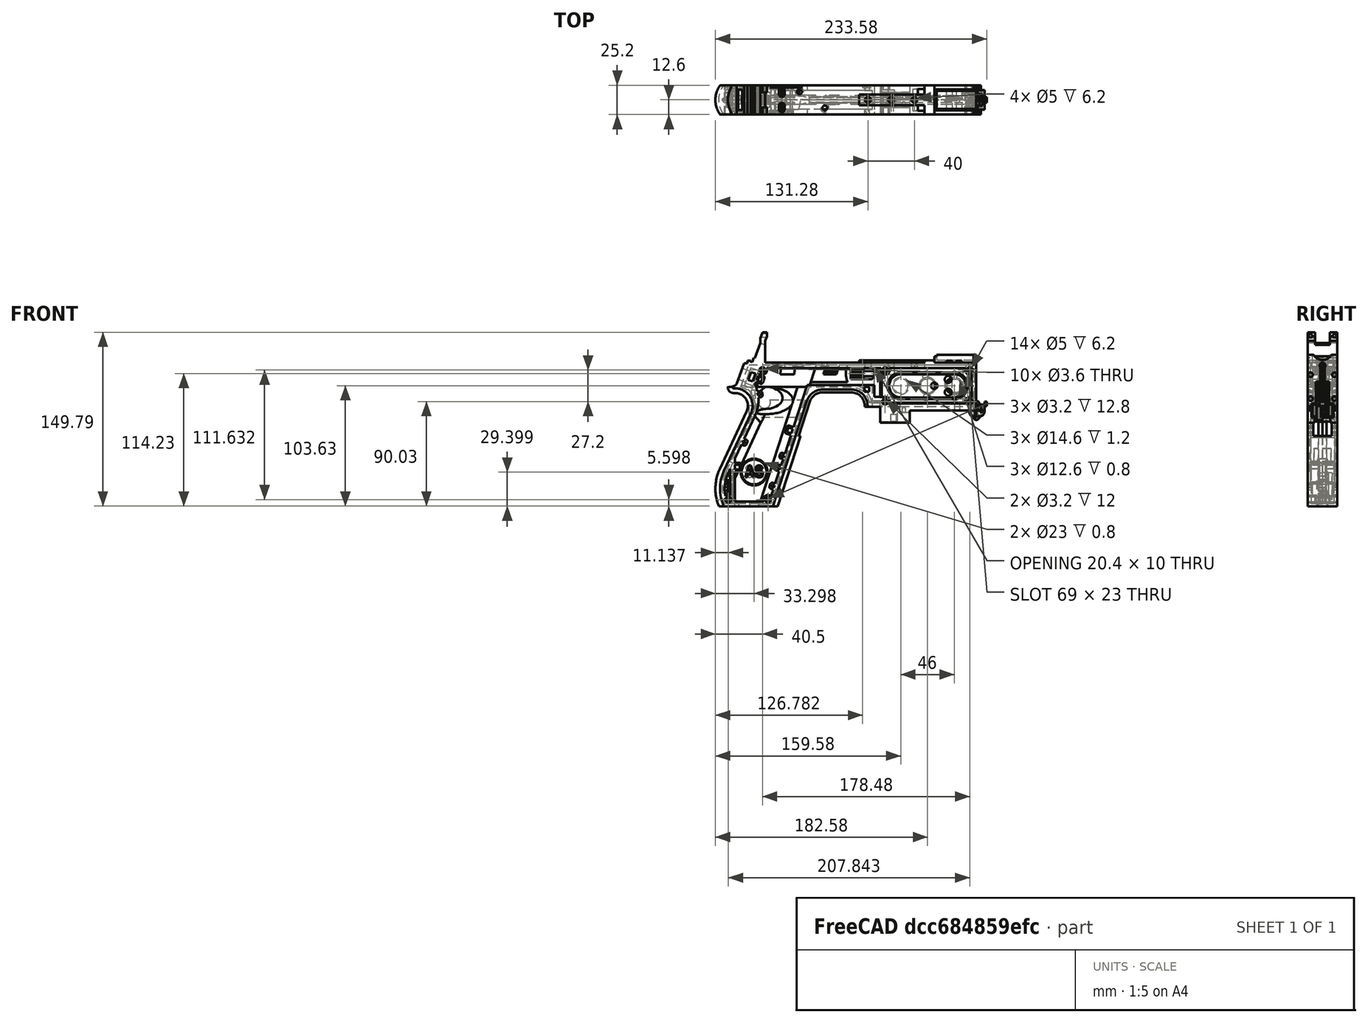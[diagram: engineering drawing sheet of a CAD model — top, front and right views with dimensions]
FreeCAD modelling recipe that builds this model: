
FCSTD DOCUMENT  (FreeCAD 1.0R39319 (Git))
Label: PICON-OF_ver_53
License: All rights reserved
LicenseURL: https://en.wikipedia.org/wiki/All_rights_reserved
objects: Sketcher::SketchObject×124, Part::Extrusion×63, Part::Cut×48, PartDesign::Pad×29, PartDesign::Pocket×21, PartDesign::Chamfer×15, PartDesign::Body×10, PartDesign::Fillet×6, Part::MultiFuse×5, Part::Part2DObjectPython×4, PartDesign::SubtractivePipe×4, PartDesign::SubtractiveLoft×4, PartDesign::Plane×3, PartDesign::SubShapeBinder×2, Part::Sweep×1, PartDesign::ShapeBinder×1, Mesh::Feature×1, PartDesign::Point×1, PartDesign::Groove×1
note: 626 computed .brp shape members not serialized (recipe doc carries the construction recipe); baked Part::Feature solids carry a one-line shape summary decoded from their .brp

FEATURE [Sketcher::SketchObject] Sketch  label="corpo principale"
  ArcFitTolerance = 1e-06
  AttacherType = Attacher::AttachEngine3D
  AttachmentSupport = -> [XZ_Plane]
  FullyConstrained = true
  MakeInternals = false
  MapMode = 5
  Placement = pos=(0,0,0) rot=(1,0,0;1.5708rad)
  sketch-geometry (65):
    g0: LineSegment StartX=0 StartY=0 StartZ=0 EndX=-57.2 EndY=0 EndZ=0
    g1: LineSegment StartX=-57.2 StartY=0 StartZ=0 EndX=-57.2 EndY=-10.4 EndZ=0
    g2: LineSegment StartX=-57.2 StartY=-10.4 StartZ=0 EndX=-82.8 EndY=-10.4 EndZ=0
    g3: LineSegment StartX=-82.8 StartY=-10.4 StartZ=0 EndX=-82.8 EndY=3.2 EndZ=0
    g4: LineSegment StartX=-82.8 StartY=3.2 StartZ=0 EndX=-93.6 EndY=3.2 EndZ=0
    g5: LineSegment StartX=-93.6 StartY=3.2 StartZ=0 EndX=-93.6 EndY=4 EndZ=0
    g6: LineSegment StartX=-107.6 StartY=18 StartZ=0 EndX=-132.428 EndY=18 EndZ=0
    g7: LineSegment StartX=-145.743 StartY=8.32624 StartZ=0 EndX=-175.232 EndY=-82.4316 EndZ=0
    g8: LineSegment StartX=-175.232 StartY=-82.4316 StartZ=0 EndX=-217.232 EndY=-82.4316 EndZ=0
    g9: LineSegment StartX=-217.232 StartY=-52.1862 StartZ=0 EndX=-193.988 EndY=-2.33927 EndZ=0
    g10: LineSegment StartX=-206.196 StartY=23.0857 StartZ=0 EndX=-199.861 EndY=40.4914 EndZ=0
    g11: LineSegment StartX=-199.861 StartY=40.4914 StartZ=0 EndX=-197.061 EndY=40.4914 EndZ=0
    g12: LineSegment StartX=-197.061 StartY=40.4914 StartZ=0 EndX=-197.061 EndY=42.8914 EndZ=0
    g13: LineSegment StartX=-197.061 StartY=42.8914 StartZ=0 EndX=-194.261 EndY=42.8914 EndZ=0
    g14: LineSegment StartX=-194.261 StartY=42.8914 StartZ=0 EndX=-194.535 EndY=42.1397 EndZ=0
    g15: LineSegment StartX=-194.535 StartY=42.1397 StartZ=0 EndX=-193.031 EndY=41.5924 EndZ=0
    g16: LineSegment StartX=-193.031 StartY=41.5924 StartZ=0 EndX=-191.663 EndY=45.3512 EndZ=0
    g17: LineSegment StartX=-191.663 StartY=45.3512 StartZ=0 EndX=-190.536 EndY=44.9408 EndZ=0
    g18: LineSegment StartX=-190.536 StartY=44.9408 StartZ=0 EndX=-185.747 EndY=58.0965 EndZ=0
    g19: LineSegment StartX=-185.747 StartY=58.0965 StartZ=0 EndX=-185.747 EndY=62.0965 EndZ=0
    g20: LineSegment StartX=-185.747 StartY=62.0965 StartZ=0 EndX=-183.832 EndY=67.3588 EndZ=0
    g21: LineSegment StartX=-183.832 StartY=67.3588 StartZ=0 EndX=-180.232 EndY=67.3588 EndZ=0
    g22: LineSegment StartX=-180.232 StartY=67.3588 StartZ=0 EndX=-180.232 EndY=63.7588 EndZ=0
    g23: LineSegment StartX=-180.232 StartY=63.7588 StartZ=0 EndX=-181.6 EndY=60 EndZ=0
    g24: LineSegment StartX=-181.6 StartY=60 StartZ=0 EndX=-181.6 EndY=41.2 EndZ=0
    g25: LineSegment StartX=-181.6 StartY=41.2 StartZ=0 EndX=-100.8 EndY=41.2 EndZ=0
    g26: LineSegment StartX=-36 StartY=43.2 StartZ=0 EndX=-36 EndY=41.2 EndZ=0
    g27: LineSegment StartX=0 StartY=48 StartZ=0 EndX=0 EndY=0 EndZ=0
    g28: LineSegment StartX=-209.901 StartY=19.85 StartZ=0 EndX=-209.901 EndY=20.1 EndZ=0
    g29: LineSegment StartX=-208.001 StartY=22 StartZ=0 EndX=-207.747 EndY=22 EndZ=0
    g30: LineSegment StartX=-207.583 StartY=19 StartZ=0 EndX=-209.051 EndY=19 EndZ=0
    g31: ArcOfCircle CenterX=-208.001 CenterY=20.1 CenterZ=0 NormalX=0 NormalY=0 NormalZ=1 AngleXU=0 Radius=1.9 StartAngle=1.5708 EndAngle=3.14159
    g32: GeomPoint [constr] X=-209.901 Y=22 Z=0
    g33: ArcOfCircle CenterX=-209.051 CenterY=19.85 CenterZ=0 NormalX=0 NormalY=0 NormalZ=1 AngleXU=0 Radius=0.85 StartAngle=3.14159 EndAngle=4.71239
    g34: GeomPoint [constr] X=-209.901 Y=19 Z=0
    g35: ArcOfCircle CenterX=-207.747 CenterY=23.65 CenterZ=0 NormalX=0 NormalY=0 NormalZ=1 AngleXU=0 Radius=1.65 StartAngle=4.71239 EndAngle=5.93412
    g36: GeomPoint [constr] X=-206.591 Y=22 Z=0
    g37: LineSegment StartX=-4 StartY=6 StartZ=0 EndX=-4 EndY=36.4 EndZ=0
    g38: LineSegment StartX=-4 StartY=36.4 StartZ=0 EndX=-185.2 EndY=36.4 EndZ=0
    g39: LineSegment StartX=-185.2 StartY=36.4 StartZ=0 EndX=-190.441 EndY=22 EndZ=0
    g40: LineSegment StartX=-214.575 StartY=-78.4316 StartZ=0 EndX=-178.142 EndY=-78.4316 EndZ=0
    g41: LineSegment StartX=-178.142 StartY=-78.4316 StartZ=0 EndX=-145.51 EndY=22 EndZ=0
    g42: LineSegment StartX=-145.51 StartY=22 StartZ=0 EndX=-87.91 EndY=22 EndZ=0
    g43: LineSegment StartX=-87.91 StartY=22 StartZ=0 EndX=-87.91 EndY=11.6 EndZ=0
    g44: LineSegment StartX=-87.91 StartY=11.6 StartZ=0 EndX=-80.11 EndY=11.6 EndZ=0
    g45: LineSegment StartX=-80.11 StartY=11.6 StartZ=0 EndX=-80.11 EndY=6 EndZ=0
    g46: LineSegment StartX=-80.11 StartY=6 StartZ=0 EndX=-4 EndY=6 EndZ=0
    g47: LineSegment StartX=-190.363 StartY=-4.02975 StartZ=0 EndX=-213.607 EndY=-53.8767 EndZ=0
    g48: ArcOfCircle CenterX=-132.428 CenterY=4 CenterZ=0 NormalX=0 NormalY=0 NormalZ=1 AngleXU=0 Radius=14 StartAngle=1.5708 EndAngle=2.82743
    g49: GeomPoint [constr] X=-142.6 Y=18 Z=0
    g50: ArcOfCircle CenterX=-107.6 CenterY=4 CenterZ=0 NormalX=0 NormalY=0 NormalZ=1 AngleXU=0 Radius=14 StartAngle=0 EndAngle=1.5708
    g51: GeomPoint [constr] X=-93.6 Y=18 Z=0
    g52: ArcOfCircle CenterX=-184.801 CenterY=-67.3089 CenterZ=0 NormalX=0 NormalY=0 NormalZ=1 AngleXU=0 Radius=35.7833 StartAngle=2.70526 EndAngle=3.57792
    g53: ArcOfCircle CenterX=-207.583 CenterY=4 CenterZ=0 NormalX=0 NormalY=0 NormalZ=1 AngleXU=0 Radius=15 StartAngle=5.84685 EndAngle=7.85398
    g54: LineSegment [constr] StartX=-213.607 StartY=-53.8767 StartZ=0 EndX=-217.232 EndY=-52.1862 EndZ=0
    g55: ArcOfCircle CenterX=-184.801 CenterY=-67.3089 CenterZ=0 NormalX=0 NormalY=0 NormalZ=1 AngleXU=0 Radius=31.7833 StartAngle=2.70526 EndAngle=3.49911
    g56: ArcOfCircle CenterX=-218.095 CenterY=8.90192 CenterZ=0 NormalX=0 NormalY=0 NormalZ=1 AngleXU=0 Radius=30.5989 StartAngle=5.84685 EndAngle=6.72553
    g57: LineSegment StartX=-44.6 StartY=43.2 StartZ=0 EndX=-36 EndY=43.2 EndZ=0
    g58: LineSegment StartX=-100.8 StartY=41.2 StartZ=0 EndX=-44.6 EndY=41.2 EndZ=0
    g59: LineSegment StartX=-44.6 StartY=41.2 StartZ=0 EndX=-44.6 EndY=43.2 EndZ=0
    g60: LineSegment StartX=-2.4 StartY=48 StartZ=0 EndX=0 EndY=48 EndZ=0
    g61: LineSegment StartX=-36 StartY=41.2 StartZ=0 EndX=-2.4 EndY=41.2 EndZ=0
    g62: LineSegment StartX=-2.4 StartY=41.2 StartZ=0 EndX=-2.4 EndY=48 EndZ=0
    g63: LineSegment [constr] StartX=-181.6 StartY=36.4 StartZ=0 EndX=-152.209 EndY=36.4 EndZ=0
    g64: LineSegment [constr] StartX=-181.6 StartY=36.4 StartZ=0 EndX=-130.41 EndY=36.4 EndZ=0
  constraints (183):
    c: Coincident(g-1,g0)
    c: PointOnObject(g0,g-1)
    c: Coincident(g0,g1)
    c: Vertical(g1)
    c: Coincident(g1,g2)
    c: Horizontal(g2)
    c: Coincident(g2,g3)
    c: Vertical(g3)
    c: Coincident(g3,g4)
    c: Coincident(g4,g5)
    c: Vertical(g5)
    c: Horizontal(g6)
    c: Coincident(g7,g8)
    c: Horizontal(g8)
    c: Coincident(g10,g11)
    c: Horizontal(g11)
    c: Coincident(g11,g12)
    c: Vertical(g12)
    c: Coincident(g12,g13)
    c: Horizontal(g13)
    c: Coincident(g13,g14)
    c: Coincident(g14,g15)
    c: Coincident(g15,g16)
    c: Coincident(g16,g17)
    c: Coincident(g17,g18)
    c: Coincident(g18,g19)
    c: Vertical(g19)
    c: Coincident(g19,g20)
    c: Coincident(g20,g21)
    c: Horizontal(g21)
    c: Coincident(g21,g22)
    c: Vertical(g22)
    c: Coincident(g22,g23)
    c: Coincident(g23,g24)
    c: Vertical(g24)
    c: Coincident(g24,g25)
    c: Horizontal(g25)
    c: Coincident(g57,g26)
    c: Vertical(g26)
    c: Coincident(g26,g61)
    c: PointOnObject(g60,g-2)
    c: Coincident(g60,g27)
    c: Coincident(g27,g0)
    c: DistanceY(g27,g27) = 48
    c: DistanceY(g1,g1) = 10.4
    c: DistanceX(g0,g0) = 57.2
    c: DistanceX(g2,g2) = 25.6
    c: Horizontal(g4)
    c: DistanceY(g3,g3) = 13.6
    c: DistanceX(g4,g4) = 10.8
    c: DistanceY(g5,g51) = 14.8
    c: DistanceX(g49,g51) = 49
    c: Distance(g7,g49) = 105.6
    c: DistanceX(g61,g60) = 36
    c: DistanceX(g25,g25) = 80.8
    c: DistanceY(g24,g24) = 18.8
    c: DistanceY(g22,g22) = 3.6
    c: Distance(g23) = 4
    c: Angle(g-1,g23) = 1.22173
    c: DistanceX(g21,g21) = 3.6
    c: Distance(g20) = 5.6
    c: Angle(g-1,g20) = 1.22173
    c: DistanceY(g19,g19) = 4
    c: Distance(g18) = 14
    c: Angle(g-1,g18) = 1.22173
    c: Distance(g17) = 1.2
    c: Distance(g16) = 4
    c: Angle(g16) = 1.22173
    c: Perpendicular(g18,g17)
    c: Distance(g15) = 1.6
    c: Perpendicular(g16,g15)
    c: Distance(g14) = 0.8
    c: DistanceX(g13,g13) = 2.8
    c: Perpendicular(g15,g14)
    c: DistanceY(g12,g12) = 2.4
    c: DistanceX(g11,g11) = 2.8
    c: Distance(g9) = 55
    c: Angle(g9,g-1) = 2.00713
    c: Horizontal(g29)
    c: Vertical(g28)
    c: Horizontal(g30)
    c: PointOnObject(g32,g29)
    c: PointOnObject(g32,g28)
    c: Tangent(g29,g31) = 1.5708
    c: Tangent(g28,g31) = 1.5708
    c: PointOnObject(g34,g28)
    c: PointOnObject(g34,g30)
    c: Tangent(g28,g33) = 1.5708
    c: Tangent(g30,g33) = 1.5708
    c: PointOnObject(g36,g29)
    c: PointOnObject(g36,g10)
    c: Tangent(g29,g35) = -1.5708
    c: Tangent(g10,g35) = -1.5708
    c: Angle(g-1,g10) = 1.22173
    c: Radius(g35) = 1.65
    c: Vertical(g37)
    c: Coincident(g37,g38)
    c: Horizontal(g38)
    c: Coincident(g38,g39)
    c: Horizontal(g40)
    c: Coincident(g40,g41)
    c: Coincident(g41,g42)
    c: Horizontal(g42)
    c: Coincident(g42,g43)
    c: Vertical(g43)
    c: Coincident(g43,g44)
    c: Horizontal(g44)
    c: Coincident(g44,g45)
    c: Vertical(g45)
    c: Coincident(g45,g46)
    c: Coincident(g46,g37)
    c: Horizontal(g46)
    c: DistanceY(g0,g37) = 6
    c: DistanceX(g37,g0) = 4
    c: DistanceY(g37,g25) = 4.8
    c: DistanceX(g38,g38) = 181.2
    c: DistanceX(g42,g42) = 57.6
    c: DistanceY(g49,g41) = 4
    c: DistanceX(g41,g49) = 2.91
    c: DistanceY(g43,g43) = 10.4
    c: DistanceX(g44,g44) = 7.8
    c: DistanceY(g7,g40) = 4
    c: Distance(g47) = 55
    c: Angle(g-1,g39) = 1.22173
    c: PointOnObject(g49,g7)
    c: PointOnObject(g49,g6)
    c: Tangent(g7,g48) = -1.5708
    c: Tangent(g6,g48) = -1.5708
    c: PointOnObject(g51,g5)
    c: PointOnObject(g51,g6)
    c: Tangent(g5,g50) = -1.5708
    c: Tangent(g6,g50) = -1.5708
    c: Radius(g50) = 14
    c: Radius(g48) = 14
    c: DistanceX(g8,g8) = 42
    c: Angle(g7,g-1) = 1.88496
    c: Parallel(g41,g7)
    c: Parallel(g47,g9)
    c: Coincident(g52,g8)
    c: Tangent(g52,g9) = 1.5708
    c: DistanceX(g9,g8) = 0
    c: Tangent(g53,g9) = -1.5708
    c: Tangent(g53,g30) = -1.5708
    c: Diameter(g53) = 30
    c: DistanceY(g53,g0) = -4
    c: Coincident(g54,g47)
    c: Distance(g54) = 4
    c: Coincident(g54,g9)
    c: Coincident(g55,g40)
    c: Tangent(g55,g47) = -1.5708
    c: Coincident(g52,g55)
    c: Coincident(g56,g39)
    c: Tangent(g56,g47) = 1.5708
    c: Horizontal(g57)
    c: DistanceX(g57,g57) = 8.6
    c: Coincident(g58,g25)
    c: Horizontal(g58)
    c: Coincident(g59,g58)
    c: Vertical(g59)
    c: DistanceY(g58,g57) = 2
    c: DistanceX(g58,g58) = 56.2
    c: Coincident(g59,g57)
    c: DistanceY(g41,g36) = 0
    c: DistanceY(g36,g39) = 0
    c: DistanceY(g28,g28) = 0.25
    c: DistanceX(g30,g36) = 2.46
    c: DistanceX(g28,g29) = 1.9
    c: Coincident(g62,g60)
    c: Horizontal(g60)
    c: DistanceX(g62,g27) = 2.4
    c: Coincident(g61,g62)
    c: DistanceY(g26,g26) = 2
    c: Vertical(g62)
    c: DistanceY(g61,g60) = 6.8
    c: Horizontal(g61)
    c: Distance(g63) = 29.391
    c: PointOnObject(g63,g38)
    c: PointOnObject(g63,g38)
    c: Distance(g64) = 51.19
    c: PointOnObject(g64,g38)
    c: PointOnObject(g64,g38)
    c: DistanceX(g24,g63) = 0
    c: DistanceX(g24,g64) = 0
FEATURE [Part::Extrusion] Extrude  label="Extrude corpo principale"
  Base = -> Sketch
  Dir = (0,-1,2e-16)
  DirMode = 2
  FaceMakerClass = Part::FaceMakerBullseye
  FaceMakerMode = 3
  LengthFwd = 25.2
  LengthRev = 12.6
  Solid = true
  Symmetric = true
FEATURE [Sketcher::SketchObject] Sketch002  label="scavo grilletto"
  ArcFitTolerance = 1e-06
  AttachmentSupport = -> [XZ_Plane]
  ExternalGeometry = -> [Sketch]
  FullyConstrained = true
  MakeInternals = false
  MapMode = 5
  Placement = pos=(0,0,0) rot=(1,0,0;1.5708rad)
  sketch-geometry (4):
    g0: LineSegment StartX=-89.51 StartY=22 StartZ=0 EndX=-152.71 EndY=22 EndZ=0
    g1: LineSegment StartX=-152.71 StartY=22 StartZ=0 EndX=-167.006 EndY=-22 EndZ=0
    g2: LineSegment StartX=-167.006 StartY=-22 StartZ=0 EndX=-89.51 EndY=-22 EndZ=0
    g3: LineSegment StartX=-89.51 StartY=-22 StartZ=0 EndX=-89.51 EndY=22 EndZ=0
  constraints (12):
    c: Horizontal(g0)
    c: Coincident(g0,g1)
    c: Coincident(g1,g2)
    c: Horizontal(g2)
    c: Coincident(g2,g3)
    c: Coincident(g3,g0)
    c: Vertical(g3)
    c: Angle(g1,g0) = 1.88496
    c: DistanceY(g3,g3) = 44
    c: DistanceX(g0,g0) = 63.2
    c: DistanceX(g0,g-3) = 1.6
    c: DistanceY(g-3,g0) = 0
FEATURE [Sketcher::SketchObject] Sketch004  label="traiettoria arrotondamento impugnatura anteriore"
  ArcFitTolerance = 1e-06
  AttachmentSupport = -> [XZ_Plane]
  ExternalGeometry = -> [Sketch]
  FullyConstrained = true
  MakeInternals = false
  MapMode = 5
  Placement = pos=(0,0,0) rot=(1,0,0;1.5708rad)
  sketch-geometry (13):
    g0: LineSegment StartX=-175.232 StartY=-82.4316 StartZ=0 EndX=-145.743 EndY=8.32624 EndZ=0
    g1: LineSegment StartX=-93.6 StartY=3.2 StartZ=0 EndX=-93.6 EndY=4 EndZ=0
    g2: LineSegment StartX=-132.428 StartY=18 StartZ=0 EndX=-107.6 EndY=18 EndZ=0
    g3: ArcOfCircle CenterX=-132.428 CenterY=4 CenterZ=0 NormalX=0 NormalY=0 NormalZ=1 AngleXU=0 Radius=14 StartAngle=1.5708 EndAngle=2.82743
    g4: ArcOfCircle CenterX=-107.6 CenterY=4 CenterZ=0 NormalX=0 NormalY=0 NormalZ=1 AngleXU=0 Radius=14 StartAngle=0 EndAngle=1.5708
    g5: LineSegment StartX=-175.232 StartY=-82.4316 StartZ=0 EndX=-217.232 EndY=-82.4316 EndZ=0
    g6: LineSegment StartX=-217.232 StartY=-52.1862 StartZ=0 EndX=-193.988 EndY=-2.33927 EndZ=0
    g7: LineSegment StartX=-209.051 StartY=19 StartZ=0 EndX=-207.583 EndY=19 EndZ=0
    g8: LineSegment StartX=-209.901 StartY=20.1 StartZ=0 EndX=-209.901 EndY=19.85 EndZ=0
    g9: ArcOfCircle CenterX=-184.801 CenterY=-67.3089 CenterZ=0 NormalX=0 NormalY=0 NormalZ=1 AngleXU=0 Radius=35.7833 StartAngle=2.70526 EndAngle=3.57792
    g10: ArcOfCircle CenterX=-207.583 CenterY=4 CenterZ=0 NormalX=0 NormalY=0 NormalZ=1 AngleXU=0 Radius=15 StartAngle=5.84685 EndAngle=7.85398
    g11: ArcOfCircle CenterX=-209.051 CenterY=19.85 CenterZ=0 NormalX=0 NormalY=0 NormalZ=1 AngleXU=0 Radius=0.85 StartAngle=3.14159 EndAngle=4.71239
    g12: ArcOfCircle CenterX=-208.001 CenterY=20.1 CenterZ=0 NormalX=0 NormalY=0 NormalZ=1 AngleXU=0 Radius=1.9 StartAngle=1.5708 EndAngle=3.14159
  constraints (26):
    c: Coincident(g0,g-3)
    c: Coincident(g0,g-6)
    c: Coincident(g1,g-8)
    c: Coincident(g1,g-7)
    c: Coincident(g2,g-5)
    c: Coincident(g2,g-4)
    c: Coincident(g3,g2)
    c: Tangent(g3,g0) = 1.5708
    c: Coincident(g4,g1)
    c: Tangent(g4,g2) = 1.5708
    c: Coincident(g5,g0)
    c: Coincident(g5,g-9)
    c: Coincident(g6,g-12)
    c: Coincident(g6,g-11)
    c: Coincident(g7,g-15)
    c: Coincident(g7,g-14)
    c: Coincident(g8,g-16)
    c: Coincident(g8,g-17)
    c: Tangent(g9,g6) = 1.5708
    c: Coincident(g9,g5)
    c: Coincident(g10,g7)
    c: Tangent(g10,g6) = -1.5708
    c: Tangent(g11,g7) = -1.5708
    c: Coincident(g11,g8)
    c: Tangent(g12,g8) = -1.5708
    c: Coincident(g12,g-17)
FEATURE [PartDesign::Plane] DatumPlane  label="Piano per disegno arrotondamento impugnatura"
  AttachmentSupport = -> [Sketch]
  Length = 73.6581
  MapMode = 7
  Placement = pos=(-145.743,1.8e-15,8.32624) rot=(0.154555,0.154555,0.97582;1.59527rad)
  ResizeMode = 0
  Width = 303.511
FEATURE [Sketcher::SketchObject] Sketch005  label="forma arrotondamento impugnatura anteriore"
  ArcFitTolerance = 1e-06
  AttachmentSupport = -> [DatumPlane]
  FullyConstrained = true
  MakeInternals = false
  MapMode = 5
  Placement = pos=(-145.743,1.8e-15,8.32624) rot=(0.154555,0.154555,0.97582;1.59527rad)
  sketch-geometry (5):
    g0: GeomPoint [constr] X=0 Y=-4 Z=0
    g1: GeomPoint [constr] X=-12.6 Y=7.1e-15 Z=0
    g2: GeomPoint [constr] X=12.6 Y=4.97e-14 Z=0
    g3: LineSegment StartX=-12.6 StartY=7.1e-15 StartZ=0 EndX=12.6 EndY=4.97e-14 EndZ=0
    g4: ArcOfCircle CenterX=-3.88e-14 CenterY=17.845 CenterZ=0 NormalX=0 NormalY=0 NormalZ=1 AngleXU=0 Radius=21.845 StartAngle=4.09759 EndAngle=5.32718
  constraints (11):
    c: DistanceY(g0,g-1) = 4
    c: DistanceX(g-1,g0) = 0
    c: DistanceX(g1,g-1) = 12.6
    c: DistanceX(g-1,g2) = 12.6
    c: DistanceY(g-1,g2) = 0
    c: DistanceY(g-1,g1) = 0
    c: Coincident(g3,g1)
    c: Coincident(g3,g2)
    c: Coincident(g4,g1)
    c: Coincident(g4,g2)
    c: PointOnObject(g0,g4)
FEATURE [Part::Sweep] Sweep  label="Sweep impugnatura"
  Frenet = true
  Sections = -> [Sketch005]
  Solid = true
  Spine = -> Sketch [Edge32,Edge33,Edge34,Edge35,Edge36,Edge37,Edge38,Edge39,Edge40,Edge41,Edge42,Edge43,Edge44]
  Transition = 1
FEATURE [Sketcher::SketchObject] Sketch008  label="buchi e pulizie varie"
  ArcFitTolerance = 1e-06
  AttachmentSupport = -> [XZ_Plane]
  ExternalGeometry = -> [Sketch]
  FullyConstrained = true
  MakeInternals = false
  MapMode = 5
  Placement = pos=(0,0,0) rot=(1,0,0;1.5708rad)
  sketch-geometry (26):
    g0: LineSegment StartX=-96.278 StartY=20.155 StartZ=0 EndX=-92.278 EndY=20.155 EndZ=0
    g1: LineSegment StartX=-92.278 StartY=20.155 StartZ=0 EndX=-92.278 EndY=16.155 EndZ=0
    g2: LineSegment StartX=-92.278 StartY=16.155 StartZ=0 EndX=-96.278 EndY=16.155 EndZ=0
    g3: LineSegment StartX=-96.278 StartY=16.155 StartZ=0 EndX=-96.278 EndY=20.155 EndZ=0
    g4: LineSegment StartX=-222.232 StartY=-82.4316 StartZ=0 EndX=-170.232 EndY=-82.4316 EndZ=0
    g5: LineSegment StartX=-170.232 StartY=-82.4316 StartZ=0 EndX=-170.232 EndY=-86.4316 EndZ=0
    g6: LineSegment StartX=-170.232 StartY=-86.4316 StartZ=0 EndX=-222.232 EndY=-86.4316 EndZ=0
    g7: LineSegment StartX=-222.232 StartY=-86.4316 StartZ=0 EndX=-222.232 EndY=-82.4316 EndZ=0
    g8: LineSegment StartX=-213.901 StartY=20.1 StartZ=0 EndX=-213.901 EndY=26 EndZ=0
    g9: LineSegment StartX=-213.901 StartY=26 StartZ=0 EndX=-206.196 EndY=26 EndZ=0
    g10: LineSegment StartX=-17.4 StartY=42.8 StartZ=0 EndX=-12.4 EndY=42.8 EndZ=0
    g11: LineSegment StartX=-12.4 StartY=42.8 StartZ=0 EndX=-12.4 EndY=41.2 EndZ=0
    g12: LineSegment StartX=-12.4 StartY=41.2 StartZ=0 EndX=-17.4 EndY=41.2 EndZ=0
    g13: LineSegment StartX=-17.4 StartY=41.2 StartZ=0 EndX=-17.4 EndY=42.8 EndZ=0
    g14: LineSegment StartX=-25.9 StartY=42.8 StartZ=0 EndX=-20.9 EndY=42.8 EndZ=0
    g15: LineSegment StartX=-20.9 StartY=42.8 StartZ=0 EndX=-20.9 EndY=41.2 EndZ=0
    g16: LineSegment StartX=-20.9 StartY=41.2 StartZ=0 EndX=-25.9 EndY=41.2 EndZ=0
    g17: LineSegment StartX=-25.9 StartY=41.2 StartZ=0 EndX=-25.9 EndY=42.8 EndZ=0
    g18: GeomPoint [constr] X=-206.196 Y=23.0857 Z=0
    g19: GeomPoint [constr] X=-213.901 Y=20.1 Z=0
    g20: BSplineCurve PolesCount=4 KnotsCount=2 Degree=3 IsPeriodic=0
    g21-g24: Circle [constr] x4 (B-spline internal-alignment scaffolding for g20; pole/knot coordinates omitted)
    g25: LineSegment StartX=-206.196 StartY=26 StartZ=0 EndX=-206.196 EndY=23.0857 EndZ=0
  constraints (73):
    c: Horizontal(g0)
    c: Coincident(g1,g0)
    c: Vertical(g1)
    c: Coincident(g2,g1)
    c: Horizontal(g2)
    c: Coincident(g3,g2)
    c: Coincident(g3,g0)
    c: Vertical(g3)
    c: DistanceX(g0,g-4) = 4.368
    c: DistanceY(g0,g-4) = 1.845
    c: DistanceY(g1,g1) = 4
    c: DistanceX(g2,g2) = 4
    c: Horizontal(g4)
    c: Coincident(g5,g4)
    c: Vertical(g5)
    c: Coincident(g6,g5)
    c: Horizontal(g6)
    c: Coincident(g7,g6)
    c: Coincident(g7,g4)
    c: Vertical(g7)
    c: DistanceY(g7,g7) = 4
    c: DistanceX(g4,g-5) = 5
    c: DistanceX(g-5,g4) = 5
    c: DistanceY(g4,g-5) = 0
    c: Coincident(g9,g8)
    c: Parallel(g9,g-6)
    c: DistanceX(g8,g-8) = 4
    c: Horizontal(g10)
    c: Coincident(g11,g10)
    c: Vertical(g11)
    c: Coincident(g12,g11)
    c: Horizontal(g12)
    c: Coincident(g13,g12)
    c: Coincident(g13,g10)
    c: Vertical(g13)
    c: Horizontal(g14)
    c: Coincident(g15,g14)
    c: Vertical(g15)
    c: Coincident(g16,g15)
    c: Horizontal(g16)
    c: Coincident(g17,g16)
    c: Coincident(g17,g14)
    c: Vertical(g17)
    c: DistanceY(g11,g10) = 1.6
    c: DistanceX(g10,g10) = 5
    c: DistanceY(g15,g14) = 1.6
    c: DistanceX(g14,g14) = 5
    c: DistanceX(g15,g12) = 3.5
    c: DistanceX(g11,g-9) = 10
    c: DistanceY(g-9,g11) = 0
    c: DistanceY(g-9,g15) = 0
    c: Perpendicular(g8,g9)
    c: DistanceY(g-7,g9) = 4
    c: DistanceY(g8,g-8) = 0
    c: InternalAlignment(g18,g20)
    c: InternalAlignment(g19,g20)
    c: InternalAlignment(g21,g20)
    c: Weight(g21) = 1
    c: InternalAlignment(g22,g20)
    c: Equal(g22,g21)
    c: InternalAlignment(g23,g20)
    c: Equal(g23,g21)
    c: InternalAlignment(g24,g20)
    c: Equal(g24,g21)
    c: Coincident(g18,g-12)
    c: Coincident(g19,g8)
    c: Coincident(g25,g9)
    c: Coincident(g25,g20)
    c: Vertical(g25)
    c: DistanceY(g20,g23) = 0
    c: DistanceY(g22,g18) = 2.26
    c: DistanceX(g22,g18) = 0.93
    c: DistanceX(g20,g23) = 2.9
FEATURE [Part::Extrusion] Extrude004  label="Extrude Buchi e pulizie varie"
  Base = -> Sketch008
  Dir = (0,-1,2e-16)
  DirMode = 2
  FaceMakerClass = Part::FaceMakerBullseye
  FaceMakerMode = 3
  LengthFwd = 25.2
  LengthRev = 0
  Solid = true
  Symmetric = true
FEATURE [Sketcher::SketchObject] Sketch009  label="rinforzi"
  ArcFitTolerance = 1e-06
  AttachmentSupport = -> [XZ_Plane]
  ExternalGeometry = -> [Sketch]
  FullyConstrained = true
  MakeInternals = false
  MapMode = 5
  Placement = pos=(0,0,0) rot=(1,0,0;1.5708rad)
  sketch-geometry (9):
    g0: LineSegment StartX=-87.91 StartY=22 StartZ=0 EndX=-87.91 EndY=36.4 EndZ=0
    g1: LineSegment StartX=-87.91 StartY=36.4 StartZ=0 EndX=-97.91 EndY=36.4 EndZ=0
    g2: LineSegment StartX=-97.91 StartY=36.4 StartZ=0 EndX=-97.91 EndY=22 EndZ=0
    g3: LineSegment StartX=-97.91 StartY=22 StartZ=0 EndX=-87.91 EndY=22 EndZ=0
    g4: LineSegment StartX=-149.713 StartY=9.06563 StartZ=0 EndX=-154.586 EndY=-5.93437 EndZ=0
    g5: LineSegment StartX=-154.586 StartY=-5.93437 StartZ=0 EndX=-191.863 EndY=-5.93437 EndZ=0
    g6: LineSegment StartX=-191.863 StartY=-5.93437 StartZ=0 EndX=-191.863 EndY=9.06563 EndZ=0
    g7: LineSegment StartX=-191.863 StartY=9.06563 StartZ=0 EndX=-149.713 EndY=9.06563 EndZ=0
    g8: LineSegment [constr] StartX=-145.51 StartY=22 StartZ=0 EndX=-149.713 EndY=9.06563 EndZ=0
  constraints (25):
    c: Vertical(g0)
    c: Coincident(g1,g0)
    c: Horizontal(g1)
    c: Coincident(g2,g1)
    c: Vertical(g2)
    c: Coincident(g3,g2)
    c: Coincident(g3,g0)
    c: Horizontal(g3)
    c: Coincident(g0,g-4)
    c: DistanceX(g3,g3) = 10
    c: DistanceY(g0,g-3) = 0
    c: Coincident(g5,g4)
    c: Horizontal(g5)
    c: Coincident(g6,g5)
    c: Vertical(g6)
    c: Coincident(g7,g6)
    c: Coincident(g7,g4)
    c: Horizontal(g7)
    c: Distance(g8) = 13.6
    c: Parallel(g-6,g8)
    c: Coincident(g-6,g8)
    c: Parallel(g4,g-6)
    c: DistanceY(g4,g4) = 15
    c: Coincident(g4,g8)
    c: DistanceX(g-5,g5) = -1.5
FEATURE [Part::Extrusion] Extrude001  label="Extrude scavo grilletto"
  Base = -> Sketch002
  Dir = (0,-1,2e-16)
  DirMode = 2
  FaceMakerClass = Part::FaceMakerBullseye
  FaceMakerMode = 3
  LengthFwd = 16
  LengthRev = 0
  Solid = true
  Symmetric = true
FEATURE [Part::Extrusion] Extrude005  label="Extrude Rinforzi"
  Base = -> Sketch009
  Dir = (0,-1,2e-16)
  DirMode = 2
  FaceMakerClass = Part::FaceMakerBullseye
  FaceMakerMode = 3
  LengthFwd = 2
  LengthRev = 0
  Placement = pos=(0,12.6,0) rot=(0,0,1;0rad)
  Solid = true
  Symmetric = false
FEATURE [PartDesign::ShapeBinder] CopyCut
  TraceSupport = false
FEATURE [PartDesign::Plane] DatumPlane001
  AttachmentSupport = -> [CopyCut]
  Length = 283.944
  MapMode = 5
  Placement = pos=(0,12.6,0) rot=(0,0.707107,0.707107;3.14159rad)
  ResizeMode = 0
  Width = 188.15
FEATURE [Sketcher::SketchObject] Sketch010  label="buco neopixel"
  ArcFitTolerance = 1e-06
  AttachmentSupport = -> [XZ_Plane]
  ExternalGeometry = -> [Sketch]
  FullyConstrained = true
  MakeInternals = false
  MapMode = 5
  Placement = pos=(0,0,0) rot=(1,0,0;1.5708rad)
  sketch-geometry (5):
    g0: LineSegment [constr] StartX=-199.861 StartY=40.4914 StartZ=0 EndX=-201.368 EndY=36.3521 EndZ=0
    g1: LineSegment StartX=-201.368 StartY=36.3521 StartZ=0 EndX=-204.932 EndY=26.5605 EndZ=0
    g2: LineSegment StartX=-201.368 StartY=36.3521 StartZ=0 EndX=-180.2 EndY=28.6477 EndZ=0
    g3: LineSegment StartX=-180.2 StartY=28.6477 StartZ=0 EndX=-183.764 EndY=18.8561 EndZ=0
    g4: LineSegment StartX=-183.764 StartY=18.8561 StartZ=0 EndX=-204.932 EndY=26.5605 EndZ=0
  constraints (14):
    c: Parallel(g0,g-3)
    c: Distance(g0) = 4.405
    c: Coincident(g0,g-3)
    c: Coincident(g2,g1)
    c: Coincident(g3,g2)
    c: Coincident(g4,g3)
    c: Coincident(g4,g1)
    c: Parallel(g1,g-3)
    c: Distance(g1) = 10.42
    c: Coincident(g1,g0)
    c: Parallel(g2,g4)
    c: Perpendicular(g1,g2)
    c: DistanceX(g-4,g2) = 5
    c: Parallel(g3,g1)
FEATURE [Part::Extrusion] Extrude006  label="Extrude buco neopixel"
  Base = -> Sketch010
  Dir = (0,-1,2e-16)
  DirMode = 2
  FaceMakerClass = Part::FaceMakerBullseye
  FaceMakerMode = 3
  LengthFwd = 17.2
  LengthRev = 0
  Solid = true
  Symmetric = true
FEATURE [Sketcher::SketchObject] Sketch011  label="fermo grilletto"
  ArcFitTolerance = 1e-06
  AttachmentSupport = -> [XZ_Plane]
  ExternalGeometry = -> [Sketch]
  FullyConstrained = true
  MakeInternals = false
  MapMode = 5
  Placement = pos=(0,0,0) rot=(1,0,0;1.5708rad)
  sketch-geometry (18):
    g0: LineSegment [constr] StartX=-145.51 StartY=22 StartZ=0 EndX=-157.347 EndY=-14.4293 EndZ=0
    g1: LineSegment [constr] StartX=-157.347 StartY=-14.4293 StartZ=0 EndX=-157.841 EndY=-15.951 EndZ=0
    g2: LineSegment StartX=-161.151 StartY=-13.1932 StartZ=0 EndX=-155.825 EndY=-14.9237 EndZ=0
    g3: LineSegment StartX=-163.167 StartY=-14.2205 StartZ=0 EndX=-164.403 EndY=-18.0247 EndZ=0
    g4: LineSegment StartX=-163.376 StartY=-20.0408 StartZ=0 EndX=-158.05 EndY=-21.7713 EndZ=0
    g5: LineSegment StartX=-158.05 StartY=-21.7713 StartZ=0 EndX=-155.825 EndY=-14.9237 EndZ=0
    g6: LineSegment StartX=-161.645 StartY=-14.7149 StartZ=0 EndX=-157.841 EndY=-15.951 EndZ=0
    g7: LineSegment StartX=-157.841 StartY=-15.951 StartZ=0 EndX=-159.077 EndY=-19.7552 EndZ=0
    g8: LineSegment StartX=-159.077 StartY=-19.7552 StartZ=0 EndX=-162.881 EndY=-18.5191 EndZ=0
    g9: LineSegment StartX=-162.881 StartY=-18.5191 StartZ=0 EndX=-161.645 EndY=-14.7149 EndZ=0
    g10: LineSegment [constr] StartX=-161.645 StartY=-14.7149 StartZ=0 EndX=-161.151 EndY=-13.1932 EndZ=0
    g11: LineSegment [constr] StartX=-159.077 StartY=-19.7552 StartZ=0 EndX=-157.555 EndY=-20.2496 EndZ=0
    g12: LineSegment [constr] StartX=-159.077 StartY=-19.7552 StartZ=0 EndX=-159.572 EndY=-21.2769 EndZ=0
    g13: LineSegment [constr] StartX=-161.645 StartY=-14.7149 StartZ=0 EndX=-163.167 EndY=-14.2205 EndZ=0
    g14: ArcOfCircle CenterX=-161.645 CenterY=-14.7149 CenterZ=0 NormalX=0 NormalY=0 NormalZ=1 AngleXU=0 Radius=1.6 StartAngle=1.25664 EndAngle=2.82743
    g15: GeomPoint [constr] X=-162.673 Y=-12.6988 Z=0
    g16: ArcOfCircle CenterX=-162.881 CenterY=-18.5191 CenterZ=0 NormalX=0 NormalY=0 NormalZ=1 AngleXU=0 Radius=1.6 StartAngle=2.82743 EndAngle=4.39823
    g17: GeomPoint [constr] X=-164.897 Y=-19.5464 Z=0
  constraints (48):
    c: Parallel(g0,g-3)
    c: Distance(g0) = 38.304
    c: Coincident(g0,g-3)
    c: Parallel(g1,g-3)
    c: Distance(g1) = 1.6
    c: Coincident(g1,g0)
    c: Coincident(g5,g4)
    c: Coincident(g5,g2)
    c: Coincident(g7,g6)
    c: Coincident(g8,g7)
    c: Coincident(g9,g8)
    c: Coincident(g9,g6)
    c: Parallel(g7,g-3)
    c: Parallel(g9,g7)
    c: Perpendicular(g6,g7)
    c: Parallel(g6,g8)
    c: Distance(g6) = 4
    c: Distance(g9) = 4
    c: Parallel(g5,g7)
    c: Parallel(g9,g3)
    c: Parallel(g2,g6)
    c: Parallel(g4,g8)
    c: Parallel(g13,g6)
    c: Parallel(g10,g9)
    c: Parallel(g11,g8)
    c: Parallel(g12,g7)
    c: Distance(g10) = 1.6
    c: Distance(g13) = 1.6
    c: Distance(g12) = 1.6
    c: Distance(g11) = 1.6
    c: Coincident(g10,g6)
    c: Coincident(g13,g6)
    c: Coincident(g12,g7)
    c: Coincident(g11,g7)
    c: Distance(g10,g15) = 1.6
    c: Distance(g15,g13) = 1.6
    c: Distance(g4,g12) = 1.6
    c: Distance(g4,g11) = 1.6
    c: PointOnObject(g15,g2)
    c: Tangent(g3,g14) = -1.5708
    c: Tangent(g2,g14) = 1.5708
    c: PointOnObject(g17,g4)
    c: PointOnObject(g17,g3)
    c: Tangent(g4,g16) = -1.5708
    c: Tangent(g3,g16) = -1.5708
    c: Equal(g16,g14)
    c: Coincident(g16,g8)
    c: Coincident(g6,g1)
FEATURE [Part::Extrusion] Extrude007  label="Extrude fermo grilletto"
  Base = -> Sketch011
  Dir = (0,-1,2e-16)
  DirMode = 2
  FaceMakerClass = Part::FaceMakerBullseye
  FaceMakerMode = 3
  LengthFwd = 25.2
  LengthRev = 0
  Solid = true
  Symmetric = true
FEATURE [Sketcher::SketchObject] Sketch012  label="buco oled"
  ArcFitTolerance = 1e-06
  AttachmentSupport = -> [XZ_Plane]
  ExternalGeometry = -> [Sketch]
  FullyConstrained = true
  MakeInternals = false
  MapMode = 5
  Placement = pos=(0,0,0) rot=(1,0,0;1.5708rad)
  sketch-geometry (4):
    g0: LineSegment StartX=-185.747 StartY=58.0965 StartZ=0 EndX=-180.232 EndY=56.0891 EndZ=0
    g1: LineSegment StartX=-185.747 StartY=58.0965 StartZ=0 EndX=-185.747 EndY=67.3588 EndZ=0
    g2: LineSegment StartX=-185.747 StartY=67.3588 StartZ=0 EndX=-180.232 EndY=67.3588 EndZ=0
    g3: LineSegment StartX=-180.232 StartY=67.3588 StartZ=0 EndX=-180.232 EndY=56.0891 EndZ=0
  constraints (10):
    c: Coincident(g1,g0)
    c: Coincident(g2,g1)
    c: Coincident(g3,g2)
    c: Coincident(g3,g0)
    c: Parallel(g1,g-5)
    c: Perpendicular(g-3,g0)
    c: Parallel(g2,g-6)
    c: Parallel(g3,g-4)
    c: Coincident(g0,g-5)
    c: Coincident(g2,g-6)
FEATURE [Part::Extrusion] Extrude008  label="Extrude buco oled"
  Base = -> Sketch012
  Dir = (0,-1,2e-16)
  DirMode = 2
  FaceMakerClass = Part::FaceMakerBullseye
  FaceMakerMode = 3
  LengthFwd = 12.8
  LengthRev = 0
  Solid = true
  Symmetric = true
FEATURE [Sketcher::SketchObject] Sketch013  label="buco pompa"
  ArcFitTolerance = 1e-06
  AttachmentSupport = -> [XZ_Plane]
  ExternalGeometry = -> [Sketch]
  FullyConstrained = true
  MakeInternals = false
  MapMode = 5
  Placement = pos=(0,0,0) rot=(1,0,0;1.5708rad)
  sketch-geometry (8):
    g0: LineSegment StartX=-82.8 StartY=-10.4 StartZ=0 EndX=-82.8 EndY=-9.6 EndZ=0
    g1: LineSegment StartX=-82.8 StartY=-9.6 StartZ=0 EndX=-67.9 EndY=-9.6 EndZ=0
    g2: LineSegment StartX=-67.9 StartY=-9.6 StartZ=0 EndX=-67.9 EndY=6 EndZ=0
    g3: LineSegment StartX=-67.9 StartY=6 StartZ=0 EndX=-65.9 EndY=6 EndZ=0
    g4: LineSegment StartX=-65.9 StartY=6 StartZ=0 EndX=-65.9 EndY=-1.7 EndZ=0
    g5: LineSegment StartX=-65.9 StartY=-1.7 StartZ=0 EndX=-57.2 EndY=-1.7 EndZ=0
    g6: LineSegment StartX=-57.2 StartY=-1.7 StartZ=0 EndX=-57.2 EndY=-10.4 EndZ=0
    g7: LineSegment StartX=-57.2 StartY=-10.4 StartZ=0 EndX=-82.8 EndY=-10.4 EndZ=0
  constraints (22):
    c: Vertical(g0)
    c: Coincident(g1,g0)
    c: Horizontal(g1)
    c: Coincident(g2,g1)
    c: Vertical(g2)
    c: Coincident(g3,g2)
    c: Horizontal(g3)
    c: Coincident(g4,g3)
    c: Vertical(g4)
    c: Coincident(g5,g4)
    c: Horizontal(g5)
    c: Coincident(g6,g5)
    c: Vertical(g6)
    c: Coincident(g7,g6)
    c: Coincident(g7,g0)
    c: DistanceY(g0,g0) = 0.8
    c: DistanceY(g6,g6) = 8.7
    c: DistanceX(g1,g1) = 14.9
    c: DistanceX(g3,g3) = 2
    c: Coincident(g0,g-4)
    c: DistanceY(g2,g-6) = 0
    c: Coincident(g6,g-5)
FEATURE [Part::Extrusion] Extrude009  label="Extrude buco pompa"
  Base = -> Sketch013
  Dir = (0,-1,2e-16)
  DirMode = 2
  FaceMakerClass = Part::FaceMakerBullseye
  FaceMakerMode = 3
  LengthFwd = 13.2
  LengthRev = 0
  Solid = true
  Symmetric = true
FEATURE [Sketcher::SketchObject] Sketch014  label="buco frontale"
  ArcFitTolerance = 1e-06
  AttachmentSupport = -> [XZ_Plane]
  ExternalGeometry = -> [Sketch]
  FullyConstrained = true
  MakeInternals = false
  MapMode = 5
  Placement = pos=(0,0,0) rot=(1,0,0;1.5708rad)
  sketch-geometry (10):
    g0: LineSegment StartX=0 StartY=0 StartZ=0 EndX=0 EndY=24.671 EndZ=0
    g1: LineSegment StartX=0 StartY=24.671 StartZ=0 EndX=-4 EndY=24.671 EndZ=0
    g2: LineSegment StartX=-4 StartY=24.671 StartZ=0 EndX=-4 EndY=16 EndZ=0
    g3: LineSegment StartX=-4 StartY=16 StartZ=0 EndX=-2.4 EndY=16 EndZ=0
    g4: LineSegment StartX=-2.4 StartY=16 StartZ=0 EndX=-2.4 EndY=10 EndZ=0
    g5: LineSegment StartX=-2.4 StartY=10 StartZ=0 EndX=-12 EndY=10 EndZ=0
    g6: LineSegment StartX=-12 StartY=10 StartZ=0 EndX=-12 EndY=6 EndZ=0
    g7: LineSegment StartX=-12 StartY=6 StartZ=0 EndX=-2.4 EndY=6 EndZ=0
    g8: LineSegment StartX=-2.4 StartY=6 StartZ=0 EndX=-2.4 EndY=0 EndZ=0
    g9: LineSegment StartX=-2.4 StartY=0 StartZ=0 EndX=0 EndY=0 EndZ=0
  constraints (29):
    c: Vertical(g0)
    c: Coincident(g1,g0)
    c: Horizontal(g1)
    c: Coincident(g2,g1)
    c: Vertical(g2)
    c: Coincident(g3,g2)
    c: Horizontal(g3)
    c: Coincident(g4,g3)
    c: Vertical(g4)
    c: Coincident(g5,g4)
    c: Horizontal(g5)
    c: Coincident(g6,g5)
    c: Vertical(g6)
    c: Coincident(g7,g6)
    c: Coincident(g8,g7)
    c: Vertical(g8)
    c: Coincident(g9,g8)
    c: Coincident(g9,g0)
    c: Horizontal(g9)
    c: DistanceY(g0,g0) = 24.671
    c: Horizontal(g7)
    c: DistanceY(g6,g6) = 4
    c: DistanceY(g4,g4) = 6
    c: DistanceX(g9,g9) = 2.4
    c: Coincident(g0,g-1)
    c: DistanceY(g-3,g7) = 0
    c: DistanceX(g8,g4) = 0
    c: DistanceX(g-3,g1) = 0
    c: DistanceX(g6,g-3) = 8
FEATURE [Part::Extrusion] Extrude010  label="Extrude buco frontale"
  Base = -> Sketch014
  Dir = (0,-1,2e-16)
  DirMode = 2
  FaceMakerClass = Part::FaceMakerBullseye
  FaceMakerMode = 3
  LengthFwd = 11.2
  LengthRev = 0
  Solid = true
  Symmetric = true
FEATURE [Sketcher::SketchObject] Sketch015  label="guida rail"
  ArcFitTolerance = 1e-06
  AttachmentSupport = -> [XZ_Plane]
  ExternalGeometry = -> [Sketch]
  FullyConstrained = true
  MakeInternals = false
  MapMode = 5
  Placement = pos=(0,0,0) rot=(1,0,0;1.5708rad)
  sketch-geometry (4):
    g0: LineSegment StartX=-100.8 StartY=43.2 StartZ=0 EndX=-44.6 EndY=43.2 EndZ=0
    g1: LineSegment StartX=-44.6 StartY=43.2 StartZ=0 EndX=-44.6 EndY=41.2 EndZ=0
    g2: LineSegment StartX=-44.6 StartY=41.2 StartZ=0 EndX=-100.8 EndY=41.2 EndZ=0
    g3: LineSegment StartX=-100.8 StartY=41.2 StartZ=0 EndX=-100.8 EndY=43.2 EndZ=0
  constraints (9):
    c: Horizontal(g0)
    c: Coincident(g1,g0)
    c: Coincident(g2,g1)
    c: Coincident(g3,g2)
    c: Coincident(g3,g0)
    c: Vertical(g3)
    c: Coincident(g2,g-3)
    c: Coincident(g1,g-3)
    c: Coincident(g0,g-4)
FEATURE [Part::Extrusion] Extrude011  label="Extrude guida rail"
  Base = -> Sketch015
  Dir = (0,-1,2e-16)
  DirMode = 2
  FaceMakerClass = Part::FaceMakerBullseye
  FaceMakerMode = 3
  LengthFwd = 9
  LengthRev = 0
  Solid = true
  Symmetric = true
FEATURE [Sketcher::SketchObject] Sketch016  label="guide per coperture laterali"
  ArcFitTolerance = 1e-06
  AttachmentSupport = -> [XZ_Plane]
  ExternalGeometry = -> [Sketch]
  FullyConstrained = true
  MakeInternals = false
  MapMode = 5
  Placement = pos=(0,0,0) rot=(1,0,0;1.5708rad)
  sketch-geometry (14):
    g0: Circle CenterX=-5.6 CenterY=7.6 CenterZ=0 NormalX=0 NormalY=0 NormalZ=1 AngleXU=0 Radius=1.6
    g1: Circle CenterX=-5.6 CenterY=7.6 CenterZ=0 NormalX=0 NormalY=0 NormalZ=1 AngleXU=0 Radius=4
    g2: Circle CenterX=-5.6 CenterY=34.8 CenterZ=0 NormalX=0 NormalY=0 NormalZ=1 AngleXU=0 Radius=1.6
    g3: Circle CenterX=-5.6 CenterY=34.8 CenterZ=0 NormalX=0 NormalY=0 NormalZ=1 AngleXU=0 Radius=4
    g4: Circle CenterX=-184.08 CenterY=34.8 CenterZ=0 NormalX=0 NormalY=0 NormalZ=1 AngleXU=0 Radius=1.6
    g5: Circle CenterX=-184.08 CenterY=34.8 CenterZ=0 NormalX=0 NormalY=0 NormalZ=1 AngleXU=0 Radius=4
    g6: Circle CenterX=-179.305 CenterY=-76.8316 CenterZ=0 NormalX=0 NormalY=0 NormalZ=1 AngleXU=0 Radius=1.6
    g7: Circle CenterX=-179.305 CenterY=-76.8316 CenterZ=0 NormalX=0 NormalY=0 NormalZ=1 AngleXU=0 Radius=4
    g8: Circle CenterX=-213.443 CenterY=-76.8316 CenterZ=0 NormalX=0 NormalY=0 NormalZ=1 AngleXU=0 Radius=1.6
    g9: Circle CenterX=-213.443 CenterY=-76.8316 CenterZ=0 NormalX=0 NormalY=0 NormalZ=1 AngleXU=0 Radius=4
    g10: Circle CenterX=-78.51 CenterY=7.6 CenterZ=0 NormalX=0 NormalY=0 NormalZ=1 AngleXU=0 Radius=1.6
    g11: Circle CenterX=-78.51 CenterY=7.6 CenterZ=0 NormalX=0 NormalY=0 NormalZ=1 AngleXU=0 Radius=4
    g12: Circle CenterX=-78.51 CenterY=34.8 CenterZ=0 NormalX=0 NormalY=0 NormalZ=1 AngleXU=0 Radius=1.6
    g13: Circle CenterX=-78.51 CenterY=34.8 CenterZ=0 NormalX=0 NormalY=0 NormalZ=1 AngleXU=0 Radius=4
  constraints (35):
    c: Diameter(g0) = 3.2
    c: Diameter(g1) = 8
    c: Coincident(g0,g1)
    c: Diameter(g2) = 3.2
    c: Diameter(g3) = 8
    c: Coincident(g3,g2)
    c: Tangent(g2,g-7)
    c: Diameter(g4) = 3.2
    c: Diameter(g5) = 8
    c: Coincident(g5,g4)
    c: Tangent(g4,g-7)
    c: Tangent(g4,g-8)
    c: Diameter(g6) = 3.2
    c: Diameter(g7) = 8
    c: Coincident(g7,g6)
    c: Tangent(g6,g-9)
    c: Tangent(g6,g-10)
    c: Diameter(g8) = 3.2
    c: Diameter(g9) = 8
    c: Coincident(g9,g8)
    c: Tangent(g8,g-10)
    c: Tangent(g8,g-11)
    c: Diameter(g10) = 3.2
    c: Diameter(g11) = 8
    c: Diameter(g12) = 3.2
    c: Diameter(g13) = 8
    c: Coincident(g12,g13)
    c: Coincident(g10,g11)
    c: Tangent(g12,g-7)
    c: DistanceX(g12,g10) = 0
    c: Tangent(g2,g-6)
    c: Tangent(g0,g-6)
    c: Tangent(g0,g-3)
    c: Tangent(g10,g-3)
    c: Tangent(g10,g-4)
FEATURE [Part::Extrusion] Extrude012  label="extrude guide per coperture laterali"
  Base = -> Sketch016
  Dir = (0,-1,2e-16)
  DirMode = 2
  FaceMakerClass = Part::FaceMakerBullseye
  FaceMakerMode = 3
  LengthFwd = 25.2
  LengthRev = 0
  Solid = true
  Symmetric = true
FEATURE [Sketcher::SketchObject] Sketch017  label="supporto CAM"
  ArcFitTolerance = 1e-06
  AttachmentSupport = -> [XZ_Plane]
  ExternalGeometry = -> [Sketch]
  FullyConstrained = true
  MakeInternals = false
  MapMode = 5
  Placement = pos=(0,0,0) rot=(1,0,0;1.5708rad)
  sketch-geometry (6):
    g0: LineSegment StartX=-2.4 StartY=48 StartZ=0 EndX=-2.4 EndY=41.2 EndZ=0
    g1: LineSegment StartX=-2.4 StartY=48 StartZ=0 EndX=-34 EndY=48 EndZ=0
    g2: LineSegment StartX=-34 StartY=48 StartZ=0 EndX=-34 EndY=46.72 EndZ=0
    g3: LineSegment StartX=-34 StartY=46.72 StartZ=0 EndX=-36 EndY=46.72 EndZ=0
    g4: LineSegment StartX=-36 StartY=46.72 StartZ=0 EndX=-36 EndY=41.2 EndZ=0
    g5: LineSegment StartX=-36 StartY=41.2 StartZ=0 EndX=-2.4 EndY=41.2 EndZ=0
  constraints (15):
    c: Coincident(g1,g0)
    c: Horizontal(g1)
    c: Coincident(g2,g1)
    c: Vertical(g2)
    c: Coincident(g3,g2)
    c: Horizontal(g3)
    c: Coincident(g4,g3)
    c: Coincident(g5,g4)
    c: DistanceX(g1,g0) = 31.6
    c: Coincident(g5,g0)
    c: Vertical(g4)
    c: DistanceY(g2,g1) = 1.28
    c: Coincident(g0,g-3)
    c: Coincident(g0,g-3)
    c: Coincident(g4,g-4)
FEATURE [Part::Extrusion] Extrude013  label="Extrude supporto CAM"
  Base = -> Sketch017
  Dir = (0,-1,2e-16)
  DirMode = 2
  FaceMakerClass = Part::FaceMakerBullseye
  FaceMakerMode = 3
  LengthFwd = 17.8
  LengthRev = 0
  Solid = true
  Symmetric = true
FEATURE [Sketcher::SketchObject] Sketch018  label="Scavo CAM"
  ArcFitTolerance = 1e-06
  AttachmentSupport = -> [YZ_Plane]
  ExternalGeometry = -> [Sketch]
  FullyConstrained = true
  MakeInternals = false
  MapMode = 5
  Placement = pos=(0,0,0) rot=(0.57735,0.57735,0.57735;2.0944rad)
  sketch-geometry (4):
    g0: LineSegment StartX=-7.73 StartY=48 StartZ=0 EndX=7.73 EndY=48 EndZ=0
    g1: LineSegment [constr] StartX=1.07e-14 StartY=48 StartZ=0 EndX=0 EndY=43.5155 EndZ=0
    g2: ArcOfCircle CenterX=9e-15 CenterY=52.42 CenterZ=0 NormalX=0 NormalY=0 NormalZ=1 AngleXU=0 Radius=8.90445 StartAngle=3.66102 EndAngle=5.76376
    g3: Circle [constr] CenterX=9e-15 CenterY=52.42 CenterZ=0 NormalX=0 NormalY=0 NormalZ=1 AngleXU=0 Radius=8.9
  constraints (13):
    c: Horizontal(g0)
    c: DistanceY(g-3,g0) = 0
    c: DistanceX(g0,g0) = 15.46
    c: DistanceX(g0,g-3) = 7.73
    c: DistanceX(g-3) = 0
    c: Coincident(g1,g-3)
    c: PointOnObject(g1,g-2)
    c: Coincident(g2,g0)
    c: Coincident(g2,g0)
    c: PointOnObject(g1,g2)
    c: Diameter(g3) = 17.8
    c: DistanceY(g1,g3) = 4.42
    c: Coincident(g2,g3)
FEATURE [Part::Extrusion] Extrude014  label="Extrude Scavo CAM"
  Base = -> Sketch018
  Dir = (1,0,0)
  DirMode = 2
  FaceMakerClass = Part::FaceMakerBullseye
  FaceMakerMode = 3
  LengthFwd = -34
  LengthRev = 0
  Solid = true
  Symmetric = false
FEATURE [Sketcher::SketchObject] Sketch019  label="scavo rumble"
  ArcFitTolerance = 1e-06
  AttachmentSupport = -> [XZ_Plane]
  ExternalGeometry = -> [Sketch]
  FullyConstrained = true
  MakeInternals = false
  MapMode = 5
  Placement = pos=(0,0,0) rot=(1,0,0;1.5708rad)
  sketch-geometry (6):
    g0: LineSegment StartX=-163.771 StartY=-21.9058 StartZ=0 EndX=-158.636 EndY=-23.5745 EndZ=0
    g1: LineSegment StartX=-158.636 StartY=-23.5745 StartZ=0 EndX=-165.743 EndY=-45.4488 EndZ=0
    g2: LineSegment StartX=-165.743 StartY=-45.4488 StartZ=0 EndX=-170.879 EndY=-43.7801 EndZ=0
    g3: LineSegment StartX=-170.879 StartY=-43.7801 StartZ=0 EndX=-163.771 EndY=-21.9058 EndZ=0
    g4: LineSegment [constr] StartX=-145.51 StartY=22 StartZ=0 EndX=-160.157 EndY=-23.0801 EndZ=0
    g5: LineSegment [constr] StartX=-158.636 StartY=-23.5745 StartZ=0 EndX=-160.157 EndY=-23.0801 EndZ=0
  constraints (17):
    c: Coincident(g1,g0)
    c: Coincident(g2,g1)
    c: Coincident(g3,g2)
    c: Coincident(g3,g0)
    c: Parallel(g3,g-3)
    c: Parallel(g3,g1)
    c: Perpendicular(g3,g0)
    c: Perpendicular(g2,g3)
    c: Distance(g2,g0) = 23
    c: Parallel(g4,g-3)
    c: Distance(g4) = 47.4
    c: Coincident(g4,g-3)
    c: Parallel(g5,g0)
    c: Distance(g5) = 1.6
    c: Coincident(g5,g0)
    c: Distance(g5,g0) = 3.8
    c: Coincident(g5,g4)
FEATURE [Part::Extrusion] Extrude015  label="scavo rumble001"
  Base = -> Sketch019
  Dir = (0,-1,2e-16)
  DirMode = 2
  FaceMakerClass = Part::FaceMakerBullseye
  FaceMakerMode = 3
  LengthFwd = 21
  LengthRev = 0
  Solid = true
  Symmetric = true
FEATURE [Sketcher::SketchObject] Sketch020  label="fermo rumble"
  ArcFitTolerance = 1e-06
  AttachmentSupport = -> [XZ_Plane]
  ExternalGeometry = -> [Sketch019,Sketch]
  FullyConstrained = true
  MakeInternals = false
  MapMode = 5
  Placement = pos=(0,0,0) rot=(1,0,0;1.5708rad)
  sketch-geometry (16):
    g0: LineSegment [constr] StartX=-165.905 StartY=-40.7697 StartZ=0 EndX=-167.265 EndY=-44.9544 EndZ=0
    g1: LineSegment [constr] StartX=-167.265 StartY=-44.9544 StartZ=0 EndX=-165.743 EndY=-45.4488 EndZ=0
    g2: LineSegment StartX=-167.318 StartY=-37.9976 StartZ=0 EndX=-165.225 EndY=-38.6774 EndZ=0
    g3: LineSegment StartX=-165.225 StartY=-38.6774 StartZ=0 EndX=-165.905 EndY=-40.7697 EndZ=0
    g4: LineSegment StartX=-165.905 StartY=-40.7697 StartZ=0 EndX=-167.997 EndY=-40.0899 EndZ=0
    g5: LineSegment StartX=-167.997 StartY=-40.0899 StartZ=0 EndX=-167.318 EndY=-37.9976 EndZ=0
    g6: LineSegment StartX=-166.823 StartY=-36.4759 StartZ=0 EndX=-163.399 EndY=-37.5883 EndZ=0
    g7: LineSegment StartX=-163.399 StartY=-37.5883 StartZ=0 EndX=-165.006 EndY=-42.5338 EndZ=0
    g8: LineSegment StartX=-165.006 StartY=-42.5338 StartZ=0 EndX=-168.43 EndY=-41.4214 EndZ=0
    g9: LineSegment StartX=-169.457 StartY=-39.4053 StartZ=0 EndX=-168.839 EndY=-37.5031 EndZ=0
    g10: LineSegment [constr] StartX=-168.839 StartY=-37.5031 StartZ=0 EndX=-168.345 EndY=-35.9815 EndZ=0
    g11: LineSegment [constr] StartX=-168.345 StartY=-35.9815 StartZ=0 EndX=-166.823 EndY=-36.4759 EndZ=0
    g12: ArcOfCircle CenterX=-167.936 CenterY=-39.8997 CenterZ=0 NormalX=0 NormalY=0 NormalZ=1 AngleXU=0 Radius=1.6 StartAngle=2.82743 EndAngle=4.39823
    g13: GeomPoint [constr] X=-169.952 Y=-40.9269 Z=0
    g14: ArcOfCircle CenterX=-167.318 CenterY=-37.9976 CenterZ=0 NormalX=0 NormalY=0 NormalZ=1 AngleXU=0 Radius=1.6 StartAngle=1.25664 EndAngle=2.82743
    g15: GeomPoint [constr] X=-168.345 Y=-35.9815 Z=0
  constraints (42):
    c: Parallel(g0,g-4)
    c: Distance(g0) = 4.4
    c: Coincident(g1,g0)
    c: Perpendicular(g0,g1)
    c: Distance(g1) = 1.6
    c: Coincident(g1,g-5)
    c: Coincident(g3,g2)
    c: Coincident(g4,g3)
    c: Coincident(g5,g4)
    c: Coincident(g5,g2)
    c: Parallel(g3,g-4)
    c: Parallel(g3,g5)
    c: Perpendicular(g2,g3)
    c: Parallel(g4,g2)
    c: Distance(g2) = 2.2
    c: Distance(g3) = 2.2
    c: Coincident(g7,g6)
    c: Coincident(g8,g7)
    c: Parallel(g7,g-4)
    c: Parallel(g7,g9)
    c: Perpendicular(g6,g7)
    c: Parallel(g6,g8)
    c: Distance(g6,g15) = 5.2
    c: Distance(g7) = 5.2
    c: Coincident(g11,g10)
    c: Parallel(g10,g9)
    c: Parallel(g11,g6)
    c: Distance(g10) = 1.6
    c: Distance(g11) = 1.6
    c: Coincident(g10,g15)
    c: Distance(g11,g2) = 1.6
    c: Distance(g2,g10) = 1.6
    c: PointOnObject(g13,g8)
    c: PointOnObject(g13,g9)
    c: Tangent(g8,g12) = 1.5708
    c: Tangent(g9,g12) = 1.5708
    c: PointOnObject(g15,g9)
    c: Tangent(g6,g14) = 1.5708
    c: Tangent(g9,g14) = 1.5708
    c: Equal(g12,g14)
    c: Coincident(g6,g11)
    c: Coincident(g3,g0)
FEATURE [Part::Extrusion] Extrude016  label="Extrude fermo rumble"
  Base = -> Sketch020
  Dir = (0,-1,2e-16)
  DirMode = 2
  FaceMakerClass = Part::FaceMakerBullseye
  FaceMakerMode = 3
  LengthFwd = 25.2
  LengthRev = 0
  Solid = true
  Symmetric = true
FEATURE [Sketcher::SketchObject] Sketch021  label="perno fermo rumble001"
  ArcFitTolerance = 1e-06
  AttachmentSupport = -> [XZ_Plane001]
  FullyConstrained = true
  MakeInternals = false
  MapMode = 5
  Placement = pos=(0,0,0) rot=(1,0,0;1.5708rad)
  sketch-geometry (16):
    g0: LineSegment StartX=0 StartY=0.45 StartZ=0 EndX=0 EndY=1.55 EndZ=0
    g1: LineSegment StartX=0.45 StartY=2 StartZ=0 EndX=1.55 EndY=2 EndZ=0
    g2: LineSegment StartX=2 StartY=1.55 StartZ=0 EndX=2 EndY=0.45 EndZ=0
    g3: LineSegment StartX=1.55 StartY=0 StartZ=0 EndX=0.45 EndY=0 EndZ=0
    g4: ArcOfCircle [constr] CenterX=0.45 CenterY=1.55 CenterZ=0 NormalX=0 NormalY=0 NormalZ=1 AngleXU=0 Radius=0.45 StartAngle=1.5708 EndAngle=3.14159
    g5: GeomPoint [constr] X=0 Y=2 Z=0
    g6: LineSegment StartX=0.45 StartY=2 StartZ=0 EndX=0 EndY=1.55 EndZ=0
    g7: ArcOfCircle [constr] CenterX=1.55 CenterY=1.55 CenterZ=0 NormalX=0 NormalY=0 NormalZ=1 AngleXU=0 Radius=0.45 StartAngle=0 EndAngle=1.5708
    g8: GeomPoint [constr] X=2 Y=2 Z=0
    g9: LineSegment StartX=2 StartY=1.55 StartZ=0 EndX=1.55 EndY=2 EndZ=0
    g10: ArcOfCircle [constr] CenterX=1.55 CenterY=0.45 CenterZ=0 NormalX=0 NormalY=0 NormalZ=1 AngleXU=0 Radius=0.45 StartAngle=4.71239 EndAngle=6.28319
    g11: GeomPoint [constr] X=2 Y=0 Z=0
    g12: LineSegment StartX=1.55 StartY=0 StartZ=0 EndX=2 EndY=0.45 EndZ=0
    g13: ArcOfCircle [constr] CenterX=0.45 CenterY=0.45 CenterZ=0 NormalX=0 NormalY=0 NormalZ=1 AngleXU=0 Radius=0.45 StartAngle=3.14159 EndAngle=4.71239
    g14: GeomPoint [constr] X=0 Y=0 Z=0
    g15: LineSegment StartX=0 StartY=0.45 StartZ=0 EndX=0.45 EndY=0 EndZ=0
  constraints (35):
    c: Coincident(g14,g-1)
    c: PointOnObject(g5,g-2)
    c: Horizontal(g1)
    c: Vertical(g2)
    c: Horizontal(g3)
    c: DistanceX(g5,g8) = 2
    c: DistanceY(g11,g8) = 2
    c: PointOnObject(g5,g0)
    c: PointOnObject(g5,g1)
    c: Tangent(g0,g4) = 1.5708
    c: Tangent(g1,g4) = 1.5708
    c: Coincident(g6,g0)
    c: Coincident(g6,g1)
    c: PointOnObject(g8,g2)
    c: PointOnObject(g8,g1)
    c: Tangent(g2,g7) = 1.5708
    c: Tangent(g1,g7) = 1.5708
    c: Coincident(g9,g2)
    c: Coincident(g9,g1)
    c: PointOnObject(g11,g2)
    c: PointOnObject(g11,g3)
    c: Tangent(g2,g10) = 1.5708
    c: Tangent(g3,g10) = 1.5708
    c: Coincident(g12,g2)
    c: Coincident(g12,g3)
    c: PointOnObject(g14,g0)
    c: PointOnObject(g14,g3)
    c: Tangent(g0,g13) = 1.5708
    c: Tangent(g3,g13) = 1.5708
    c: Coincident(g15,g0)
    c: Coincident(g15,g3)
    c: Equal(g6,g9)
    c: Equal(g9,g12)
    c: Equal(g12,g15)
    c: DistanceX(g14,g3) = 0.45
FEATURE [Sketcher::SketchObject] Sketch022  label="fori per M3x5(OD)x6(L)"
  ArcFitTolerance = 1e-06
  AttachmentSupport = -> [XZ_Plane]
  ExternalGeometry = -> [Sketch016]
  FullyConstrained = true
  MakeInternals = false
  MapMode = 5
  Placement = pos=(0,0,0) rot=(1,0,0;1.5708rad)
  sketch-geometry (7):
    g0: Circle CenterX=-5.6 CenterY=34.8 CenterZ=0 NormalX=0 NormalY=0 NormalZ=1 AngleXU=0 Radius=2.5
    g1: Circle CenterX=-5.6 CenterY=7.6 CenterZ=0 NormalX=0 NormalY=0 NormalZ=1 AngleXU=0 Radius=2.5
    g2: Circle CenterX=-78.51 CenterY=34.8 CenterZ=0 NormalX=0 NormalY=0 NormalZ=1 AngleXU=0 Radius=2.5
    g3: Circle CenterX=-78.51 CenterY=7.6 CenterZ=0 NormalX=0 NormalY=0 NormalZ=1 AngleXU=0 Radius=2.5
    g4: Circle CenterX=-184.08 CenterY=34.8 CenterZ=0 NormalX=0 NormalY=0 NormalZ=1 AngleXU=0 Radius=2.5
    g5: Circle CenterX=-179.305 CenterY=-76.8316 CenterZ=0 NormalX=0 NormalY=0 NormalZ=1 AngleXU=0 Radius=2.5
    g6: Circle CenterX=-213.443 CenterY=-76.8316 CenterZ=0 NormalX=0 NormalY=0 NormalZ=1 AngleXU=0 Radius=2.5
  constraints (14):
    c: Diameter(g0) = 5
    c: Diameter(g1) = 5
    c: Diameter(g2) = 5
    c: Diameter(g3) = 5
    c: Diameter(g4) = 5
    c: Diameter(g5) = 5
    c: Diameter(g6) = 5
    c: Coincident(g0,g-8)
    c: Coincident(g1,g-9)
    c: Coincident(g2,g-6)
    c: Coincident(g3,g-7)
    c: Coincident(g4,g-5)
    c: Coincident(g5,g-4)
    c: Coincident(g6,g-3)
FEATURE [Part::Extrusion] Extrude018  label="Extrude fori M3x5x6 - dx"
  Base = -> Sketch022
  Dir = (0,-1,2e-16)
  DirMode = 2
  FaceMakerClass = Part::FaceMakerBullseye
  FaceMakerMode = 3
  LengthFwd = 6.2
  LengthRev = 0
  Placement = pos=(0,-9.5,0) rot=(0,0,1;0rad)
  Solid = true
  Symmetric = true
FEATURE [Part::Extrusion] Extrude019  label="Extrude fori M3x5x6 - sx"
  Base = -> Sketch022
  Dir = (0,-1,2e-16)
  DirMode = 2
  FaceMakerClass = Part::FaceMakerBullseye
  FaceMakerMode = 3
  LengthFwd = 6.2
  LengthRev = 0
  Placement = pos=(0,9.5,0) rot=(0,0,1;0rad)
  Solid = true
  Symmetric = true
FEATURE [Sketcher::SketchObject] Sketch023  label="foro anteriore M3x5x6"
  ArcFitTolerance = 1e-06
  AttachmentSupport = -> [YZ_Plane]
  FullyConstrained = true
  MakeInternals = false
  MapMode = 5
  Placement = pos=(0,0,0) rot=(0.57735,0.57735,0.57735;2.0944rad)
  sketch-geometry (2):
    g0: LineSegment [constr] StartX=0 StartY=0 StartZ=0 EndX=0 EndY=38.6 EndZ=0
    g1: Circle CenterX=0 CenterY=38.6 CenterZ=0 NormalX=0 NormalY=0 NormalZ=1 AngleXU=0 Radius=2.5
  constraints (5):
    c: Coincident(g0,g-1)
    c: PointOnObject(g0,g-2)
    c: DistanceY(g0,g0) = 38.6
    c: Diameter(g1) = 5
    c: Coincident(g1,g0)
FEATURE [Part::Extrusion] Extrude020  label="Extrude foro anteriore M3x5x6"
  Base = -> Sketch023
  Dir = (1,0,0)
  DirMode = 2
  FaceMakerClass = Part::FaceMakerBullseye
  FaceMakerMode = 3
  LengthFwd = -6.2
  LengthRev = 0
  Solid = true
  Symmetric = false
FEATURE [Sketcher::SketchObject] Sketch024  label="fori per viti frontale"
  ArcFitTolerance = 1e-06
  AttachmentSupport = -> [YZ_Plane]
  FullyConstrained = true
  MakeInternals = false
  MapMode = 5
  Placement = pos=(0,0,0) rot=(0.57735,0.57735,0.57735;2.0944rad)
  sketch-geometry (9):
    g0: LineSegment [constr] StartX=-10.3 StartY=30.721 StartZ=0 EndX=10.3 EndY=30.721 EndZ=0
    g1: LineSegment [constr] StartX=10.3 StartY=30.721 StartZ=0 EndX=10.3 EndY=10.121 EndZ=0
    g2: LineSegment [constr] StartX=10.3 StartY=10.121 StartZ=0 EndX=-10.3 EndY=10.121 EndZ=0
    g3: LineSegment [constr] StartX=-10.3 StartY=10.121 StartZ=0 EndX=-10.3 EndY=30.721 EndZ=0
    g4: LineSegment [constr] StartX=0 StartY=0 StartZ=0 EndX=0 EndY=10.121 EndZ=0
    g5: Circle CenterX=-10.3 CenterY=30.721 CenterZ=0 NormalX=0 NormalY=0 NormalZ=1 AngleXU=0 Radius=2
    g6: Circle CenterX=10.3 CenterY=30.721 CenterZ=0 NormalX=0 NormalY=0 NormalZ=1 AngleXU=0 Radius=2
    g7: Circle CenterX=-10.3 CenterY=10.121 CenterZ=0 NormalX=0 NormalY=0 NormalZ=1 AngleXU=0 Radius=2
    g8: Circle CenterX=10.3 CenterY=10.121 CenterZ=0 NormalX=0 NormalY=0 NormalZ=1 AngleXU=0 Radius=2
  constraints (22):
    c: Horizontal(g0)
    c: Coincident(g1,g0)
    c: Vertical(g1)
    c: Coincident(g2,g1)
    c: Horizontal(g2)
    c: Coincident(g3,g2)
    c: Coincident(g3,g0)
    c: Vertical(g3)
    c: DistanceX(g0,g0) = 20.6
    c: DistanceY(g3,g3) = 20.6
    c: Coincident(g4,g-1)
    c: PointOnObject(g4,g-2)
    c: DistanceY(g4,g4) = 10.121
    c: Symmetric(g2,g2,g4)
    c: Diameter(g5) = 4
    c: Diameter(g6) = 4
    c: Diameter(g7) = 4
    c: Diameter(g8) = 4
    c: Coincident(g5,g0)
    c: Coincident(g6,g0)
    c: Coincident(g7,g2)
    c: Coincident(g8,g1)
FEATURE [Part::Extrusion] Extrude021  label="Extrude fori per viti frontale"
  Base = -> Sketch024
  Dir = (1,0,0)
  DirMode = 2
  FaceMakerClass = Part::FaceMakerBullseye
  FaceMakerMode = 3
  LengthFwd = -2.4
  LengthRev = 0
  Solid = true
  Symmetric = false
FEATURE [Sketcher::SketchObject] Sketch025  label="foro per filo CAM"
  ArcFitTolerance = 1e-06
  AttachmentSupport = -> [XZ_Plane]
  ExternalGeometry = -> [Sketch]
  FullyConstrained = true
  MakeInternals = false
  MapMode = 5
  Placement = pos=(0,0,0) rot=(1,0,0;1.5708rad)
  sketch-geometry (4):
    g0: LineSegment StartX=-44.6 StartY=41.2 StartZ=0 EndX=-44.6 EndY=36.4 EndZ=0
    g1: LineSegment StartX=-44.6 StartY=36.4 StartZ=0 EndX=-54.6 EndY=36.4 EndZ=0
    g2: LineSegment StartX=-54.6 StartY=36.4 StartZ=0 EndX=-50.4 EndY=41.2 EndZ=0
    g3: LineSegment StartX=-50.4 StartY=41.2 StartZ=0 EndX=-44.6 EndY=41.2 EndZ=0
  constraints (11):
    c: Vertical(g0)
    c: Coincident(g1,g0)
    c: Horizontal(g1)
    c: Coincident(g2,g1)
    c: Coincident(g3,g2)
    c: Coincident(g3,g0)
    c: Horizontal(g3)
    c: Coincident(g0,g-3)
    c: DistanceY(g0,g-4) = 0
    c: DistanceX(g3,g3) = 5.8
    c: DistanceX(g1,g1) = 10
FEATURE [Part::Extrusion] Extrude022  label="Extrude foro per filo CAM dx"
  Base = -> Sketch025
  Dir = (0,-1,2e-16)
  DirMode = 2
  FaceMakerClass = Part::FaceMakerBullseye
  FaceMakerMode = 3
  LengthFwd = 4.9
  LengthRev = 0
  Placement = pos=(0,6.95,0) rot=(0,0,1;0rad)
  Solid = true
  Symmetric = true
FEATURE [Part::Extrusion] Extrude023  label="Extrude foro per filo CAM sx"
  Base = -> Sketch025
  Dir = (0,-1,2e-16)
  DirMode = 2
  FaceMakerClass = Part::FaceMakerBullseye
  FaceMakerMode = 3
  LengthFwd = 4.9
  LengthRev = 0
  Placement = pos=(0,-6.95,0) rot=(0,0,1;0rad)
  Solid = true
  Symmetric = true
FEATURE [Sketcher::SketchObject] Sketch026  label="foro sotto anteriore M3x5x6"
  ArcFitTolerance = 1e-06
  AttachmentSupport = -> [XY_Plane]
  FullyConstrained = true
  MakeInternals = false
  MapMode = 5
  sketch-geometry (2):
    g0: LineSegment [constr] StartX=0 StartY=0 StartZ=0 EndX=-16.5 EndY=0 EndZ=0
    g1: Circle CenterX=-16.5 CenterY=0 CenterZ=0 NormalX=0 NormalY=0 NormalZ=1 AngleXU=0 Radius=2.5
  constraints (5):
    c: Distance(g0) = 16.5
    c: Coincident(g0,g-1)
    c: PointOnObject(g0,g-1)
    c: Diameter(g1) = 5
    c: Coincident(g0,g1)
FEATURE [Sketcher::SketchObject] Sketch027  label="foro sotto posteriore M3x5x6"
  ArcFitTolerance = 1e-06
  AttachmentSupport = -> [XY_Plane]
  ExternalGeometry = -> [Sketch]
  FullyConstrained = true
  MakeInternals = false
  MapMode = 5
  sketch-geometry (2):
    g0: LineSegment [constr] StartX=-82.8 StartY=2e-16 StartZ=0 EndX=-71.3 EndY=2e-16 EndZ=0
    g1: Circle CenterX=-71.3 CenterY=2e-16 CenterZ=0 NormalX=0 NormalY=0 NormalZ=1 AngleXU=0 Radius=2.5
  constraints (5):
    c: Distance(g0) = 11.5
    c: Coincident(g0,g-3)
    c: PointOnObject(g0,g-3)
    c: Diameter(g1) = 5
    c: Coincident(g1,g0)
FEATURE [Sketcher::SketchObject] Sketch029  label="fori sotto impugnatura"
  ArcFitTolerance = 1e-06
  AttachmentSupport = -> [XY_Plane]
  ExternalGeometry = -> [Sketch]
  FullyConstrained = true
  MakeInternals = false
  MapMode = 5
  sketch-geometry (15):
    g0: LineSegment [constr] StartX=-175.232 StartY=-1.83e-14 StartZ=0 EndX=-191.232 EndY=0 EndZ=0
    g1: Circle CenterX=-191.232 CenterY=0 CenterZ=0 NormalX=0 NormalY=0 NormalZ=1 AngleXU=0 Radius=3.95
    g2: LineSegment [constr] StartX=-175.232 StartY=-1.83e-14 StartZ=0 EndX=-204.275 EndY=0 EndZ=0
    g3: LineSegment StartX=-204.275 StartY=3.525 StartZ=0 EndX=-204.275 EndY=-3.525 EndZ=0
    g4: LineSegment StartX=-205.4 StartY=-4.65 StartZ=0 EndX=-206.65 EndY=-4.65 EndZ=0
    g5: LineSegment StartX=-207.775 StartY=-3.525 StartZ=0 EndX=-207.775 EndY=3.525 EndZ=0
    g6: LineSegment StartX=-206.65 StartY=4.65 StartZ=0 EndX=-205.4 EndY=4.65 EndZ=0
    g7: ArcOfCircle CenterX=-206.65 CenterY=3.525 CenterZ=0 NormalX=0 NormalY=0 NormalZ=1 AngleXU=0 Radius=1.125 StartAngle=1.5708 EndAngle=3.14159
    g8: GeomPoint [constr] X=-207.775 Y=4.65 Z=0
    g9: ArcOfCircle CenterX=-205.4 CenterY=3.525 CenterZ=0 NormalX=0 NormalY=0 NormalZ=1 AngleXU=0 Radius=1.125 StartAngle=0 EndAngle=1.5708
    g10: GeomPoint [constr] X=-204.275 Y=4.65 Z=0
    g11: ArcOfCircle CenterX=-205.4 CenterY=-3.525 CenterZ=0 NormalX=0 NormalY=0 NormalZ=1 AngleXU=0 Radius=1.125 StartAngle=4.71239 EndAngle=6.28319
    g12: GeomPoint [constr] X=-204.275 Y=-4.65 Z=0
    g13: ArcOfCircle CenterX=-206.65 CenterY=-3.525 CenterZ=0 NormalX=0 NormalY=0 NormalZ=1 AngleXU=0 Radius=1.125 StartAngle=3.14159 EndAngle=4.71239
    g14: GeomPoint [constr] X=-207.775 Y=-4.65 Z=0
  constraints (35):
    c: Distance(g0) = 16
    c: Coincident(g0,g-3)
    c: PointOnObject(g0,g-1)
    c: Diameter(g1) = 7.9
    c: Coincident(g1,g0)
    c: Coincident(g2,g0)
    c: PointOnObject(g2,g-1)
    c: Vertical(g3)
    c: Horizontal(g4)
    c: Vertical(g5)
    c: Horizontal(g6)
    c: DistanceY(g12,g10) = 9.3
    c: DistanceX(g8,g10) = 3.5
    c: Symmetric(g10,g12,g2)
    c: PointOnObject(g8,g5)
    c: PointOnObject(g8,g6)
    c: Tangent(g5,g7) = 1.5708
    c: Tangent(g6,g7) = 1.5708
    c: PointOnObject(g10,g3)
    c: PointOnObject(g10,g6)
    c: Tangent(g3,g9) = 1.5708
    c: Tangent(g6,g9) = 1.5708
    c: PointOnObject(g12,g3)
    c: PointOnObject(g12,g4)
    c: Tangent(g3,g11) = 1.5708
    c: Tangent(g4,g11) = 1.5708
    c: PointOnObject(g14,g4)
    c: PointOnObject(g14,g5)
    c: Tangent(g4,g13) = 1.5708
    c: Tangent(g5,g13) = 1.5708
    c: Equal(g7,g9)
    c: Equal(g9,g11)
    c: Equal(g11,g13)
    c: DistanceX(g6,g6) = 1.25
    c: DistanceX(g-5,g5) = 6.8
FEATURE [Sketcher::SketchObject] Sketch030  label="fori superiori per solenoide e oled"
  ArcFitTolerance = 1e-06
  AttachmentSupport = -> [XY_Plane]
  ExternalGeometry = -> [Sketch]
  FullyConstrained = true
  MakeInternals = false
  MapMode = 5
  sketch-geometry (33):
    g0: LineSegment [constr] StartX=-181.6 StartY=1.12e-14 StartZ=0 EndX=-169.91 EndY=0 EndZ=0
    g1: LineSegment [constr] StartX=-169.91 StartY=0 StartZ=0 EndX=-169.91 EndY=-2.6 EndZ=0
    g2: LineSegment [constr] StartX=-169.91 StartY=0 StartZ=0 EndX=-169.91 EndY=2.6 EndZ=0
    g3: LineSegment StartX=-169.91 StartY=4.975 StartZ=0 EndX=-169.91 EndY=8.225 EndZ=0
    g4: LineSegment StartX=-167.535 StartY=10.6 StartZ=0 EndX=-167.285 EndY=10.6 EndZ=0
    g5: LineSegment StartX=-164.91 StartY=8.225 StartZ=0 EndX=-164.91 EndY=4.975 EndZ=0
    g6: LineSegment StartX=-167.285 StartY=2.6 StartZ=0 EndX=-167.535 EndY=2.6 EndZ=0
    g7: LineSegment StartX=-169.91 StartY=-4.975 StartZ=0 EndX=-169.91 EndY=-8.225 EndZ=0
    g8: LineSegment StartX=-167.535 StartY=-10.6 StartZ=0 EndX=-167.285 EndY=-10.6 EndZ=0
    g9: LineSegment StartX=-164.91 StartY=-8.225 StartZ=0 EndX=-164.91 EndY=-4.975 EndZ=0
    g10: LineSegment StartX=-167.285 StartY=-2.6 StartZ=0 EndX=-167.535 EndY=-2.6 EndZ=0
    g11: ArcOfCircle CenterX=-167.535 CenterY=8.225 CenterZ=0 NormalX=0 NormalY=0 NormalZ=1 AngleXU=0 Radius=2.375 StartAngle=1.5708 EndAngle=3.14159
    g12: GeomPoint [constr] X=-169.91 Y=10.6 Z=0
    g13: ArcOfCircle CenterX=-167.285 CenterY=8.225 CenterZ=0 NormalX=0 NormalY=0 NormalZ=1 AngleXU=0 Radius=2.375 StartAngle=0 EndAngle=1.5708
    g14: GeomPoint [constr] X=-164.91 Y=10.6 Z=0
    g15: ArcOfCircle CenterX=-167.285 CenterY=4.975 CenterZ=0 NormalX=0 NormalY=0 NormalZ=1 AngleXU=0 Radius=2.375 StartAngle=4.71239 EndAngle=6.28319
    g16: GeomPoint [constr] X=-164.91 Y=2.6 Z=0
    g17: ArcOfCircle CenterX=-167.535 CenterY=4.975 CenterZ=0 NormalX=0 NormalY=0 NormalZ=1 AngleXU=0 Radius=2.375 StartAngle=3.14159 EndAngle=4.71239
    g18: GeomPoint [constr] X=-169.91 Y=2.6 Z=0
    g19: ArcOfCircle CenterX=-167.535 CenterY=-4.975 CenterZ=0 NormalX=0 NormalY=0 NormalZ=1 AngleXU=0 Radius=2.375 StartAngle=1.5708 EndAngle=3.14159
    g20: GeomPoint [constr] X=-169.91 Y=-2.6 Z=0
    g21: ArcOfCircle CenterX=-167.285 CenterY=-4.975 CenterZ=0 NormalX=0 NormalY=0 NormalZ=1 AngleXU=0 Radius=2.375 StartAngle=0 EndAngle=1.5708
    g22: GeomPoint [constr] X=-164.91 Y=-2.6 Z=0
    g23: ArcOfCircle CenterX=-167.285 CenterY=-8.225 CenterZ=0 NormalX=0 NormalY=0 NormalZ=1 AngleXU=0 Radius=2.375 StartAngle=4.71239 EndAngle=6.28319
    g24: GeomPoint [constr] X=-164.91 Y=-10.6 Z=0
    g25: ArcOfCircle CenterX=-167.535 CenterY=-8.225 CenterZ=0 NormalX=0 NormalY=0 NormalZ=1 AngleXU=0 Radius=2.375 StartAngle=3.14159 EndAngle=4.71239
    g26: GeomPoint [constr] X=-169.91 Y=-10.6 Z=0
    g27: LineSegment [constr] StartX=-181.6 StartY=1.12e-14 StartZ=0 EndX=-152.209 EndY=0 EndZ=0
    g28: LineSegment [constr] StartX=-181.6 StartY=1.12e-14 StartZ=0 EndX=-130.41 EndY=0 EndZ=0
    g29: LineSegment [constr] StartX=-152.209 StartY=0 StartZ=0 EndX=-152.209 EndY=6.95 EndZ=0
    g30: LineSegment [constr] StartX=-130.41 StartY=0 StartZ=0 EndX=-130.41 EndY=-6.95 EndZ=0
    g31: Circle CenterX=-152.209 CenterY=6.95 CenterZ=0 NormalX=0 NormalY=0 NormalZ=1 AngleXU=0 Radius=2.1
    g32: Circle CenterX=-130.41 CenterY=-6.95 CenterZ=0 NormalX=0 NormalY=0 NormalZ=1 AngleXU=0 Radius=2.1
  constraints (79):
    c: Distance(g0) = 11.69
    c: PointOnObject(g0,g-1)
    c: Coincident(g-4,g0)
    c: Distance(g1) = 2.6
    c: Coincident(g1,g0)
    c: Vertical(g1)
    c: Distance(g2) = 2.6
    c: Coincident(g2,g0)
    c: Vertical(g2)
    c: Distance(g18,g12) = 8
    c: Coincident(g18,g2)
    c: Vertical(g3)
    c: Distance(g14,g12) = 5
    c: Horizontal(g4)
    c: Distance(g16,g14) = 8
    c: Vertical(g5)
    c: Distance(g26,g20) = 8
    c: Coincident(g20,g1)
    c: Vertical(g7)
    c: Distance(g26,g24) = 5
    c: Horizontal(g8)
    c: Distance(g24,g22) = 8
    c: Vertical(g9)
    c: PointOnObject(g12,g3)
    c: PointOnObject(g12,g4)
    c: Tangent(g3,g11) = 1.5708
    c: Tangent(g4,g11) = 1.5708
    c: PointOnObject(g14,g5)
    c: PointOnObject(g14,g4)
    c: Tangent(g5,g13) = 1.5708
    c: Tangent(g4,g13) = 1.5708
    c: PointOnObject(g16,g5)
    c: PointOnObject(g16,g6)
    c: Tangent(g5,g15) = 1.5708
    c: Tangent(g6,g15) = 1.5708
    c: PointOnObject(g18,g3)
    c: PointOnObject(g18,g6)
    c: Tangent(g3,g17) = 1.5708
    c: Tangent(g6,g17) = 1.5708
    c: Equal(g11,g13)
    c: Equal(g13,g15)
    c: Equal(g15,g17)
    c: DistanceX(g4,g4) = 0.25
    c: PointOnObject(g20,g7)
    c: PointOnObject(g20,g10)
    c: Tangent(g7,g19) = -1.5708
    c: Tangent(g10,g19) = -1.5708
    c: PointOnObject(g22,g9)
    c: PointOnObject(g22,g10)
    c: Tangent(g9,g21) = -1.5708
    c: Tangent(g10,g21) = -1.5708
    c: PointOnObject(g24,g9)
    c: PointOnObject(g24,g8)
    c: Tangent(g9,g23) = -1.5708
    c: Tangent(g8,g23) = -1.5708
    c: PointOnObject(g26,g8)
    c: PointOnObject(g26,g7)
    c: Tangent(g8,g25) = -1.5708
    c: Tangent(g7,g25) = -1.5708
    c: Equal(g19,g21)
    c: Equal(g21,g23)
    c: Equal(g23,g25)
    c: DistanceX(g10,g10) = 0.25
    c: Distance(g27) = 29.391
    c: Coincident(g27,g0)
    c: PointOnObject(g27,g-1)
    c: Distance(g28) = 51.19
    c: Coincident(g28,g0)
    c: PointOnObject(g28,g-1)
    c: Distance(g29) = 6.95
    c: Coincident(g29,g27)
    c: Vertical(g29)
    c: Distance(g30) = 6.95
    c: Coincident(g30,g28)
    c: Vertical(g30)
    c: Diameter(g31) = 4.2
    c: Diameter(g32) = 4.2
    c: Coincident(g32,g30)
    c: Coincident(g31,g29)
FEATURE [Sketcher::SketchObject] Sketch031  label="fori inferiori switch pompa"
  ArcFitTolerance = 1e-06
  AttachmentSupport = -> [XY_Plane]
  ExternalGeometry = -> [Sketch]
  FullyConstrained = true
  MakeInternals = false
  MapMode = 5
  sketch-geometry (4):
    g0: LineSegment [constr] StartX=-57.2 StartY=1.9e-15 StartZ=0 EndX=-62.45 EndY=1.9e-15 EndZ=0
    g1: LineSegment [constr] StartX=-62.45 StartY=3.25 StartZ=0 EndX=-62.45 EndY=-3.25 EndZ=0
    g2: Circle CenterX=-62.45 CenterY=3.25 CenterZ=0 NormalX=0 NormalY=0 NormalZ=1 AngleXU=0 Radius=1.6
    g3: Circle CenterX=-62.45 CenterY=-3.25 CenterZ=0 NormalX=0 NormalY=0 NormalZ=1 AngleXU=0 Radius=1.6
  constraints (10):
    c: Distance(g0) = 5.25
    c: Coincident(g0,g-3)
    c: PointOnObject(g0,g-3)
    c: Vertical(g1)
    c: DistanceY(g1,g1) = 6.5
    c: Symmetric(g1,g1,g0)
    c: Diameter(g2) = 3.2
    c: Diameter(g3) = 3.2
    c: Coincident(g2,g1)
    c: Coincident(g3,g1)
FEATURE [Sketcher::SketchObject] Sketch032  label="spazio per PILA 18650"
  ArcFitTolerance = 1e-06
  AttachmentSupport = -> [XY_Plane]
  ExternalGeometry = -> [Sketch]
  FullyConstrained = true
  MakeInternals = false
  MapMode = 5
  sketch-geometry (2):
    g0: LineSegment [constr] StartX=-178.142 StartY=-1.74e-14 StartZ=0 EndX=-191.142 EndY=-1.83e-14 EndZ=0
    g1: Circle CenterX=-191.142 CenterY=-1.83e-14 CenterZ=0 NormalX=0 NormalY=0 NormalZ=1 AngleXU=0 Radius=10.5
  constraints (5):
    c: Distance(g0) = 13
    c: Coincident(g0,g-3)
    c: PointOnObject(g0,g-4)
    c: Diameter(g1) = 21
    c: Coincident(g1,g0)
FEATURE [Part::Extrusion] Extrude030  label="Extrude spazio per PILA 18650"
  Base = -> Sketch032
  Dir = (0,0,1)
  DirLink = -> Sketch [Edge45]
  DirMode = 2
  FaceMakerClass = Part::FaceMakerBullseye
  FaceMakerMode = 3
  LengthFwd = 76
  LengthRev = 0
  Placement = pos=(6,0,-72) rot=(0,0,1;0rad)
  Solid = true
  Symmetric = false
FEATURE [Sketcher::SketchObject] Sketch033  label="fermo per scheda micro"
  ArcFitTolerance = 1e-06
  AttachmentSupport = -> [XZ_Plane]
  ExternalGeometry = -> [Sketch]
  FullyConstrained = true
  MakeInternals = false
  MapMode = 5
  Placement = pos=(0,0,0) rot=(1,0,0;1.5708rad)
  sketch-geometry (12):
    g0: LineSegment StartX=-11.6 StartY=6 StartZ=0 EndX=-4 EndY=6 EndZ=0
    g1: LineSegment StartX=-4 StartY=6 StartZ=0 EndX=-4 EndY=36.4 EndZ=0
    g2: LineSegment StartX=-4 StartY=36.4 StartZ=0 EndX=-11.6 EndY=36.4 EndZ=0
    g3: LineSegment StartX=-11.6 StartY=36.4 StartZ=0 EndX=-11.6 EndY=6 EndZ=0
    g4: LineSegment StartX=-80.11 StartY=11.6 StartZ=0 EndX=-70.51 EndY=11.6 EndZ=0
    g5: LineSegment StartX=-70.51 StartY=11.6 StartZ=0 EndX=-70.51 EndY=6 EndZ=0
    g6: LineSegment StartX=-70.51 StartY=6 StartZ=0 EndX=-80.11 EndY=6 EndZ=0
    g7: LineSegment StartX=-80.11 StartY=6 StartZ=0 EndX=-80.11 EndY=11.6 EndZ=0
    g8: LineSegment StartX=-78.51 StartY=36.4 StartZ=0 EndX=-70.51 EndY=36.4 EndZ=0
    g9: LineSegment StartX=-70.51 StartY=36.4 StartZ=0 EndX=-70.51 EndY=30.8 EndZ=0
    g10: LineSegment StartX=-70.51 StartY=30.8 StartZ=0 EndX=-78.51 EndY=30.8 EndZ=0
    g11: LineSegment StartX=-78.51 StartY=30.8 StartZ=0 EndX=-78.51 EndY=36.4 EndZ=0
  constraints (33):
    c: Horizontal(g0)
    c: Coincident(g1,g0)
    c: Coincident(g2,g1)
    c: Horizontal(g2)
    c: Coincident(g3,g2)
    c: Coincident(g3,g0)
    c: Vertical(g3)
    c: DistanceX(g2,g2) = 7.6
    c: Coincident(g1,g-3)
    c: Coincident(g0,g-3)
    c: Horizontal(g4)
    c: Coincident(g5,g4)
    c: Vertical(g5)
    c: Coincident(g6,g5)
    c: Horizontal(g6)
    c: Coincident(g7,g6)
    c: Coincident(g7,g4)
    c: Vertical(g7)
    c: DistanceY(g5,g5) = 5.6
    c: DistanceX(g4,g4) = 9.6
    c: Coincident(g9,g8)
    c: Vertical(g9)
    c: Coincident(g10,g9)
    c: Horizontal(g10)
    c: Coincident(g11,g10)
    c: Coincident(g11,g8)
    c: Vertical(g11)
    c: DistanceY(g9,g9) = 5.6
    c: DistanceX(g10,g10) = 8
    c: Coincident(g4,g-4)
    c: DistanceX(g4,g10) = 1.6
    c: Horizontal(g8)
    c: DistanceY(g8,g1) = 0
FEATURE [Sketcher::SketchObject] Sketch034  label="buchi guida rail"
  ArcFitTolerance = 1e-06
  AttachmentSupport = -> [XY_Plane]
  ExternalGeometry = -> [Sketch]
  FullyConstrained = true
  MakeInternals = false
  MapMode = 5
  sketch-geometry (6):
    g0: LineSegment [constr] StartX=-100.8 StartY=9.1e-15 StartZ=0 EndX=-93.3 EndY=0 EndZ=0
    g1: LineSegment [constr] StartX=-93.3 StartY=0 StartZ=0 EndX=-73.3 EndY=0 EndZ=0
    g2: LineSegment [constr] StartX=-73.3 StartY=0 StartZ=0 EndX=-53.3 EndY=0 EndZ=0
    g3: Circle CenterX=-93.3 CenterY=0 CenterZ=0 NormalX=0 NormalY=0 NormalZ=1 AngleXU=0 Radius=2.5
    g4: Circle CenterX=-73.3 CenterY=0 CenterZ=0 NormalX=0 NormalY=0 NormalZ=1 AngleXU=0 Radius=2.5
    g5: Circle CenterX=-53.3 CenterY=0 CenterZ=0 NormalX=0 NormalY=0 NormalZ=1 AngleXU=0 Radius=2.5
  constraints (15):
    c: Distance(g0) = 7.5
    c: Coincident(g0,g-3)
    c: PointOnObject(g0,g-1)
    c: Distance(g1) = 20
    c: Coincident(g1,g0)
    c: PointOnObject(g1,g-1)
    c: Distance(g2) = 20
    c: Coincident(g2,g1)
    c: PointOnObject(g2,g-1)
    c: Diameter(g3) = 5
    c: Diameter(g4) = 5
    c: Diameter(g5) = 5
    c: Coincident(g3,g0)
    c: Coincident(g4,g1)
    c: Coincident(g5,g2)
FEATURE [Part::Extrusion] Extrude032  label="Extrude buchi guida rail"
  Base = -> Sketch034
  Dir = (0,0,1)
  DirMode = 2
  FaceMakerClass = Part::FaceMakerBullseye
  FaceMakerMode = 3
  LengthFwd = -6.2
  LengthRev = 0
  Placement = pos=(0,0,43.2) rot=(0,0,1;0rad)
  Solid = true
  Symmetric = false
FEATURE [Part::Extrusion] Extrude033  label="Extrude fori superiori per solenoide e oled001"
  Base = -> Sketch030
  Dir = (0,0,1)
  DirMode = 2
  FaceMakerClass = Part::FaceMakerBullseye
  FaceMakerMode = 3
  LengthFwd = -4.8
  LengthRev = 0
  Placement = pos=(0,0,41.2) rot=(0,0,1;0rad)
  Solid = true
  Symmetric = false
FEATURE [Part::Extrusion] Extrude034  label="Extrude fori sotto impugnatura001"
  Base = -> Sketch029
  Dir = (0,0,1)
  DirMode = 2
  FaceMakerClass = Part::FaceMakerBullseye
  FaceMakerMode = 3
  LengthFwd = 5
  LengthRev = 0
  Placement = pos=(0,0,-83) rot=(0,0,1;0rad)
  Solid = true
  Symmetric = false
FEATURE [Part::Extrusion] Extrude035  label="Extrude fori inferiori switch pompa001"
  Base = -> Sketch031
  Dir = (0,0,1)
  DirMode = 2
  FaceMakerClass = Part::FaceMakerBullseye
  FaceMakerMode = 3
  LengthFwd = 4
  LengthRev = 0
  Placement = pos=(0,0,-1.7) rot=(0,0,1;0rad)
  Solid = true
  Symmetric = false
FEATURE [Part::Extrusion] Extrude036  label="Extrude foro sotto posteriore M3x5x007"
  Base = -> Sketch027
  Dir = (0,0,1)
  DirMode = 2
  FaceMakerClass = Part::FaceMakerBullseye
  FaceMakerMode = 3
  LengthFwd = 6.2
  LengthRev = 0
  Placement = pos=(0,0,-9.6) rot=(0,0,1;0rad)
  Solid = true
  Symmetric = false
FEATURE [Part::Extrusion] Extrude037  label="Extrude foro sotto anteriore M3x5x007"
  Base = -> Sketch026
  Dir = (0,0,1)
  DirMode = 2
  FaceMakerClass = Part::FaceMakerBullseye
  FaceMakerMode = 3
  LengthFwd = 6.2
  LengthRev = 0
  Solid = true
  Symmetric = false
FEATURE [Sketcher::SketchObject] Sketch035  label="foro per fissaggio micro"
  ArcFitTolerance = 1e-06
  AttachmentSupport = -> [XZ_Plane]
  ExternalGeometry = -> [Sketch,Sketch033]
  FullyConstrained = true
  MakeInternals = false
  MapMode = 5
  Placement = pos=(0,0,0) rot=(1,0,0;1.5708rad)
  sketch-geometry (3):
    g0: Circle CenterX=-7.8 CenterY=21.2 CenterZ=0 NormalX=0 NormalY=0 NormalZ=1 AngleXU=0 Radius=1.6
    g1: GeomPoint [constr] X=-4 Y=21.2 Z=0
    g2: LineSegment [constr] StartX=-4 StartY=21.2 StartZ=0 EndX=-11.6 EndY=21.2 EndZ=0
  constraints (6):
    c: Diameter(g0) = 3.2
    c: Symmetric(g-3,g-3,g1)
    c: Coincident(g2,g1)
    c: Horizontal(g2)
    c: DistanceX(g-4,g2) = 0
    c: Symmetric(g2,g1,g0)
FEATURE [Part::Extrusion] Extrude038  label="Extrude foro per fissaggio micro"
  Base = -> Sketch035
  Dir = (0,-1,2e-16)
  DirMode = 2
  FaceMakerClass = Part::FaceMakerBullseye
  FaceMakerMode = 3
  LengthFwd = 3
  LengthRev = 0
  Placement = pos=(0,8.6,0) rot=(0,0,1;0rad)
  Solid = true
  Symmetric = false
FEATURE [Sketcher::SketchObject] Sketch036  label="supporto per alimentatore"
  ArcFitTolerance = 1e-06
  AttachmentSupport = -> [XZ_Plane]
  ExternalGeometry = -> [Sketch,Sketch016,Sketch022]
  FullyConstrained = true
  MakeInternals = false
  MapMode = 5
  Placement = pos=(0,0,0) rot=(1,0,0;1.5708rad)
  sketch-geometry (5):
    g0: LineSegment StartX=-211.843 StartY=-50.0944 StartZ=0 EndX=-211.843 EndY=-80.4316 EndZ=0
    g1: LineSegment StartX=-211.843 StartY=-50.0944 StartZ=0 EndX=-207.775 EndY=-41.3701 EndZ=0
    g2: LineSegment [constr] StartX=-209.443 StartY=-50.0944 StartZ=0 EndX=-209.443 EndY=-80.4316 EndZ=0
    g3: LineSegment StartX=-207.775 StartY=-41.3701 StartZ=0 EndX=-207.775 EndY=-80.4316 EndZ=0
    g4: LineSegment StartX=-211.843 StartY=-80.4316 StartZ=0 EndX=-207.775 EndY=-80.4316 EndZ=0
  constraints (15):
    c: Vertical(g0)
    c: Coincident(g1,g0)
    c: Vertical(g2)
    c: Tangent(g2,g-5)
    c: Coincident(g3,g1)
    c: Vertical(g3)
    c: DistanceY(g-3,g3) = -2
    c: Tangent(g1,g-8)
    c: DistanceY(g-3,g0) = -2
    c: Coincident(g4,g0)
    c: Coincident(g4,g3)
    c: Tangent(g0,g-6)
    c: DistanceY(g-3,g2) = -2
    c: DistanceY(g2,g0) = 0
    c: DistanceX(g-3,g3) = 6.8
FEATURE [Part::Extrusion] Extrude039  label="Extrude039 supporto alimentatore"
  Base = -> Sketch036
  Dir = (0,-1,2e-16)
  DirMode = 2
  FaceMakerClass = Part::FaceMakerBullseye
  FaceMakerMode = 3
  LengthFwd = 25.2
  LengthRev = 0
  Solid = true
  Symmetric = true
FEATURE [Sketcher::SketchObject] Sketch037  label="scavo per alimentatore"
  ArcFitTolerance = 1e-06
  AttachmentSupport = -> [XZ_Plane]
  ExternalGeometry = -> [Sketch036]
  FullyConstrained = true
  MakeInternals = false
  MapMode = 5
  Placement = pos=(0,0,0) rot=(1,0,0;1.5708rad)
  sketch-geometry (4):
    g0: LineSegment StartX=-209.575 StartY=-50.4316 StartZ=0 EndX=-209.575 EndY=-80.4316 EndZ=0
    g1: LineSegment StartX=-209.575 StartY=-50.4316 StartZ=0 EndX=-207.775 EndY=-50.4316 EndZ=0
    g2: LineSegment StartX=-207.775 StartY=-50.4316 StartZ=0 EndX=-207.775 EndY=-80.4316 EndZ=0
    g3: LineSegment StartX=-207.775 StartY=-80.4316 StartZ=0 EndX=-209.575 EndY=-80.4316 EndZ=0
  constraints (11):
    c: Vertical(g0)
    c: Coincident(g1,g0)
    c: Horizontal(g1)
    c: Coincident(g2,g1)
    c: Vertical(g2)
    c: Coincident(g3,g2)
    c: Coincident(g3,g0)
    c: Horizontal(g3)
    c: DistanceX(g1,g1) = 1.8
    c: Coincident(g2,g-3)
    c: DistanceY(g2,g2) = 30
FEATURE [Part::Extrusion] Extrude040  label="Extrude040 scavo alimentatore"
  Base = -> Sketch037
  Dir = (0,-1,2e-16)
  DirMode = 2
  FaceMakerClass = Part::FaceMakerBullseye
  FaceMakerMode = 3
  LengthFwd = 19.5
  LengthRev = 0
  Solid = true
  Symmetric = true
FEATURE [Part::Extrusion] Extrude031  label="Extrude fermo per scheda micro"
  Base = -> Sketch033
  Dir = (0,-1,2e-16)
  DirMode = 2
  FaceMakerClass = Part::FaceMakerBullseye
  FaceMakerMode = 3
  LengthFwd = 3
  LengthRev = 0
  Placement = pos=(0,8.6,0) rot=(0,0,1;0rad)
  Solid = true
  Symmetric = false
FEATURE [Sketcher::SketchObject] Sketch038  label="scavo driver solenoide"
  ArcFitTolerance = 1e-06
  AttachmentSupport = -> [XZ_Plane]
  ExternalGeometry = -> [Sketch,Sketch036]
  FullyConstrained = true
  MakeInternals = false
  MapMode = 5
  Placement = pos=(0,0,0) rot=(1,0,0;1.5708rad)
  sketch-geometry (7):
    g0: LineSegment StartX=-192.222 StartY=-8.0175 StartZ=0 EndX=-194.941 EndY=-6.74965 EndZ=0
    g1: LineSegment StartX=-194.941 StartY=-6.74965 StartZ=0 EndX=-212.269 EndY=-43.9083 EndZ=0
    g2: LineSegment StartX=-192.222 StartY=-8.0175 StartZ=0 EndX=-188.779 EndY=-9.62345 EndZ=0
    g3: LineSegment StartX=-188.779 StartY=-9.62345 StartZ=0 EndX=-205.357 EndY=-45.1761 EndZ=0
    g4: LineSegment StartX=-205.357 StartY=-45.1761 StartZ=0 EndX=-209.55 EndY=-45.1761 EndZ=0
    g5: LineSegment [constr] StartX=-212.269 StartY=-43.9083 StartZ=0 EndX=-209.55 EndY=-45.1761 EndZ=0
    g6: LineSegment StartX=-212.269 StartY=-43.9083 StartZ=0 EndX=-209.55 EndY=-45.1761 EndZ=0
  constraints (20):
    c: Coincident(g1,g0)
    c: Coincident(g3,g2)
    c: Coincident(g4,g3)
    c: Distance(g2) = 3.8
    c: Distance(g1) = 41
    c: Coincident(g5,g1)
    c: Distance(g5) = 3
    c: Perpendicular(g5,g-3)
    c: Parallel(g1,g-3)
    c: Perpendicular(g1,g0)
    c: Distance(g0) = 3
    c: Coincident(g6,g1)
    c: Parallel(g3,g-3)
    c: Perpendicular(g2,g3)
    c: Coincident(g2,g0)
    c: Perpendicular(g-4,g4)
    c: PointOnObject(g5,g-3)
    c: Distance(g-3,g5) = 9.6
    c: Coincident(g4,g5)
    c: Coincident(g6,g4)
FEATURE [Part::Extrusion] Extrude041  label="Extrude scavo driver solenoide"
  Base = -> Sketch038
  Dir = (0,-1,2e-16)
  DirMode = 2
  FaceMakerClass = Part::FaceMakerBullseye
  FaceMakerMode = 3
  LengthFwd = 20.6
  LengthRev = 0
  Solid = true
  Symmetric = true
FEATURE [Sketcher::SketchObject] Sketch039  label="scavo per cavo usb per micro"
  ArcFitTolerance = 1e-06
  AttachmentSupport = -> [XZ_Plane]
  ExternalGeometry = -> [Sketch,Sketch016]
  FullyConstrained = true
  MakeInternals = false
  MapMode = 5
  Placement = pos=(0,0,0) rot=(1,0,0;1.5708rad)
  sketch-geometry (4):
    g0: LineSegment StartX=-82.51 StartY=36.4 StartZ=0 EndX=-74.51 EndY=36.4 EndZ=0
    g1: LineSegment StartX=-74.51 StartY=36.4 StartZ=0 EndX=-74.51 EndY=30.8 EndZ=0
    g2: LineSegment StartX=-74.51 StartY=30.8 StartZ=0 EndX=-82.51 EndY=30.8 EndZ=0
    g3: LineSegment StartX=-82.51 StartY=30.8 StartZ=0 EndX=-82.51 EndY=36.4 EndZ=0
  constraints (11):
    c: Coincident(g1,g0)
    c: Vertical(g1)
    c: Coincident(g2,g1)
    c: Horizontal(g2)
    c: Coincident(g3,g2)
    c: Coincident(g3,g0)
    c: Vertical(g3)
    c: Tangent(g0,g-3)
    c: Tangent(g2,g-4)
    c: Tangent(g3,g-4)
    c: Tangent(g1,g-4)
FEATURE [Part::Extrusion] Extrude042  label="Extrude scavo per cavo usb per micro"
  Base = -> Sketch039
  Dir = (0,-1,2e-16)
  DirMode = 2
  FaceMakerClass = Part::FaceMakerBullseye
  FaceMakerMode = 3
  LengthFwd = 11.2
  LengthRev = 0
  Solid = true
  Symmetric = true
FEATURE [Sketcher::SketchObject] Sketch040  label="scavo saldature alimentatore connettore 5v"
  ArcFitTolerance = 1e-06
  AttachmentSupport = -> [XZ_Plane]
  ExternalGeometry = -> [Sketch037]
  FullyConstrained = true
  MakeInternals = false
  MapMode = 5
  Placement = pos=(0,0,0) rot=(1,0,0;1.5708rad)
  sketch-geometry (4):
    g0: LineSegment StartX=-211.175 StartY=-52.4316 StartZ=0 EndX=-211.175 EndY=-56.4316 EndZ=0
    g1: LineSegment StartX=-211.175 StartY=-52.4316 StartZ=0 EndX=-209.575 EndY=-52.4316 EndZ=0
    g2: LineSegment StartX=-209.575 StartY=-52.4316 StartZ=0 EndX=-209.575 EndY=-56.4316 EndZ=0
    g3: LineSegment StartX=-209.575 StartY=-56.4316 StartZ=0 EndX=-211.175 EndY=-56.4316 EndZ=0
  constraints (11):
    c: Vertical(g0)
    c: Coincident(g1,g0)
    c: Horizontal(g1)
    c: Coincident(g2,g1)
    c: Coincident(g3,g2)
    c: Coincident(g3,g0)
    c: Horizontal(g3)
    c: DistanceX(g1,g1) = 1.6
    c: DistanceY(g2,g2) = 4
    c: Tangent(g2,g-3)
    c: DistanceY(g1,g-3) = 2
FEATURE [Part::Extrusion] Extrude043  label="Extrude scavo saldature alimentatore connettore 5v"
  Base = -> Sketch040
  Dir = (0,-1,2e-16)
  DirMode = 2
  FaceMakerClass = Part::FaceMakerBullseye
  FaceMakerMode = 3
  LengthFwd = 8
  LengthRev = 0
  Solid = true
  Symmetric = true
FEATURE [Sketcher::SketchObject] Sketch041  label="scavo saldature alimentatore connettore 5v verticali"
  ArcFitTolerance = 1e-06
  AttachmentSupport = -> [XZ_Plane]
  ExternalGeometry = -> [Sketch037]
  FullyConstrained = true
  MakeInternals = false
  MapMode = 5
  Placement = pos=(0,0,0) rot=(1,0,0;1.5708rad)
  sketch-geometry (4):
    g0: LineSegment StartX=-211.175 StartY=-53.6316 StartZ=0 EndX=-209.575 EndY=-53.6316 EndZ=0
    g1: LineSegment StartX=-209.575 StartY=-53.6316 StartZ=0 EndX=-209.575 EndY=-76.6316 EndZ=0
    g2: LineSegment StartX=-209.575 StartY=-76.6316 StartZ=0 EndX=-211.175 EndY=-76.6316 EndZ=0
    g3: LineSegment StartX=-211.175 StartY=-76.6316 StartZ=0 EndX=-211.175 EndY=-53.6316 EndZ=0
  constraints (11):
    c: Horizontal(g0)
    c: Coincident(g1,g0)
    c: Coincident(g2,g1)
    c: Horizontal(g2)
    c: Coincident(g3,g2)
    c: Coincident(g3,g0)
    c: Vertical(g3)
    c: DistanceY(g3,g3) = 23
    c: DistanceX(g0,g0) = 1.6
    c: Tangent(g1,g-3)
    c: DistanceY(g0,g-3) = 3.2
FEATURE [Part::Extrusion] Extrude044  label="Extrude scavo saldature alimentatore connettore 5v verticali"
  Base = -> Sketch041
  Dir = (0,-1,2e-16)
  DirMode = 2
  FaceMakerClass = Part::FaceMakerBullseye
  FaceMakerMode = 3
  LengthFwd = 3.2
  LengthRev = 0
  Placement = pos=(0,8.3,0) rot=(0,0,1;0rad)
  Solid = true
  Symmetric = false
FEATURE [Sketcher::SketchObject] Sketch042  label="fermi per driver solenoide e alimentatore"
  ArcFitTolerance = 1e-06
  AttachmentSupport = -> [XZ_Plane]
  ExternalGeometry = -> [Sketch036,Sketch037,Sketch,Sketch038]
  FullyConstrained = true
  MakeInternals = false
  MapMode = 5
  Placement = pos=(0,0,0) rot=(1,0,0;1.5708rad)
  sketch-geometry (27):
    g0: LineSegment StartX=-200.506 StartY=-25.7811 StartZ=0 EndX=-201.436 EndY=-27.775 EndZ=0
    g1: LineSegment StartX=-201.436 StartY=-27.775 StartZ=0 EndX=-199.442 EndY=-28.7048 EndZ=0
    g2: LineSegment StartX=-199.442 StartY=-28.7048 StartZ=0 EndX=-198.512 EndY=-26.7109 EndZ=0
    g3: LineSegment StartX=-198.512 StartY=-26.7109 StartZ=0 EndX=-200.506 EndY=-25.7811 EndZ=0
    g4: LineSegment StartX=-201.28 StartY=-23.6549 StartZ=0 EndX=-203.562 EndY=-28.5489 EndZ=0
    g5: LineSegment StartX=-203.562 StartY=-28.5489 StartZ=0 EndX=-200.118 EndY=-30.1549 EndZ=0
    g6: LineSegment StartX=-197.992 StartY=-29.381 StartZ=0 EndX=-197.062 EndY=-27.3871 EndZ=0
    g7: LineSegment StartX=-197.836 StartY=-25.2608 StartZ=0 EndX=-201.28 EndY=-23.6549 EndZ=0
    g8: LineSegment [constr] StartX=-198.668 StartY=-30.8311 StartZ=0 EndX=-197.992 EndY=-29.381 EndZ=0
    g9: LineSegment [constr] StartX=-198.668 StartY=-30.8311 StartZ=0 EndX=-200.118 EndY=-30.1549 EndZ=0
    g10: ArcOfCircle CenterX=-198.512 CenterY=-26.7109 CenterZ=0 NormalX=0 NormalY=0 NormalZ=1 AngleXU=0 Radius=1.6 StartAngle=5.84685 EndAngle=7.41765
    g11: GeomPoint [constr] X=-196.386 Y=-25.937 Z=0
    g12: ArcOfCircle CenterX=-199.442 CenterY=-28.7048 CenterZ=0 NormalX=0 NormalY=0 NormalZ=1 AngleXU=0 Radius=1.6 StartAngle=4.27606 EndAngle=5.84685
    g13: GeomPoint [constr] X=-198.668 Y=-30.8311 Z=0
    g14: LineSegment StartX=-207.775 StartY=-46.8316 StartZ=0 EndX=-207.775 EndY=-50.8316 EndZ=0
    g15: LineSegment StartX=-207.775 StartY=-46.8316 StartZ=0 EndX=-203.775 EndY=-46.8316 EndZ=0
    g16: LineSegment StartX=-203.775 StartY=-46.8316 StartZ=0 EndX=-203.775 EndY=-50.8316 EndZ=0
    g17: LineSegment StartX=-207.775 StartY=-50.8316 StartZ=0 EndX=-203.775 EndY=-50.8316 EndZ=0
    g18: LineSegment StartX=-209.375 StartY=-52.4316 StartZ=0 EndX=-203.775 EndY=-52.4316 EndZ=0
    g19: LineSegment StartX=-202.175 StartY=-50.8316 StartZ=0 EndX=-202.175 EndY=-46.8316 EndZ=0
    g20: LineSegment StartX=-203.775 StartY=-45.2316 StartZ=0 EndX=-209.375 EndY=-45.2316 EndZ=0
    g21: LineSegment StartX=-209.375 StartY=-45.2316 StartZ=0 EndX=-209.375 EndY=-52.4316 EndZ=0
    g22: ArcOfCircle CenterX=-203.775 CenterY=-46.8316 CenterZ=0 NormalX=0 NormalY=0 NormalZ=1 AngleXU=0 Radius=1.6 StartAngle=1.8e-15 EndAngle=1.5708
    g23: GeomPoint [constr] X=-202.175 Y=-45.2316 Z=0
    g24: ArcOfCircle CenterX=-203.775 CenterY=-50.8316 CenterZ=0 NormalX=0 NormalY=0 NormalZ=1 AngleXU=0 Radius=1.6 StartAngle=4.71239 EndAngle=6.28319
    g25: GeomPoint [constr] X=-202.175 Y=-52.4316 Z=0
    g26: LineSegment [constr] StartX=-207.775 StartY=-50.4316 StartZ=0 EndX=-207.775 EndY=-50.8316 EndZ=0
  constraints (69):
    c: Coincident(g1,g0)
    c: Coincident(g2,g1)
    c: Coincident(g3,g2)
    c: Coincident(g3,g0)
    c: Parallel(g0,g2)
    c: Perpendicular(g3,g0)
    c: Perpendicular(g1,g0)
    c: Coincident(g5,g4)
    c: Coincident(g7,g4)
    c: Distance(g3) = 2.2
    c: Distance(g2) = 2.2
    c: Parallel(g6,g2)
    c: Parallel(g6,g4)
    c: Perpendicular(g5,g6)
    c: Perpendicular(g7,g6)
    c: Distance(g13,g11) = 5.4
    c: Distance(g5,g13) = 5.4
    c: Coincident(g9,g8)
    c: Distance(g8) = 1.6
    c: Distance(g9) = 1.6
    c: Perpendicular(g9,g8)
    c: Parallel(g8,g6)
    c: Coincident(g8,g13)
    c: Distance(g8,g1) = 1.6
    c: Distance(g9,g1) = 1.6
    c: Tangent(g0,g-5)
    c: Distance(g0,g-6) = 19.2
    c: PointOnObject(g11,g7)
    c: PointOnObject(g11,g6)
    c: Tangent(g7,g10) = -1.5708
    c: Tangent(g6,g10) = -1.5708
    c: PointOnObject(g13,g5)
    c: Tangent(g5,g12) = -1.5708
    c: Tangent(g6,g12) = -1.5708
    c: Equal(g10,g12)
    c: Coincident(g10,g2)
    c: Vertical(g14)
    c: Coincident(g15,g14)
    c: Horizontal(g15)
    c: Coincident(g16,g15)
    c: Vertical(g16)
    c: Coincident(g17,g14)
    c: Coincident(g17,g16)
    c: Horizontal(g17)
    c: Distance(g16) = 4
    c: Distance(g15) = 4
    c: Horizontal(g18)
    c: Vertical(g19)
    c: Horizontal(g20)
    c: Coincident(g21,g20)
    c: Coincident(g21,g18)
    c: Vertical(g21)
    c: Distance(g20,g23) = 7.2
    c: Distance(g25,g23) = 7.2
    c: DistanceY(g18,g14) = 1.6
    c: DistanceX(g18,g14) = 1.6
    c: PointOnObject(g23,g20)
    c: PointOnObject(g23,g19)
    c: Tangent(g20,g22) = -1.5708
    c: Tangent(g19,g22) = -1.5708
    c: PointOnObject(g25,g19)
    c: Tangent(g18,g24) = -1.5708
    c: Tangent(g19,g24) = -1.5708
    c: Equal(g22,g24)
    c: Coincident(g22,g15)
    c: Vertical(g26)
    c: Distance(g26) = 0.4
    c: Coincident(g26,g-4)
    c: Coincident(g14,g26)
FEATURE [Part::Extrusion] Extrude045  label="Extrude fermi per driver solenoide e alimentatore"
  Base = -> Sketch042
  Dir = (0,-1,2e-16)
  DirMode = 2
  FaceMakerClass = Part::FaceMakerBullseye
  FaceMakerMode = 3
  LengthFwd = 25.2
  LengthRev = 0
  Solid = true
  Symmetric = true
FEATURE [Sketcher::SketchObject] Sketch043  label="scavo pulizia fermo alimentatore"
  ArcFitTolerance = 1e-06
  AttachmentSupport = -> [XZ_Plane]
  ExternalGeometry = -> [Sketch042,Sketch036,Sketch037]
  FullyConstrained = true
  MakeInternals = false
  MapMode = 5
  Placement = pos=(0,0,0) rot=(1,0,0;1.5708rad)
  sketch-geometry (6):
    g0: LineSegment StartX=-209.375 StartY=-52.4316 StartZ=0 EndX=-209.375 EndY=-50.4316 EndZ=0
    g1: LineSegment StartX=-209.375 StartY=-50.4316 StartZ=0 EndX=-207.775 EndY=-50.4316 EndZ=0
    g2: LineSegment StartX=-207.775 StartY=-50.4316 StartZ=0 EndX=-207.775 EndY=-45.2316 EndZ=0
    g3: LineSegment StartX=-207.775 StartY=-45.2316 StartZ=0 EndX=-202.175 EndY=-45.2316 EndZ=0
    g4: LineSegment StartX=-202.175 StartY=-45.2316 StartZ=0 EndX=-202.175 EndY=-52.4316 EndZ=0
    g5: LineSegment StartX=-202.175 StartY=-52.4316 StartZ=0 EndX=-209.375 EndY=-52.4316 EndZ=0
  constraints (13):
    c: Vertical(g0)
    c: Coincident(g1,g0)
    c: Coincident(g2,g1)
    c: Coincident(g3,g2)
    c: Coincident(g4,g3)
    c: Coincident(g5,g4)
    c: Coincident(g5,g0)
    c: Horizontal(g5)
    c: Coincident(g0,g-6)
    c: Tangent(g1,g-8)
    c: Tangent(g2,g-4)
    c: Tangent(g3,g-7)
    c: Tangent(g4,g-3)
FEATURE [Part::Extrusion] Extrude046  label="Extrude scavo pulizia fermo alimentatore"
  Base = -> Sketch043
  Dir = (0,-1,2e-16)
  DirMode = 2
  FaceMakerClass = Part::FaceMakerBullseye
  FaceMakerMode = 3
  LengthFwd = 19.5
  LengthRev = 0
  Solid = true
  Symmetric = true
FEATURE [Sketcher::SketchObject] Sketch044  label="buchini per fissaggio oled"
  ArcFitTolerance = 1e-06
  AttachmentSupport = -> [YZ_Plane]
  ExternalGeometry = -> [Sketch]
  FullyConstrained = true
  MakeInternals = false
  MapMode = 5
  Placement = pos=(0,0,0) rot=(0.57735,0.57735,0.57735;2.0944rad)
  sketch-geometry (5):
    g0: LineSegment [constr] StartX=1.5e-14 StartY=67.3588 StartZ=0 EndX=0 EndY=64.3588 EndZ=0
    g1: LineSegment [constr] StartX=0 StartY=64.3588 StartZ=0 EndX=10.4 EndY=64.3588 EndZ=0
    g2: LineSegment [constr] StartX=0 StartY=64.3588 StartZ=0 EndX=-10.4 EndY=64.3588 EndZ=0
    g3: Circle CenterX=10.4 CenterY=64.3588 CenterZ=0 NormalX=0 NormalY=0 NormalZ=1 AngleXU=0 Radius=1.5
    g4: Circle CenterX=-10.4 CenterY=64.3588 CenterZ=0 NormalX=0 NormalY=0 NormalZ=1 AngleXU=0 Radius=1.5
  constraints (13):
    c: Distance(g0) = 3
    c: PointOnObject(g0,g-2)
    c: Coincident(g1,g0)
    c: Horizontal(g1)
    c: Coincident(g2,g0)
    c: Horizontal(g2)
    c: DistanceX(g1,g1) = 10.4
    c: Coincident(g3,g1)
    c: Diameter(g4) = 3
    c: Coincident(g4,g2)
    c: Coincident(g0,g-7)
    c: Equal(g1,g2)
    c: Equal(g4,g3)
FEATURE [Part::Extrusion] Extrude047  label="Extrude buchini per fissaggio oled"
  Base = -> Sketch044
  Dir = (1,0,0)
  DirMode = 2
  FaceMakerClass = Part::FaceMakerBullseye
  FaceMakerMode = 3
  LengthFwd = 10
  LengthRev = 0
  Placement = pos=(-186,0,0) rot=(0,0,1;0rad)
  Solid = true
  Symmetric = false
FEATURE [Sketcher::SketchObject] Sketch046  label="scavo 5x5 neopixel"
  ArcFitTolerance = 1e-06
  AttachmentSupport = -> [YZ_Plane002]
  FullyConstrained = true
  MakeInternals = false
  MapMode = 5
  Placement = pos=(0,0,0) rot=(0.57735,0.57735,0.57735;2.0944rad)
  sketch-geometry (4):
    g0: LineSegment StartX=-2.7 StartY=2.7 StartZ=0 EndX=2.7 EndY=2.7 EndZ=0
    g1: LineSegment StartX=2.7 StartY=2.7 StartZ=0 EndX=2.7 EndY=-2.7 EndZ=0
    g2: LineSegment StartX=2.7 StartY=-2.7 StartZ=0 EndX=-2.7 EndY=-2.7 EndZ=0
    g3: LineSegment StartX=-2.7 StartY=-2.7 StartZ=0 EndX=-2.7 EndY=2.7 EndZ=0
  constraints (11):
    c: Horizontal(g0)
    c: Coincident(g1,g0)
    c: Vertical(g1)
    c: Coincident(g2,g1)
    c: Horizontal(g2)
    c: Coincident(g3,g2)
    c: Coincident(g3,g0)
    c: Vertical(g3)
    c: DistanceX(g0,g0) = 5.4
    c: DistanceY(g1,g1) = 5.4
    c: Symmetric(g0,g1,g-1)
FEATURE [Sketcher::SketchObject] Sketch047  label="scavo 10x10 neopixel corpo"
  ArcFitTolerance = 1e-06
  AttachmentOffset = pos=(0,0,1) rot=(0,0,1;0rad)
  AttachmentSupport = -> [YZ_Plane002]
  FullyConstrained = true
  MakeInternals = false
  MapMode = 5
  Placement = pos=(1,0,0) rot=(0.57735,0.57735,0.57735;2.0944rad)
  sketch-geometry (4):
    g0: LineSegment StartX=-5 StartY=5.1 StartZ=0 EndX=5 EndY=5.1 EndZ=0
    g1: LineSegment StartX=5 StartY=5.1 StartZ=0 EndX=5 EndY=-5.1 EndZ=0
    g2: LineSegment StartX=5 StartY=-5.1 StartZ=0 EndX=-5 EndY=-5.1 EndZ=0
    g3: LineSegment StartX=-5 StartY=-5.1 StartZ=0 EndX=-5 EndY=5.1 EndZ=0
  constraints (11):
    c: Horizontal(g0)
    c: Coincident(g1,g0)
    c: Vertical(g1)
    c: Coincident(g2,g1)
    c: Horizontal(g2)
    c: Coincident(g3,g2)
    c: Coincident(g3,g0)
    c: Vertical(g3)
    c: DistanceX(g0,g0) = 10
    c: DistanceY(g1,g1) = 10.2
    c: Symmetric(g0,g2,g-1)
FEATURE [Sketcher::SketchObject] Sketch048  label="buco per perno blocco neopixel"
  ArcFitTolerance = 1e-06
  AttachmentSupport = -> [XZ_Plane002]
  FullyConstrained = true
  MakeInternals = false
  MapMode = 5
  Placement = pos=(0,0,0) rot=(1,0,0;1.5708rad)
  sketch-geometry (4):
    g0: LineSegment StartX=3 StartY=1.2 StartZ=0 EndX=3 EndY=-1.2 EndZ=0
    g1: LineSegment StartX=3 StartY=-1.2 StartZ=0 EndX=5.4 EndY=-1.2 EndZ=0
    g2: LineSegment StartX=5.4 StartY=-1.2 StartZ=0 EndX=5.4 EndY=1.2 EndZ=0
    g3: LineSegment StartX=5.4 StartY=1.2 StartZ=0 EndX=3 EndY=1.2 EndZ=0
  constraints (11):
    c: Coincident(g1,g0)
    c: Horizontal(g1)
    c: Coincident(g2,g1)
    c: Vertical(g2)
    c: Coincident(g3,g2)
    c: Coincident(g3,g0)
    c: Horizontal(g3)
    c: DistanceX(g1,g1) = 2.4
    c: DistanceY(g2,g2) = 2.4
    c: Symmetric(g0,g0,g-1)
    c: DistanceX(g-1,g0) = 3
FEATURE [Sketcher::SketchObject] Sketch045  label="blocco principale per neopixel"
  ArcFitTolerance = 1e-06
  AttachmentSupport = -> [XZ_Plane002]
  ExternalGeometry = -> [Sketch048]
  FullyConstrained = true
  MakeInternals = false
  MapMode = 5
  Placement = pos=(0,0,0) rot=(1,0,0;1.5708rad)
  sketch-geometry (6):
    g0: LineSegment StartX=0 StartY=5.1 StartZ=0 EndX=0 EndY=-5.1 EndZ=0
    g1: LineSegment StartX=0 StartY=-5.1 StartZ=0 EndX=3 EndY=-5.1 EndZ=0
    g2: LineSegment StartX=7 StartY=-1.1 StartZ=0 EndX=7 EndY=5.1 EndZ=0
    g3: LineSegment StartX=7 StartY=5.1 StartZ=0 EndX=0 EndY=5.1 EndZ=0
    g4: ArcOfCircle CenterX=3 CenterY=-1.1 CenterZ=0 NormalX=0 NormalY=0 NormalZ=1 AngleXU=0 Radius=4 StartAngle=4.71239 EndAngle=6.28319
    g5: GeomPoint [constr] X=7 Y=-5.1 Z=0
  constraints (15):
    c: Vertical(g0)
    c: Coincident(g1,g0)
    c: Horizontal(g1)
    c: Vertical(g2)
    c: Coincident(g3,g2)
    c: Coincident(g3,g0)
    c: Horizontal(g3)
    c: DistanceY(g0,g0) = 10.2
    c: Symmetric(g0,g0,g-1)
    c: DistanceX(g3,g3) = 7
    c: PointOnObject(g5,g2)
    c: PointOnObject(g5,g1)
    c: Tangent(g2,g4) = -1.5708
    c: Tangent(g1,g4) = -1.5708
    c: DistanceX(g-3,g1) = 0
FEATURE [Sketcher::SketchObject] Sketch049  label="rinforzi esterni per corpo neopoixel"
  ArcFitTolerance = 1e-06
  AttachmentSupport = -> [XZ_Plane002]
  ExternalGeometry = -> [Sketch045]
  FullyConstrained = true
  MakeInternals = false
  MapMode = 5
  Placement = pos=(0,0,0) rot=(1,0,0;1.5708rad)
  sketch-geometry (8):
    g0: LineSegment StartX=1 StartY=-4.1 StartZ=0 EndX=2 EndY=-4.1 EndZ=0
    g1: LineSegment StartX=2 StartY=-4.1 StartZ=0 EndX=2 EndY=-5.1 EndZ=0
    g2: LineSegment StartX=2 StartY=-5.1 StartZ=0 EndX=1 EndY=-5.1 EndZ=0
    g3: LineSegment StartX=1 StartY=-5.1 StartZ=0 EndX=1 EndY=-4.1 EndZ=0
    g4: LineSegment StartX=1 StartY=5.1 StartZ=0 EndX=2 EndY=5.1 EndZ=0
    g5: LineSegment StartX=2 StartY=5.1 StartZ=0 EndX=2 EndY=4.1 EndZ=0
    g6: LineSegment StartX=2 StartY=4.1 StartZ=0 EndX=1 EndY=4.1 EndZ=0
    g7: LineSegment StartX=1 StartY=4.1 StartZ=0 EndX=1 EndY=5.1 EndZ=0
  constraints (24):
    c: Horizontal(g0)
    c: Coincident(g1,g0)
    c: Vertical(g1)
    c: Coincident(g2,g1)
    c: Horizontal(g2)
    c: Coincident(g3,g2)
    c: Coincident(g3,g0)
    c: Vertical(g3)
    c: Horizontal(g4)
    c: Coincident(g5,g4)
    c: Vertical(g5)
    c: Coincident(g6,g5)
    c: Horizontal(g6)
    c: Coincident(g7,g6)
    c: Coincident(g7,g4)
    c: Vertical(g7)
    c: DistanceX(g4,g4) = 1
    c: DistanceY(g5,g5) = 1
    c: DistanceX(g0,g0) = 1
    c: DistanceY(g1,g1) = 1
    c: DistanceX(g-3,g4) = 1
    c: DistanceY(g-3,g4) = 0
    c: DistanceX(g-4,g2) = 1
    c: DistanceY(g2,g-4) = 0
FEATURE [Sketcher::SketchObject] Sketch052  label="scavo saldature driver solenoide"
  ArcFitTolerance = 1e-06
  AttachmentSupport = -> [XZ_Plane]
  ExternalGeometry = -> [Sketch038]
  FullyConstrained = true
  MakeInternals = false
  MapMode = 5
  Placement = pos=(0,0,0) rot=(1,0,0;1.5708rad)
  sketch-geometry (4):
    g0: LineSegment StartX=-195.304 StartY=-6.5806 StartZ=0 EndX=-196.994 EndY=-10.2058 EndZ=0
    g1: LineSegment StartX=-196.994 StartY=-10.2058 StartZ=0 EndX=-196.632 EndY=-10.3749 EndZ=0
    g2: LineSegment StartX=-196.632 StartY=-10.3749 StartZ=0 EndX=-194.941 EndY=-6.74965 EndZ=0
    g3: LineSegment StartX=-194.941 StartY=-6.74965 StartZ=0 EndX=-195.304 EndY=-6.5806 EndZ=0
  constraints (11):
    c: Coincident(g1,g0)
    c: Coincident(g2,g1)
    c: Coincident(g3,g2)
    c: Coincident(g3,g0)
    c: Parallel(g2,g0)
    c: Perpendicular(g2,g3)
    c: Perpendicular(g1,g2,g1) = 1.5708
    c: Parallel(g2,g-3)
    c: Distance(g2) = 4
    c: Distance(g3) = 0.4
    c: Coincident(g2,g-3)
FEATURE [Part::Extrusion] Extrude055  label="Extrude scavo saldature driver solenoide"
  Base = -> Sketch052
  Dir = (0,-1,2e-16)
  DirMode = 2
  FaceMakerClass = Part::FaceMakerBullseye
  FaceMakerMode = 3
  LengthFwd = 6
  LengthRev = 0
  Solid = true
  Symmetric = true
FEATURE [Sketcher::SketchObject] Sketch053  label="scavo saldature rumble"
  ArcFitTolerance = 1e-06
  AttachmentSupport = -> [XZ_Plane]
  ExternalGeometry = -> [Sketch019]
  FullyConstrained = true
  MakeInternals = false
  MapMode = 5
  Placement = pos=(0,0,0) rot=(1,0,0;1.5708rad)
  sketch-geometry (4):
    g0: LineSegment StartX=-164.507 StartY=-41.6446 StartZ=0 EndX=-165.743 EndY=-45.4488 EndZ=0
    g1: LineSegment StartX=-165.743 StartY=-45.4488 StartZ=0 EndX=-164.602 EndY=-45.8196 EndZ=0
    g2: LineSegment StartX=-164.602 StartY=-45.8196 StartZ=0 EndX=-163.366 EndY=-42.0154 EndZ=0
    g3: LineSegment StartX=-163.366 StartY=-42.0154 StartZ=0 EndX=-164.507 EndY=-41.6446 EndZ=0
  constraints (11):
    c: Coincident(g1,g0)
    c: Coincident(g2,g1)
    c: Coincident(g3,g2)
    c: Coincident(g3,g0)
    c: Parallel(g0,g2)
    c: Perpendicular(g3,g0)
    c: Perpendicular(g1,g0)
    c: Parallel(g0,g-3)
    c: Distance(g0) = 4
    c: Distance(g1) = 1.2
    c: Coincident(g0,g-3)
FEATURE [Part::Extrusion] Extrude056  label="Extrude scavo saldature rumble"
  Base = -> Sketch053
  Dir = (0,-1,2e-16)
  DirMode = 2
  FaceMakerClass = Part::FaceMakerBullseye
  FaceMakerMode = 3
  LengthFwd = 8.4
  LengthRev = 0
  Solid = true
  Symmetric = true
FEATURE [Sketcher::SketchObject] Sketch054  label="scavo saldature alimentatore connettore USB"
  ArcFitTolerance = 1e-06
  AttachmentSupport = -> [XZ_Plane]
  ExternalGeometry = -> [Sketch037]
  FullyConstrained = true
  MakeInternals = false
  MapMode = 5
  Placement = pos=(0,0,0) rot=(1,0,0;1.5708rad)
  sketch-geometry (4):
    g0: LineSegment StartX=-209.575 StartY=-80.4316 StartZ=0 EndX=-210.375 EndY=-80.4316 EndZ=0
    g1: LineSegment StartX=-210.375 StartY=-80.4316 StartZ=0 EndX=-210.375 EndY=-72.4316 EndZ=0
    g2: LineSegment StartX=-210.375 StartY=-72.4316 StartZ=0 EndX=-209.575 EndY=-72.4316 EndZ=0
    g3: LineSegment StartX=-209.575 StartY=-72.4316 StartZ=0 EndX=-209.575 EndY=-80.4316 EndZ=0
  constraints (11):
    c: Horizontal(g0)
    c: Coincident(g1,g0)
    c: Vertical(g1)
    c: Coincident(g2,g1)
    c: Horizontal(g2)
    c: Coincident(g3,g2)
    c: Coincident(g3,g0)
    c: Vertical(g3)
    c: DistanceX(g0,g0) = 0.8
    c: DistanceY(g3,g3) = 8
    c: Coincident(g0,g-4)
FEATURE [Part::Extrusion] Extrude057  label="Extrude scavo saldature alimentatore connettore USB"
  Base = -> Sketch054
  Dir = (0,-1,2e-16)
  DirMode = 2
  FaceMakerClass = Part::FaceMakerBullseye
  FaceMakerMode = 3
  LengthFwd = 11
  LengthRev = 0
  Solid = true
  Symmetric = true
FEATURE [Sketcher::SketchObject] Sketch055  label="buco interno per micro switch"
  ArcFitTolerance = 1e-06
  AttachmentSupport = -> [XZ_Plane]
  ExternalGeometry = -> [Sketch]
  FullyConstrained = true
  MakeInternals = false
  MapMode = 5
  Placement = pos=(0,0,0) rot=(1,0,0;1.5708rad)
  sketch-geometry (11):
    g0: LineSegment [constr] StartX=-194.483 StartY=34.2854 StartZ=0 EndX=-196.022 EndY=30.0568 EndZ=0
    g1: LineSegment [constr] StartX=-196.022 StartY=30.0568 StartZ=0 EndX=-197.561 EndY=25.8282 EndZ=0
    g2: LineSegment [constr] StartX=-196.022 StartY=30.0568 StartZ=0 EndX=-194.143 EndY=29.3727 EndZ=0
    g3: LineSegment [constr] StartX=-196.022 StartY=30.0568 StartZ=0 EndX=-197.902 EndY=30.7408 EndZ=0
    g4: LineSegment StartX=-196.362 StartY=34.9694 StartZ=0 EndX=-192.604 EndY=33.6014 EndZ=0
    g5: LineSegment StartX=-199.441 StartY=26.5122 StartZ=0 EndX=-195.682 EndY=25.1441 EndZ=0
    g6: LineSegment StartX=-192.604 StartY=33.6014 StartZ=0 EndX=-195.682 EndY=25.1441 EndZ=0
    g7: LineSegment StartX=-196.362 StartY=34.9694 StartZ=0 EndX=-199.441 EndY=26.5122 EndZ=0
    g8: GeomPoint [constr] X=-187.821 Y=29.2 Z=0
    g9: LineSegment [constr] StartX=-188.505 StartY=27.3206 StartZ=0 EndX=-196.022 EndY=30.0568 EndZ=0
    g10: LineSegment [constr] StartX=-187.821 StartY=29.2 StartZ=0 EndX=-188.505 EndY=27.3206 EndZ=0
  constraints (27):
    c: Coincident(g2,g0)
    c: Parallel(g0,g-3)
    c: Tangent(g1,g0) = -1.5708
    c: Perpendicular(g0,g2)
    c: Tangent(g2,g3)
    c: Distance(g0,g1) = 9
    c: Equal(g0,g1)
    c: Distance(g3,g2) = 4
    c: Equal(g2,g3)
    c: Parallel(g3,g4)
    c: Symmetric(g4,g4,g0)
    c: Parallel(g6,g1)
    c: Parallel(g7,g1)
    c: Symmetric(g6,g6,g2)
    c: Symmetric(g5,g5,g1)
    c: Symmetric(g7,g7,g3)
    c: Coincident(g7,g4)
    c: Coincident(g6,g4)
    c: Coincident(g5,g6)
    c: Symmetric(g-3,g-3,g8)
    c: Perpendicular(g-3,g9)
    c: Distance(g9) = 8
    c: Coincident(g3,g9)
    c: Coincident(g10,g8)
    c: Parallel(g10,g-3)
    c: Distance(g10) = 2
    c: Coincident(g10,g9)
FEATURE [Sketcher::SketchObject] Sketch056  label="buco esterno per micro switch"
  ArcFitTolerance = 1e-06
  AttachmentSupport = -> [XZ_Plane]
  ExternalGeometry = -> [Sketch055]
  FullyConstrained = true
  MakeInternals = false
  MapMode = 5
  Placement = pos=(0,0,0) rot=(1,0,0;1.5708rad)
  sketch-geometry (17):
    g0: GeomPoint [constr] X=-194.143 Y=29.3727 Z=0
    g1: GeomPoint [constr] X=-194.483 Y=34.2854 Z=0
    g2: GeomPoint [constr] X=-197.902 Y=30.7408 Z=0
    g3: GeomPoint [constr] X=-197.561 Y=25.8282 Z=0
    g4: GeomPoint [constr] X=-196.022 Y=30.0568 Z=0
    g5: LineSegment [constr] StartX=-194.483 StartY=34.2854 StartZ=0 EndX=-196.022 EndY=30.0568 EndZ=0
    g6: LineSegment [constr] StartX=-196.022 StartY=30.0568 StartZ=0 EndX=-197.561 EndY=25.8282 EndZ=0
    g7: LineSegment [constr] StartX=-197.902 StartY=30.7408 StartZ=0 EndX=-196.022 EndY=30.0568 EndZ=0
    g8: LineSegment [constr] StartX=-196.022 StartY=30.0568 StartZ=0 EndX=-194.143 EndY=29.3727 EndZ=0
    g9: LineSegment [constr] StartX=-195.338 StartY=31.9362 StartZ=0 EndX=-196.022 EndY=30.0568 EndZ=0
    g10: LineSegment [constr] StartX=-196.022 StartY=30.0568 StartZ=0 EndX=-196.706 EndY=28.1774 EndZ=0
    g11: LineSegment [constr] StartX=-196.022 StartY=30.0568 StartZ=0 EndX=-196.821 EndY=30.3475 EndZ=0
    g12: LineSegment [constr] StartX=-196.022 StartY=30.0568 StartZ=0 EndX=-195.223 EndY=29.7661 EndZ=0
    g13: LineSegment StartX=-194.539 StartY=31.6454 StartZ=0 EndX=-195.907 EndY=27.8867 EndZ=0
    g14: LineSegment StartX=-196.137 StartY=32.2269 StartZ=0 EndX=-197.505 EndY=28.4681 EndZ=0
    g15: LineSegment StartX=-196.137 StartY=32.2269 StartZ=0 EndX=-194.539 EndY=31.6454 EndZ=0
    g16: LineSegment StartX=-197.505 StartY=28.4681 StartZ=0 EndX=-195.907 EndY=27.8867 EndZ=0
  constraints (34):
    c: Symmetric(g-5,g-5,g1)
    c: Symmetric(g-5,g-6,g0)
    c: Symmetric(g-6,g-6,g3)
    c: Symmetric(g-5,g-6,g2)
    c: Coincident(g5,g1)
    c: Coincident(g5,g4)
    c: Coincident(g6,g4)
    c: Coincident(g6,g3)
    c: Equal(g5,g6)
    c: Coincident(g7,g2)
    c: Coincident(g7,g4)
    c: Coincident(g8,g4)
    c: Coincident(g8,g0)
    c: Equal(g7,g8)
    c: Coincident(g11,g9)
    c: Coincident(g12,g9)
    c: Tangent(g10,g9) = -1.5708
    c: Perpendicular(g11,g9)
    c: Parallel(g9,g-4)
    c: Equal(g9,g10)
    c: Parallel(g12,g11)
    c: Equal(g11,g12)
    c: Distance(g11,g12) = 1.7
    c: Distance(g9,g10) = 4
    c: Symmetric(g13,g13,g12)
    c: Parallel(g13,g9)
    c: Symmetric(g14,g14,g11)
    c: Symmetric(g15,g15,g9)
    c: Parallel(g15,g11)
    c: Symmetric(g16,g16,g10)
    c: Coincident(g16,g14)
    c: Coincident(g15,g14)
    c: Coincident(g13,g15)
    c: Coincident(g9,g4)
FEATURE [Sketcher::SketchObject] Sketch057  label="buco interno per SWITCH"
  ArcFitTolerance = 1e-06
  AttachmentSupport = -> [XZ_Plane]
  ExternalGeometry = -> [Sketch]
  FullyConstrained = true
  MakeInternals = false
  MapMode = 5
  Placement = pos=(0,0,0) rot=(1,0,0;1.5708rad)
  sketch-geometry (10):
    g0: GeomPoint [constr] X=-187.821 Y=29.2 Z=0
    g1: LineSegment [constr] StartX=-188.505 StartY=27.3206 StartZ=0 EndX=-193.203 EndY=29.0307 EndZ=0
    g2: LineSegment [constr] StartX=-190.809 StartY=35.6086 StartZ=0 EndX=-195.597 EndY=22.4529 EndZ=0
    g3: GeomPoint [constr] X=-193.203 Y=29.0307 Z=0
    g4: LineSegment [constr] StartX=-196.492 StartY=30.2278 StartZ=0 EndX=-189.914 EndY=27.8336 EndZ=0
    g5: LineSegment StartX=-194.098 StartY=36.8056 StartZ=0 EndX=-187.52 EndY=34.4115 EndZ=0
    g6: LineSegment StartX=-194.098 StartY=36.8056 StartZ=0 EndX=-198.886 EndY=23.6499 EndZ=0
    g7: LineSegment StartX=-187.52 StartY=34.4115 StartZ=0 EndX=-192.308 EndY=21.2558 EndZ=0
    g8: LineSegment StartX=-198.886 StartY=23.6499 StartZ=0 EndX=-192.308 EndY=21.2558 EndZ=0
    g9: LineSegment [constr] StartX=-187.821 StartY=29.2 StartZ=0 EndX=-188.505 EndY=27.3206 EndZ=0
  constraints (23):
    c: Symmetric(g-3,g-3,g0)
    c: Perpendicular(g1,g-3)
    c: Parallel(g2,g-3)
    c: Symmetric(g2,g2,g3)
    c: Perpendicular(g2,g4)
    c: Symmetric(g4,g4,g3)
    c: Distance(g2) = 14
    c: Distance(g4) = 7
    c: Distance(g1) = 5
    c: Parallel(g5,g4)
    c: Parallel(g7,g2)
    c: Symmetric(g5,g5,g2)
    c: Symmetric(g6,g6,g4)
    c: Symmetric(g7,g7,g4)
    c: Symmetric(g8,g8,g2)
    c: Coincident(g6,g5)
    c: Coincident(g7,g5)
    c: Coincident(g8,g7)
    c: Coincident(g3,g1)
    c: Coincident(g9,g0)
    c: Parallel(g9,g-3)
    c: Distance(g9) = 2
    c: Coincident(g1,g9)
FEATURE [Sketcher::SketchObject] Sketch058  label="buco esterno per SWITCH"
  ArcFitTolerance = 1e-06
  AttachmentSupport = -> [XZ_Plane]
  ExternalGeometry = -> [Sketch057]
  FullyConstrained = true
  MakeInternals = false
  MapMode = 5
  Placement = pos=(0,0,0) rot=(1,0,0;1.5708rad)
  sketch-geometry (12):
    g0: GeomPoint [constr] X=-190.809 Y=35.6086 Z=0
    g1: GeomPoint [constr] X=-196.492 Y=30.2278 Z=0
    g2: GeomPoint [constr] X=-189.914 Y=27.8336 Z=0
    g3: GeomPoint [constr] X=-195.597 Y=22.4529 Z=0
    g4: GeomPoint [constr] X=-193.203 Y=29.0307 Z=0
    g5: LineSegment [constr] StartX=-192.006 StartY=32.3196 StartZ=0 EndX=-194.4 EndY=25.7418 EndZ=0
    g6: GeomPoint [constr] X=-193.203 Y=29.0307 Z=0
    g7: LineSegment [constr] StartX=-195.082 StartY=29.7148 StartZ=0 EndX=-191.324 EndY=28.3467 EndZ=0
    g8: LineSegment StartX=-193.885 StartY=33.0037 StartZ=0 EndX=-190.127 EndY=31.6356 EndZ=0
    g9: LineSegment StartX=-190.127 StartY=31.6356 StartZ=0 EndX=-192.521 EndY=25.0578 EndZ=0
    g10: LineSegment StartX=-196.28 StartY=26.4258 StartZ=0 EndX=-192.521 EndY=25.0578 EndZ=0
    g11: LineSegment StartX=-193.885 StartY=33.0037 StartZ=0 EndX=-196.28 EndY=26.4258 EndZ=0
  constraints (21):
    c: Symmetric(g-6,g-6,g3)
    c: Symmetric(g-4,g-6,g2)
    c: Symmetric(g-5,g-4,g0)
    c: Symmetric(g-5,g-6,g1)
    c: Symmetric(g1,g2,g4)
    c: Parallel(g5,g-4)
    c: Symmetric(g5,g5,g6)
    c: Perpendicular(g7,g5)
    c: Symmetric(g7,g7,g6)
    c: Distance(g5) = 7
    c: Distance(g7) = 4
    c: Parallel(g8,g7)
    c: Parallel(g11,g5)
    c: Symmetric(g8,g8,g5)
    c: Symmetric(g9,g9,g7)
    c: Symmetric(g10,g10,g5)
    c: Symmetric(g11,g11,g7)
    c: Coincident(g11,g8)
    c: Coincident(g9,g8)
    c: Coincident(g9,g10)
    c: Coincident(g6,g4)
FEATURE [Part::Extrusion] Extrude060  label="Extrude buco interno per SWITCH destro"
  Base = -> Sketch057
  Dir = (0,-1,2e-16)
  DirMode = 2
  FaceMakerClass = Part::FaceMakerBullseye
  FaceMakerMode = 3
  LengthFwd = 13.2
  LengthRev = 0
  Placement = pos=(0,2.6,0) rot=(0,0,1;0rad)
  Solid = true
  Symmetric = false
FEATURE [Part::Extrusion] Extrude061  label="Extrude buco esterno per SWITCH destro"
  Base = -> Sketch058
  Dir = (0,-1,2e-16)
  DirMode = 2
  FaceMakerClass = Part::FaceMakerBullseye
  FaceMakerMode = 3
  LengthFwd = 2
  LengthRev = 0
  Placement = pos=(0,-10.6,0) rot=(0,0,1;0rad)
  Solid = true
  Symmetric = false
FEATURE [Sketcher::SketchObject] Sketch059  label="buco per spazio introduzione SWITCH"
  ArcFitTolerance = 1e-06
  AttachmentSupport = -> [XZ_Plane]
  ExternalGeometry = -> [Sketch057,Sketch010]
  FullyConstrained = true
  MakeInternals = false
  MapMode = 5
  Placement = pos=(0,0,0) rot=(1,0,0;1.5708rad)
  sketch-geometry (8):
    g0: LineSegment [constr] StartX=-201.368 StartY=36.3521 StartZ=0 EndX=-195.094 EndY=34.0687 EndZ=0
    g1: LineSegment [constr] StartX=-194.098 StartY=36.8056 StartZ=0 EndX=-195.094 EndY=34.0687 EndZ=0
    g2: LineSegment StartX=-198.658 StartY=24.2771 StartZ=0 EndX=-199.654 EndY=21.5401 EndZ=0
    g3: LineSegment StartX=-199.654 StartY=21.5401 StartZ=0 EndX=-181.196 EndY=14.822 EndZ=0
    g4: LineSegment StartX=-181.196 StartY=14.822 StartZ=0 EndX=-180.2 EndY=17.559 EndZ=0
    g5: LineSegment StartX=-180.2 StartY=17.559 StartZ=0 EndX=-198.658 EndY=24.2771 EndZ=0
    g6: LineSegment [constr] StartX=-204.932 StartY=26.5605 StartZ=0 EndX=-198.658 EndY=24.2771 EndZ=0
    g7: LineSegment [constr] StartX=-198.658 StartY=24.2771 StartZ=0 EndX=-199.654 EndY=21.5401 EndZ=0
  constraints (20):
    c: Parallel(g1,g-3)
    c: Parallel(g0,g-4)
    c: Coincident(g0,g-4)
    c: Coincident(g1,g-3)
    c: Coincident(g0,g1)
    c: Coincident(g3,g2)
    c: Coincident(g4,g3)
    c: Coincident(g5,g4)
    c: Coincident(g5,g2)
    c: Parallel(g5,g-5)
    c: Parallel(g3,g-5)
    c: Parallel(g4,g-6)
    c: DistanceX(g-6,g4) = 0
    c: Coincident(g6,g-5)
    c: Equal(g6,g0)
    c: Coincident(g7,g6)
    c: Equal(g7,g1)
    c: Tangent(g7,g-3)
    c: Coincident(g2,g6)
    c: Coincident(g2,g7)
FEATURE [Part::Extrusion] Extrude062  label="Extrude buco per spazio introduzione SWITCH"
  Base = -> Sketch059
  Dir = (0,-1,2e-16)
  DirMode = 2
  FaceMakerClass = Part::FaceMakerBullseye
  FaceMakerMode = 3
  LengthFwd = 13.2
  LengthRev = 0
  Solid = true
  Symmetric = true
FEATURE [Part::Extrusion] Extrude063  label="Extrude buco interno per SWITCH sinistro"
  Base = -> Sketch057
  Dir = (0,-1,2e-16)
  DirMode = 2
  FaceMakerClass = Part::FaceMakerBullseye
  FaceMakerMode = 3
  LengthFwd = 13.2
  LengthRev = 0
  Placement = pos=(0,10.6,0) rot=(0,0,1;0rad)
  Solid = true
  Symmetric = false
FEATURE [Part::Extrusion] Extrude064  label="Extrude buco esterno per SWITCH sinistro"
  Base = -> Sketch058
  Dir = (0,-1,2e-16)
  DirMode = 2
  FaceMakerClass = Part::FaceMakerBullseye
  FaceMakerMode = 3
  LengthFwd = 2
  LengthRev = 0
  Placement = pos=(0,12.6,0) rot=(0,0,1;0rad)
  Solid = true
  Symmetric = false
FEATURE [Sketcher::SketchObject] Sketch061  label="struttura esterna blocco switch"
  ArcFitTolerance = 1e-06
  AttachmentSupport = -> [XZ_Plane003]
  FullyConstrained = true
  MakeInternals = false
  MapMode = 5
  Placement = pos=(0,0,0) rot=(1,0,0;1.5708rad)
  sketch-geometry (5):
    g0: LineSegment StartX=-1 StartY=-5.1 StartZ=0 EndX=1 EndY=-5.1 EndZ=0
    g1: LineSegment StartX=1 StartY=-5.1 StartZ=0 EndX=1 EndY=5.1 EndZ=0
    g2: LineSegment StartX=1 StartY=5.1 StartZ=0 EndX=-1 EndY=5.1 EndZ=0
    g3: LineSegment StartX=-1 StartY=5.1 StartZ=0 EndX=-1 EndY=-5.1 EndZ=0
    g4: GeomPoint [constr] X=0 Y=0 Z=0
  constraints (12):
    c: Coincident(g0,g1)
    c: Coincident(g1,g2)
    c: Coincident(g2,g3)
    c: Coincident(g3,g0)
    c: Horizontal(g0)
    c: Horizontal(g2)
    c: Vertical(g1)
    c: Vertical(g3)
    c: Symmetric(g2,g0,g4)
    c: Distance(g1,g3) = 2
    c: Distance(g0,g2) = 10.2
    c: Coincident(g4,g-1)
FEATURE [Sketcher::SketchObject] Sketch062  label="struttura interna blocco switch"
  ArcFitTolerance = 1e-06
  AttachmentSupport = -> [XZ_Plane003]
  ExternalGeometry = -> [Sketch061]
  FullyConstrained = true
  MakeInternals = false
  MapMode = 5
  Placement = pos=(0,0,0) rot=(1,0,0;1.5708rad)
  sketch-geometry (5):
    g0: LineSegment StartX=-1 StartY=3.1 StartZ=0 EndX=-1 EndY=-3.1 EndZ=0
    g1: LineSegment StartX=-1 StartY=-3.1 StartZ=0 EndX=1 EndY=-3.1 EndZ=0
    g2: LineSegment StartX=1 StartY=-3.1 StartZ=0 EndX=1 EndY=3.1 EndZ=0
    g3: LineSegment StartX=1 StartY=3.1 StartZ=0 EndX=-1 EndY=3.1 EndZ=0
    g4: GeomPoint [constr] X=0 Y=0 Z=0
  constraints (12):
    c: Coincident(g0,g1)
    c: Coincident(g1,g2)
    c: Coincident(g2,g3)
    c: Coincident(g3,g0)
    c: Vertical(g0)
    c: Vertical(g2)
    c: Horizontal(g1)
    c: Horizontal(g3)
    c: Symmetric(g2,g0,g4)
    c: Coincident(g4,g-1)
    c: Distance(g0) = 6.2
    c: Equal(g3,g-3)
FEATURE [Sketcher::SketchObject] Sketch063  label="blocchi tra switch"
  ArcFitTolerance = 1e-06
  AttachmentSupport = -> [XZ_Plane003]
  ExternalGeometry = -> [Sketch061,Sketch062]
  FullyConstrained = true
  MakeInternals = false
  MapMode = 5
  Placement = pos=(0,0,0) rot=(1,0,0;1.5708rad)
  sketch-geometry (8):
    g0: LineSegment StartX=-3 StartY=5.1 StartZ=0 EndX=-1 EndY=5.1 EndZ=0
    g1: LineSegment StartX=-1 StartY=5.1 StartZ=0 EndX=-1 EndY=3.1 EndZ=0
    g2: LineSegment StartX=-1 StartY=3.1 StartZ=0 EndX=-3 EndY=3.1 EndZ=0
    g3: LineSegment StartX=-3 StartY=3.1 StartZ=0 EndX=-3 EndY=5.1 EndZ=0
    g4: LineSegment StartX=-3 StartY=-3.1 StartZ=0 EndX=-1 EndY=-3.1 EndZ=0
    g5: LineSegment StartX=-1 StartY=-3.1 StartZ=0 EndX=-1 EndY=-5.1 EndZ=0
    g6: LineSegment StartX=-1 StartY=-5.1 StartZ=0 EndX=-3 EndY=-5.1 EndZ=0
    g7: LineSegment StartX=-3 StartY=-5.1 StartZ=0 EndX=-3 EndY=-3.1 EndZ=0
  constraints (20):
    c: Horizontal(g0)
    c: Coincident(g1,g0)
    c: Coincident(g2,g1)
    c: Horizontal(g2)
    c: Coincident(g3,g2)
    c: Coincident(g3,g0)
    c: Vertical(g3)
    c: Horizontal(g4)
    c: Coincident(g5,g4)
    c: Coincident(g6,g5)
    c: Horizontal(g6)
    c: Coincident(g7,g6)
    c: Coincident(g7,g4)
    c: Vertical(g7)
    c: Coincident(g0,g-4)
    c: Coincident(g1,g-5)
    c: Coincident(g4,g-6)
    c: Coincident(g5,g-7)
    c: Distance(g0) = 2
    c: Distance(g4) = 2
FEATURE [Sketcher::SketchObject] Sketch066  label="piano per rampino"
  ArcFitTolerance = 1e-06
  AttachmentSupport = -> [XZ_Plane002]
  ExternalGeometry = -> [Sketch045]
  FullyConstrained = true
  MakeInternals = false
  MapMode = 5
  Placement = pos=(0,0,0) rot=(1,0,0;1.5708rad)
  sketch-geometry (4):
    g0: LineSegment StartX=5.4 StartY=5.1 StartZ=0 EndX=5.4 EndY=3.9 EndZ=0
    g1: LineSegment StartX=5.4 StartY=3.9 StartZ=0 EndX=7 EndY=3.9 EndZ=0
    g2: LineSegment StartX=7 StartY=3.9 StartZ=0 EndX=7 EndY=5.1 EndZ=0
    g3: LineSegment StartX=7 StartY=5.1 StartZ=0 EndX=5.4 EndY=5.1 EndZ=0
  constraints (11):
    c: Coincident(g0,g1)
    c: Coincident(g1,g2)
    c: Coincident(g2,g3)
    c: Coincident(g3,g0)
    c: Vertical(g0)
    c: Vertical(g2)
    c: Horizontal(g1)
    c: Horizontal(g3)
    c: Distance(g0,g2) = 1.6
    c: Distance(g1,g3) = 1.2
    c: Coincident(g2,g-3)
FEATURE [Sketcher::SketchObject] Sketch064  label="rampini_per_serraggio_struttura"
  ArcFitTolerance = 1e-06
  AttachmentSupport = -> [XZ_Plane002]
  ExternalGeometry = -> [Sketch066,Sketch045]
  FullyConstrained = true
  MakeInternals = false
  MapMode = 5
  Placement = pos=(0,0,0) rot=(1,0,0;1.5708rad)
  sketch-geometry (7):
    g0: LineSegment StartX=7 StartY=5.1 StartZ=0 EndX=7 EndY=3.9 EndZ=0
    g1: LineSegment StartX=7 StartY=3.9 StartZ=0 EndX=9 EndY=3.9 EndZ=0
    g2: LineSegment StartX=7 StartY=5.1 StartZ=0 EndX=7 EndY=5.1 EndZ=0
    g3: LineSegment StartX=7 StartY=5.1 StartZ=0 EndX=7 EndY=7.5 EndZ=0
    g4: LineSegment StartX=9 StartY=5.1 StartZ=0 EndX=9 EndY=3.9 EndZ=0
    g5: LineSegment StartX=7 StartY=7.5 StartZ=0 EndX=9 EndY=7.5 EndZ=0
    g6: LineSegment StartX=9 StartY=7.5 StartZ=0 EndX=9 EndY=5.1 EndZ=0
  constraints (20):
    c: Vertical(g0)
    c: Coincident(g1,g0)
    c: Horizontal(g1)
    c: Coincident(g2,g0)
    c: Horizontal(g2)
    c: Coincident(g3,g2)
    c: Vertical(g3)
    c: Coincident(g5,g3)
    c: Coincident(g4,g6)
    c: Coincident(g4,g1)
    c: Vertical(g4)
    c: Coincident(g0,g-3)
    c: DistanceY(g-4,g3) = 2.4
    c: DistanceX(g1,g1) = 2
    c: DistanceY(g2,g6) = 0
    c: DistanceX(g2,g2) = 0
    c: DistanceY(g0,g0) = 1.2
    c: Coincident(g5,g6)
    c: Horizontal(g5)
    c: Vertical(g6)
FEATURE [Sketcher::SketchObject] Sketch067  label="perno per blocco switch"
  ArcFitTolerance = 1e-06
  AttachmentSupport = -> [XZ_Plane]
  ExternalGeometry = -> [Sketch,Sketch010]
  FullyConstrained = true
  MakeInternals = false
  MapMode = 5
  Placement = pos=(0,0,0) rot=(1,0,0;1.5708rad)
  sketch-geometry (14):
    g0: LineSegment StartX=-191.073 StartY=24.9429 StartZ=0 EndX=-185.81 EndY=23.0276 EndZ=0
    g1: LineSegment StartX=-183.76 StartY=23.9839 StartZ=0 EndX=-182.392 EndY=27.7427 EndZ=0
    g2: LineSegment StartX=-183.348 StartY=29.7934 StartZ=0 EndX=-188.61 EndY=31.7087 EndZ=0
    g3: LineSegment StartX=-188.61 StartY=31.7087 StartZ=0 EndX=-191.073 EndY=24.9429 EndZ=0
    g4: GeomPoint [constr] X=-186.459 Y=27.0946 Z=0
    g5: LineSegment StartX=-189.022 StartY=25.8992 StartZ=0 EndX=-185.263 EndY=24.5311 EndZ=0
    g6: LineSegment StartX=-185.263 StartY=24.5311 StartZ=0 EndX=-183.895 EndY=28.2899 EndZ=0
    g7: LineSegment StartX=-183.895 StartY=28.2899 StartZ=0 EndX=-187.654 EndY=29.658 EndZ=0
    g8: LineSegment StartX=-187.654 StartY=29.658 StartZ=0 EndX=-189.022 EndY=25.8992 EndZ=0
    g9: GeomPoint [constr] X=-186.459 Y=27.0946 Z=0
    g10: ArcOfCircle CenterX=-185.263 CenterY=24.5311 CenterZ=0 NormalX=0 NormalY=0 NormalZ=1 AngleXU=0 Radius=1.6 StartAngle=4.36332 EndAngle=5.93412
    g11: GeomPoint [constr] X=-184.307 Y=22.4804 Z=0
    g12: ArcOfCircle CenterX=-183.895 CenterY=28.2899 CenterZ=0 NormalX=0 NormalY=0 NormalZ=1 AngleXU=0 Radius=1.6 StartAngle=5.93412 EndAngle=7.50492
    g13: GeomPoint [constr] X=-181.844 Y=29.2462 Z=0
  constraints (30):
    c: Coincident(g2,g3)
    c: Coincident(g3,g0)
    c: Symmetric(g13,g0,g4)
    c: Distance(g11,g3) = 7.2
    c: Distance(g0,g2) = 7.2
    c: Parallel(g3,g1)
    c: Parallel(g2,g0)
    c: Perpendicular(g2,g3)
    c: Coincident(g5,g6)
    c: Coincident(g6,g7)
    c: Coincident(g7,g8)
    c: Coincident(g8,g5)
    c: Symmetric(g7,g5,g9)
    c: Distance(g6,g8) = 4
    c: Distance(g5,g7) = 4
    c: Coincident(g9,g4)
    c: Parallel(g8,g6)
    c: Parallel(g7,g5)
    c: Perpendicular(g7,g8)
    c: Tangent(g8,g-3)
    c: Tangent(g2,g-4)
    c: PointOnObject(g11,g1)
    c: PointOnObject(g11,g0)
    c: Tangent(g1,g10) = -1.5708
    c: Tangent(g0,g10) = -1.5708
    c: PointOnObject(g13,g1)
    c: Tangent(g1,g12) = -1.5708
    c: Tangent(g2,g12) = -1.5708
    c: Equal(g10,g12)
    c: Coincident(g10,g5)
FEATURE [Part::Extrusion] Extrude072  label="Extrude perno per blocco switch"
  Base = -> Sketch067
  Dir = (0,-1,2e-16)
  DirMode = 2
  FaceMakerClass = Part::FaceMakerBullseye
  FaceMakerMode = 3
  LengthFwd = 25.2
  LengthRev = 0
  Solid = true
  Symmetric = true
FEATURE [Part::MultiFuse] Fusion
  Refine = true
  Shapes = -> [Extrude,Sweep,Extrude007,Extrude011,Extrude005,Extrude012,Extrude013,Extrude016,Extrude031,Extrude039,Extrude045,Extrude072]
FEATURE [Part::Cut] Cut
  Base = -> Fusion
  Refine = true
  Tool = -> Extrude001
FEATURE [Part::Cut] Cut001
  Base = -> Cut
  Refine = true
  Tool = -> Extrude004
FEATURE [Part::Cut] Cut002
  Base = -> Cut001
  Refine = true
  Tool = -> Extrude006
FEATURE [Part::Cut] Cut003
  Base = -> Cut002
  Refine = true
  Tool = -> Extrude008
FEATURE [Part::Cut] Cut004
  Base = -> Cut003
  Refine = true
  Tool = -> Extrude009
FEATURE [Part::Cut] Cut005
  Base = -> Cut004
  Refine = true
  Tool = -> Extrude010
FEATURE [Part::Cut] Cut006
  Base = -> Cut005
  Refine = true
  Tool = -> Extrude014
FEATURE [Part::Cut] Cut007
  Base = -> Cut006
  Refine = true
  Tool = -> Extrude015
FEATURE [Part::Cut] Cut008
  Base = -> Cut007
  Refine = true
  Tool = -> Extrude018
FEATURE [Part::Cut] Cut009
  Base = -> Cut008
  Refine = true
  Tool = -> Extrude019
FEATURE [Part::Cut] Cut010
  Base = -> Cut009
  Refine = true
  Tool = -> Extrude020
FEATURE [Part::Cut] Cut011
  Base = -> Cut010
  Refine = true
  Tool = -> Extrude021
FEATURE [Part::Cut] Cut012
  Base = -> Cut011
  Refine = true
  Tool = -> Extrude022
FEATURE [Part::Cut] Cut013
  Base = -> Cut012
  Refine = true
  Tool = -> Extrude023
FEATURE [Part::Cut] Cut014
  Base = -> Cut013
  Refine = true
  Tool = -> Extrude032
FEATURE [Part::Cut] Cut015
  Base = -> Cut014
  Refine = true
  Tool = -> Extrude033
FEATURE [Part::Cut] Cut016
  Base = -> Cut015
  Refine = true
  Tool = -> Extrude034
FEATURE [Part::Cut] Cut017
  Base = -> Cut016
  Refine = true
  Tool = -> Extrude035
FEATURE [Part::Cut] Cut018
  Base = -> Cut017
  Refine = true
  Tool = -> Extrude036
FEATURE [Part::Cut] Cut019
  Base = -> Cut018
  Refine = true
  Tool = -> Extrude037
FEATURE [Part::Cut] Cut020
  Base = -> Cut019
  Refine = true
  Tool = -> Extrude030
FEATURE [Part::Cut] Cut022
  Base = -> Cut020
  Refine = true
  Tool = -> Extrude038
FEATURE [Part::Cut] Cut023
  Base = -> Cut022
  Refine = true
  Tool = -> Extrude041
FEATURE [Part::Cut] Cut024
  Base = -> Cut023
  Refine = true
  Tool = -> Extrude040
FEATURE [Part::Cut] Cut025
  Base = -> Cut024
  Refine = true
  Tool = -> Extrude042
FEATURE [Part::Cut] Cut026
  Base = -> Cut025
  Refine = true
  Tool = -> Extrude043
FEATURE [Part::Cut] Cut027
  Base = -> Cut026
  Refine = true
  Tool = -> Extrude044
FEATURE [Part::Cut] Cut028
  Base = -> Cut027
  Refine = true
  Tool = -> Extrude046
FEATURE [Part::Cut] Cut029
  Base = -> Cut028
  Refine = true
  Tool = -> Extrude047
FEATURE [Part::Cut] Cut033
  Base = -> Cut029
  Refine = true
  Tool = -> Extrude055
FEATURE [Part::Cut] Cut034
  Base = -> Cut033
  Refine = true
  Tool = -> Extrude056
FEATURE [Part::Cut] Cut035
  Base = -> Cut034
  Refine = true
  Tool = -> Extrude057
FEATURE [Part::Cut] Cut037
  Base = -> Cut035
  Refine = true
  Tool = -> Extrude060
FEATURE [Part::Cut] Cut038
  Base = -> Cut037
  Refine = true
  Tool = -> Extrude061
FEATURE [Part::Cut] Cut039
  Base = -> Cut038
  Refine = true
  Tool = -> Extrude063
FEATURE [Part::Cut] Cut040
  Base = -> Cut039
  Refine = true
  Tool = -> Extrude064
FEATURE [Part::Cut] Cut041
  Base = -> Cut040
  Refine = true
  Tool = -> Extrude062
FEATURE [Sketcher::SketchObject] Sketch068  label="base con smusso sopra neopixel"
  ArcFitTolerance = 1e-06
  AttachmentSupport = -> [YZ_Plane002]
  FullyConstrained = true
  MakeInternals = false
  MapMode = 5
  Placement = pos=(0,0,0) rot=(0.57735,0.57735,0.57735;2.0944rad)
  sketch-geometry (5):
    g0: LineSegment StartX=-9.5 StartY=-6.1 StartZ=0 EndX=9.5 EndY=-6.1 EndZ=0
    g1: LineSegment StartX=9.5 StartY=-6.1 StartZ=0 EndX=9.5 EndY=6.1 EndZ=0
    g2: LineSegment StartX=9.5 StartY=6.1 StartZ=0 EndX=-9.5 EndY=6.1 EndZ=0
    g3: LineSegment StartX=-9.5 StartY=6.1 StartZ=0 EndX=-9.5 EndY=-6.1 EndZ=0
    g4: GeomPoint [constr] X=0 Y=0 Z=0
  constraints (12):
    c: Coincident(g0,g1)
    c: Coincident(g1,g2)
    c: Coincident(g2,g3)
    c: Coincident(g3,g0)
    c: Horizontal(g0)
    c: Horizontal(g2)
    c: Vertical(g1)
    c: Vertical(g3)
    c: Symmetric(g2,g0,g4)
    c: Distance(g1,g3) = 19
    c: Distance(g0,g2) = 12.2
    c: Coincident(g4,g-1)
FEATURE [Sketcher::SketchObject] Sketch069  label="cilindro minore"
  ArcFitTolerance = 1e-06
  AttachmentSupport = -> [XZ_Plane004]
  FullyConstrained = true
  MakeInternals = false
  MapMode = 5
  Placement = pos=(0,0,0) rot=(1,0,0;1.5708rad)
  sketch-geometry (1):
    g0: Circle CenterX=0 CenterY=0 CenterZ=0 NormalX=0 NormalY=0 NormalZ=1 AngleXU=0 Radius=5.8
  constraints (2):
    c: Diameter(g0) = 11.6
    c: Coincident(g0,g-1)
FEATURE [Sketcher::SketchObject] Sketch070  label="cilindro maggiore"
  ArcFitTolerance = 1e-06
  AttachmentSupport = -> [XZ_Plane004]
  ExternalGeometry = -> [Sketch069]
  FullyConstrained = true
  MakeInternals = false
  MapMode = 5
  Placement = pos=(0,0,0) rot=(1,0,0;1.5708rad)
  sketch-geometry (1):
    g0: Circle CenterX=0 CenterY=0 CenterZ=0 NormalX=0 NormalY=0 NormalZ=1 AngleXU=0 Radius=6.5
  constraints (2):
    c: Coincident(g0,g-1)
    c: Diameter(g0) = 13
FEATURE [Sketcher::SketchObject] Sketch071  label="buco interno"
  ArcFitTolerance = 1e-06
  AttachmentSupport = -> [XZ_Plane004]
  ExternalGeometry = -> [Sketch069]
  FullyConstrained = true
  MakeInternals = false
  MapMode = 5
  Placement = pos=(0,0,0) rot=(1,0,0;1.5708rad)
  sketch-geometry (1):
    g0: Circle CenterX=0 CenterY=0 CenterZ=0 NormalX=0 NormalY=0 NormalZ=1 AngleXU=0 Radius=5
  constraints (2):
    c: Coincident(g0,g-1)
    c: Diameter(g0) = 10
FEATURE [PartDesign::Pad] Pad
  Direction = (0,-1,2e-16)
  Length = 1.2
  Length2 = 10
  Placement = pos=(0,0,0) rot=(1,0,0;1.5708rad)
  Profile = -> Sketch070
  ReferenceAxis = -> Sketch070 [N_Axis]
  Refine = true
  Suppressed = false
  Type = 0
FEATURE [PartDesign::Pad] Pad001
  BaseFeature = -> Pad
  Direction = (0,-1,2e-16)
  Length = 5.6
  Length2 = 10
  Placement = pos=(0,0,0) rot=(1,0,0;1.5708rad)
  Profile = -> Sketch069
  ReferenceAxis = -> Sketch069 [N_Axis]
  Refine = true
  Suppressed = false
  Type = 0
FEATURE [PartDesign::Pocket] Pocket
  BaseFeature = -> Pad001
  Direction = (0,1,-2e-16)
  Length = 7
  Length2 = 5
  Midplane = true
  Placement = pos=(0,0,0) rot=(1,0,0;1.5708rad)
  Profile = -> Sketch071
  ReferenceAxis = -> Sketch071 [N_Axis]
  Refine = true
  Suppressed = false
  Type = 0
FEATURE [PartDesign::Fillet] Fillet
  Base = -> Pocket [Face7]
  BaseFeature = -> Pocket
  Placement = pos=(0,0,0) rot=(1,0,0;1.5708rad)
  Radius = 1
  Refine = true
  SupportTransform = false
  Suppressed = false
  UseAllEdges = false
FEATURE [PartDesign::Body] Body004  label="pulsanti lato sinistro"
  AllowCompound = false
  Group = -> [Sketch069,Sketch070,Sketch071,Pad,Pad001,Pocket,Fillet]
  Origin = -> Origin004
  Tip = -> Fillet
FEATURE [Sketcher::SketchObject] Sketch072  label="buco per saldature e diodo driver solenoide"
  ArcFitTolerance = 1e-06
  AttachmentSupport = -> [XZ_Plane]
  ExternalGeometry = -> [Sketch038]
  FullyConstrained = true
  MakeInternals = false
  MapMode = 5
  Placement = pos=(0,0,0) rot=(1,0,0;1.5708rad)
  sketch-geometry (4):
    g0: LineSegment StartX=-212.269 StartY=-43.9083 StartZ=0 EndX=-207.197 EndY=-33.0326 EndZ=0
    g1: LineSegment StartX=-207.197 StartY=-33.0326 StartZ=0 EndX=-207.56 EndY=-32.8635 EndZ=0
    g2: LineSegment StartX=-207.56 StartY=-32.8635 StartZ=0 EndX=-212.631 EndY=-43.7392 EndZ=0
    g3: LineSegment StartX=-212.631 StartY=-43.7392 StartZ=0 EndX=-212.269 EndY=-43.9083 EndZ=0
  constraints (11):
    c: Coincident(g1,g0)
    c: Coincident(g2,g1)
    c: Coincident(g3,g2)
    c: Coincident(g3,g0)
    c: Parallel(g-3,g0)
    c: Parallel(g0,g2)
    c: Perpendicular(g0,g3)
    c: Perpendicular(g1,g0)
    c: Distance(g3) = 0.4
    c: Distance(g2) = 12
    c: Coincident(g0,g-3)
FEATURE [Part::Extrusion] Extrude074  label="Extrude buco per saldature e diodo driver solenoide"
  Base = -> Sketch072
  Dir = (0,-1,2e-16)
  DirMode = 2
  FaceMakerClass = Part::FaceMakerBullseye
  FaceMakerMode = 3
  LengthFwd = 14.6
  LengthRev = 0
  Solid = true
  Symmetric = true
FEATURE [Part::Cut] Cut042
  Base = -> Cut041
  Refine = true
  Tool = -> Extrude074
FEATURE [Sketcher::SketchObject] Sketch073  label="fori slargati blocco solenoide"
  ArcFitTolerance = 1e-06
  AttachmentSupport = -> [XY_Plane]
  ExternalGeometry = -> [Sketch030]
  FullyConstrained = true
  MakeInternals = false
  MapMode = 5
  sketch-geometry (2):
    g0: Circle CenterX=-152.209 CenterY=6.95 CenterZ=0 NormalX=0 NormalY=0 NormalZ=1 AngleXU=0 Radius=3.7
    g1: Circle CenterX=-130.41 CenterY=-6.95 CenterZ=0 NormalX=0 NormalY=0 NormalZ=1 AngleXU=0 Radius=3.7
  constraints (4):
    c: Diameter(g0) = 7.4
    c: Coincident(g0,g-3)
    c: Diameter(g1) = 7.4
    c: Coincident(g1,g-4)
FEATURE [Part::Extrusion] Extrude075  label="Extrude fori slargati blocco solenoide"
  Base = -> Sketch073
  Dir = (0,0,1)
  DirMode = 2
  FaceMakerClass = Part::FaceMakerBullseye
  FaceMakerMode = 3
  LengthFwd = 1.5
  LengthRev = 0
  Placement = pos=(0,0,36.4) rot=(0,0,1;0rad)
  Solid = true
  Symmetric = false
FEATURE [Part::Cut] Cut043
  Base = -> Cut042
  Refine = true
  Tool = -> Extrude075
FEATURE [Sketcher::SketchObject] Sketch074  label="lato sx pistola"
  ArcFitTolerance = 1e-06
  AttachmentSupport = -> [XZ_Plane]
  ExternalGeometry = -> [Sketch016,Sketch,Sketch058]
  FullyConstrained = true
  MakeInternals = false
  MapMode = 5
  Placement = pos=(0,0,0) rot=(1,0,0;1.5708rad)
  sketch-geometry (37):
    g0: LineSegment StartX=-82.8 StartY=3.2 StartZ=0 EndX=0 EndY=3.2 EndZ=0
    g1: LineSegment StartX=-82.8 StartY=3.2 StartZ=0 EndX=-82.8 EndY=6.2 EndZ=0
    g2: LineSegment [constr] StartX=-107.6 StartY=18 StartZ=0 EndX=-107.6 EndY=20 EndZ=0
    g3: LineSegment [constr] StartX=-132.428 StartY=18 StartZ=0 EndX=-132.428 EndY=20 EndZ=0
    g4: LineSegment StartX=-132.428 StartY=20 StartZ=0 EndX=-107.6 EndY=20 EndZ=0
    g5: ArcOfCircle CenterX=-107.6 CenterY=4 CenterZ=0 NormalX=0 NormalY=0 NormalZ=1 AngleXU=0 Radius=16 StartAngle=0.137937 EndAngle=1.5708
    g6: LineSegment StartX=-82.8 StartY=6.2 StartZ=0 EndX=-91.752 EndY=6.2 EndZ=0
    g7: LineSegment [constr] StartX=-145.743 StartY=8.32624 StartZ=0 EndX=-147.645 EndY=8.94427 EndZ=0
    g8: ArcOfCircle CenterX=-132.428 CenterY=4 CenterZ=0 NormalX=0 NormalY=0 NormalZ=1 AngleXU=0 Radius=16 StartAngle=1.5708 EndAngle=2.82743
    g9: LineSegment StartX=-215.932 StartY=-80.4316 StartZ=0 EndX=-176.685 EndY=-80.4316 EndZ=0
    g10: LineSegment StartX=-147.645 StartY=8.94427 StartZ=0 EndX=-176.685 EndY=-80.4316 EndZ=0
    g11: LineSegment [constr] StartX=-193.988 StartY=-2.33927 StartZ=0 EndX=-192.176 EndY=-3.18451 EndZ=0
    g12: LineSegment [constr] StartX=-217.232 StartY=-52.1862 StartZ=0 EndX=-215.42 EndY=-53.0314 EndZ=0
    g13: LineSegment StartX=-192.176 StartY=-3.18451 StartZ=0 EndX=-215.42 EndY=-53.0314 EndZ=0
    g14: ArcOfCircle CenterX=-184.801 CenterY=-67.3089 CenterZ=0 NormalX=0 NormalY=0 NormalZ=1 AngleXU=0 Radius=33.7833 StartAngle=2.70526 EndAngle=3.54053
    g15: ArcOfCircle CenterX=-207.583 CenterY=4 CenterZ=0 NormalX=0 NormalY=0 NormalZ=1 AngleXU=0 Radius=17 StartAngle=5.84685 EndAngle=7.56663
    g16: LineSegment StartX=-202.765 StartY=20.303 StartZ=0 EndX=-195.887 EndY=39.2 EndZ=0
    g17: LineSegment [constr] StartX=-193.885 StartY=33.0037 StartZ=0 EndX=-197.644 EndY=34.3718 EndZ=0
    g18: LineSegment StartX=-195.887 StartY=39.2 StartZ=0 EndX=0 EndY=39.2 EndZ=0
    g19: LineSegment StartX=0 StartY=3.2 StartZ=0 EndX=0 EndY=39.2 EndZ=0
    g20: LineSegment StartX=-189.939 StartY=31.5672 StartZ=0 EndX=-192.333 EndY=24.9893 EndZ=0
    g21: LineSegment StartX=-196.467 StartY=26.4942 StartZ=0 EndX=-194.073 EndY=33.0721 EndZ=0
    g22: Circle CenterX=-213.443 CenterY=-76.8316 CenterZ=0 NormalX=0 NormalY=0 NormalZ=1 AngleXU=0 Radius=1.8
    g23: Circle CenterX=-179.305 CenterY=-76.8316 CenterZ=0 NormalX=0 NormalY=0 NormalZ=1 AngleXU=0 Radius=1.8
    g24: Circle CenterX=-184.08 CenterY=34.8 CenterZ=0 NormalX=0 NormalY=0 NormalZ=1 AngleXU=0 Radius=1.8
    g25: Circle CenterX=-78.51 CenterY=34.8 CenterZ=0 NormalX=0 NormalY=0 NormalZ=1 AngleXU=0 Radius=1.8
    g26: Circle CenterX=-78.51 CenterY=7.6 CenterZ=0 NormalX=0 NormalY=0 NormalZ=1 AngleXU=0 Radius=1.8
    g27: Circle CenterX=-5.6 CenterY=34.8 CenterZ=0 NormalX=0 NormalY=0 NormalZ=1 AngleXU=0 Radius=1.8
    g28: Circle CenterX=-5.6 CenterY=7.6 CenterZ=0 NormalX=0 NormalY=0 NormalZ=1 AngleXU=0 Radius=1.8
    g29: LineSegment StartX=-190.127 StartY=31.6356 StartZ=0 EndX=-189.939 EndY=31.5672 EndZ=0
    g30: LineSegment StartX=-194.073 StartY=33.0721 StartZ=0 EndX=-193.885 EndY=33.0037 EndZ=0
    g31: LineSegment StartX=-193.885 StartY=33.0037 StartZ=0 EndX=-190.127 EndY=31.6356 EndZ=0
    g32: LineSegment StartX=-196.467 StartY=26.4942 StartZ=0 EndX=-192.333 EndY=24.9893 EndZ=0
    g33: Circle CenterX=-19 CenterY=21.2 CenterZ=0 NormalX=0 NormalY=0 NormalZ=1 AngleXU=0 Radius=6.3
    g34: Circle CenterX=-42 CenterY=21.2 CenterZ=0 NormalX=0 NormalY=0 NormalZ=1 AngleXU=0 Radius=6.3
    g35: Circle CenterX=-65 CenterY=21.2 CenterZ=0 NormalX=0 NormalY=0 NormalZ=1 AngleXU=0 Radius=6.3
    g36: LineSegment [constr] StartX=-4 StartY=21.2 StartZ=0 EndX=-65 EndY=21.2 EndZ=0
  constraints (96):
    c: Coincident(g0,g-41)
    c: Horizontal(g0)
    c: PointOnObject(g0,g-39)
    c: Coincident(g1,g0)
    c: Vertical(g1)
    c: DistanceY(g1,g1) = 3
    c: Coincident(g2,g-17)
    c: Vertical(g2)
    c: Coincident(g3,g-16)
    c: Vertical(g3)
    c: DistanceY(g2,g2) = 2
    c: DistanceY(g3,g3) = 2
    c: Coincident(g4,g3)
    c: Coincident(g4,g2)
    c: Coincident(g5,g-17)
    c: Coincident(g5,g2)
    c: Coincident(g6,g1)
    c: Horizontal(g6)
    c: Coincident(g6,g5)
    c: Coincident(g7,g-15)
    c: Coincident(g8,g7)
    c: Coincident(g8,g3)
    c: Coincident(g8,g-15)
    c: Horizontal(g9)
    c: DistanceY(g-13,g9) = 2
    c: Coincident(g10,g7)
    c: Parallel(g10,g-14)
    c: Coincident(g9,g10)
    c: Distance(g11) = 2
    c: Coincident(g11,g-11)
    c: Perpendicular(g-11,g11)
    c: Distance(g12) = 2
    c: Coincident(g12,g-12)
    c: Perpendicular(g-11,g12)
    c: Coincident(g13,g11)
    c: Coincident(g13,g12)
    c: Coincident(g14,g-32)
    c: Coincident(g14,g12)
    c: Coincident(g14,g9)
    c: Coincident(g15,g-10)
    c: Coincident(g15,g11)
    c: Parallel(g16,g-22)
    c: Distance(g17) = 4
    c: PointOnObject(g17,g16)
    c: Coincident(g15,g16)
    c: Horizontal(g18)
    c: Coincident(g18,g16)
    c: Coincident(g19,g0)
    c: PointOnObject(g19,g-39)
    c: DistanceY(g19,g-36) = 2
    c: Coincident(g18,g19)
    c: Diameter(g22) = 3.6
    c: Coincident(g22,g-9)
    c: Diameter(g23) = 3.6
    c: Coincident(g23,g-8)
    c: Diameter(g24) = 3.6
    c: Diameter(g25) = 3.6
    c: Diameter(g26) = 3.6
    c: Diameter(g27) = 3.6
    c: Diameter(g28) = 3.6
    c: Coincident(g27,g-4)
    c: Coincident(g28,g-3)
    c: Coincident(g25,g-6)
    c: Coincident(g26,g-5)
    c: Coincident(g24,g-7)
    c: Parallel(g20,g-21)
    c: Equal(g20,g-21)
    c: Parallel(g21,g-19)
    c: Equal(g21,g-19)
    c: Distance(g29) = 0.2
    c: Distance(g30) = 0.2
    c: Parallel(g29,g-20)
    c: Parallel(g31,g-20)
    c: Equal(g31,g-20)
    c: Coincident(g30,g31)
    c: Coincident(g31,g29)
    c: Coincident(g29,g-21)
    c: Parallel(g30,g31)
    c: Coincident(g17,g30)
    c: Coincident(g20,g29)
    c: Coincident(g21,g30)
    c: Perpendicular(g16,g17)
    c: Coincident(g32,g21)
    c: Coincident(g32,g20)
    c: Perpendicular(g10,g7)
    c: Diameter(g33) = 12.6
    c: Diameter(g34) = 12.6
    c: Diameter(g35) = 12.6
    c: Horizontal(g36)
    c: PointOnObject(g33,g36)
    c: PointOnObject(g34,g36)
    c: DistanceX(g34,g33) = 23
    c: DistanceX(g35,g34) = 23
    c: DistanceX(g33,g36) = 15
    c: Symmetric(g-24,g-24,g36)
    c: Coincident(g36,g35)
FEATURE [Sketcher::SketchObject] Sketch075  label="lato dx pistola"
  ArcFitTolerance = 1e-06
  AttachmentSupport = -> [XZ_Plane]
  ExternalGeometry = -> [Sketch016,Sketch,Sketch058,Sketch074]
  FullyConstrained = true
  MakeInternals = false
  MapMode = 5
  Placement = pos=(0,0,0) rot=(1,0,0;1.5708rad)
  sketch-geometry (61):
    g0: LineSegment StartX=-82.8 StartY=3.2 StartZ=0 EndX=0 EndY=3.2 EndZ=0
    g1: LineSegment StartX=-82.8 StartY=3.2 StartZ=0 EndX=-82.8 EndY=6.2 EndZ=0
    g2: LineSegment [constr] StartX=-107.6 StartY=18 StartZ=0 EndX=-107.6 EndY=20 EndZ=0
    g3: LineSegment [constr] StartX=-132.428 StartY=18 StartZ=0 EndX=-132.428 EndY=20 EndZ=0
    g4: LineSegment StartX=-132.428 StartY=20 StartZ=0 EndX=-107.6 EndY=20 EndZ=0
    g5: ArcOfCircle CenterX=-107.6 CenterY=4 CenterZ=0 NormalX=0 NormalY=0 NormalZ=1 AngleXU=0 Radius=16 StartAngle=0.137937 EndAngle=1.5708
    g6: LineSegment StartX=-82.8 StartY=6.2 StartZ=0 EndX=-91.752 EndY=6.2 EndZ=0
    g7: LineSegment [constr] StartX=-145.743 StartY=8.32624 StartZ=0 EndX=-147.645 EndY=8.94427 EndZ=0
    g8: ArcOfCircle CenterX=-132.428 CenterY=4 CenterZ=0 NormalX=0 NormalY=0 NormalZ=1 AngleXU=0 Radius=16 StartAngle=1.5708 EndAngle=2.82743
    g9: LineSegment StartX=-215.932 StartY=-80.4316 StartZ=0 EndX=-176.685 EndY=-80.4316 EndZ=0
    g10: LineSegment StartX=-147.645 StartY=8.94427 StartZ=0 EndX=-176.685 EndY=-80.4316 EndZ=0
    g11: LineSegment [constr] StartX=-193.988 StartY=-2.33927 StartZ=0 EndX=-192.176 EndY=-3.18451 EndZ=0
    g12: LineSegment [constr] StartX=-217.232 StartY=-52.1862 StartZ=0 EndX=-215.42 EndY=-53.0314 EndZ=0
    g13: LineSegment StartX=-192.176 StartY=-3.18451 StartZ=0 EndX=-215.42 EndY=-53.0314 EndZ=0
    g14: ArcOfCircle CenterX=-184.801 CenterY=-67.3089 CenterZ=0 NormalX=0 NormalY=0 NormalZ=1 AngleXU=0 Radius=33.7833 StartAngle=2.70526 EndAngle=3.54053
    g15: ArcOfCircle CenterX=-207.583 CenterY=4 CenterZ=0 NormalX=0 NormalY=0 NormalZ=1 AngleXU=0 Radius=17 StartAngle=5.84685 EndAngle=7.56663
    g16: LineSegment StartX=-202.765 StartY=20.303 StartZ=0 EndX=-195.887 EndY=39.2 EndZ=0
    g17: LineSegment [constr] StartX=-193.885 StartY=33.0037 StartZ=0 EndX=-197.644 EndY=34.3718 EndZ=0
    g18: LineSegment StartX=-195.887 StartY=39.2 StartZ=0 EndX=0 EndY=39.2 EndZ=0
    g19: LineSegment StartX=0 StartY=3.2 StartZ=0 EndX=0 EndY=39.2 EndZ=0
    g20: LineSegment StartX=-189.939 StartY=31.5672 StartZ=0 EndX=-192.333 EndY=24.9893 EndZ=0
    g21: LineSegment StartX=-196.467 StartY=26.4942 StartZ=0 EndX=-194.073 EndY=33.0721 EndZ=0
    g22: Circle CenterX=-213.443 CenterY=-76.8316 CenterZ=0 NormalX=0 NormalY=0 NormalZ=1 AngleXU=0 Radius=1.8
    g23: Circle CenterX=-179.305 CenterY=-76.8316 CenterZ=0 NormalX=0 NormalY=0 NormalZ=1 AngleXU=0 Radius=1.8
    g24: Circle CenterX=-184.08 CenterY=34.8 CenterZ=0 NormalX=0 NormalY=0 NormalZ=1 AngleXU=0 Radius=1.8
    g25: Circle CenterX=-78.51 CenterY=34.8 CenterZ=0 NormalX=0 NormalY=0 NormalZ=1 AngleXU=0 Radius=1.8
    g26: Circle CenterX=-78.51 CenterY=7.6 CenterZ=0 NormalX=0 NormalY=0 NormalZ=1 AngleXU=0 Radius=1.8
    g27: Circle CenterX=-5.6 CenterY=34.8 CenterZ=0 NormalX=0 NormalY=0 NormalZ=1 AngleXU=0 Radius=1.8
    g28: Circle CenterX=-5.6 CenterY=7.6 CenterZ=0 NormalX=0 NormalY=0 NormalZ=1 AngleXU=0 Radius=1.8
    g29: LineSegment StartX=-190.127 StartY=31.6356 StartZ=0 EndX=-189.939 EndY=31.5672 EndZ=0
    g30: LineSegment StartX=-194.073 StartY=33.0721 StartZ=0 EndX=-193.885 EndY=33.0037 EndZ=0
    g31: LineSegment StartX=-193.885 StartY=33.0037 StartZ=0 EndX=-190.127 EndY=31.6356 EndZ=0
    g32: LineSegment StartX=-196.467 StartY=26.4942 StartZ=0 EndX=-192.333 EndY=24.9893 EndZ=0
    g33: LineSegment [constr] StartX=-4 StartY=21.2 StartZ=0 EndX=-87.91 EndY=21.2 EndZ=0
    g34: GeomPoint [constr] X=-4 Y=21.2 Z=0
    g35: LineSegment [constr] StartX=-15.2 StartY=33.7 StartZ=0 EndX=-15.2 EndY=8.7 EndZ=0
    g36: LineSegment [constr] StartX=-15.2 StartY=33.7 StartZ=0 EndX=-56.2 EndY=33.7 EndZ=0
    g37: LineSegment [constr] StartX=-15.2 StartY=8.7 StartZ=0 EndX=-56.2 EndY=8.7 EndZ=0
    g38: LineSegment [constr] StartX=-56.2 StartY=33.7 StartZ=0 EndX=-56.2 EndY=8.7 EndZ=0
    g39: Circle CenterX=-18.6 CenterY=30.3 CenterZ=0 NormalX=0 NormalY=0 NormalZ=1 AngleXU=0 Radius=3.4
    g40: Circle CenterX=-18.6 CenterY=12.1 CenterZ=0 NormalX=0 NormalY=0 NormalZ=1 AngleXU=0 Radius=3.4
    g41: Circle CenterX=-43.2 CenterY=30.3 CenterZ=0 NormalX=0 NormalY=0 NormalZ=1 AngleXU=0 Radius=3.4
    g42: Circle CenterX=-43.2 CenterY=12.1 CenterZ=0 NormalX=0 NormalY=0 NormalZ=1 AngleXU=0 Radius=3.4
    g43: LineSegment [constr] StartX=-4 StartY=21.2 StartZ=0 EndX=-15.2 EndY=21.2 EndZ=0
    g44: LineSegment [constr] StartX=-15.2 StartY=21.2 StartZ=0 EndX=-36.2 EndY=21.2 EndZ=0
    g45: LineSegment [constr] StartX=-41.5 StartY=16.2 StartZ=0 EndX=-30.9 EndY=16.2 EndZ=0
    g46: LineSegment [constr] StartX=-30.9 StartY=16.2 StartZ=0 EndX=-30.9 EndY=26.2 EndZ=0
    g47: LineSegment [constr] StartX=-30.9 StartY=26.2 StartZ=0 EndX=-41.5 EndY=26.2 EndZ=0
    g48: LineSegment [constr] StartX=-41.5 StartY=26.2 StartZ=0 EndX=-41.5 EndY=16.2 EndZ=0
    g49: GeomPoint [constr] X=-36.2 Y=21.2 Z=0
    g50: Circle CenterX=-36.2 CenterY=21.2 CenterZ=0 NormalX=0 NormalY=0 NormalZ=1 AngleXU=0 Radius=2.8
    g51: LineSegment [constr] StartX=-24.2 StartY=26.7 StartZ=0 EndX=-24.2 EndY=15.7 EndZ=0
    g52: Circle CenterX=-24.2 CenterY=26.7 CenterZ=0 NormalX=0 NormalY=0 NormalZ=1 AngleXU=0 Radius=3
    g53: Circle CenterX=-24.2 CenterY=15.7 CenterZ=0 NormalX=0 NormalY=0 NormalZ=1 AngleXU=0 Radius=3
    g54: GeomPoint X=-18.6 Y=30.3 Z=0
    g55: GeomPoint X=-18.6 Y=12.1 Z=0
    g56: GeomPoint X=-43.2 Y=12.1 Z=0
    g57: GeomPoint X=-43.2 Y=30.3 Z=0
    g58: Circle CenterX=-65 CenterY=21.2 CenterZ=0 NormalX=0 NormalY=0 NormalZ=1 AngleXU=0 Radius=1.5
    g59: Circle CenterX=-42 CenterY=21.2 CenterZ=0 NormalX=0 NormalY=0 NormalZ=1 AngleXU=0 Radius=1.5
    g60: Circle CenterX=-19 CenterY=21.2 CenterZ=0 NormalX=0 NormalY=0 NormalZ=1 AngleXU=0 Radius=1.5
  constraints (149):
    c: Coincident(g0,g-41)
    c: Horizontal(g0)
    c: PointOnObject(g0,g-39)
    c: Coincident(g1,g0)
    c: Vertical(g1)
    c: DistanceY(g1,g1) = 3
    c: Coincident(g2,g-17)
    c: Vertical(g2)
    c: Coincident(g3,g-16)
    c: Vertical(g3)
    c: DistanceY(g2,g2) = 2
    c: DistanceY(g3,g3) = 2
    c: Coincident(g4,g3)
    c: Coincident(g4,g2)
    c: Coincident(g5,g-17)
    c: Coincident(g5,g2)
    c: Coincident(g6,g1)
    c: Horizontal(g6)
    c: Coincident(g6,g5)
    c: Coincident(g7,g-15)
    c: Coincident(g8,g7)
    c: Coincident(g8,g3)
    c: Coincident(g8,g-15)
    c: Horizontal(g9)
    c: DistanceY(g-13,g9) = 2
    c: Coincident(g10,g7)
    c: Parallel(g10,g-14)
    c: Coincident(g9,g10)
    c: Distance(g11) = 2
    c: Coincident(g11,g-11)
    c: Perpendicular(g-11,g11)
    c: Distance(g12) = 2
    c: Coincident(g12,g-12)
    c: Perpendicular(g-11,g12)
    c: Coincident(g13,g11)
    c: Coincident(g13,g12)
    c: Coincident(g14,g-32)
    c: Coincident(g14,g12)
    c: Coincident(g14,g9)
    c: Coincident(g15,g-10)
    c: Coincident(g15,g11)
    c: Parallel(g16,g-22)
    c: Distance(g17) = 4
    c: PointOnObject(g17,g16)
    c: Coincident(g15,g16)
    c: Horizontal(g18)
    c: Coincident(g18,g16)
    c: Coincident(g19,g0)
    c: PointOnObject(g19,g-39)
    c: DistanceY(g19,g-36) = 2
    c: Coincident(g18,g19)
    c: Diameter(g22) = 3.6
    c: Coincident(g22,g-9)
    c: Diameter(g23) = 3.6
    c: Coincident(g23,g-8)
    c: Diameter(g24) = 3.6
    c: Diameter(g25) = 3.6
    c: Diameter(g26) = 3.6
    c: Diameter(g27) = 3.6
    c: Diameter(g28) = 3.6
    c: Coincident(g27,g-4)
    c: Coincident(g28,g-3)
    c: Coincident(g25,g-6)
    c: Coincident(g26,g-5)
    c: Coincident(g24,g-7)
    c: Parallel(g20,g-21)
    c: Equal(g20,g-21)
    c: Parallel(g21,g-19)
    c: Equal(g21,g-19)
    c: Distance(g29) = 0.2
    c: Distance(g30) = 0.2
    c: Parallel(g29,g-20)
    c: Parallel(g31,g-20)
    c: Equal(g31,g-20)
    c: Coincident(g30,g31)
    c: Coincident(g31,g29)
    c: Coincident(g29,g-21)
    c: Parallel(g30,g31)
    c: Coincident(g17,g30)
    c: Coincident(g20,g29)
    c: Coincident(g21,g30)
    c: Perpendicular(g16,g17)
    c: Coincident(g32,g21)
    c: Coincident(g32,g20)
    c: Perpendicular(g10,g7)
    c: Horizontal(g33)
    c: Symmetric(g-24,g-24,g33)
    c: PointOnObject(g33,g-28)
    c: Symmetric(g-24,g-24,g34)
    c: DistanceY(g35,g35) = 25
    c: Symmetric(g35,g35,g33)
    c: Distance(g36) = 41
    c: Coincident(g36,g35)
    c: Horizontal(g36)
    c: Coincident(g37,g35)
    c: Horizontal(g37)
    c: Coincident(g38,g36)
    c: Vertical(g38)
    c: Coincident(g37,g38)
    c: Diameter(g39) = 6.8
    c: Diameter(g40) = 6.8
    c: Tangent(g39,g36)
    c: Tangent(g40,g37)
    c: Tangent(g39,g35)
    c: Tangent(g40,g35)
    c: Diameter(g41) = 6.8
    c: Diameter(g42) = 6.8
    c: Tangent(g41,g36)
    c: Tangent(g42,g37)
    c: DistanceX(g41,g39) = 24.6
    c: DistanceX(g42,g40) = 24.6
    c: Distance(g43) = 11.2
    c: Coincident(g43,g33)
    c: PointOnObject(g43,g33)
    c: PointOnObject(g43,g35)
    c: Distance(g44) = 21
    c: Coincident(g44,g43)
    c: PointOnObject(g44,g33)
    c: Coincident(g45,g46)
    c: Coincident(g46,g47)
    c: Coincident(g47,g48)
    c: Coincident(g48,g45)
    c: Horizontal(g45)
    c: Horizontal(g47)
    c: Vertical(g46)
    c: Vertical(g48)
    c: Symmetric(g47,g45,g49)
    c: Distance(g46,g48) = 10.6
    c: Distance(g45,g47) = 10
    c: Coincident(g49,g44)
    c: Diameter(g50) = 5.6
    c: Coincident(g50,g44)
    c: Distance(g51) = 11
    c: Symmetric(g51,g51,g33)
    c: DistanceX(g51,g43) = 9
    c: Diameter(g52) = 6
    c: Coincident(g52,g51)
    c: Diameter(g53) = 6
    c: Coincident(g53,g51)
    c: Coincident(g40,g55)
    c: Coincident(g39,g54)
    c: Coincident(g41,g57)
    c: Coincident(g42,g56)
    c: Diameter(g58) = 3
    c: Diameter(g59) = 3
    c: Diameter(g60) = 3
    c: Coincident(g58,g-44)
    c: Coincident(g59,g-46)
    c: Coincident(g60,g-45)
FEATURE [Sketcher::SketchObject] Sketch078
  ArcFitTolerance = 1e-06
  AttachmentSupport = -> [XZ_Plane005]
  FullyConstrained = true
  MakeInternals = false
  MapMode = 5
  Placement = pos=(0,0,0) rot=(1,0,0;1.5708rad)
  sketch-geometry (5):
    g0: LineSegment [constr] StartX=0 StartY=5.5 StartZ=0 EndX=0 EndY=-5.5 EndZ=0
    g1: ArcOfCircle CenterX=0 CenterY=5.5 CenterZ=0 NormalX=0 NormalY=0 NormalZ=1 AngleXU=0 Radius=2.7 StartAngle=0 EndAngle=3.14159
    g2: ArcOfCircle CenterX=0 CenterY=-5.5 CenterZ=0 NormalX=0 NormalY=0 NormalZ=1 AngleXU=0 Radius=2.7 StartAngle=3.1416 EndAngle=6.28318
    g3: LineSegment StartX=-2.7 StartY=5.5 StartZ=0 EndX=-2.7 EndY=-5.50001 EndZ=0
    g4: LineSegment StartX=2.7 StartY=5.5 StartZ=0 EndX=2.7 EndY=-5.50001 EndZ=0
  constraints (13):
    c: Distance(g0) = 11
    c: Vertical(g0)
    c: Symmetric(g0,g0,g-1)
    c: Radius(g1) = 2.7
    c: Coincident(g1,g0)
    c: Radius(g2) = 2.7
    c: Coincident(g2,g0)
    c: Vertical(g3)
    c: Vertical(g4)
    c: Coincident(g2,g4)
    c: Coincident(g2,g3)
    c: Tangent(g3,g1) = -1.5708
    c: Tangent(g4,g1) = 1.5708
FEATURE [PartDesign::Pad] Pad002
  Direction = (0,-1,2e-16)
  Length = 0.8
  Length2 = 10
  Placement = pos=(0,0,0) rot=(1,0,0;1.5708rad)
  Profile = -> Sketch078
  ReferenceAxis = -> Sketch078 [N_Axis]
  Refine = true
  Suppressed = false
  Type = 0
FEATURE [Sketcher::SketchObject] Sketch079
  ArcFitTolerance = 1e-06
  AttachmentSupport = -> [XZ_Plane005]
  ExternalGeometry = -> [Sketch078]
  FullyConstrained = true
  MakeInternals = false
  MapMode = 5
  Placement = pos=(0,0,0) rot=(1,0,0;1.5708rad)
  sketch-geometry (2):
    g0: Circle CenterX=-1e-16 CenterY=5.5 CenterZ=0 NormalX=0 NormalY=0 NormalZ=1 AngleXU=0 Radius=2.7
    g1: Circle CenterX=0 CenterY=-5.5 CenterZ=0 NormalX=0 NormalY=0 NormalZ=1 AngleXU=0 Radius=2.7
  constraints (4):
    c: Coincident(g0,g-3)
    c: PointOnObject(g-3,g0)
    c: Coincident(g1,g-4)
    c: Equal(g1,g-4)
FEATURE [PartDesign::Pad] Pad003
  BaseFeature = -> Pad002
  Direction = (0,-1,2e-16)
  Length = 5
  Length2 = 10
  Placement = pos=(0,0,0) rot=(1,0,0;1.5708rad)
  Profile = -> Sketch079
  ReferenceAxis = -> Sketch079 [N_Axis]
  Refine = true
  Suppressed = false
  Type = 0
FEATURE [PartDesign::Fillet] Fillet001
  Base = -> Pad003 [Edge16,Edge14]
  BaseFeature = -> Pad003
  Placement = pos=(0,0,0) rot=(1,0,0;1.5708rad)
  Radius = 0.4
  Refine = true
  SupportTransform = false
  Suppressed = false
  UseAllEdges = false
FEATURE [PartDesign::Body] Body005  label="pulsanti lato destro"
  AllowCompound = false
  Group = -> [Sketch078,Pad002,Sketch079,Pad003,Fillet001]
  Origin = -> Origin005
  Tip = -> Fillet001
FEATURE [PartDesign::SubShapeBinder] Binder
  BindCopyOnChange = 0
  BindMode = 0
  ClaimChildren = false
  Context = -> Body006 [Binder.]
  Fuse = false
  MakeFace = true
  OffsetFill = false
  OffsetIntersection = false
  OffsetJoinType = 0
  OffsetOpenResult = false
  PartialLoad = false
  Refine = true
  Relative = true
  Support = -> [Body[Sketch074.]]
  _Version = 2
FEATURE [PartDesign::SubShapeBinder] Binder001
  BindCopyOnChange = 0
  BindMode = 0
  ClaimChildren = false
  Context = -> Body007 [Binder001.]
  Fuse = false
  MakeFace = true
  OffsetFill = false
  OffsetIntersection = false
  OffsetJoinType = 0
  OffsetOpenResult = false
  PartialLoad = false
  Refine = true
  Relative = true
  Support = -> [Body[Sketch075.]]
  _Version = 2
FEATURE [Mesh::Feature] logo_per_PCB_definitivo_positivo
  Placement = pos=(-191,17,-66) rot=(0,1,1;0rad)
FEATURE [Sketcher::SketchObject] Sketch114  label="Sketch114 - base lato DX"
  ArcFitTolerance = 1e-06
  AttachmentSupport = -> [Binder001]
  ExternalGeometry = -> [Binder001]
  FullyConstrained = true
  MakeInternals = false
  MapMode = 5
  Placement = pos=(0,1e-15,0) rot=(0,0.707107,0.707107;3.14159rad)
  sketch-geometry (30):
    g0: Circle CenterX=5.6 CenterY=34.8 CenterZ=0 NormalX=0 NormalY=0 NormalZ=1 AngleXU=0 Radius=1.8
    g1: Circle CenterX=5.6 CenterY=7.6 CenterZ=0 NormalX=0 NormalY=0 NormalZ=1 AngleXU=0 Radius=1.8
    g2: Circle CenterX=24.2 CenterY=26.7 CenterZ=0 NormalX=0 NormalY=0 NormalZ=1 AngleXU=0 Radius=3
    g3: Circle CenterX=24.2 CenterY=15.7 CenterZ=0 NormalX=0 NormalY=0 NormalZ=1 AngleXU=0 Radius=3
    g4: Circle CenterX=36.2 CenterY=21.2 CenterZ=0 NormalX=0 NormalY=0 NormalZ=1 AngleXU=0 Radius=2.8
    g5: Circle CenterX=78.51 CenterY=34.8 CenterZ=0 NormalX=0 NormalY=0 NormalZ=1 AngleXU=0 Radius=1.8
    g6: Circle CenterX=78.51 CenterY=7.6 CenterZ=0 NormalX=0 NormalY=0 NormalZ=1 AngleXU=0 Radius=1.8
    g7: Circle CenterX=184.08 CenterY=34.8 CenterZ=0 NormalX=0 NormalY=0 NormalZ=1 AngleXU=0 Radius=1.8
    g8: Circle CenterX=213.443 CenterY=-76.8316 CenterZ=0 NormalX=0 NormalY=0 NormalZ=1 AngleXU=0 Radius=1.8
    g9: Circle CenterX=179.305 CenterY=-76.8316 CenterZ=0 NormalX=0 NormalY=0 NormalZ=1 AngleXU=0 Radius=1.8
    g10: ArcOfCircle [constr] CenterX=132.428 CenterY=4 CenterZ=0 NormalX=0 NormalY=0 NormalZ=1 AngleXU=0 Radius=16 StartAngle=0.314159 EndAngle=1.5708
    g11: ArcOfCircle CenterX=107.6 CenterY=4 CenterZ=0 NormalX=0 NormalY=0 NormalZ=1 AngleXU=0 Radius=16 StartAngle=1.5708 EndAngle=3.00366
    g12: ArcOfCircle CenterX=207.583 CenterY=4 CenterZ=0 NormalX=0 NormalY=0 NormalZ=1 AngleXU=0 Radius=17 StartAngle=1.85815 EndAngle=3.57792
    g13: ArcOfCircle CenterX=184.801 CenterY=-67.3089 CenterZ=0 NormalX=0 NormalY=0 NormalZ=1 AngleXU=0 Radius=33.7833 StartAngle=5.88425 EndAngle=6.71952
    g14: LineSegment StartX=0 StartY=39.2 StartZ=0 EndX=0 EndY=3.2 EndZ=0
    g15: LineSegment StartX=0 StartY=3.2 StartZ=0 EndX=82.8 EndY=3.2 EndZ=0
    g16: LineSegment StartX=82.8 StartY=3.2 StartZ=0 EndX=82.8 EndY=6.2 EndZ=0
    g17: LineSegment StartX=82.8 StartY=6.2 StartZ=0 EndX=91.752 EndY=6.2 EndZ=0
    g18: LineSegment StartX=107.6 StartY=20 StartZ=0 EndX=132.428 EndY=20 EndZ=0
    g19: LineSegment StartX=147.645 StartY=8.94427 StartZ=0 EndX=176.685 EndY=-80.4316 EndZ=0
    g20: LineSegment StartX=176.685 StartY=-80.4316 StartZ=0 EndX=215.932 EndY=-80.4316 EndZ=0
    g21: LineSegment StartX=215.42 StartY=-53.0314 StartZ=0 EndX=192.176 EndY=-3.18451 EndZ=0
    g22: LineSegment StartX=202.765 StartY=20.303 StartZ=0 EndX=195.887 EndY=39.2 EndZ=0
    g23: LineSegment StartX=195.887 StartY=39.2 StartZ=0 EndX=0 EndY=39.2 EndZ=0
    g24: LineSegment StartX=196.467 StartY=26.4942 StartZ=0 EndX=194.073 EndY=33.0721 EndZ=0
    g25: LineSegment StartX=194.073 StartY=33.0721 StartZ=0 EndX=189.939 EndY=31.5672 EndZ=0
    g26: LineSegment StartX=189.939 StartY=31.5672 StartZ=0 EndX=192.333 EndY=24.9893 EndZ=0
    g27: LineSegment StartX=192.333 StartY=24.9893 StartZ=0 EndX=196.467 EndY=26.4942 EndZ=0
    g28: LineSegment StartX=132.428 StartY=20 StartZ=0 EndX=144.053 EndY=20 EndZ=0
    g29: LineSegment StartX=144.053 StartY=20 StartZ=0 EndX=147.645 EndY=8.94427 EndZ=0
  constraints (65):
    c: Equal(g0,g-25)
    c: Equal(g2,g-29)
    c: Equal(g3,g-30)
    c: Equal(g4,g-28)
    c: Equal(g1,g-26)
    c: Coincident(g0,g-25)
    c: Coincident(g1,g-26)
    c: Coincident(g2,g-29)
    c: Coincident(g3,g-30)
    c: Coincident(g4,g-28)
    c: Equal(g5,g-23)
    c: Equal(g6,g-24)
    c: Coincident(g5,g-23)
    c: Coincident(g6,g-24)
    c: Equal(g7,g-20)
    c: Coincident(g7,g-20)
    c: Equal(g9,g-22)
    c: Coincident(g9,g-22)
    c: Equal(g8,g-21)
    c: Coincident(g8,g-21)
    c: Equal(g13,g-12)
    c: Equal(g12,g-14)
    c: Equal(g10,g-9)
    c: Equal(g11,g-7)
    c: Coincident(g14,g-27)
    c: Coincident(g14,g-27)
    c: Coincident(g15,g14)
    c: Coincident(g15,g-5)
    c: Coincident(g16,g15)
    c: Coincident(g16,g-6)
    c: Coincident(g17,g16)
    c: Coincident(g17,g-7)
    c: Coincident(g11,g17)
    c: Coincident(g11,g-8)
    c: Coincident(g18,g11)
    c: Coincident(g18,g-9)
    c: Coincident(g10,g18)
    c: Coincident(g10,g-10)
    c: Coincident(g19,g10)
    c: Coincident(g19,g-11)
    c: Coincident(g20,g19)
    c: Coincident(g20,g-12)
    c: Coincident(g13,g20)
    c: Coincident(g13,g-13)
    c: Coincident(g21,g13)
    c: Coincident(g21,g-14)
    c: Coincident(g12,g21)
    c: Coincident(g12,g-15)
    c: Coincident(g22,g12)
    c: Coincident(g22,g-15)
    c: Coincident(g23,g22)
    c: Coincident(g23,g14)
    c: Coincident(g24,g-18)
    c: Coincident(g24,g-16)
    c: Coincident(g25,g24)
    c: Coincident(g25,g-19)
    c: Coincident(g26,g25)
    c: Coincident(g26,g-19)
    c: Coincident(g27,g26)
    c: Coincident(g27,g24)
    c: Coincident(g29,g10)
    c: Coincident(g28,g10)
    c: Coincident(g29,g28)
    c: Parallel(g28,g18)
    c: Parallel(g29,g19)
FEATURE [PartDesign::Pad] Pad011
  Direction = (0,1,-2e-16)
  Length = 2
  Length2 = 10
  Profile = -> Sketch114
  ReferenceAxis = -> Sketch114 [N_Axis]
  Refine = true
  Reversed = true
  Suppressed = false
  Type = 0
FEATURE [Sketcher::SketchObject] Sketch115
  ArcFitTolerance = 1e-06
  AttachmentSupport = -> [Pad011]
  ExternalGeometry = -> [Binder001]
  FullyConstrained = true
  MakeInternals = false
  MapMode = 5
  Placement = pos=(0,1.7e-15,0) rot=(0,0.707107,0.707107;3.14159rad)
  sketch-geometry (4):
    g0: ArcOfCircle CenterX=24.2 CenterY=26.7 CenterZ=0 NormalX=0 NormalY=0 NormalZ=1 AngleXU=0 Radius=3 StartAngle=4.48384e-08 EndAngle=3.14159
    g1: ArcOfCircle CenterX=24.2 CenterY=15.7 CenterZ=0 NormalX=0 NormalY=0 NormalZ=1 AngleXU=0 Radius=3 StartAngle=3.14159 EndAngle=6.28318
    g2: LineSegment StartX=21.2 StartY=26.7 StartZ=0 EndX=21.2 EndY=15.7 EndZ=0
    g3: LineSegment StartX=27.2 StartY=26.7 StartZ=0 EndX=27.2 EndY=15.7 EndZ=0
  constraints (12):
    c: Equal(g1,g-4)
    c: Equal(g0,g-3)
    c: Coincident(g0,g-3)
    c: Coincident(g1,g-4)
    c: Vertical(g2)
    c: Vertical(g3)
    c: Tangent(g3,g-3)
    c: Tangent(g2,g-3)
    c: Coincident(g0,g2)
    c: Coincident(g0,g3)
    c: Coincident(g1,g2)
    c: Coincident(g3,g1)
FEATURE [Sketcher::SketchObject] Sketch117  label="Sketch117 - fori per inserto M3 x 3 x 4.5"
  ArcFitTolerance = 1e-06
  AttachmentSupport = -> [Pad011]
  ExternalGeometry = -> [Binder001]
  FullyConstrained = true
  MakeInternals = false
  MapMode = 5
  Placement = pos=(0,1.7e-15,0) rot=(0,0.707107,0.707107;3.14159rad)
  sketch-geometry (4):
    g0: Circle CenterX=43.2 CenterY=30.3 CenterZ=0 NormalX=0 NormalY=0 NormalZ=1 AngleXU=0 Radius=2.25
    g1: Circle CenterX=43.2 CenterY=12.1 CenterZ=0 NormalX=0 NormalY=0 NormalZ=1 AngleXU=0 Radius=2.25
    g2: Circle CenterX=18.6 CenterY=30.3 CenterZ=0 NormalX=0 NormalY=0 NormalZ=1 AngleXU=0 Radius=2.25
    g3: Circle CenterX=18.6 CenterY=12.1 CenterZ=0 NormalX=0 NormalY=0 NormalZ=1 AngleXU=0 Radius=2.25
  constraints (8):
    c: Diameter(g0) = 4.5
    c: Diameter(g1) = 4.5
    c: Diameter(g2) = 4.5
    c: Diameter(g3) = 4.5
    c: Coincident(g2,g-3)
    c: Coincident(g3,g-6)
    c: Coincident(g0,g-4)
    c: Coincident(g1,g-5)
FEATURE [Sketcher::SketchObject] Sketch118
  ArcFitTolerance = 1e-06
  AttachmentSupport = -> [Pad011]
  ExternalGeometry = -> [Binder001]
  FullyConstrained = true
  MakeInternals = false
  MapMode = 5
  Placement = pos=(0,-2,0) rot=(1,0,0;1.5708rad)
  sketch-geometry (12):
    g0: Circle CenterX=-78.51 CenterY=34.8 CenterZ=0 NormalX=0 NormalY=0 NormalZ=1 AngleXU=0 Radius=1.8
    g1: Circle CenterX=-78.51 CenterY=7.6 CenterZ=0 NormalX=0 NormalY=0 NormalZ=1 AngleXU=0 Radius=1.8
    g2: Circle CenterX=-5.6 CenterY=34.8 CenterZ=0 NormalX=0 NormalY=0 NormalZ=1 AngleXU=0 Radius=1.8
    g3: Circle CenterX=-5.6 CenterY=7.6 CenterZ=0 NormalX=0 NormalY=0 NormalZ=1 AngleXU=0 Radius=1.8
    g4: LineSegment StartX=0 StartY=39.2 StartZ=0 EndX=0 EndY=3.2 EndZ=0
    g5: LineSegment StartX=0 StartY=3.2 StartZ=0 EndX=-82.8 EndY=3.2 EndZ=0
    g6: LineSegment StartX=-82.8 StartY=3.2 StartZ=0 EndX=-82.8 EndY=39.2 EndZ=0
    g7: LineSegment StartX=-82.8 StartY=39.2 StartZ=0 EndX=0 EndY=39.2 EndZ=0
    g8: ArcOfCircle CenterX=-65 CenterY=21.2 CenterZ=0 NormalX=0 NormalY=0 NormalZ=1 AngleXU=0 Radius=10 StartAngle=1.5708 EndAngle=4.71239
    g9: ArcOfCircle CenterX=-19 CenterY=21.2 CenterZ=0 NormalX=0 NormalY=0 NormalZ=1 AngleXU=0 Radius=10 StartAngle=4.71239 EndAngle=7.85398
    g10: LineSegment StartX=-65 StartY=31.2 StartZ=0 EndX=-19 EndY=31.2 EndZ=0
    g11: LineSegment StartX=-65 StartY=11.2 StartZ=0 EndX=-19 EndY=11.2 EndZ=0
  constraints (25):
    c: Equal(g2,g-5)
    c: Equal(g3,g-7)
    c: Equal(g1,g-6)
    c: Equal(g0,g-4)
    c: Coincident(g0,g-4)
    c: Coincident(g1,g-6)
    c: Coincident(g3,g-7)
    c: Coincident(g2,g-5)
    c: Coincident(g4,g-8)
    c: Coincident(g4,g-9)
    c: Coincident(g5,g4)
    c: Coincident(g5,g-10)
    c: Coincident(g6,g5)
    c: PointOnObject(g6,g-3)
    c: Vertical(g6)
    c: Coincident(g7,g6)
    c: Coincident(g7,g4)
    c: Tangent(g8,g10) = 1.5708
    c: Tangent(g8,g11) = -1.5708
    c: Tangent(g9,g10) = 1.5708
    c: Tangent(g9,g11) = -1.5708
    c: Equal(g8,g9)
    c: Radius(g8) = 10
    c: Coincident(g8,g-11)
    c: Coincident(g9,g-12)
FEATURE [Sketcher::SketchObject] Sketch120
  ArcFitTolerance = 1e-06
  AttachmentSupport = -> [Pad011]
  ExternalGeometry = -> [Binder001]
  FullyConstrained = true
  MakeInternals = false
  MapMode = 5
  Placement = pos=(0,-2,0) rot=(1,0,0;1.5708rad)
  sketch-geometry (4):
    g0: LineSegment StartX=-137.815 StartY=39.2 StartZ=0 EndX=-142.655 EndY=24.303 EndZ=0
    g1: LineSegment StartX=-137.815 StartY=39.2 StartZ=0 EndX=-110.815 EndY=39.2 EndZ=0
    g2: LineSegment StartX=-142.655 StartY=24.303 StartZ=0 EndX=-110.815 EndY=24.303 EndZ=0
    g3: ArcOfCircle CenterX=-92.2534 CenterY=31.7515 CenterZ=0 NormalX=0 NormalY=0 NormalZ=1 AngleXU=0 Radius=20 StartAngle=2.75997 EndAngle=3.52321
  constraints (12):
    c: PointOnObject(g0,g-3)
    c: Coincident(g1,g0)
    c: PointOnObject(g1,g-3)
    c: Coincident(g2,g0)
    c: Horizontal(g2)
    c: Tangent(g0,g-4)
    c: Vertical(g2,g1)
    c: DistanceX(g1,g1) = 27
    c: DistanceY(g-6,g0) = 4
    c: Radius(g3) = 20
    c: Coincident(g3,g1)
    c: Coincident(g3,g2)
FEATURE [Sketcher::SketchObject] Sketch121
  ArcFitTolerance = 1e-06
  AttachmentSupport = -> [Pad011]
  ExternalGeometry = -> [Binder001]
  FullyConstrained = true
  MakeInternals = false
  MapMode = 5
  Placement = pos=(0,-2,0) rot=(1,0,0;1.5708rad)
  sketch-geometry (15):
    g0: LineSegment StartX=-137.815 StartY=39.2 StartZ=0 EndX=-143.955 EndY=20.303 EndZ=0
    g1: LineSegment StartX=-143.955 StartY=20.303 StartZ=0 EndX=-190.141 EndY=20.303 EndZ=0
    g2: LineSegment StartX=-190.141 StartY=20.303 StartZ=0 EndX=-186.139 EndY=31.3 EndZ=0
    g3: LineSegment StartX=-178.754 StartY=39.2 StartZ=0 EndX=-180.791 EndY=33.6029 EndZ=0
    g4: ArcOfCircle CenterX=-184.08 CenterY=34.8 CenterZ=0 NormalX=0 NormalY=0 NormalZ=1 AngleXU=0 Radius=3.5 StartAngle=4.71239 EndAngle=5.93412
    g5: LineSegment StartX=-184.08 StartY=31.3 StartZ=0 EndX=-186.139 EndY=31.3 EndZ=0
    g6: LineSegment StartX=-137.815 StartY=39.2 StartZ=0 EndX=-156.815 EndY=39.2 EndZ=0
    g7: LineSegment StartX=-168.815 StartY=39.2 StartZ=0 EndX=-178.754 EndY=39.2 EndZ=0
    g8: LineSegment StartX=-157.815 StartY=39.2 StartZ=0 EndX=-167.815 EndY=39.2 EndZ=0
    g9: LineSegment StartX=-168.815 StartY=31.2 StartZ=0 EndX=-156.815 EndY=31.2 EndZ=0
    g10: LineSegment StartX=-167.436 StartY=36.2 StartZ=0 EndX=-157.436 EndY=36.2 EndZ=0
    g11: ArcOfCircle CenterX=-176.411 CenterY=35.2 CenterZ=0 NormalX=0 NormalY=0 NormalZ=1 AngleXU=0 Radius=20 StartAngle=6.08183 EndAngle=6.48454
    g12: ArcOfCircle CenterX=-188.411 CenterY=35.2 CenterZ=0 NormalX=0 NormalY=0 NormalZ=1 AngleXU=0 Radius=20 StartAngle=6.08183 EndAngle=6.48454
    g13: ArcOfCircle CenterX=-177.411 CenterY=35.2 CenterZ=0 NormalX=0 NormalY=0 NormalZ=1 AngleXU=0 Radius=20 StartAngle=0.0500209 EndAngle=0.201358
    g14: ArcOfCircle CenterX=-187.411 CenterY=35.2 CenterZ=0 NormalX=0 NormalY=0 NormalZ=1 AngleXU=0 Radius=20 StartAngle=0.0500209 EndAngle=0.201358
  constraints (46):
    c: PointOnObject(g0,g-3)
    c: Tangent(g0,g-5)
    c: Coincident(g1,g0)
    c: Horizontal(g1)
    c: Coincident(g2,g1)
    c: PointOnObject(g3,g-3)
    c: Parallel(g3,g-6)
    c: Parallel(g2,g-6)
    c: Radius(g4) = 3.5
    c: Coincident(g4,g-7)
    c: Tangent(g3,g4) = 1.5708
    c: Horizontal(g5)
    c: Tangent(g5,g4) = 1.5708
    c: DistanceX(g-8,g5) = 3.8
    c: Coincident(g2,g5)
    c: Coincident(g6,g0)
    c: PointOnObject(g6,g-3)
    c: DistanceX(g6,g6) = 19
    c: PointOnObject(g7,g-3)
    c: DistanceX(g7,g6) = 12
    c: Coincident(g7,g3)
    c: PointOnObject(g8,g-3)
    c: PointOnObject(g8,g-3)
    c: DistanceX(g8,g8) = 10
    c: DistanceX(g8,g6) = 1
    c: Horizontal(g9)
    c: Vertical(g7,g9)
    c: Vertical(g6,g9)
    c: DistanceY(g9,g7) = 8
    c: Horizontal(g10)
    c: Equal(g8,g10)
    c: DistanceY(g10,g8) = 3
    c: Radius(g11) = 20
    c: Coincident(g11,g6)
    c: Coincident(g11,g9)
    c: Radius(g12) = 20
    c: Coincident(g12,g7)
    c: Coincident(g12,g9)
    c: Equal(g13,g11)
    c: Coincident(g13,g8)
    c: Coincident(g13,g10)
    c: Horizontal(g13,g11)
    c: Equal(g14,g12)
    c: Coincident(g14,g8)
    c: Coincident(g14,g10)
    c: Horizontal(g1,g-6)
FEATURE [Sketcher::SketchObject] Sketch122
  ArcFitTolerance = 1e-06
  AttachmentSupport = -> [Pad011]
  ExternalGeometry = -> [Binder001]
  FullyConstrained = true
  MakeInternals = false
  MapMode = 5
  Placement = pos=(0,-2,0) rot=(1,0,0;1.5708rad)
  sketch-geometry (8):
    g0: ArcOfCircle CenterX=-184.801 CenterY=-67.3089 CenterZ=0 NormalX=0 NormalY=0 NormalZ=1 AngleXU=0 Radius=33.7833 StartAngle=2.70526 EndAngle=3.54053
    g1: LineSegment StartX=-176.685 StartY=-80.4316 StartZ=0 EndX=-215.932 EndY=-80.4316 EndZ=0
    g2: LineSegment StartX=-215.42 StartY=-53.0314 StartZ=0 EndX=-192.176 EndY=-3.18454 EndZ=0
    g3: ArcOfCircle CenterX=-207.583 CenterY=4 CenterZ=0 NormalX=0 NormalY=0 NormalZ=1 AngleXU=0 Radius=17 StartAngle=5.84685 EndAngle=7.56663
    g4: Circle CenterX=-213.443 CenterY=-76.8316 CenterZ=0 NormalX=0 NormalY=0 NormalZ=1 AngleXU=0 Radius=3
    g5: Circle CenterX=-179.305 CenterY=-76.8316 CenterZ=0 NormalX=0 NormalY=0 NormalZ=1 AngleXU=0 Radius=3
    g6: LineSegment StartX=-143.955 StartY=20.303 StartZ=0 EndX=-176.685 EndY=-80.4316 EndZ=0
    g7: LineSegment StartX=-202.765 StartY=20.303 StartZ=0 EndX=-143.955 EndY=20.303 EndZ=0
  constraints (18):
    c: Coincident(g0,g-7)
    c: Coincident(g0,g-8)
    c: Coincident(g1,g0)
    c: Tangent(g2,g-5)
    c: Coincident(g3,g-6)
    c: Coincident(g2,g3)
    c: Coincident(g0,g2)
    c: Diameter(g4) = 6
    c: Diameter(g5) = 6
    c: Coincident(g4,g-9)
    c: Coincident(g5,g-10)
    c: Horizontal(g1)
    c: Coincident(g6,g1)
    c: Tangent(g6,g-4)
    c: Coincident(g3,g-6)
    c: Coincident(g7,g3)
    c: Horizontal(g7)
    c: Coincident(g7,g6)
FEATURE [Sketcher::SketchObject] Sketch123
  ArcFitTolerance = 1e-06
  AttachmentSupport = -> [Pad011]
  ExternalGeometry = -> [Binder001]
  FullyConstrained = true
  MakeInternals = false
  MapMode = 5
  Placement = pos=(0,-2,0) rot=(1,0,0;1.5708rad)
  sketch-geometry (4):
    g0: LineSegment StartX=-108 StartY=36.8 StartZ=0 EndX=-90 EndY=36.8 EndZ=0
    g1: LineSegment StartX=-108 StartY=36.8 StartZ=0 EndX=-108 EndY=26.8 EndZ=0
    g2: LineSegment StartX=-108 StartY=26.8 StartZ=0 EndX=-90 EndY=26.8 EndZ=0
    g3: ArcOfCircle CenterX=-94 CenterY=31.8 CenterZ=0 NormalX=0 NormalY=0 NormalZ=1 AngleXU=0 Radius=6.40312 StartAngle=5.38713 EndAngle=7.17924
  constraints (13):
    c: Horizontal(g0)
    c: Coincident(g1,g0)
    c: Vertical(g1)
    c: Coincident(g2,g1)
    c: Horizontal(g2)
    c: DistanceX(g0,g0) = 18
    c: DistanceY(g1,g1) = 10
    c: Equal(g0,g2)
    c: DistanceX(g0,g-3) = 90
    c: DistanceY(g0,g-3) = 2.4
    c: Coincident(g3,g0)
    c: Coincident(g3,g2)
    c: DistanceX(g3,g0) = 4
FEATURE [PartDesign::Chamfer] Chamfer014
  Angle = 45
  Base = -> Pad011 [Edge80,Edge4,Edge7]
  BaseFeature = -> Pad011
  ChamferType = 0
  FlipDirection = false
  Refine = true
  Size = 1.9
  Size2 = 1
  SupportTransform = false
  Suppressed = false
  UseAllEdges = false
FEATURE [PartDesign::Pocket] Pocket006
  BaseFeature = -> Chamfer014
  Direction = (0,-1,2e-16)
  Length = 1.2
  Length2 = 5
  Profile = -> Sketch115
  ReferenceAxis = -> Sketch115 [N_Axis]
  Refine = true
  Suppressed = false
  Type = 0
FEATURE [Sketcher::SketchObject] Sketch116  label="Sketch116 - pieno per inserto M3 x 3 x 4,5"
  ArcFitTolerance = 1e-06
  AttachmentSupport = -> [Pocket006]
  ExternalGeometry = -> [Binder001]
  FullyConstrained = true
  MakeInternals = false
  MapMode = 5
  Placement = pos=(0,1.7e-15,0) rot=(0,0.707107,0.707107;3.14159rad)
  sketch-geometry (4):
    g0: Circle CenterX=43.2 CenterY=30.3 CenterZ=0 NormalX=0 NormalY=0 NormalZ=1 AngleXU=0 Radius=3.4
    g1: Circle CenterX=43.2 CenterY=12.1 CenterZ=0 NormalX=0 NormalY=0 NormalZ=1 AngleXU=0 Radius=3.4
    g2: Circle CenterX=18.6 CenterY=30.3 CenterZ=0 NormalX=0 NormalY=0 NormalZ=1 AngleXU=0 Radius=3.4
    g3: Circle CenterX=18.6 CenterY=12.1 CenterZ=0 NormalX=0 NormalY=0 NormalZ=1 AngleXU=0 Radius=3.4
  constraints (8):
    c: Diameter(g0) = 6.8
    c: Diameter(g1) = 6.8
    c: Diameter(g2) = 6.8
    c: Diameter(g3) = 6.8
    c: Coincident(g2,g-3)
    c: Coincident(g0,g-4)
    c: Coincident(g3,g-6)
    c: Coincident(g1,g-5)
FEATURE [PartDesign::Pad] Pad012
  BaseFeature = -> Pocket006
  Direction = (0,1,-2e-16)
  Length = 2.4
  Length2 = 10
  Profile = -> Sketch116
  ReferenceAxis = -> Sketch116 [N_Axis]
  Refine = true
  Suppressed = false
  Type = 0
FEATURE [PartDesign::Pocket] Pocket007
  BaseFeature = -> Pad012
  Direction = (0,-1,2e-16)
  Length = 0.6
  Length2 = 2.4
  Profile = -> Sketch117
  ReferenceAxis = -> Sketch117 [N_Axis]
  Refine = true
  Suppressed = false
  Type = 4
FEATURE [PartDesign::Pad] Pad013
  BaseFeature = -> Pocket007
  Direction = (0,-1,2e-16)
  Length = 1.6
  Length2 = 10
  Profile = -> Sketch118
  ReferenceAxis = -> Sketch118 [N_Axis]
  Refine = true
  Suppressed = false
  Type = 0
FEATURE [Sketcher::SketchObject] Sketch119
  ArcFitTolerance = 1e-06
  AttachmentSupport = -> [Pad013]
  ExternalGeometry = -> [Binder001]
  FullyConstrained = true
  MakeInternals = false
  MapMode = 5
  Placement = pos=(0,-3.6,0) rot=(1,0,0;1.5708rad)
  sketch-geometry (21):
    g0: LineSegment [constr] StartX=-82.8 StartY=3.2 StartZ=0 EndX=-82.8 EndY=39.2 EndZ=0
    g1: ArcOfCircle CenterX=-78.51 CenterY=34.8 CenterZ=0 NormalX=0 NormalY=0 NormalZ=1 AngleXU=0 Radius=3.5 StartAngle=4.71239 EndAngle=6.28319
    g2: ArcOfCircle CenterX=-78.51 CenterY=7.6 CenterZ=0 NormalX=0 NormalY=0 NormalZ=1 AngleXU=0 Radius=3.5 StartAngle=0 EndAngle=1.5708
    g3: ArcOfCircle CenterX=-5.6 CenterY=34.8 CenterZ=0 NormalX=0 NormalY=0 NormalZ=1 AngleXU=0 Radius=3.5 StartAngle=3.14159 EndAngle=4.71239
    g4: ArcOfCircle CenterX=-5.6 CenterY=7.6 CenterZ=0 NormalX=0 NormalY=0 NormalZ=1 AngleXU=0 Radius=3.5 StartAngle=1.5708 EndAngle=3.14159
    g5: LineSegment StartX=0 StartY=39.2 StartZ=0 EndX=0 EndY=31.3 EndZ=0
    g6: LineSegment StartX=0 StartY=39.2 StartZ=0 EndX=-9.1 EndY=39.2 EndZ=0
    g7: LineSegment StartX=0 StartY=3.2 StartZ=0 EndX=0 EndY=11.1 EndZ=0
    g8: LineSegment StartX=0 StartY=3.2 StartZ=0 EndX=-9.1 EndY=3.2 EndZ=0
    g9: LineSegment StartX=-82.8 StartY=3.2 StartZ=0 EndX=-75.01 EndY=3.2 EndZ=0
    g10: LineSegment StartX=-82.8 StartY=3.2 StartZ=0 EndX=-82.8 EndY=11.1 EndZ=0
    g11: LineSegment StartX=-82.8 StartY=39.2 StartZ=0 EndX=-82.8 EndY=31.3 EndZ=0
    g12: LineSegment StartX=-82.8 StartY=39.2 StartZ=0 EndX=-75.01 EndY=39.2 EndZ=0
    g13: LineSegment StartX=-82.8 StartY=31.3 StartZ=0 EndX=-78.51 EndY=31.3 EndZ=0
    g14: LineSegment StartX=-75.01 StartY=39.2 StartZ=0 EndX=-75.01 EndY=34.8 EndZ=0
    g15: LineSegment StartX=-82.8 StartY=11.1 StartZ=0 EndX=-78.51 EndY=11.1 EndZ=0
    g16: LineSegment StartX=-75.01 StartY=3.2 StartZ=0 EndX=-75.01 EndY=7.6 EndZ=0
    g17: LineSegment StartX=-9.1 StartY=39.2 StartZ=0 EndX=-9.1 EndY=34.8 EndZ=0
    g18: LineSegment StartX=0 StartY=31.3 StartZ=0 EndX=-5.6 EndY=31.3 EndZ=0
    g19: LineSegment StartX=0 StartY=11.1 StartZ=0 EndX=-5.6 EndY=11.1 EndZ=0
    g20: LineSegment StartX=-9.1 StartY=3.2 StartZ=0 EndX=-9.1 EndY=7.6 EndZ=0
  constraints (51):
    c: Coincident(g0,g-10)
    c: PointOnObject(g0,g-8)
    c: Vertical(g0)
    c: Coincident(g1,g-3)
    c: Coincident(g2,g-4)
    c: Coincident(g3,g-5)
    c: Coincident(g4,g-6)
    c: Radius(g4) = 3.5
    c: Radius(g3) = 3.5
    c: Radius(g1) = 3.5
    c: Radius(g2) = 3.5
    c: Coincident(g5,g-9)
    c: PointOnObject(g5,g-9)
    c: Coincident(g6,g5)
    c: PointOnObject(g6,g-8)
    c: Coincident(g7,g-9)
    c: PointOnObject(g7,g-9)
    c: Coincident(g8,g7)
    c: PointOnObject(g8,g-7)
    c: Coincident(g9,g0)
    c: PointOnObject(g9,g-7)
    c: Coincident(g10,g0)
    c: PointOnObject(g10,g0)
    c: Coincident(g11,g0)
    c: PointOnObject(g11,g0)
    c: Coincident(g12,g0)
    c: PointOnObject(g12,g-8)
    c: Coincident(g13,g11)
    c: Horizontal(g13)
    c: Coincident(g14,g12)
    c: Vertical(g14)
    c: Coincident(g15,g10)
    c: Horizontal(g15)
    c: Coincident(g16,g9)
    c: Vertical(g16)
    c: Coincident(g17,g6)
    c: Vertical(g17)
    c: Coincident(g18,g5)
    c: Horizontal(g18)
    c: Coincident(g19,g7)
    c: Horizontal(g19)
    c: Coincident(g20,g8)
    c: Vertical(g20)
    c: Tangent(g20,g4) = 1.5708
    c: Tangent(g4,g19) = -1.5708
    c: Tangent(g18,g3) = 1.5708
    c: Tangent(g3,g17) = -1.5708
    c: Tangent(g13,g1) = -1.5708
    c: Tangent(g1,g14) = 1.5708
    c: Tangent(g16,g2) = -1.5708
    c: Tangent(g2,g15) = 1.5708
FEATURE [PartDesign::Pocket] Pocket008
  BaseFeature = -> Pad013
  Direction = (0,1,-2e-16)
  Length = 1.6
  Length2 = 5
  Profile = -> Sketch119
  ReferenceAxis = -> Sketch119 [N_Axis]
  Refine = true
  Suppressed = false
  Type = 0
FEATURE [PartDesign::Pad] Pad017
  BaseFeature = -> Pocket008
  Direction = (0,-1,2e-16)
  Length = 1.6
  Length2 = 10
  Profile = -> Sketch123
  ReferenceAxis = -> Sketch123 [N_Axis]
  Refine = true
  Suppressed = false
  Type = 0
FEATURE [Sketcher::SketchObject] Sketch125
  ArcFitTolerance = 1e-06
  AttachmentSupport = -> [Pad017]
  ExternalGeometry = -> [Pad017]
  FullyConstrained = true
  MakeInternals = false
  MapMode = 5
  Placement = pos=(0,-3.6,8e-16) rot=(1,0,0;1.5708rad)
  sketch-geometry (20):
    g0: LineSegment StartX=-108 StartY=35.8 StartZ=0 EndX=-108 EndY=35 EndZ=0
    g1: LineSegment StartX=-108 StartY=35 StartZ=0 EndX=-97 EndY=35 EndZ=0
    g2: LineSegment StartX=-97 StartY=35 StartZ=0 EndX=-97 EndY=35.8 EndZ=0
    g3: LineSegment StartX=-97 StartY=35.8 StartZ=0 EndX=-108 EndY=35.8 EndZ=0
    g4: LineSegment StartX=-108 StartY=28.6 StartZ=0 EndX=-108 EndY=27.8 EndZ=0
    g5: LineSegment StartX=-108 StartY=27.8 StartZ=0 EndX=-97 EndY=27.8 EndZ=0
    g6: LineSegment StartX=-97 StartY=27.8 StartZ=0 EndX=-97 EndY=28.6 EndZ=0
    g7: LineSegment StartX=-97 StartY=28.6 StartZ=0 EndX=-108 EndY=28.6 EndZ=0
    g8: LineSegment StartX=-108 StartY=30.4 StartZ=0 EndX=-108 EndY=29.6 EndZ=0
    g9: LineSegment StartX=-108 StartY=29.6 StartZ=0 EndX=-97 EndY=29.6 EndZ=0
    g10: LineSegment StartX=-97 StartY=29.6 StartZ=0 EndX=-97 EndY=30.4 EndZ=0
    g11: LineSegment StartX=-97 StartY=30.4 StartZ=0 EndX=-108 EndY=30.4 EndZ=0
    g12: LineSegment StartX=-108 StartY=32.2 StartZ=0 EndX=-108 EndY=31.4 EndZ=0
    g13: LineSegment StartX=-108 StartY=31.4 StartZ=0 EndX=-97 EndY=31.4 EndZ=0
    g14: LineSegment StartX=-97 StartY=31.4 StartZ=0 EndX=-97 EndY=32.2 EndZ=0
    g15: LineSegment StartX=-97 StartY=32.2 StartZ=0 EndX=-108 EndY=32.2 EndZ=0
    g16: LineSegment StartX=-108 StartY=34 StartZ=0 EndX=-108 EndY=33.2 EndZ=0
    g17: LineSegment StartX=-108 StartY=33.2 StartZ=0 EndX=-97 EndY=33.2 EndZ=0
    g18: LineSegment StartX=-97 StartY=33.2 StartZ=0 EndX=-97 EndY=34 EndZ=0
    g19: LineSegment StartX=-97 StartY=34 StartZ=0 EndX=-108 EndY=34 EndZ=0
  constraints (55):
    c: Coincident(g1,g0)
    c: Horizontal(g1)
    c: Coincident(g2,g1)
    c: Vertical(g2)
    c: Coincident(g3,g2)
    c: Horizontal(g3)
    c: Coincident(g3,g0)
    c: DistanceX(g1,g1) = 11
    c: DistanceY(g2,g2) = 0.8
    c: Coincident(g5,g4)
    c: Horizontal(g5)
    c: Coincident(g6,g5)
    c: Vertical(g6)
    c: Coincident(g7,g6)
    c: Horizontal(g7)
    c: Coincident(g7,g4)
    c: Coincident(g9,g8)
    c: Horizontal(g9)
    c: Coincident(g10,g9)
    c: Vertical(g10)
    c: Coincident(g11,g10)
    c: Horizontal(g11)
    c: Coincident(g11,g8)
    c: Coincident(g13,g12)
    c: Horizontal(g13)
    c: Coincident(g14,g13)
    c: Vertical(g14)
    c: Coincident(g15,g14)
    c: Horizontal(g15)
    c: Coincident(g15,g12)
    c: Coincident(g17,g16)
    c: Horizontal(g17)
    c: Coincident(g18,g17)
    c: Vertical(g18)
    c: Coincident(g19,g18)
    c: Horizontal(g19)
    c: Coincident(g19,g16)
    c: Equal(g3,g19)
    c: Equal(g3,g15)
    c: Equal(g3,g11)
    c: Equal(g3,g7)
    c: Equal(g2,g18)
    c: Equal(g2,g14)
    c: Equal(g2,g10)
    c: Equal(g2,g6)
    c: DistanceY(g-4,g4) = 1
    c: DistanceY(g4,g8) = 1
    c: DistanceY(g8,g12) = 1
    c: DistanceY(g12,g16) = 1
    c: DistanceY(g16,g0) = 1
    c: Tangent(g0,g-5)
    c: Tangent(g16,g-5)
    c: Tangent(g12,g-5)
    c: Tangent(g8,g-5)
    c: Tangent(g4,g-5)
FEATURE [PartDesign::Chamfer] Chamfer009
  Angle = 45
  Base = -> Pad017 [Edge151,Edge154]
  BaseFeature = -> Pad017
  ChamferType = 1
  FlipDirection = false
  Refine = true
  Size = 1.5
  Size2 = 2.8
  SupportTransform = false
  Suppressed = false
  UseAllEdges = false
FEATURE [PartDesign::Pocket] Pocket009
  BaseFeature = -> Chamfer009
  Direction = (0,1,-2e-16)
  Length = 1
  Length2 = 5
  Profile = -> Sketch125
  ReferenceAxis = -> Sketch125 [N_Axis]
  Refine = true
  Suppressed = false
  Type = 0
FEATURE [PartDesign::Pad] Pad014
  BaseFeature = -> Pocket009
  Direction = (0,-1,2e-16)
  Length = 0.8
  Length2 = 10
  Profile = -> Sketch120
  ReferenceAxis = -> Sketch120 [N_Axis]
  Refine = true
  Suppressed = false
  Type = 0
FEATURE [Sketcher::SketchObject] Sketch124
  ArcFitTolerance = 1e-06
  AttachmentSupport = -> [Pad014]
  ExternalGeometry = -> [Binder001]
  FullyConstrained = true
  MakeInternals = false
  MapMode = 5
  Placement = pos=(0,-2.8,6e-16) rot=(1,0,0;1.5708rad)
  sketch-geometry (4):
    g0: LineSegment StartX=-129 StartY=39.2 StartZ=0 EndX=-131.599 EndY=31.2 EndZ=0
    g1: LineSegment StartX=-118 StartY=39.2 StartZ=0 EndX=-120.599 EndY=31.2 EndZ=0
    g2: LineSegment StartX=-129 StartY=39.2 StartZ=0 EndX=-118 EndY=39.2 EndZ=0
    g3: LineSegment StartX=-120.599 StartY=31.2 StartZ=0 EndX=-131.599 EndY=31.2 EndZ=0
  constraints (12):
    c: PointOnObject(g0,g-3)
    c: PointOnObject(g1,g-3)
    c: Parallel(g-4,g0)
    c: Parallel(g-4,g1)
    c: Coincident(g2,g0)
    c: Coincident(g2,g1)
    c: DistanceX(g2,g2) = 11
    c: DistanceY(g1,g1) = 8
    c: Coincident(g3,g1)
    c: Horizontal(g3)
    c: Coincident(g3,g0)
    c: DistanceX(g1,g-3) = 118
FEATURE [PartDesign::Pad] Pad018
  BaseFeature = -> Pad014
  Direction = (0,-1,2e-16)
  Length = 1.2
  Length2 = 10
  Profile = -> Sketch124
  ReferenceAxis = -> Sketch124 [N_Axis]
  Refine = true
  Suppressed = false
  Type = 0
FEATURE [Sketcher::SketchObject] Sketch126
  ArcFitTolerance = 1e-06
  AttachmentSupport = -> [Pad018]
  ExternalGeometry = -> [Pad018]
  FullyConstrained = true
  MakeInternals = false
  MapMode = 5
  Placement = pos=(0,-4,0) rot=(1,0,0;1.5708rad)
  sketch-geometry (8):
    g0: LineSegment StartX=-129.877 StartY=36.5 StartZ=0 EndX=-130.137 EndY=35.7 EndZ=0
    g1: LineSegment StartX=-130.69 StartY=34 StartZ=0 EndX=-130.95 EndY=33.2 EndZ=0
    g2: LineSegment StartX=-129.877 StartY=36.5 StartZ=0 EndX=-118.877 EndY=36.5 EndZ=0
    g3: LineSegment StartX=-130.137 StartY=35.7 StartZ=0 EndX=-119.137 EndY=35.7 EndZ=0
    g4: LineSegment StartX=-130.69 StartY=34 StartZ=0 EndX=-119.69 EndY=34 EndZ=0
    g5: LineSegment StartX=-130.95 StartY=33.2 StartZ=0 EndX=-119.95 EndY=33.2 EndZ=0
    g6: LineSegment StartX=-118.877 StartY=36.5 StartZ=0 EndX=-119.137 EndY=35.7 EndZ=0
    g7: LineSegment StartX=-119.69 StartY=34 StartZ=0 EndX=-119.95 EndY=33.2 EndZ=0
  constraints (20):
    c: Coincident(g2,g0)
    c: Horizontal(g2)
    c: Coincident(g3,g0)
    c: Horizontal(g3)
    c: Coincident(g4,g1)
    c: Horizontal(g4)
    c: Coincident(g5,g1)
    c: Horizontal(g5)
    c: Coincident(g6,g2)
    c: Coincident(g6,g3)
    c: Coincident(g7,g4)
    c: Coincident(g7,g5)
    c: Tangent(g0,g-4)
    c: Tangent(g6,g-5)
    c: Tangent(g1,g-4)
    c: Tangent(g7,g-5)
    c: DistanceY(g3,g2) = 0.8
    c: DistanceY(g5,g4) = 0.8
    c: DistanceY(g-6,g1) = 2
    c: DistanceY(g-6,g0) = 4.5
FEATURE [PartDesign::Chamfer] Chamfer008
  Angle = 45
  Base = -> Pad018 [Edge257]
  BaseFeature = -> Pad018
  ChamferType = 1
  FlipDirection = false
  Refine = true
  Size = 1
  Size2 = 6
  SupportTransform = false
  Suppressed = false
  UseAllEdges = false
FEATURE [PartDesign::Pocket] Pocket010
  BaseFeature = -> Chamfer008
  Direction = (0,1,-2e-16)
  Length = 1
  Length2 = 5
  Profile = -> Sketch126
  ReferenceAxis = -> Sketch126 [N_Axis]
  Refine = true
  Suppressed = false
  Type = 0
FEATURE [PartDesign::Pad] Pad015
  BaseFeature = -> Pocket010
  Direction = (0,-1,2e-16)
  Length = 2
  Length2 = 10
  Profile = -> Sketch121
  ReferenceAxis = -> Sketch121 [N_Axis]
  Refine = true
  Suppressed = false
  Type = 0
FEATURE [PartDesign::Pad] Pad016
  BaseFeature = -> Pad015
  Direction = (0,-1,2e-16)
  Length = 1.6
  Length2 = 10
  Profile = -> Sketch122
  ReferenceAxis = -> Sketch122 [N_Axis]
  Refine = true
  Suppressed = false
  Type = 0
FEATURE [Sketcher::SketchObject] Sketch129
  ArcFitTolerance = 1e-06
  AttachmentSupport = -> [Pad016]
  ExternalGeometry = -> [Binder001]
  FullyConstrained = true
  MakeInternals = false
  MapMode = 5
  Placement = pos=(0,-3.6,0) rot=(1,0,0;1.5708rad)
  sketch-geometry (12):
    g0: LineSegment [constr] StartX=-192.176 StartY=-3.18451 StartZ=0 EndX=-181.223 EndY=20.303 EndZ=0
    g1: LineSegment [constr] StartX=-202.765 StartY=20.303 StartZ=0 EndX=-181.223 EndY=20.303 EndZ=0
    g2: LineSegment StartX=-202.765 StartY=20.303 StartZ=0 EndX=-181.223 EndY=20.303 EndZ=0
    g3: LineSegment StartX=-192.176 StartY=-3.18451 StartZ=0 EndX=-196.804 EndY=-13.1107 EndZ=0
    g4: ArcOfCircle CenterX=-207.583 CenterY=4 CenterZ=0 NormalX=0 NormalY=0 NormalZ=1 AngleXU=0 Radius=17 StartAngle=5.84685 EndAngle=7.56663
    g5: ArcOfEllipse CenterX=-181.223 CenterY=8.55923 CenterZ=0 NormalX=0 NormalY=0 NormalZ=1 MajorRadius=23.4779 MinorRadius=11.7437 AngleXU=2e-16 StartAngle=4.71239 EndAngle=7.85398
    g6: LineSegment [constr] StartX=-157.745 StartY=8.55923 StartZ=0 EndX=-204.701 EndY=8.55923 EndZ=0
    g7: LineSegment [constr] StartX=-181.223 StartY=20.303 StartZ=0 EndX=-181.223 EndY=-3.18451 EndZ=0
    g8: GeomPoint [constr] X=-160.894 Y=8.55923 Z=0
    g9: GeomPoint [constr] X=-201.553 Y=8.55923 Z=0
    g10: ArcOfCircle CenterX=-181.223 CenterY=-20.3763 CenterZ=0 NormalX=0 NormalY=0 NormalZ=1 AngleXU=0 Radius=17.1918 StartAngle=1.57079 EndAngle=2.70526
    g11: GeomPoint [constr] X=-181.223 Y=-3.18451 Z=0
  constraints (23):
    c: Coincident(g0,g-5)
    c: Coincident(g1,g-6)
    c: Horizontal(g1)
    c: Coincident(g1,g0)
    c: Parallel(g0,g-4)
    c: Coincident(g2,g1)
    c: Coincident(g2,g0)
    c: Coincident(g3,g0)
    c: Equal(g4,g-5)
    c: Coincident(g4,g1)
    c: Coincident(g4,g0)
    c: InternalAlignment(g6-g9 -> g5) x4
    c: Vertical(g5,g0)
    c: Horizontal(g6)
    c: Coincident(g5,g0)
    c: DistanceX(g6,g-3) = 10.1
    c: Tangent(g10,g3) = -1.5708
    c: PointOnObject(g11,g10)
    c: Tangent(g5,g10,g11) = 1.5708
    c: Coincident(g10,g5)
    c: Coincident(g11,g7)
    c: Parallel(g3,g-4)
    c: Horizontal(g5,g0)
FEATURE [Sketcher::SketchObject] Sketch130
  ArcFitTolerance = 1e-06
  AttachmentOffset = pos=(0,0,-1.6) rot=(0,0,1;0rad)
  AttachmentSupport = -> [Pad016]
  ExternalGeometry = -> [Binder001]
  FullyConstrained = true
  MakeInternals = false
  MapMode = 5
  Placement = pos=(0,-2,-4e-16) rot=(1,0,0;1.5708rad)
  sketch-geometry (12):
    g0: LineSegment [constr] StartX=-192.176 StartY=-3.18451 StartZ=0 EndX=-181.223 EndY=20.303 EndZ=0
    g1: LineSegment [constr] StartX=-202.765 StartY=20.303 StartZ=0 EndX=-181.223 EndY=20.303 EndZ=0
    g2: LineSegment StartX=-202.765 StartY=20.303 StartZ=0 EndX=-181.223 EndY=20.303 EndZ=0
    g3: LineSegment StartX=-192.176 StartY=-3.18451 StartZ=0 EndX=-193.827 EndY=-6.72678 EndZ=0
    g4: ArcOfCircle CenterX=-207.583 CenterY=4 CenterZ=0 NormalX=0 NormalY=0 NormalZ=1 AngleXU=0 Radius=17 StartAngle=5.84685 EndAngle=7.56663
    g5: ArcOfEllipse CenterX=-181.223 CenterY=10.803 CenterZ=0 NormalX=0 NormalY=0 NormalZ=1 MajorRadius=14.4779 MinorRadius=9.5 AngleXU=0 StartAngle=4.71239 EndAngle=7.85398
    g6: LineSegment [constr] StartX=-166.745 StartY=10.803 StartZ=0 EndX=-195.701 EndY=10.803 EndZ=0
    g7: LineSegment [constr] StartX=-181.223 StartY=20.303 StartZ=0 EndX=-181.223 EndY=1.30297 EndZ=0
    g8: GeomPoint [constr] X=-170.298 Y=10.803 Z=0
    g9: GeomPoint [constr] X=-192.148 Y=10.803 Z=0
    g10: ArcOfCircle CenterX=-181.223 CenterY=-12.6042 CenterZ=0 NormalX=0 NormalY=0 NormalZ=1 AngleXU=0 Radius=13.9072 StartAngle=1.5708 EndAngle=2.70526
    g11: GeomPoint [constr] X=-181.223 Y=1.30297 Z=0
  constraints (23):
    c: Coincident(g0,g-5)
    c: Coincident(g1,g-6)
    c: Horizontal(g1)
    c: Coincident(g1,g0)
    c: Parallel(g0,g-4)
    c: Coincident(g2,g1)
    c: Coincident(g2,g0)
    c: Coincident(g3,g0)
    c: Equal(g4,g-5)
    c: Coincident(g4,g1)
    c: Coincident(g4,g0)
    c: InternalAlignment(g6-g9 -> g5) x4
    c: Vertical(g5,g0)
    c: Horizontal(g6)
    c: Coincident(g5,g0)
    c: DistanceX(g6,g-3) = 19.1
    c: Tangent(g10,g3) = -1.5708
    c: PointOnObject(g11,g10)
    c: Tangent(g5,g10,g11) = 1.5708
    c: Coincident(g10,g5)
    c: Coincident(g11,g7)
    c: Parallel(g3,g-4)
    c: DistanceY(g5,g0) = 19
FEATURE [Part::Part2DObjectPython] Clone2D001  label="Sketch130 (2D)"  # Draft 2D object (typed FeaturePython)
  Fuse = false
  Objects = -> [Sketch130]
  Placement = pos=(0,-2,-4e-16) rot=(1,0,0;1.5708rad)
  Scale = (1,1,1)
FEATURE [Sketcher::SketchObject] Sketch131
  ArcFitTolerance = 1e-06
  AttachmentOffset = pos=(0,0,-3.5) rot=(0,0,1;0rad)
  AttachmentSupport = -> [Pad016]
  ExternalGeometry = -> [Binder001]
  FullyConstrained = true
  MakeInternals = false
  MapMode = 5
  Placement = pos=(0,-0.1,-8e-16) rot=(1,0,0;1.5708rad)
  sketch-geometry (1):
    g0: GeomPoint X=-197.47 Y=8.55923 Z=0
  constraints (1):
    c: Symmetric(g-6,g-4,g0)
FEATURE [Sketcher::SketchObject] Sketch132
  ArcFitTolerance = 1e-06
  AttachmentSupport = -> [Pad016]
  ExternalGeometry = -> [Binder001]
  FullyConstrained = true
  MakeInternals = false
  MapMode = 5
  Placement = pos=(0,-3.6,0) rot=(1,0,0;1.5708rad)
  sketch-geometry (3):
    g0: LineSegment [constr] StartX=-215.42 StartY=-53.0314 StartZ=0 EndX=-167.782 EndY=-53.0314 EndZ=0
    g1: Circle CenterX=-191.282 CenterY=-53.0314 CenterZ=0 NormalX=0 NormalY=0 NormalZ=1 AngleXU=0 Radius=11.5
    g2: Circle CenterX=-191.282 CenterY=-53.0314 CenterZ=0 NormalX=0 NormalY=0 NormalZ=1 AngleXU=0 Radius=10.7
  constraints (8):
    c: Coincident(g0,g-3)
    c: PointOnObject(g0,g-4)
    c: Horizontal(g0)
    c: Diameter(g1) = 23
    c: PointOnObject(g1,g0)
    c: DistanceX(g1,g0) = 23.5
    c: Diameter(g2) = 21.4
    c: Coincident(g2,g1)
FEATURE [Part::Part2DObjectPython] ShapeString  # Draft 2D object (typed FeaturePython)
  FontFile = <path>
  Fuse = false
  Justification = 6
  JustificationReference = 0
  KeepLeftMargin = false
  MakeFace = true
  ObliqueAngle = 0
  Placement = pos=(-199,-3.6,-57.5) rot=(1,0,0;1.5708rad)
  ScaleToSize = true
  Size = 10
  String = AS
  Tracking = 0
FEATURE [Sketcher::SketchObject] Sketch133
  ArcFitTolerance = 1e-06
  AttachmentSupport = -> [Binder]
  ExternalGeometry = -> [Binder]
  FullyConstrained = true
  MakeInternals = false
  MapMode = 5
  Placement = pos=(0,9e-16,0) rot=(0,0.707107,0.707107;3.14159rad)
  sketch-geometry (30):
    g0: LineSegment StartX=0 StartY=39.2 StartZ=0 EndX=0 EndY=3.2 EndZ=0
    g1: LineSegment StartX=0 StartY=3.2 StartZ=0 EndX=82.8 EndY=3.2 EndZ=0
    g2: LineSegment StartX=82.8 StartY=3.2 StartZ=0 EndX=82.8 EndY=6.2 EndZ=0
    g3: LineSegment StartX=82.8 StartY=6.2 StartZ=0 EndX=91.752 EndY=6.2 EndZ=0
    g4: LineSegment StartX=0 StartY=39.2 StartZ=0 EndX=195.887 EndY=39.2 EndZ=0
    g5: LineSegment StartX=195.887 StartY=39.2 StartZ=0 EndX=202.765 EndY=20.303 EndZ=0
    g6: LineSegment StartX=192.333 StartY=24.9893 StartZ=0 EndX=196.467 EndY=26.4942 EndZ=0
    g7: LineSegment StartX=196.467 StartY=26.4942 StartZ=0 EndX=194.073 EndY=33.0721 EndZ=0
    g8: LineSegment StartX=194.073 StartY=33.0721 StartZ=0 EndX=189.939 EndY=31.5672 EndZ=0
    g9: LineSegment StartX=189.939 StartY=31.5672 StartZ=0 EndX=192.333 EndY=24.9893 EndZ=0
    g10: ArcOfCircle CenterX=107.6 CenterY=4 CenterZ=0 NormalX=0 NormalY=0 NormalZ=1 AngleXU=0 Radius=16 StartAngle=1.5708 EndAngle=3.00366
    g11: LineSegment StartX=107.6 StartY=20 StartZ=0 EndX=132.428 EndY=20 EndZ=0
    g12: ArcOfCircle [constr] CenterX=132.428 CenterY=4 CenterZ=0 NormalX=0 NormalY=0 NormalZ=1 AngleXU=0 Radius=16 StartAngle=0.314159 EndAngle=1.5708
    g13: LineSegment StartX=147.645 StartY=8.94427 StartZ=0 EndX=176.685 EndY=-80.4316 EndZ=0
    g14: LineSegment StartX=176.685 StartY=-80.4316 StartZ=0 EndX=215.932 EndY=-80.4316 EndZ=0
    g15: ArcOfCircle CenterX=207.583 CenterY=4 CenterZ=0 NormalX=0 NormalY=0 NormalZ=1 AngleXU=0 Radius=17 StartAngle=1.85815 EndAngle=3.57792
    g16: ArcOfCircle CenterX=184.801 CenterY=-67.3089 CenterZ=0 NormalX=0 NormalY=0 NormalZ=1 AngleXU=0 Radius=33.7833 StartAngle=5.88425 EndAngle=6.71952
    g17: LineSegment StartX=192.176 StartY=-3.18451 StartZ=0 EndX=215.42 EndY=-53.0314 EndZ=0
    g18: Circle CenterX=5.6 CenterY=34.8 CenterZ=0 NormalX=0 NormalY=0 NormalZ=1 AngleXU=0 Radius=1.8
    g19: Circle CenterX=5.6 CenterY=7.6 CenterZ=0 NormalX=0 NormalY=0 NormalZ=1 AngleXU=0 Radius=1.8
    g20: Circle CenterX=78.51 CenterY=34.8 CenterZ=0 NormalX=0 NormalY=0 NormalZ=1 AngleXU=0 Radius=1.8
    g21: Circle CenterX=78.51 CenterY=7.6 CenterZ=0 NormalX=0 NormalY=0 NormalZ=1 AngleXU=0 Radius=1.8
    g22: Circle CenterX=184.08 CenterY=34.8 CenterZ=0 NormalX=0 NormalY=0 NormalZ=1 AngleXU=0 Radius=1.8
    g23: Circle CenterX=179.305 CenterY=-76.8316 CenterZ=0 NormalX=0 NormalY=0 NormalZ=1 AngleXU=0 Radius=1.8
    g24: Circle CenterX=213.443 CenterY=-76.8316 CenterZ=0 NormalX=0 NormalY=0 NormalZ=1 AngleXU=0 Radius=1.8
    g25: Circle CenterX=19 CenterY=21.2 CenterZ=0 NormalX=0 NormalY=0 NormalZ=1 AngleXU=0 Radius=6.3
    g26: Circle CenterX=42 CenterY=21.2 CenterZ=0 NormalX=0 NormalY=0 NormalZ=1 AngleXU=0 Radius=6.3
    g27: Circle CenterX=65 CenterY=21.2 CenterZ=0 NormalX=0 NormalY=0 NormalZ=1 AngleXU=0 Radius=6.3
    g28: LineSegment StartX=132.428 StartY=20 StartZ=0 EndX=144.053 EndY=20 EndZ=0
    g29: LineSegment StartX=147.645 StartY=8.94427 StartZ=0 EndX=144.053 EndY=20 EndZ=0
  constraints (65):
    c: Coincident(g0,g-4)
    c: Coincident(g0,g-5)
    c: Coincident(g1,g0)
    c: Coincident(g1,g-6)
    c: Coincident(g2,g1)
    c: Coincident(g2,g-7)
    c: Coincident(g3,g2)
    c: Coincident(g3,g-8)
    c: Coincident(g4,g0)
    c: Coincident(g4,g-16)
    c: Coincident(g5,g4)
    c: Coincident(g5,g-16)
    c: Coincident(g6,g-20)
    c: Coincident(g6,g-21)
    c: Coincident(g7,g6)
    c: Coincident(g7,g-23)
    c: Coincident(g8,g7)
    c: Coincident(g8,g-22)
    c: Coincident(g9,g8)
    c: Coincident(g9,g6)
    c: Equal(g10,g-8)
    c: Coincident(g10,g3)
    c: Coincident(g10,g-9)
    c: Coincident(g11,g10)
    c: Coincident(g11,g-10)
    c: Equal(g12,g-10)
    c: Coincident(g12,g11)
    c: Coincident(g12,g-11)
    c: Coincident(g13,g12)
    c: Coincident(g13,g-12)
    c: Coincident(g14,g13)
    c: Coincident(g14,g-13)
    c: Equal(g15,g-15)
    c: Coincident(g15,g5)
    c: Coincident(g15,g-15)
    c: Equal(g16,g-13)
    c: Coincident(g16,g14)
    c: Coincident(g16,g-14)
    c: Coincident(g17,g15)
    c: Coincident(g17,g16)
    c: Equal(g18,g-28)
    c: Equal(g19,g-29)
    c: Equal(g20,g-26)
    c: Equal(g21,g-27)
    c: Equal(g22,g-17)
    c: Equal(g24,g-25)
    c: Equal(g23,g-24)
    c: Coincident(g23,g-24)
    c: Coincident(g24,g-25)
    c: Coincident(g22,g-17)
    c: Coincident(g20,g-26)
    c: Coincident(g21,g-27)
    c: Coincident(g18,g-28)
    c: Coincident(g19,g-29)
    c: Equal(g25,g-30)
    c: Equal(g26,g-31)
    c: Equal(g27,g-32)
    c: Coincident(g25,g-30)
    c: Coincident(g26,g-31)
    c: Coincident(g27,g-32)
    c: Parallel(g28,g11)
    c: Parallel(g29,g13)
    c: Coincident(g28,g11)
    c: Coincident(g29,g12)
    c: Coincident(g29,g28)
FEATURE [PartDesign::Pad] Pad019
  Direction = (0,1,-2e-16)
  Length = 2
  Length2 = 10
  Profile = -> Sketch133
  ReferenceAxis = -> Sketch133 [N_Axis]
  Refine = true
  Suppressed = false
  Type = 0
FEATURE [Sketcher::SketchObject] Sketch091  label="Sketch091 - forma anteriore"
  ArcFitTolerance = 1e-06
  AttachmentSupport = -> [Pad019]
  ExternalGeometry = -> [Binder]
  FullyConstrained = true
  MakeInternals = false
  MapMode = 5
  Placement = pos=(0,2,0) rot=(0,0.707107,0.707107;3.14159rad)
  sketch-geometry (12):
    g0: Circle CenterX=5.6 CenterY=34.8 CenterZ=0 NormalX=0 NormalY=0 NormalZ=1 AngleXU=0 Radius=1.8
    g1: Circle CenterX=5.6 CenterY=7.6 CenterZ=0 NormalX=0 NormalY=0 NormalZ=1 AngleXU=0 Radius=1.8
    g2: Circle CenterX=78.51 CenterY=34.8 CenterZ=0 NormalX=0 NormalY=0 NormalZ=1 AngleXU=0 Radius=1.8
    g3: Circle CenterX=78.51 CenterY=7.6 CenterZ=0 NormalX=0 NormalY=0 NormalZ=1 AngleXU=0 Radius=1.8
    g4: LineSegment StartX=0 StartY=39.2 StartZ=0 EndX=0 EndY=3.2 EndZ=0
    g5: LineSegment StartX=0 StartY=3.2 StartZ=0 EndX=82.8 EndY=3.2 EndZ=0
    g6: LineSegment StartX=82.8 StartY=3.2 StartZ=0 EndX=82.8 EndY=39.2 EndZ=0
    g7: LineSegment StartX=82.8 StartY=39.2 StartZ=0 EndX=0 EndY=39.2 EndZ=0
    g8: ArcOfCircle CenterX=19 CenterY=21.2 CenterZ=0 NormalX=0 NormalY=0 NormalZ=1 AngleXU=0 Radius=10 StartAngle=1.5708 EndAngle=4.71239
    g9: ArcOfCircle CenterX=65 CenterY=21.2 CenterZ=0 NormalX=0 NormalY=0 NormalZ=1 AngleXU=0 Radius=10 StartAngle=4.71239 EndAngle=7.85398
    g10: LineSegment StartX=19 StartY=31.2 StartZ=0 EndX=65 EndY=31.2 EndZ=0
    g11: LineSegment StartX=19 StartY=11.2 StartZ=0 EndX=65 EndY=11.2 EndZ=0
  constraints (25):
    c: Equal(g2,g-7)
    c: Equal(g3,g-8)
    c: Equal(g1,g-13)
    c: Equal(g0,g-12)
    c: Coincident(g0,g-12)
    c: Coincident(g1,g-13)
    c: Coincident(g3,g-8)
    c: Coincident(g2,g-7)
    c: Coincident(g4,g-4)
    c: Coincident(g4,g-5)
    c: Coincident(g5,g4)
    c: Coincident(g5,g-6)
    c: Coincident(g6,g5)
    c: PointOnObject(g6,g-3)
    c: Vertical(g6)
    c: Coincident(g7,g6)
    c: Coincident(g7,g4)
    c: Tangent(g8,g10) = 1.5708
    c: Tangent(g8,g11) = -1.5708
    c: Tangent(g9,g10) = 1.5708
    c: Tangent(g9,g11) = -1.5708
    c: Equal(g8,g9)
    c: Radius(g8) = 10
    c: Coincident(g8,g-11)
    c: Coincident(g9,g-9)
FEATURE [Sketcher::SketchObject] Sketch093  label="Sketch093 - scavi interni pulsanti"
  ArcFitTolerance = 1e-06
  AttachmentSupport = -> [Pad019]
  ExternalGeometry = -> [Binder]
  FullyConstrained = true
  MakeInternals = false
  MapMode = 5
  Placement = pos=(0,1.8e-15,0) rot=(1,0,0;1.5708rad)
  sketch-geometry (3):
    g0: Circle CenterX=-65 CenterY=21.2 CenterZ=0 NormalX=0 NormalY=0 NormalZ=1 AngleXU=0 Radius=7.3
    g1: Circle CenterX=-42 CenterY=21.2 CenterZ=0 NormalX=0 NormalY=0 NormalZ=1 AngleXU=0 Radius=7.3
    g2: Circle CenterX=-19 CenterY=21.2 CenterZ=0 NormalX=0 NormalY=0 NormalZ=1 AngleXU=0 Radius=7.3
  constraints (6):
    c: Coincident(g0,g-3)
    c: Coincident(g1,g-4)
    c: Coincident(g2,g-5)
    c: Diameter(g0) = 14.6
    c: Diameter(g1) = 14.6
    c: Diameter(g2) = 14.6
FEATURE [Sketcher::SketchObject] Sketch094  label="Sketch094 - forma centrale"
  ArcFitTolerance = 1e-06
  AttachmentSupport = -> [Pad019]
  ExternalGeometry = -> [Binder]
  FullyConstrained = true
  MakeInternals = false
  MapMode = 5
  Placement = pos=(0,2,0) rot=(0,0.707107,0.707107;3.14159rad)
  sketch-geometry (4):
    g0: LineSegment StartX=137.815 StartY=39.2 StartZ=0 EndX=142.655 EndY=24.303 EndZ=0
    g1: LineSegment StartX=110.815 StartY=24.303 StartZ=0 EndX=142.655 EndY=24.303 EndZ=0
    g2: LineSegment StartX=137.815 StartY=39.2 StartZ=0 EndX=110.815 EndY=39.2 EndZ=0
    g3: ArcOfCircle CenterX=92.2534 CenterY=31.7515 CenterZ=0 NormalX=0 NormalY=0 NormalZ=1 AngleXU=0 Radius=20 StartAngle=5.90156 EndAngle=6.66481
  constraints (12):
    c: PointOnObject(g0,g-3)
    c: Tangent(g0,g-5)
    c: Horizontal(g1)
    c: Coincident(g1,g0)
    c: Coincident(g2,g0)
    c: PointOnObject(g2,g-3)
    c: DistanceX(g2,g2) = 27
    c: Vertical(g1,g2)
    c: Coincident(g3,g2)
    c: Radius(g3) = 20
    c: Coincident(g3,g1)
    c: DistanceY(g-6,g0) = 4
FEATURE [Sketcher::SketchObject] Sketch095  label="Sketch095 - forma posteriore"
  ArcFitTolerance = 1e-06
  AttachmentSupport = -> [Pad019]
  ExternalGeometry = -> [Binder]
  FullyConstrained = true
  MakeInternals = false
  MapMode = 5
  Placement = pos=(0,2,0) rot=(0,0.707107,0.707107;3.14159rad)
  sketch-geometry (15):
    g0: LineSegment StartX=137.815 StartY=39.2 StartZ=0 EndX=143.955 EndY=20.303 EndZ=0
    g1: LineSegment StartX=143.955 StartY=20.303 StartZ=0 EndX=190.141 EndY=20.303 EndZ=0
    g2: ArcOfCircle CenterX=184.08 CenterY=34.8 CenterZ=0 NormalX=0 NormalY=0 NormalZ=1 AngleXU=0 Radius=3.5 StartAngle=3.49066 EndAngle=4.71239
    g3: LineSegment StartX=180.791 StartY=33.6029 StartZ=0 EndX=178.754 EndY=39.2 EndZ=0
    g4: LineSegment StartX=184.08 StartY=31.3 StartZ=0 EndX=186.139 EndY=31.3 EndZ=0
    g5: LineSegment StartX=190.141 StartY=20.303 StartZ=0 EndX=186.139 EndY=31.3 EndZ=0
    g6: LineSegment StartX=137.815 StartY=39.2 StartZ=0 EndX=156.815 EndY=39.2 EndZ=0
    g7: LineSegment StartX=178.754 StartY=39.2 StartZ=0 EndX=168.815 EndY=39.2 EndZ=0
    g8: LineSegment StartX=156.815 StartY=31.2 StartZ=0 EndX=168.815 EndY=31.2 EndZ=0
    g9: ArcOfCircle CenterX=176.411 CenterY=35.2 CenterZ=0 NormalX=0 NormalY=0 NormalZ=1 AngleXU=0 Radius=20 StartAngle=2.94023 EndAngle=3.34295
    g10: ArcOfCircle CenterX=188.411 CenterY=35.2 CenterZ=0 NormalX=0 NormalY=0 NormalZ=1 AngleXU=0 Radius=20 StartAngle=2.94023 EndAngle=3.34295
    g11: LineSegment StartX=157.815 StartY=39.2 StartZ=0 EndX=167.815 EndY=39.2 EndZ=0
    g12: LineSegment StartX=157.436 StartY=36.2 StartZ=0 EndX=167.436 EndY=36.2 EndZ=0
    g13: ArcOfCircle CenterX=177.411 CenterY=35.2 CenterZ=0 NormalX=0 NormalY=0 NormalZ=1 AngleXU=0 Radius=20 StartAngle=2.94023 EndAngle=3.09157
    g14: ArcOfCircle CenterX=187.411 CenterY=35.2 CenterZ=0 NormalX=0 NormalY=0 NormalZ=1 AngleXU=0 Radius=20 StartAngle=2.94023 EndAngle=3.09157
  constraints (46):
    c: PointOnObject(g0,g-3)
    c: Tangent(g0,g-6)
    c: Coincident(g1,g0)
    c: Horizontal(g1)
    c: Radius(g2) = 3.5
    c: Coincident(g2,g-5)
    c: PointOnObject(g3,g-3)
    c: Parallel(g3,g-4)
    c: Tangent(g3,g2) = 1.5708
    c: Horizontal(g4)
    c: Tangent(g4,g2) = -1.5708
    c: Coincident(g5,g1)
    c: Parallel(g5,g-4)
    c: Coincident(g5,g4)
    c: DistanceX(g4,g-8) = 3.8
    c: Coincident(g6,g0)
    c: PointOnObject(g6,g-3)
    c: Coincident(g7,g3)
    c: PointOnObject(g7,g-3)
    c: Horizontal(g8)
    c: DistanceX(g6,g7) = 12
    c: Vertical(g8,g6)
    c: Vertical(g7,g8)
    c: DistanceY(g8,g6) = 8
    c: Coincident(g9,g8)
    c: Coincident(g9,g6)
    c: Coincident(g10,g7)
    c: Coincident(g10,g8)
    c: Radius(g9) = 20
    c: Radius(g10) = 20
    c: PointOnObject(g11,g-3)
    c: PointOnObject(g11,g-3)
    c: DistanceX(g11,g11) = 10
    c: DistanceX(g6,g11) = 1
    c: Horizontal(g12)
    c: Equal(g12,g11)
    c: DistanceY(g12,g11) = 3
    c: Coincident(g13,g11)
    c: Coincident(g13,g12)
    c: Radius(g13) = 20
    c: Coincident(g14,g11)
    c: Coincident(g14,g12)
    c: Radius(g14) = 20
    c: DistanceX(g0,g6) = 19
    c: Horizontal(g9,g13)
    c: Horizontal(g0,g-4)
FEATURE [Sketcher::SketchObject] Sketch096  label="Sketch096 - forma impugnatura"
  ArcFitTolerance = 1e-06
  AttachmentSupport = -> [Pad019]
  ExternalGeometry = -> [Binder]
  FullyConstrained = true
  MakeInternals = false
  MapMode = 5
  Placement = pos=(0,2,0) rot=(0,0.707107,0.707107;3.14159rad)
  sketch-geometry (8):
    g0: LineSegment StartX=176.685 StartY=-80.4316 StartZ=0 EndX=143.955 EndY=20.303 EndZ=0
    g1: LineSegment StartX=176.685 StartY=-80.4316 StartZ=0 EndX=215.932 EndY=-80.4316 EndZ=0
    g2: Circle CenterX=179.305 CenterY=-76.8316 CenterZ=0 NormalX=0 NormalY=0 NormalZ=1 AngleXU=0 Radius=3
    g3: Circle CenterX=213.443 CenterY=-76.8316 CenterZ=0 NormalX=0 NormalY=0 NormalZ=1 AngleXU=0 Radius=3
    g4: LineSegment StartX=143.955 StartY=20.303 StartZ=0 EndX=202.765 EndY=20.303 EndZ=0
    g5: LineSegment StartX=215.42 StartY=-53.0314 StartZ=0 EndX=192.176 EndY=-3.18451 EndZ=0
    g6: ArcOfCircle CenterX=184.801 CenterY=-67.3089 CenterZ=0 NormalX=0 NormalY=0 NormalZ=1 AngleXU=0 Radius=33.7833 StartAngle=5.88425 EndAngle=6.71952
    g7: ArcOfCircle CenterX=207.583 CenterY=4 CenterZ=0 NormalX=0 NormalY=0 NormalZ=1 AngleXU=0 Radius=17 StartAngle=1.85815 EndAngle=3.57792
  constraints (19):
    c: Coincident(g0,g-4)
    c: PointOnObject(g0,g-3)
    c: Horizontal(g0,g-7)
    c: Coincident(g1,g0)
    c: Coincident(g1,g-5)
    c: Diameter(g2) = 6
    c: Diameter(g3) = 6
    c: Coincident(g2,g-9)
    c: Coincident(g3,g-10)
    c: Coincident(g4,g0)
    c: Coincident(g5,g-6)
    c: Coincident(g6,g1)
    c: Coincident(g6,g5)
    c: Equal(g-5,g6)
    c: Coincident(g5,g-7)
    c: Coincident(g4,g-7)
    c: Tangent(g7,g-7)
    c: Coincident(g7,g4)
    c: Coincident(g7,g5)
FEATURE [Sketcher::SketchObject] Sketch097
  ArcFitTolerance = 1e-06
  AttachmentSupport = -> [Pad019]
  ExternalGeometry = -> [Binder]
  FullyConstrained = true
  MakeInternals = false
  MapMode = 5
  Placement = pos=(0,2,0) rot=(0,0.707107,0.707107;3.14159rad)
  sketch-geometry (4):
    g0: LineSegment StartX=90 StartY=36.8 StartZ=0 EndX=108 EndY=36.8 EndZ=0
    g1: LineSegment StartX=108 StartY=36.8 StartZ=0 EndX=108 EndY=26.8 EndZ=0
    g2: LineSegment StartX=108 StartY=26.8 StartZ=0 EndX=90 EndY=26.8 EndZ=0
    g3: ArcOfCircle CenterX=94 CenterY=31.8 CenterZ=0 NormalX=0 NormalY=0 NormalZ=1 AngleXU=0 Radius=6.40312 StartAngle=2.24554 EndAngle=4.03765
  constraints (13):
    c: Horizontal(g0)
    c: Coincident(g1,g0)
    c: Vertical(g1)
    c: DistanceX(g0,g0) = 18
    c: DistanceY(g1,g1) = 10
    c: Coincident(g2,g1)
    c: Horizontal(g2)
    c: Equal(g2,g0)
    c: DistanceY(g0,g-3) = 2.4
    c: Coincident(g3,g0)
    c: Coincident(g3,g2)
    c: DistanceX(g2,g3) = 4
    c: DistanceX(g-3,g0) = 90
FEATURE [PartDesign::Chamfer] Chamfer015
  Angle = 45
  Base = -> Pad019 [Edge19,Edge22,Edge79]
  BaseFeature = -> Pad019
  ChamferType = 0
  FlipDirection = false
  Refine = true
  Size = 1.9
  Size2 = 1
  SupportTransform = false
  Suppressed = false
  UseAllEdges = false
FEATURE [PartDesign::Pocket] Pocket002
  BaseFeature = -> Chamfer015
  Direction = (0,1,-2e-16)
  Length = 1.2
  Length2 = 5
  Profile = -> Sketch093
  ReferenceAxis = -> Sketch093 [N_Axis]
  Refine = true
  Suppressed = false
  Type = 0
FEATURE [PartDesign::Pad] Pad005
  BaseFeature = -> Pocket002
  Direction = (0,1,-2e-16)
  Length = 1.6
  Length2 = 10
  Profile = -> Sketch091
  ReferenceAxis = -> Sketch091 [N_Axis]
  Refine = true
  Suppressed = false
  Type = 0
FEATURE [Sketcher::SketchObject] Sketch092  label="Sketch092 - scavi per viti anteriori"
  ArcFitTolerance = 1e-06
  AttachmentSupport = -> [Pad005]
  ExternalGeometry = -> [Binder]
  FullyConstrained = true
  MakeInternals = false
  MapMode = 5
  Placement = pos=(0,3.6,0) rot=(0,0.707107,0.707107;3.14159rad)
  sketch-geometry (20):
    g0: ArcOfCircle CenterX=5.6 CenterY=7.6 CenterZ=0 NormalX=0 NormalY=0 NormalZ=1 AngleXU=0 Radius=3.5 StartAngle=0 EndAngle=1.5708
    g1: ArcOfCircle CenterX=5.6 CenterY=34.8 CenterZ=0 NormalX=0 NormalY=0 NormalZ=1 AngleXU=0 Radius=3.5 StartAngle=4.71239 EndAngle=6.28319
    g2: ArcOfCircle CenterX=78.51 CenterY=34.8 CenterZ=0 NormalX=0 NormalY=0 NormalZ=1 AngleXU=0 Radius=3.5 StartAngle=3.14159 EndAngle=4.71239
    g3: ArcOfCircle CenterX=78.51 CenterY=7.6 CenterZ=0 NormalX=0 NormalY=0 NormalZ=1 AngleXU=0 Radius=3.5 StartAngle=1.5708 EndAngle=3.14159
    g4: LineSegment StartX=0 StartY=3.2 StartZ=0 EndX=0 EndY=11.1 EndZ=0
    g5: LineSegment StartX=0 StartY=11.1 StartZ=0 EndX=5.6 EndY=11.1 EndZ=0
    g6: LineSegment StartX=0 StartY=3.2 StartZ=0 EndX=9.1 EndY=3.2 EndZ=0
    g7: LineSegment StartX=9.1 StartY=3.2 StartZ=0 EndX=9.1 EndY=7.6 EndZ=0
    g8: LineSegment StartX=0 StartY=39.2 StartZ=0 EndX=0 EndY=31.3 EndZ=0
    g9: LineSegment StartX=0 StartY=31.3 StartZ=0 EndX=5.6 EndY=31.3 EndZ=0
    g10: LineSegment StartX=0 StartY=39.2 StartZ=0 EndX=9.1 EndY=39.2 EndZ=0
    g11: LineSegment StartX=9.1 StartY=39.2 StartZ=0 EndX=9.1 EndY=34.8 EndZ=0
    g12: LineSegment StartX=82.8 StartY=39.2 StartZ=0 EndX=75.01 EndY=39.2 EndZ=0
    g13: LineSegment StartX=82.8 StartY=39.2 StartZ=0 EndX=82.8 EndY=31.3 EndZ=0
    g14: LineSegment StartX=82.8 StartY=31.3 StartZ=0 EndX=78.51 EndY=31.3 EndZ=0
    g15: LineSegment StartX=82.8 StartY=3.2 StartZ=0 EndX=75.01 EndY=3.2 EndZ=0
    g16: LineSegment StartX=75.01 StartY=3.2 StartZ=0 EndX=75.01 EndY=7.6 EndZ=0
    g17: LineSegment StartX=82.8 StartY=3.2 StartZ=0 EndX=82.8 EndY=11.1 EndZ=0
    g18: LineSegment StartX=82.8 StartY=11.1 StartZ=0 EndX=78.51 EndY=11.1 EndZ=0
    g19: LineSegment StartX=75.01 StartY=39.2 StartZ=0 EndX=75.01 EndY=34.8 EndZ=0
  constraints (48):
    c: Radius(g0) = 3.5
    c: Coincident(g0,g-10)
    c: Radius(g1) = 3.5
    c: Coincident(g1,g-9)
    c: Radius(g2) = 3.5
    c: Coincident(g2,g-8)
    c: Radius(g3) = 3.5
    c: Coincident(g3,g-7)
    c: Coincident(g4,g-5)
    c: PointOnObject(g4,g-4)
    c: Coincident(g5,g4)
    c: Horizontal(g5)
    c: Coincident(g6,g4)
    c: PointOnObject(g6,g-5)
    c: Coincident(g7,g6)
    c: Vertical(g7)
    c: Coincident(g8,g-4)
    c: PointOnObject(g8,g-4)
    c: Coincident(g9,g8)
    c: Horizontal(g9)
    c: Coincident(g10,g8)
    c: PointOnObject(g10,g-3)
    c: Coincident(g11,g10)
    c: Vertical(g11)
    c: PointOnObject(g12,g-3)
    c: PointOnObject(g12,g-3)
    c: Coincident(g13,g12)
    c: Vertical(g13)
    c: Coincident(g14,g13)
    c: Horizontal(g14)
    c: Coincident(g15,g-6)
    c: PointOnObject(g15,g-5)
    c: Coincident(g16,g15)
    c: Vertical(g16)
    c: Coincident(g17,g15)
    c: Coincident(g18,g17)
    c: Horizontal(g18)
    c: Tangent(g3,g18) = -1.5708
    c: Tangent(g16,g3) = 1.5708
    c: Coincident(g19,g12)
    c: Vertical(g19)
    c: Tangent(g2,g19) = -1.5708
    c: Tangent(g2,g14) = 1.5708
    c: Tangent(g0,g7) = -1.5708
    c: Tangent(g0,g5) = 1.5708
    c: Tangent(g9,g1) = -1.5708
    c: Tangent(g1,g11) = 1.5708
    c: Tangent(g17,g13)
FEATURE [PartDesign::Pocket] Pocket001
  BaseFeature = -> Pad005
  Direction = (0,-1,2e-16)
  Length = 1.6
  Length2 = 5
  Profile = -> Sketch092
  ReferenceAxis = -> Sketch092 [N_Axis]
  Refine = true
  Suppressed = false
  Type = 0
FEATURE [PartDesign::Pad] Pad006
  BaseFeature = -> Pocket001
  Direction = (0,1,-2e-16)
  Length = 0.8
  Length2 = 10
  Profile = -> Sketch094
  ReferenceAxis = -> Sketch094 [N_Axis]
  Refine = true
  Suppressed = false
  Type = 0
FEATURE [PartDesign::Pad] Pad007
  BaseFeature = -> Pad006
  Direction = (0,1,-2e-16)
  Length = 2
  Length2 = 10
  Profile = -> Sketch095
  ReferenceAxis = -> Sketch095 [N_Axis]
  Refine = true
  Suppressed = false
  Type = 0
FEATURE [PartDesign::Pad] Pad008  label="Pad008 - forma impugnatura"
  BaseFeature = -> Pad007
  Direction = (0,1,-2e-16)
  Length = 1.6
  Length2 = 10
  Profile = -> Sketch096
  ReferenceAxis = -> Sketch096 [N_Axis]
  Refine = true
  Suppressed = false
  Type = 0
FEATURE [PartDesign::Pad] Pad009
  BaseFeature = -> Pad008
  Direction = (0,1,-2e-16)
  Length = 1.6
  Length2 = 10
  Profile = -> Sketch097
  ReferenceAxis = -> Sketch097 [N_Axis]
  Refine = true
  Suppressed = false
  Type = 0
FEATURE [Sketcher::SketchObject] Sketch098
  ArcFitTolerance = 1e-06
  AttachmentSupport = -> [Pad006]
  ExternalGeometry = -> [Binder]
  FullyConstrained = true
  MakeInternals = false
  MapMode = 5
  Placement = pos=(0,2.8,-7e-16) rot=(0,0.707107,0.707107;3.14159rad)
  sketch-geometry (4):
    g0: LineSegment StartX=118 StartY=39.2 StartZ=0 EndX=129 EndY=39.2 EndZ=0
    g1: LineSegment StartX=120.599 StartY=31.2 StartZ=0 EndX=131.599 EndY=31.2 EndZ=0
    g2: LineSegment StartX=129 StartY=39.2 StartZ=0 EndX=131.599 EndY=31.2 EndZ=0
    g3: LineSegment StartX=118 StartY=39.2 StartZ=0 EndX=120.599 EndY=31.2 EndZ=0
  constraints (12):
    c: PointOnObject(g0,g-3)
    c: PointOnObject(g0,g-3)
    c: DistanceX(g0,g0) = 11
    c: Horizontal(g1)
    c: Equal(g1,g0)
    c: Coincident(g2,g0)
    c: Coincident(g3,g0)
    c: Parallel(g-4,g2)
    c: Coincident(g1,g2)
    c: Coincident(g1,g3)
    c: DistanceY(g1,g0) = 8
    c: DistanceX(g-3,g0) = 118
FEATURE [Sketcher::SketchObject] Sketch099
  ArcFitTolerance = 1e-06
  AttachmentSupport = -> [Pad008]
  ExternalGeometry = -> [Binder]
  FullyConstrained = true
  MakeInternals = false
  MapMode = 5
  Placement = pos=(0,3.6,0) rot=(0,0.707107,0.707107;3.14159rad)
  sketch-geometry (13):
    g0: LineSegment StartX=192.176 StartY=-3.18451 StartZ=0 EndX=196.804 EndY=-13.1108 EndZ=0
    g1: LineSegment [constr] StartX=202.765 StartY=20.303 StartZ=0 EndX=181.223 EndY=20.303 EndZ=0
    g2: LineSegment [constr] StartX=181.223 StartY=20.303 StartZ=0 EndX=181.223 EndY=-3.18451 EndZ=0
    g3: ArcOfCircle CenterX=181.223 CenterY=-20.3764 CenterZ=0 NormalX=0 NormalY=0 NormalZ=1 AngleXU=0 Radius=17.1918 StartAngle=0.436332 EndAngle=1.57079
    g4: ArcOfEllipse CenterX=181.223 CenterY=8.55923 CenterZ=0 NormalX=0 NormalY=0 NormalZ=1 MajorRadius=23.4779 MinorRadius=11.7437 AngleXU=0 StartAngle=1.5708 EndAngle=4.71239
    g5: LineSegment [constr] StartX=204.701 StartY=8.55923 StartZ=0 EndX=157.745 EndY=8.55923 EndZ=0
    g6: LineSegment [constr] StartX=181.223 StartY=20.303 StartZ=0 EndX=181.223 EndY=-3.18451 EndZ=0
    g7: GeomPoint [constr] X=201.553 Y=8.55923 Z=0
    g8: GeomPoint [constr] X=160.894 Y=8.55923 Z=0
    g9: GeomPoint [constr] X=181.223 Y=-3.18451 Z=0
    g10: LineSegment StartX=181.223 StartY=20.303 StartZ=0 EndX=202.765 EndY=20.303 EndZ=0
    g11: ArcOfCircle CenterX=207.583 CenterY=4 CenterZ=0 NormalX=0 NormalY=0 NormalZ=1 AngleXU=0 Radius=17 StartAngle=1.85815 EndAngle=3.57792
    g12: LineSegment [constr] StartX=172.411 StartY=39.2 StartZ=0 EndX=192.176 EndY=-3.18451 EndZ=0
  constraints (27):
    c: Coincident(g1,g-7)
    c: Horizontal(g1)
    c: Coincident(g2,g1)
    c: Vertical(g2)
    c: Horizontal(g2,g0)
    c: Coincident(g3,g0)
    c: Coincident(g3,g2)
    c: InternalAlignment(g5-g8 -> g4) x4
    c: Horizontal(g5)
    c: PointOnObject(g4,g2)
    c: Coincident(g4,g1)
    c: DistanceX(g-3,g5) = 10.1
    c: Coincident(g4,g2)
    c: Tangent(g3,g-5)
    c: PointOnObject(g9,g4)
    c: PointOnObject(g9,g3)
    c: Tangent(g4,g3,g9) = 1.5708
    c: Coincident(g10,g1)
    c: Coincident(g10,g1)
    c: Equal(g11,g-4)
    c: Coincident(g11,g1)
    c: Coincident(g11,g0)
    c: PointOnObject(g12,g-6)
    c: PointOnObject(g1,g12)
    c: Tangent(g12,g-5) = -1.5708
    c: Tangent(g0,g-5) = -1.5708
    c: Horizontal(g9,g12)
FEATURE [Sketcher::SketchObject] Sketch106  label="Sketch106 - smusso impuniatura interno"
  ArcFitTolerance = 1e-06
  AttachmentSupport = -> [Pad008]
  ExternalGeometry = -> [Pad008]
  FullyConstrained = true
  MakeInternals = false
  MapMode = 5
  Placement = pos=(0,-1.585e-13,-80.4316) rot=(1,0,0;3.14159rad)
  sketch-geometry (9):
    g0: LineSegment StartX=-176.685 StartY=-3.6 StartZ=0 EndX=-176.685 EndY=3.277e-13 EndZ=0
    g1: LineSegment [constr] StartX=-176.685 StartY=-7.37e-14 StartZ=0 EndX=-176.685 EndY=3.279e-13 EndZ=0
    g2: LineSegment [constr] StartX=-186.685 StartY=-3.6 StartZ=0 EndX=-186.685 EndY=3.277e-13 EndZ=0
    g3: ArcOfEllipse CenterX=-186.685 CenterY=3.279e-13 CenterZ=0 NormalX=0 NormalY=0 NormalZ=1 MajorRadius=10 MinorRadius=3.6 AngleXU=-3.14159 StartAngle=1.5708 EndAngle=3.14159
    g4: LineSegment [constr] StartX=-196.685 StartY=-5.9e-15 StartZ=0 EndX=-176.685 EndY=-5.9e-15 EndZ=0
    g5: LineSegment [constr] StartX=-186.685 StartY=-3.6 StartZ=0 EndX=-186.685 EndY=3.6 EndZ=0
    g6: GeomPoint [constr] X=-196.015 Y=-1.19e-14 Z=0
    g7: GeomPoint [constr] X=-177.356 Y=-4.9e-15 Z=0
    g8: LineSegment StartX=-176.685 StartY=-3.6 StartZ=0 EndX=-186.685 EndY=-3.6 EndZ=0
  constraints (15):
    c: PointOnObject(g2,g-3)
    c: Coincident(g1,g-5)
    c: DistanceY(g1,g1) = 0
    c: Coincident(g0,g1)
    c: DistanceX(g2,g-5) = 10
    c: Vertical(g2)
    c: Horizontal(g2,g0)
    c: InternalAlignment(g4-g7 -> g3) x4
    c: Coincident(g3,g2)
    c: Horizontal(g4)
    c: Coincident(g3,g0)
    c: Tangent(g0,g-5) = 1.5708
    c: Coincident(g3,g2)
    c: Coincident(g8,g0)
    c: Coincident(g8,g2)
FEATURE [Sketcher::SketchObject] Sketch107  label="Sketch107 - smusso impugnatura esterno"
  ArcFitTolerance = 1e-06
  AttachmentSupport = -> [Pad008]
  ExternalGeometry = -> [Pad008]
  FullyConstrained = true
  MakeInternals = false
  MapMode = 5
  Placement = pos=(0,-1.585e-13,-80.4316) rot=(1,0,0;3.14159rad)
  sketch-geometry (9):
    g0: LineSegment [constr] StartX=-215.932 StartY=-1.416e-13 StartZ=0 EndX=-215.932 EndY=-4.13e-14 EndZ=0
    g1: LineSegment StartX=-215.932 StartY=-3.6 StartZ=0 EndX=-215.932 EndY=-4.13e-14 EndZ=0
    g2: LineSegment StartX=-215.932 StartY=-3.6 StartZ=0 EndX=-205.932 EndY=-3.6 EndZ=0
    g3: LineSegment [constr] StartX=-205.932 StartY=-3.6 StartZ=0 EndX=-205.932 EndY=-4.13e-14 EndZ=0
    g4: ArcOfEllipse CenterX=-205.932 CenterY=-4.13e-14 CenterZ=0 NormalX=0 NormalY=0 NormalZ=1 MajorRadius=10 MinorRadius=3.6 AngleXU=-3.14159 StartAngle=-2.66e-14 EndAngle=1.5708
    g5: LineSegment [constr] StartX=-215.932 StartY=-1.416e-13 StartZ=0 EndX=-195.932 EndY=-1.416e-13 EndZ=0
    g6: LineSegment [constr] StartX=-205.932 StartY=-3.6 StartZ=0 EndX=-205.932 EndY=3.6 EndZ=0
    g7: GeomPoint [constr] X=-215.262 Y=-1.309e-13 Z=0
    g8: GeomPoint [constr] X=-196.602 Y=-1.551e-13 Z=0
  constraints (16):
    c: Coincident(g0,g-6)
    c: PointOnObject(g0,g-6)
    c: DistanceY(g0,g0) = 0
    c: Coincident(g1,g-6)
    c: Coincident(g1,g0)
    c: Tangent(g2,g-3)
    c: DistanceX(g2,g2) = 10
    c: Coincident(g3,g2)
    c: Vertical(g3)
    c: Horizontal(g3,g0)
    c: InternalAlignment(g5-g8 -> g4) x4
    c: Coincident(g4,g3)
    c: Horizontal(g5)
    c: Coincident(g4,g0)
    c: Coincident(g4,g2)
    c: PointOnObject(g2,g1)
FEATURE [Sketcher::SketchObject] Sketch108
  ArcFitTolerance = 1e-06
  AttachmentOffset = pos=(0,0,-1.6) rot=(0,0,1;0rad)
  AttachmentSupport = -> [Pad008]
  ExternalGeometry = -> [Binder]
  FullyConstrained = true
  MakeInternals = false
  MapMode = 5
  Placement = pos=(0,2,4e-16) rot=(0,0.707107,0.707107;3.14159rad)
  sketch-geometry (14):
    g0: LineSegment StartX=192.176 StartY=-3.18451 StartZ=0 EndX=193.827 EndY=-6.72678 EndZ=0
    g1: LineSegment [constr] StartX=202.765 StartY=20.303 StartZ=0 EndX=181.223 EndY=20.303 EndZ=0
    g2: LineSegment [constr] StartX=181.223 StartY=20.303 StartZ=0 EndX=181.223 EndY=1.30297 EndZ=0
    g3: ArcOfCircle CenterX=181.223 CenterY=-12.6042 CenterZ=0 NormalX=0 NormalY=0 NormalZ=1 AngleXU=0 Radius=13.9072 StartAngle=0.436332 EndAngle=1.5708
    g4: ArcOfEllipse CenterX=181.223 CenterY=10.803 CenterZ=0 NormalX=0 NormalY=0 NormalZ=1 MajorRadius=14.4779 MinorRadius=9.5 AngleXU=0 StartAngle=1.5708 EndAngle=4.71239
    g5: LineSegment [constr] StartX=195.701 StartY=10.803 StartZ=0 EndX=166.745 EndY=10.803 EndZ=0
    g6: LineSegment [constr] StartX=181.223 StartY=20.303 StartZ=0 EndX=181.223 EndY=1.30297 EndZ=0
    g7: GeomPoint [constr] X=192.148 Y=10.803 Z=0
    g8: GeomPoint [constr] X=170.298 Y=10.803 Z=0
    g9: LineSegment StartX=181.223 StartY=20.303 StartZ=0 EndX=202.765 EndY=20.303 EndZ=0
    g10: ArcOfCircle CenterX=207.583 CenterY=4 CenterZ=0 NormalX=0 NormalY=0 NormalZ=1 AngleXU=0 Radius=17 StartAngle=1.85815 EndAngle=3.57792
    g11: LineSegment [constr] StartX=172.411 StartY=39.2 StartZ=0 EndX=192.176 EndY=-3.18451 EndZ=0
    g12: GeomPoint [constr] X=181.223 Y=1.30297 Z=0
    g13: GeomPoint [constr] X=181.223 Y=1.30297 Z=0
  constraints (28):
    c: Coincident(g1,g-7)
    c: Horizontal(g1)
    c: Coincident(g2,g1)
    c: Vertical(g2)
    c: Coincident(g3,g2)
    c: InternalAlignment(g5-g8 -> g4) x4
    c: Horizontal(g5)
    c: PointOnObject(g4,g2)
    c: Coincident(g4,g1)
    c: DistanceX(g-3,g5) = 19.1
    c: Coincident(g4,g2)
    c: Coincident(g9,g1)
    c: Coincident(g9,g1)
    c: Coincident(g10,g1)
    c: Coincident(g10,g0)
    c: PointOnObject(g11,g-6)
    c: PointOnObject(g1,g11)
    c: DistanceY(g2,g1) = 19
    c: Coincident(g10,g-4)
    c: PointOnObject(g12,g4)
    c: PointOnObject(g12,g3)
    c: Tangent(g11,g-5) = -1.5708
    c: Tangent(g0,g-5) = -1.5708
    c: Tangent(g3,g0) = 1.5708
    c: PointOnObject(g13,g4)
    c: PointOnObject(g13,g3)
    c: Tangent(g4,g3,g13) = 1.5708
    c: Horizontal(g11,g0)
FEATURE [Part::Part2DObjectPython] Clone2D  label="Sketch108 (2D)"  # Draft 2D object (typed FeaturePython)
  Fuse = false
  Objects = -> [Sketch108]
  Placement = pos=(0,2,4e-16) rot=(0,0.707107,0.707107;3.14159rad)
  Scale = (1,1,1)
FEATURE [Sketcher::SketchObject] Sketch109
  ArcFitTolerance = 1e-06
  AttachmentOffset = pos=(0,0,-3.5) rot=(0,0,1;0rad)
  AttachmentSupport = -> [Pad008]
  ExternalGeometry = -> [Binder]
  FullyConstrained = true
  MakeInternals = false
  MapMode = 5
  Placement = pos=(0,0.1,8e-16) rot=(0,0.707107,0.707107;3.14159rad)
  sketch-geometry (1):
    g0: GeomPoint X=197.47 Y=8.55923 Z=0
  constraints (1):
    c: Symmetric(g-7,g-5,g0)
FEATURE [PartDesign::Chamfer] Chamfer005
  Angle = 45
  Base = -> Pad009 [Edge215,Edge212]
  BaseFeature = -> Pad009
  ChamferType = 1
  FlipDirection = false
  Refine = true
  Size = 1.5
  Size2 = 2.8
  SupportTransform = false
  Suppressed = false
  UseAllEdges = false
FEATURE [Sketcher::SketchObject] Sketch111
  ArcFitTolerance = 1e-06
  AttachmentSupport = -> [Pad009]
  ExternalGeometry = -> [Pad009]
  FullyConstrained = true
  MakeInternals = false
  MapMode = 5
  Placement = pos=(0,3.6,-8e-16) rot=(0,0.707107,0.707107;3.14159rad)
  sketch-geometry (21):
    g0: LineSegment [constr] StartX=97 StartY=36.8 StartZ=0 EndX=97 EndY=26.8 EndZ=0
    g1: LineSegment StartX=97 StartY=28.6 StartZ=0 EndX=97 EndY=27.8 EndZ=0
    g2: LineSegment StartX=97 StartY=27.8 StartZ=0 EndX=108 EndY=27.8 EndZ=0
    g3: LineSegment StartX=108 StartY=27.8 StartZ=0 EndX=108 EndY=28.6 EndZ=0
    g4: LineSegment StartX=108 StartY=28.6 StartZ=0 EndX=97 EndY=28.6 EndZ=0
    g5: LineSegment StartX=97 StartY=35.8 StartZ=0 EndX=97 EndY=35 EndZ=0
    g6: LineSegment StartX=97 StartY=35 StartZ=0 EndX=108 EndY=35 EndZ=0
    g7: LineSegment StartX=108 StartY=35 StartZ=0 EndX=108 EndY=35.8 EndZ=0
    g8: LineSegment StartX=108 StartY=35.8 StartZ=0 EndX=97 EndY=35.8 EndZ=0
    g9: LineSegment StartX=97 StartY=30.4 StartZ=0 EndX=97 EndY=29.6 EndZ=0
    g10: LineSegment StartX=97 StartY=29.6 StartZ=0 EndX=108 EndY=29.6 EndZ=0
    g11: LineSegment StartX=108 StartY=29.6 StartZ=0 EndX=108 EndY=30.4 EndZ=0
    g12: LineSegment StartX=108 StartY=30.4 StartZ=0 EndX=97 EndY=30.4 EndZ=0
    g13: LineSegment StartX=97 StartY=34 StartZ=0 EndX=97 EndY=33.2 EndZ=0
    g14: LineSegment StartX=97 StartY=33.2 StartZ=0 EndX=108 EndY=33.2 EndZ=0
    g15: LineSegment StartX=108 StartY=33.2 StartZ=0 EndX=108 EndY=34 EndZ=0
    g16: LineSegment StartX=108 StartY=34 StartZ=0 EndX=97 EndY=34 EndZ=0
    g17: LineSegment StartX=97 StartY=32.2 StartZ=0 EndX=97 EndY=31.4 EndZ=0
    g18: LineSegment StartX=97 StartY=31.4 StartZ=0 EndX=108 EndY=31.4 EndZ=0
    g19: LineSegment StartX=108 StartY=31.4 StartZ=0 EndX=108 EndY=32.2 EndZ=0
    g20: LineSegment StartX=108 StartY=32.2 StartZ=0 EndX=97 EndY=32.2 EndZ=0
  constraints (54):
    c: Vertical(g0)
    c: PointOnObject(g0,g-3)
    c: PointOnObject(g0,g-4)
    c: DistanceX(g0,g-5) = 11
    c: Coincident(g1,g2)
    c: Coincident(g2,g3)
    c: Coincident(g3,g4)
    c: Coincident(g4,g1)
    c: Horizontal(g2)
    c: Horizontal(g4)
    c: Tangent(g1,g0)
    c: Tangent(g3,g-5)
    c: DistanceY(g2,g3) = 0.8
    c: Coincident(g5,g6)
    c: Coincident(g6,g7)
    c: Coincident(g7,g8)
    c: Coincident(g8,g5)
    c: Horizontal(g6)
    c: Horizontal(g8)
    c: DistanceY(g6,g7) = 0.8
    c: Coincident(g9,g10)
    c: Coincident(g10,g11)
    c: Coincident(g11,g12)
    c: Coincident(g12,g9)
    c: Horizontal(g10)
    c: Horizontal(g12)
    c: DistanceY(g10,g11) = 0.8
    c: Tangent(g5,g0)
    c: Tangent(g7,g-5)
    c: Tangent(g9,g0)
    c: Tangent(g11,g-5)
    c: Coincident(g13,g14)
    c: Coincident(g14,g15)
    c: Coincident(g15,g16)
    c: Coincident(g16,g13)
    c: Horizontal(g14)
    c: Horizontal(g16)
    c: DistanceY(g14,g15) = 0.8
    c: Tangent(g13,g0)
    c: Tangent(g15,g-5)
    c: Coincident(g17,g18)
    c: Coincident(g18,g19)
    c: Coincident(g19,g20)
    c: Coincident(g20,g17)
    c: Horizontal(g18)
    c: Horizontal(g20)
    c: DistanceY(g18,g19) = 0.8
    c: Tangent(g17,g0)
    c: Tangent(g19,g-5)
    c: DistanceY(g1,g9) = 1
    c: DistanceY(g9,g17) = 1
    c: DistanceY(g17,g13) = 1
    c: DistanceY(g13,g5) = 1
    c: DistanceY(g0,g1) = 1
FEATURE [PartDesign::Pocket] Pocket004
  BaseFeature = -> Chamfer005
  Direction = (0,-1,2e-16)
  Length = 1
  Length2 = 5
  Profile = -> Sketch111
  ReferenceAxis = -> Sketch111 [N_Axis]
  Refine = true
  Suppressed = false
  Type = 0
FEATURE [PartDesign::Pad] Pad010
  BaseFeature = -> Pocket004
  Direction = (0,1,-2e-16)
  Length = 1.2
  Length2 = 10
  Profile = -> Sketch098
  ReferenceAxis = -> Sketch098 [N_Axis]
  Refine = true
  Suppressed = false
  Type = 0
FEATURE [PartDesign::Chamfer] Chamfer006
  Angle = 45
  Base = -> Pad010 [Edge291]
  BaseFeature = -> Pad010
  ChamferType = 1
  FlipDirection = false
  Refine = true
  Size = 1
  Size2 = 6
  SupportTransform = false
  Suppressed = false
  UseAllEdges = false
FEATURE [Sketcher::SketchObject] Sketch110
  ArcFitTolerance = 1e-06
  AttachmentSupport = -> [Pad010]
  ExternalGeometry = -> [Sketch098]
  FullyConstrained = true
  MakeInternals = false
  MapMode = 5
  Placement = pos=(0,4,-9e-16) rot=(0,0.707107,0.707107;3.14159rad)
  sketch-geometry (8):
    g0: LineSegment StartX=119.69 StartY=34 StartZ=0 EndX=130.69 EndY=34 EndZ=0
    g1: LineSegment StartX=119.95 StartY=33.2 StartZ=0 EndX=130.95 EndY=33.2 EndZ=0
    g2: LineSegment StartX=119.137 StartY=35.7 StartZ=0 EndX=130.137 EndY=35.7 EndZ=0
    g3: LineSegment StartX=118.877 StartY=36.5 StartZ=0 EndX=129.877 EndY=36.5 EndZ=0
    g4: LineSegment StartX=118.877 StartY=36.5 StartZ=0 EndX=119.137 EndY=35.7 EndZ=0
    g5: LineSegment StartX=129.877 StartY=36.5 StartZ=0 EndX=130.137 EndY=35.7 EndZ=0
    g6: LineSegment StartX=119.69 StartY=34 StartZ=0 EndX=119.95 EndY=33.2 EndZ=0
    g7: LineSegment StartX=130.69 StartY=34 StartZ=0 EndX=130.95 EndY=33.2 EndZ=0
  constraints (24):
    c: Horizontal(g0)
    c: Horizontal(g1)
    c: Horizontal(g2)
    c: Horizontal(g3)
    c: Equal(g1,g-5)
    c: Equal(g0,g-5)
    c: Equal(g2,g-5)
    c: Equal(g3,g-5)
    c: PointOnObject(g0,g-3)
    c: PointOnObject(g1,g-3)
    c: PointOnObject(g2,g-3)
    c: PointOnObject(g3,g-3)
    c: Coincident(g4,g3)
    c: Coincident(g4,g2)
    c: Coincident(g5,g3)
    c: Coincident(g5,g2)
    c: Coincident(g6,g0)
    c: Coincident(g6,g1)
    c: Coincident(g7,g0)
    c: Coincident(g7,g1)
    c: DistanceY(g1,g0) = 0.8
    c: DistanceY(g2,g3) = 0.8
    c: DistanceY(g-5,g1) = 2
    c: DistanceY(g-5,g2) = 4.5
FEATURE [PartDesign::Pocket] Pocket003
  BaseFeature = -> Chamfer006
  Direction = (0,-1,2e-16)
  Length = 1
  Length2 = 5
  Profile = -> Sketch110
  ReferenceAxis = -> Sketch110 [N_Axis]
  Refine = true
  Suppressed = false
  Type = 0
FEATURE [PartDesign::SubtractivePipe] SubtractivePipe
  AuxilleryCurvelinear = true
  AuxillerySpineTangent = false
  BaseFeature = -> Pocket003
  Binormal = (0,0,0)
  Mode = 0
  Profile = -> Sketch106
  Refine = true
  Spine = -> Pad008 [Edge215]
  SpineTangent = false
  Suppressed = false
  Transformation = 0
  Transition = 0
FEATURE [PartDesign::SubtractivePipe] SubtractivePipe001
  AuxilleryCurvelinear = true
  AuxillerySpineTangent = false
  BaseFeature = -> SubtractivePipe
  Binormal = (0,0,0)
  Mode = 0
  Profile = -> Sketch107
  Refine = true
  Spine = -> Pad008 [Edge213,Edge216,Edge210]
  SpineTangent = false
  Suppressed = false
  Transformation = 0
  Transition = 0
FEATURE [PartDesign::SubtractiveLoft] SubtractiveLoft
  BaseFeature = -> SubtractivePipe001
  Closed = false
  Profile = -> Sketch099
  Refine = true
  Ruled = false
  Sections = -> [Sketch108]
  Suppressed = false
FEATURE [PartDesign::SubtractiveLoft] SubtractiveLoft001
  BaseFeature = -> SubtractiveLoft
  Closed = false
  Profile = -> Clone2D
  Refine = true
  Ruled = false
  Sections = -> [Sketch109]
  Suppressed = false
FEATURE [Sketcher::SketchObject] Sketch112
  ArcFitTolerance = 1e-06
  AttachmentSupport = -> [Pad008]
  ExternalGeometry = -> [Binder]
  FullyConstrained = true
  MakeInternals = false
  MapMode = 5
  Placement = pos=(0,3.6,0) rot=(0,0.707107,0.707107;3.14159rad)
  sketch-geometry (4):
    g0: LineSegment [constr] StartX=167.782 StartY=-53.0314 StartZ=0 EndX=215.42 EndY=-53.0314 EndZ=0
    g1: GeomPoint [constr] X=191.282 Y=-53.0314 Z=0
    g2: Circle CenterX=191.282 CenterY=-53.0314 CenterZ=0 NormalX=0 NormalY=0 NormalZ=1 AngleXU=0 Radius=11.5
    g3: Circle CenterX=191.282 CenterY=-53.0314 CenterZ=0 NormalX=0 NormalY=0 NormalZ=1 AngleXU=0 Radius=10.7
  constraints (9):
    c: Horizontal(g0)
    c: PointOnObject(g0,g-3)
    c: Diameter(g2) = 23
    c: Coincident(g2,g1)
    c: Diameter(g3) = 21.4
    c: Coincident(g3,g1)
    c: DistanceX(g0,g1) = 23.5
    c: PointOnObject(g1,g0)
    c: Coincident(g0,g-4)
FEATURE [PartDesign::Chamfer] Chamfer016
  Angle = 45
  Base = -> SubtractiveLoft001 [Edge118,Edge117,Edge119,Edge120,Edge109]
  BaseFeature = -> SubtractiveLoft001
  ChamferType = 0
  FlipDirection = false
  Refine = true
  Size = 1.5
  Size2 = 1
  SupportTransform = false
  Suppressed = false
  UseAllEdges = false
FEATURE [PartDesign::Chamfer] Chamfer017
  Angle = 45
  Base = -> Chamfer016 [Edge15]
  BaseFeature = -> Chamfer016
  ChamferType = 0
  FlipDirection = false
  Refine = true
  Size = 1.6
  Size2 = 1
  SupportTransform = false
  Suppressed = false
  UseAllEdges = false
FEATURE [PartDesign::Chamfer] Chamfer018
  Angle = 45
  Base = -> Chamfer017 [Edge10]
  BaseFeature = -> Chamfer017
  ChamferType = 0
  FlipDirection = false
  Refine = true
  Size = 3.5
  Size2 = 1
  SupportTransform = false
  Suppressed = false
  UseAllEdges = false
FEATURE [PartDesign::Chamfer] Chamfer019
  Angle = 45
  Base = -> Chamfer018 [Edge94]
  BaseFeature = -> Chamfer018
  ChamferType = 0
  FlipDirection = false
  Refine = true
  Size = 1.9
  Size2 = 1
  SupportTransform = false
  Suppressed = false
  UseAllEdges = false
FEATURE [PartDesign::Fillet] Fillet009
  Base = -> Chamfer019 [Edge83]
  BaseFeature = -> Chamfer019
  Radius = 1.1
  Refine = true
  SupportTransform = false
  Suppressed = false
  UseAllEdges = false
FEATURE [PartDesign::Fillet] Fillet010
  Base = -> Fillet009 [Edge76]
  BaseFeature = -> Fillet009
  Radius = 1.9
  Refine = true
  SupportTransform = false
  Suppressed = false
  UseAllEdges = false
FEATURE [PartDesign::Pocket] Pocket005
  BaseFeature = -> Fillet010
  Direction = (0,-1,2e-16)
  Length = 0.8
  Length2 = 5
  Profile = -> Sketch112
  ReferenceAxis = -> Sketch112 [N_Axis]
  Refine = true
  Suppressed = false
  Type = 0
FEATURE [Part::Part2DObjectPython] ShapeString001  # Draft 2D object (typed FeaturePython)
  FontFile = <path>
  Fuse = false
  Justification = 6
  JustificationReference = 0
  KeepLeftMargin = false
  MakeFace = true
  ObliqueAngle = 0
  Placement = pos=(-183.5,3.6,-57.5) rot=(0,0.707107,0.707107;3.14159rad)
  ScaleToSize = true
  Size = 10
  String = AS
  Tracking = 0
FEATURE [PartDesign::Pocket] Pocket013
  BaseFeature = -> Pocket005
  Direction = (-1e-16,-1,2e-16)
  Length = 1
  Length2 = 5
  Profile = -> ShapeString001
  ReferenceAxis = -> ShapeString001 [N_Axis]
  Refine = true
  Suppressed = false
  Type = 0
FEATURE [PartDesign::Pad] Pad020
  Direction = (0,-1,2e-16)
  Length = 25.2
  Length2 = 10
  Midplane = true
  Placement = pos=(0,0,0) rot=(1,0,0;1.5708rad)
  Profile = -> Sketch021
  ReferenceAxis = -> Sketch021 [N_Axis]
  Refine = true
  Suppressed = false
  Type = 0
FEATURE [PartDesign::Body] Body001  label="perno fermo rumble e driver solenoide"
  AllowCompound = false
  Group = -> [Sketch021,Pad020]
  Origin = -> Origin001
  Tip = -> Pad020
FEATURE [PartDesign::Pad] Pad021
  Direction = (0,-1,2e-16)
  Length = 16.8
  Length2 = 10
  Midplane = true
  Placement = pos=(0,0,0) rot=(1,0,0;1.5708rad)
  Profile = -> Sketch061
  ReferenceAxis = -> Sketch061 [N_Axis]
  Refine = true
  Suppressed = false
  Type = 0
FEATURE [PartDesign::Pocket] Pocket014
  BaseFeature = -> Pad021
  Direction = (0,1,-2e-16)
  Length = 12.8
  Length2 = 5
  Midplane = true
  Placement = pos=(0,0,0) rot=(1,0,0;1.5708rad)
  Profile = -> Sketch062
  ReferenceAxis = -> Sketch062 [N_Axis]
  Refine = true
  Suppressed = false
  Type = 0
FEATURE [PartDesign::Pad] Pad022
  BaseFeature = -> Pocket014
  Direction = (0,-1,2e-16)
  Length = 7.6
  Length2 = 10
  Midplane = true
  Placement = pos=(0,0,0) rot=(1,0,0;1.5708rad)
  Profile = -> Sketch063
  ReferenceAxis = -> Sketch063 [N_Axis]
  Refine = true
  Suppressed = false
  Type = 0
FEATURE [PartDesign::Body] Body003  label="blocco switch"
  AllowCompound = false
  Group = -> [Sketch061,Sketch062,Sketch063,Pad021,Pocket014,Pad022]
  Origin = -> Origin003
  Tip = -> Pad022
FEATURE [PartDesign::Pad] Pad024
  Direction = (0,-1,2e-16)
  Length = 17
  Length2 = 10
  Midplane = true
  Placement = pos=(0,0,0) rot=(1,0,0;1.5708rad)
  Profile = -> Sketch045
  ReferenceAxis = -> Sketch045 [N_Axis]
  Refine = true
  Suppressed = false
  Type = 0
FEATURE [PartDesign::Pocket] Pocket015
  BaseFeature = -> Pad024
  Direction = (-1,0,0)
  Length = 8
  Length2 = 5
  Placement = pos=(0,0,0) rot=(1,0,0;1.5708rad)
  Profile = -> Sketch047
  ReferenceAxis = -> Sketch047 [N_Axis]
  Refine = true
  Reversed = true
  Suppressed = false
  Type = 0
FEATURE [PartDesign::Pocket] Pocket016
  BaseFeature = -> Pocket015
  Direction = (-1,0,0)
  Length = 1
  Length2 = 5
  Placement = pos=(0,0,0) rot=(1,0,0;1.5708rad)
  Profile = -> Sketch046
  ReferenceAxis = -> Sketch046 [N_Axis]
  Refine = true
  Reversed = true
  Suppressed = false
  Type = 0
FEATURE [PartDesign::Pocket] Pocket017
  BaseFeature = -> Pocket016
  Direction = (0,1,-2e-16)
  Length = 17
  Length2 = 5
  Midplane = true
  Placement = pos=(0,0,0) rot=(1,0,0;1.5708rad)
  Profile = -> Sketch048
  ReferenceAxis = -> Sketch048 [N_Axis]
  Refine = true
  Suppressed = false
  Type = 0
FEATURE [PartDesign::Pad] Pad025
  BaseFeature = -> Pocket017
  Direction = (0,-1,2e-16)
  Length = 17
  Length2 = 10
  Midplane = true
  Placement = pos=(0,0,0) rot=(1,0,0;1.5708rad)
  Profile = -> Sketch049
  ReferenceAxis = -> Sketch049 [N_Axis]
  Refine = true
  Suppressed = false
  Type = 0
FEATURE [PartDesign::Pad] Pad026
  BaseFeature = -> Pad025
  Direction = (0,-1,2e-16)
  Length = 17
  Length2 = 10
  Midplane = true
  Placement = pos=(0,0,0) rot=(1,0,0;1.5708rad)
  Profile = -> Sketch066
  ReferenceAxis = -> Sketch066 [N_Axis]
  Refine = true
  Suppressed = false
  Type = 0
FEATURE [PartDesign::Pad] Pad027
  BaseFeature = -> Pad026
  Direction = (0,-1,2e-16)
  Length = 5
  Length2 = 10
  Midplane = true
  Placement = pos=(0,0,0) rot=(1,0,0;1.5708rad)
  Profile = -> Sketch064
  ReferenceAxis = -> Sketch064 [N_Axis]
  Refine = true
  Suppressed = false
  Type = 0
FEATURE [PartDesign::Pad] Pad028
  BaseFeature = -> Pad027
  Direction = (1,0,0)
  Length = 1
  Length2 = 10
  Placement = pos=(0,0,0) rot=(1,0,0;1.5708rad)
  Profile = -> Sketch068
  ReferenceAxis = -> Sketch068 [N_Axis]
  Refine = true
  Reversed = true
  Suppressed = false
  Type = 0
FEATURE [PartDesign::Chamfer] Chamfer020
  Angle = 45
  Base = -> Pad028 [Edge73,Edge75,Edge78,Edge77]
  BaseFeature = -> Pad028
  ChamferType = 0
  FlipDirection = false
  Placement = pos=(0,0,0) rot=(1,0,0;1.5708rad)
  Refine = true
  Size = 0.5
  Size2 = 1
  SupportTransform = false
  Suppressed = false
  UseAllEdges = false
FEATURE [PartDesign::Body] Body002  label="supporto per neopixel"
  AllowCompound = false
  Group = -> [Sketch045,Sketch047,Sketch046,Sketch048,Sketch049,Sketch066,Sketch064,Sketch068,Pad024,Pocket015,Pocket016,Pocket017,Pad025,Pad026,Pad027,Pad028,Chamfer020]
  Origin = -> Origin002
  Tip = -> Chamfer020
FEATURE [Sketcher::SketchObject] Sketch134  label="perno fermo rumble002"
  ArcFitTolerance = 1e-06
  AttachmentSupport = -> [XZ_Plane008]
  FullyConstrained = true
  MakeInternals = false
  MapMode = 5
  Placement = pos=(0,0,0) rot=(1,0,0;1.5708rad)
  sketch-geometry (16):
    g0: LineSegment StartX=0 StartY=0.45 StartZ=0 EndX=0 EndY=1.55 EndZ=0
    g1: LineSegment StartX=0.45 StartY=2 StartZ=0 EndX=1.55 EndY=2 EndZ=0
    g2: LineSegment StartX=2 StartY=1.55 StartZ=0 EndX=2 EndY=0.45 EndZ=0
    g3: LineSegment StartX=1.55 StartY=0 StartZ=0 EndX=0.45 EndY=0 EndZ=0
    g4: ArcOfCircle [constr] CenterX=0.45 CenterY=1.55 CenterZ=0 NormalX=0 NormalY=0 NormalZ=1 AngleXU=0 Radius=0.45 StartAngle=1.5708 EndAngle=3.14159
    g5: GeomPoint [constr] X=0 Y=2 Z=0
    g6: LineSegment StartX=0.45 StartY=2 StartZ=0 EndX=0 EndY=1.55 EndZ=0
    g7: ArcOfCircle [constr] CenterX=1.55 CenterY=1.55 CenterZ=0 NormalX=0 NormalY=0 NormalZ=1 AngleXU=0 Radius=0.45 StartAngle=0 EndAngle=1.5708
    g8: GeomPoint [constr] X=2 Y=2 Z=0
    g9: LineSegment StartX=2 StartY=1.55 StartZ=0 EndX=1.55 EndY=2 EndZ=0
    g10: ArcOfCircle [constr] CenterX=1.55 CenterY=0.45 CenterZ=0 NormalX=0 NormalY=0 NormalZ=1 AngleXU=0 Radius=0.45 StartAngle=4.71239 EndAngle=6.28319
    g11: GeomPoint [constr] X=2 Y=0 Z=0
    g12: LineSegment StartX=1.55 StartY=0 StartZ=0 EndX=2 EndY=0.45 EndZ=0
    g13: ArcOfCircle [constr] CenterX=0.45 CenterY=0.45 CenterZ=0 NormalX=0 NormalY=0 NormalZ=1 AngleXU=0 Radius=0.45 StartAngle=3.14159 EndAngle=4.71239
    g14: GeomPoint [constr] X=0 Y=0 Z=0
    g15: LineSegment StartX=0 StartY=0.45 StartZ=0 EndX=0.45 EndY=0 EndZ=0
  constraints (35):
    c: Coincident(g14,g-1)
    c: PointOnObject(g5,g-2)
    c: Horizontal(g1)
    c: Vertical(g2)
    c: Horizontal(g3)
    c: DistanceX(g5,g8) = 2
    c: DistanceY(g11,g8) = 2
    c: PointOnObject(g5,g0)
    c: PointOnObject(g5,g1)
    c: Tangent(g0,g4) = 1.5708
    c: Tangent(g1,g4) = 1.5708
    c: Coincident(g6,g0)
    c: Coincident(g6,g1)
    c: PointOnObject(g8,g2)
    c: PointOnObject(g8,g1)
    c: Tangent(g2,g7) = 1.5708
    c: Tangent(g1,g7) = 1.5708
    c: Coincident(g9,g2)
    c: Coincident(g9,g1)
    c: PointOnObject(g11,g2)
    c: PointOnObject(g11,g3)
    c: Tangent(g2,g10) = 1.5708
    c: Tangent(g3,g10) = 1.5708
    c: Coincident(g12,g2)
    c: Coincident(g12,g3)
    c: PointOnObject(g14,g0)
    c: PointOnObject(g14,g3)
    c: Tangent(g0,g13) = 1.5708
    c: Tangent(g3,g13) = 1.5708
    c: Coincident(g15,g0)
    c: Coincident(g15,g3)
    c: Equal(g6,g9)
    c: Equal(g9,g12)
    c: Equal(g12,g15)
    c: DistanceX(g14,g3) = 0.45
FEATURE [PartDesign::Pad] Pad029
  Direction = (0,-1,2e-16)
  Length = 17
  Length2 = 10
  Midplane = true
  Placement = pos=(0,0,0) rot=(1,0,0;1.5708rad)
  Profile = -> Sketch134
  ReferenceAxis = -> Sketch134 [N_Axis]
  Refine = true
  Suppressed = false
  Type = 0
FEATURE [PartDesign::Body] Body008  label="perno fermo neopixel"
  AllowCompound = false
  Group = -> [Sketch134,Pad029]
  Origin = -> Origin008
  Tip = -> Pad029
FEATURE [Sketcher::SketchObject] Sketch135  label="perno fermo rumble003"
  ArcFitTolerance = 1e-06
  AttachmentSupport = -> [XZ_Plane009]
  FullyConstrained = true
  MakeInternals = false
  MapMode = 5
  Placement = pos=(0,0,0) rot=(1,0,0;1.5708rad)
  sketch-geometry (16):
    g0: LineSegment StartX=4.69e-14 StartY=0.8 StartZ=0 EndX=-3.04e-14 EndY=3.1 EndZ=0
    g1: LineSegment StartX=0.8 StartY=3.9 StartZ=0 EndX=3.1 EndY=3.9 EndZ=0
    g2: LineSegment StartX=3.9 StartY=3.1 StartZ=0 EndX=3.9 EndY=0.8 EndZ=0
    g3: LineSegment StartX=3.1 StartY=0 StartZ=0 EndX=0.8 EndY=0 EndZ=0
    g4: ArcOfCircle [constr] CenterX=0.8 CenterY=3.1 CenterZ=0 NormalX=0 NormalY=0 NormalZ=1 AngleXU=0 Radius=0.8 StartAngle=1.5708 EndAngle=3.14159
    g5: GeomPoint [constr] X=0 Y=3.9 Z=0
    g6: LineSegment StartX=0.8 StartY=3.9 StartZ=0 EndX=-3.04e-14 EndY=3.1 EndZ=0
    g7: ArcOfCircle [constr] CenterX=3.1 CenterY=3.1 CenterZ=0 NormalX=0 NormalY=0 NormalZ=1 AngleXU=0 Radius=0.8 StartAngle=-2.4e-14 EndAngle=1.5708
    g8: GeomPoint [constr] X=3.9 Y=3.9 Z=0
    g9: LineSegment StartX=3.9 StartY=3.1 StartZ=0 EndX=3.1 EndY=3.9 EndZ=0
    g10: ArcOfCircle [constr] CenterX=3.1 CenterY=0.8 CenterZ=0 NormalX=0 NormalY=0 NormalZ=1 AngleXU=0 Radius=0.8 StartAngle=4.71239 EndAngle=6.28319
    g11: GeomPoint [constr] X=3.9 Y=0 Z=0
    g12: LineSegment StartX=3.1 StartY=0 StartZ=0 EndX=3.9 EndY=0.8 EndZ=0
    g13: ArcOfCircle [constr] CenterX=0.8 CenterY=0.8 CenterZ=0 NormalX=0 NormalY=0 NormalZ=1 AngleXU=0 Radius=0.8 StartAngle=3.14159 EndAngle=4.71239
    g14: GeomPoint [constr] X=0 Y=0 Z=0
    g15: LineSegment StartX=4.69e-14 StartY=0.8 StartZ=0 EndX=0.8 EndY=0 EndZ=0
  constraints (35):
    c: Coincident(g14,g-1)
    c: PointOnObject(g5,g-2)
    c: Horizontal(g1)
    c: Vertical(g2)
    c: Horizontal(g3)
    c: DistanceX(g5,g8) = 3.9
    c: DistanceY(g11,g8) = 3.9
    c: PointOnObject(g5,g0)
    c: PointOnObject(g5,g1)
    c: Tangent(g0,g4) = 1.5708
    c: Tangent(g1,g4) = 1.5708
    c: Coincident(g6,g0)
    c: Coincident(g6,g1)
    c: PointOnObject(g8,g2)
    c: PointOnObject(g8,g1)
    c: Tangent(g2,g7) = 1.5708
    c: Tangent(g1,g7) = 1.5708
    c: Coincident(g9,g2)
    c: Coincident(g9,g1)
    c: PointOnObject(g11,g2)
    c: PointOnObject(g11,g3)
    c: Tangent(g2,g10) = 1.5708
    c: Tangent(g3,g10) = 1.5708
    c: Coincident(g12,g2)
    c: Coincident(g12,g3)
    c: PointOnObject(g14,g0)
    c: PointOnObject(g14,g3)
    c: Tangent(g0,g13) = 1.5708
    c: Tangent(g3,g13) = 1.5708
    c: Coincident(g15,g0)
    c: Coincident(g15,g3)
    c: Equal(g6,g9)
    c: Equal(g9,g12)
    c: Equal(g12,g15)
    c: DistanceX(g14,g3) = 0.8
FEATURE [PartDesign::Pad] Pad030
  Direction = (0,-1,2e-16)
  Length = 25.2
  Length2 = 10
  Midplane = true
  Placement = pos=(0,0,0) rot=(1,0,0;1.5708rad)
  Profile = -> Sketch135
  ReferenceAxis = -> Sketch135 [N_Axis]
  Refine = true
  Suppressed = false
  Type = 0
FEATURE [PartDesign::Body] Body009  label="perno fermo switch - caricabatterie - grilletto"
  AllowCompound = false
  Group = -> [Sketch135,Pad030]
  Origin = -> Origin009
  Tip = -> Pad030
FEATURE [Sketcher::SketchObject] Sketch136  label="scavo_rele"
  ArcFitTolerance = 1e-06
  AttachmentSupport = -> [XZ_Plane]
  ExternalGeometry = -> [Sketch]
  FullyConstrained = true
  MakeInternals = false
  MapMode = 5
  Placement = pos=(0,0,0) rot=(1,0,0;1.5708rad)
  sketch-geometry (7):
    g0: LineSegment [constr] StartX=-173.013 StartY=-62.644 StartZ=0 EndX=-176.535 EndY=-73.4861 EndZ=0
    g1: LineSegment [constr] StartX=-173.013 StartY=-62.644 StartZ=0 EndX=-170.35 EndY=-63.5093 EndZ=0
    g2: LineSegment [constr] StartX=-173.013 StartY=-62.644 StartZ=0 EndX=-176.627 EndY=-61.4698 EndZ=0
    g3: LineSegment StartX=-176.627 StartY=-61.4698 StartZ=0 EndX=-170.35 EndY=-63.5093 EndZ=0
    g4: LineSegment StartX=-176.627 StartY=-61.4698 StartZ=0 EndX=-180.149 EndY=-72.3118 EndZ=0
    g5: LineSegment StartX=-170.35 StartY=-63.5093 StartZ=0 EndX=-173.872 EndY=-74.3513 EndZ=0
    g6: LineSegment StartX=-180.149 StartY=-72.3118 StartZ=0 EndX=-173.872 EndY=-74.3513 EndZ=0
  constraints (19):
    c: Tangent(g0,g-3)
    c: Distance(g0,g-3) = 89
    c: Distance(g0,g0) = 11.4
    c: Coincident(g1,g0)
    c: Coincident(g2,g0)
    c: Distance(g2) = 3.8
    c: Distance(g1) = 2.8
    c: Perpendicular(g0,g1)
    c: Perpendicular(g0,g2)
    c: Coincident(g3,g2)
    c: Coincident(g3,g1)
    c: Equal(g4,g0)
    c: Equal(g5,g0)
    c: Parallel(g4,g0)
    c: Parallel(g5,g0)
    c: Coincident(g4,g2)
    c: Coincident(g5,g1)
    c: Coincident(g6,g4)
    c: Coincident(g6,g5)
FEATURE [Part::Extrusion] Extrude076  label="Extrude076 - scavo_rele"
  Base = -> Sketch136
  Dir = (0,-1,2e-16)
  DirMode = 2
  FaceMakerClass = Part::FaceMakerBullseye
  FaceMakerMode = 3
  LengthFwd = 17.8
  LengthRev = 0
  Solid = true
  Symmetric = true
FEATURE [Sketcher::SketchObject] Sketch137  label="scavo_nuovo_driver"
  ArcFitTolerance = 1e-06
  AttachmentSupport = -> [XZ_Plane]
  ExternalGeometry = -> [Sketch]
  FullyConstrained = true
  MakeInternals = false
  MapMode = 5
  Placement = pos=(0,0,0) rot=(1,0,0;1.5708rad)
  sketch-geometry (7):
    g0: LineSegment [constr] StartX=-167.759 StartY=-46.4761 StartZ=0 EndX=-172.58 EndY=-61.3126 EndZ=0
    g1: LineSegment [constr] StartX=-167.759 StartY=-46.4761 StartZ=0 EndX=-165.477 EndY=-47.2177 EndZ=0
    g2: LineSegment [constr] StartX=-167.759 StartY=-46.4761 StartZ=0 EndX=-171.373 EndY=-45.3018 EndZ=0
    g3: LineSegment StartX=-171.373 StartY=-45.3018 StartZ=0 EndX=-165.477 EndY=-47.2177 EndZ=0
    g4: LineSegment StartX=-171.373 StartY=-45.3018 StartZ=0 EndX=-176.194 EndY=-60.1383 EndZ=0
    g5: LineSegment StartX=-165.477 StartY=-47.2177 StartZ=0 EndX=-170.297 EndY=-62.0542 EndZ=0
    g6: LineSegment StartX=-176.194 StartY=-60.1383 StartZ=0 EndX=-170.297 EndY=-62.0542 EndZ=0
  constraints (19):
    c: Distance(g0,g-3) = 72
    c: Distance(g0) = 15.6
    c: Tangent(g0,g-3)
    c: Coincident(g1,g0)
    c: Coincident(g2,g0)
    c: Distance(g1) = 2.4
    c: Distance(g2) = 3.8
    c: Perpendicular(g0,g1)
    c: Perpendicular(g0,g2)
    c: Coincident(g3,g2)
    c: Coincident(g3,g1)
    c: Equal(g4,g0)
    c: Equal(g5,g0)
    c: Parallel(g4,g0)
    c: Parallel(g5,g0)
    c: Coincident(g4,g2)
    c: Coincident(g5,g1)
    c: Coincident(g6,g4)
    c: Coincident(g6,g5)
FEATURE [Part::Extrusion] Extrude077  label="Extrude077 - scavo_nuovo_driver"
  Base = -> Sketch137
  Dir = (0,-1,2e-16)
  DirMode = 2
  FaceMakerClass = Part::FaceMakerBullseye
  FaceMakerMode = 3
  LengthFwd = 20.8
  LengthRev = 0
  Solid = true
  Symmetric = true
FEATURE [Sketcher::SketchObject] Sketch138  label="scavo_nuovo_driver_alto"
  ArcFitTolerance = 1e-06
  AttachmentSupport = -> [XZ_Plane]
  ExternalGeometry = -> [Sketch]
  FullyConstrained = true
  MakeInternals = false
  MapMode = 5
  Placement = pos=(0,0,0) rot=(1,0,0;1.5708rad)
  sketch-geometry (7):
    g0: LineSegment [constr] StartX=-188.796 StartY=17.7274 StartZ=0 EndX=-187.75 EndY=4.97025 EndZ=0
    g1: LineSegment StartX=-187.75 StartY=4.97025 StartZ=0 EndX=-189.743 EndY=4.8067 EndZ=0
    g2: LineSegment StartX=-187.75 StartY=4.97025 StartZ=0 EndX=-182.766 EndY=5.37913 EndZ=0
    g3: LineSegment StartX=-190.79 StartY=17.5638 StartZ=0 EndX=-189.743 EndY=4.8067 EndZ=0
    g4: LineSegment StartX=-183.813 StartY=18.1363 StartZ=0 EndX=-182.766 EndY=5.37913 EndZ=0
    g5: LineSegment StartX=-190.79 StartY=17.5638 StartZ=0 EndX=-188.796 EndY=17.7274 EndZ=0
    g6: LineSegment StartX=-188.796 StartY=17.7274 StartZ=0 EndX=-183.813 EndY=18.1363 EndZ=0
  constraints (20):
    c: Distance(g0) = 12.8
    c: DistanceY(g-3,g0) = 9
    c: PointOnObject(g0,g-4)
    c: PointOnObject(g0,g-4)
    c: Coincident(g1,g0)
    c: Coincident(g2,g0)
    c: Distance(g1) = 2
    c: Distance(g2) = 5
    c: Perpendicular(g0,g1)
    c: Perpendicular(g0,g2)
    c: Equal(g3,g0)
    c: Parallel(g3,g0)
    c: Coincident(g3,g1)
    c: Equal(g4,g0)
    c: Parallel(g4,g0)
    c: Coincident(g4,g2)
    c: Coincident(g5,g3)
    c: Coincident(g5,g0)
    c: Coincident(g6,g0)
    c: Coincident(g6,g4)
FEATURE [Part::Extrusion] Extrude078  label="Extrude078 - scavo_nuovo_driver_alto"
  Base = -> Sketch138
  Dir = (0,-1,2e-16)
  DirMode = 2
  FaceMakerClass = Part::FaceMakerBullseye
  FaceMakerMode = 3
  LengthFwd = 16.6
  LengthRev = 0
  Solid = true
  Symmetric = true
FEATURE [Sketcher::SketchObject] Sketch139  label="fermi_nuovo_driver_alto"
  ArcFitTolerance = 1e-06
  AttachmentSupport = -> [XZ_Plane]
  ExternalGeometry = -> [Sketch138,Sketch]
  FullyConstrained = true
  MakeInternals = false
  MapMode = 5
  Placement = pos=(0,0,0) rot=(1,0,0;1.5708rad)
  sketch-geometry (17):
    g0: LineSegment [constr] StartX=-188.314 StartY=16.4295 StartZ=0 EndX=-187.885 EndY=13.7638 EndZ=0
    g1: LineSegment [constr] StartX=-187.885 StartY=13.7638 StartZ=0 EndX=-187.456 EndY=11.0981 EndZ=0
    g2: LineSegment StartX=-187.885 StartY=13.7638 StartZ=0 EndX=-187.71 EndY=12.6778 EndZ=0
    g3: LineSegment StartX=-187.885 StartY=13.7638 StartZ=0 EndX=-188.06 EndY=14.8499 EndZ=0
    g4: LineSegment StartX=-187.71 StartY=12.6778 StartZ=0 EndX=-185.538 EndY=13.0274 EndZ=0
    g5: LineSegment StartX=-188.06 StartY=14.8499 StartZ=0 EndX=-185.888 EndY=15.1994 EndZ=0
    g6: LineSegment StartX=-185.888 StartY=15.1994 StartZ=0 EndX=-185.538 EndY=13.0274 EndZ=0
    g7: LineSegment StartX=-187.456 StartY=11.0981 StartZ=0 EndX=-189.035 EndY=10.8439 EndZ=0
    g8: LineSegment StartX=-188.314 StartY=16.4295 StartZ=0 EndX=-189.893 EndY=16.1753 EndZ=0
    g9: LineSegment StartX=-189.893 StartY=16.1753 StartZ=0 EndX=-189.035 EndY=10.8439 EndZ=0
    g10: LineSegment StartX=-187.456 StartY=11.0981 StartZ=0 EndX=-185.284 EndY=11.4477 EndZ=0
    g11: LineSegment StartX=-188.314 StartY=16.4295 StartZ=0 EndX=-186.142 EndY=16.7791 EndZ=0
    g12: LineSegment StartX=-184.308 StartY=15.4537 StartZ=0 EndX=-183.958 EndY=13.2816 EndZ=0
    g13: ArcOfCircle CenterX=-185.888 CenterY=15.1994 CenterZ=0 NormalX=0 NormalY=0 NormalZ=1 AngleXU=0 Radius=1.6 StartAngle=0.15957 EndAngle=1.73037
    g14: GeomPoint [constr] X=-184.562 Y=17.0333 Z=0
    g15: ArcOfCircle CenterX=-185.538 CenterY=13.0274 CenterZ=0 NormalX=0 NormalY=0 NormalZ=1 AngleXU=0 Radius=1.6 StartAngle=4.87196 EndAngle=6.44276
    g16: GeomPoint [constr] X=-183.704 Y=11.7019 Z=0
  constraints (43):
    c: Tangent(g1,g0) = -1.5708
    c: Distance(g0) = 2.7
    c: Equal(g1,g0)
    c: Tangent(g1,g-5)
    c: Coincident(g2,g0)
    c: Coincident(g3,g0)
    c: Distance(g2) = 1.1
    c: Equal(g3,g2)
    c: PointOnObject(g3,g2)
    c: Coincident(g4,g2)
    c: Coincident(g5,g3)
    c: Distance(g4) = 2.2
    c: Equal(g4,g5)
    c: Perpendicular(g1,g4)
    c: Perpendicular(g0,g5)
    c: Coincident(g6,g5)
    c: Coincident(g6,g4)
    c: Coincident(g7,g1)
    c: Coincident(g8,g0)
    c: Distance(g7) = 1.6
    c: Equal(g7,g8)
    c: Perpendicular(g1,g7)
    c: Perpendicular(g8,g0)
    c: Coincident(g9,g8)
    c: Coincident(g9,g7)
    c: Coincident(g10,g1)
    c: Coincident(g11,g0)
    c: Distance(g10,g16) = 3.8
    c: Perpendicular(g1,g10)
    c: Perpendicular(g1,g11)
    c: DistanceY(g0,g-4) = 3.8
    c: PointOnObject(g14,g12)
    c: PointOnObject(g14,g11)
    c: Tangent(g12,g13) = 1.5708
    c: Tangent(g11,g13) = 1.5708
    c: PointOnObject(g16,g12)
    c: PointOnObject(g16,g10)
    c: Tangent(g12,g15) = 1.5708
    c: Tangent(g10,g15) = -1.5708
    c: Equal(g13,g15)
    c: Coincident(g13,g5)
    c: Parallel(g2,g0)
    c: PointOnObject(g0,g-5)
FEATURE [Part::Extrusion] Extrude079  label="Extrude079 - fermi_nuovo_driver_alto"
  Base = -> Sketch139
  Dir = (0,-1,2e-16)
  DirMode = 2
  FaceMakerClass = Part::FaceMakerBullseye
  FaceMakerMode = 3
  LengthFwd = 25.2
  LengthRev = 0
  Solid = true
  Symmetric = true
FEATURE [Sketcher::SketchObject] Sketch140  label="scavo_diodo_nuovo_driver_alto"
  ArcFitTolerance = 1e-06
  AttachmentSupport = -> [XZ_Plane]
  ExternalGeometry = -> [Sketch138]
  FullyConstrained = true
  MakeInternals = false
  MapMode = 5
  Placement = pos=(0,0,0) rot=(1,0,0;1.5708rad)
  sketch-geometry (4):
    g0: LineSegment StartX=-190.79 StartY=17.5638 StartZ=0 EndX=-189.743 EndY=4.8067 EndZ=0
    g1: LineSegment StartX=-193.78 StartY=17.3185 StartZ=0 EndX=-192.733 EndY=4.56137 EndZ=0
    g2: LineSegment StartX=-190.79 StartY=17.5638 StartZ=0 EndX=-193.78 EndY=17.3185 EndZ=0
    g3: LineSegment StartX=-192.733 StartY=4.56137 StartZ=0 EndX=-189.743 EndY=4.8067 EndZ=0
  constraints (11):
    c: Equal(g0,g-3)
    c: Parallel(g0,g-3)
    c: Equal(g1,g-3)
    c: Parallel(g1,g-3)
    c: Coincident(g2,g0)
    c: Distance(g2) = 3
    c: Perpendicular(g0,g2)
    c: Coincident(g1,g2)
    c: Coincident(g3,g1)
    c: Coincident(g3,g0)
    c: Coincident(g0,g-3)
FEATURE [Part::Extrusion] Extrude080  label="Extrude080 - scavo_diodo_nuovo_driver_alto"
  Base = -> Sketch140
  Dir = (0,-1,2e-16)
  DirMode = 2
  FaceMakerClass = Part::FaceMakerBullseye
  FaceMakerMode = 3
  LengthFwd = 4
  LengthRev = 0
  Placement = pos=(0,7.8,0) rot=(0,0,1;0rad)
  Solid = true
  Symmetric = false
FEATURE [Part::MultiFuse] Fusion001
  Refine = true
  Shapes = -> [Cut043,Extrude079]
FEATURE [Part::Cut] Cut044
  Base = -> Fusion001
  Refine = true
  Tool = -> Extrude078
FEATURE [Part::Cut] Cut045
  Base = -> Cut044
  Refine = true
  Tool = -> Extrude080
FEATURE [Sketcher::SketchObject] Sketch141  label="fermi_nuovo_driver"
  ArcFitTolerance = 1e-06
  AttachmentSupport = -> [XZ_Plane]
  ExternalGeometry = -> [Sketch,Sketch137]
  FullyConstrained = true
  MakeInternals = false
  MapMode = 5
  Placement = pos=(0,0,0) rot=(1,0,0;1.5708rad)
  sketch-geometry (16):
    g0: LineSegment [constr] StartX=-165.477 StartY=-47.2177 StartZ=0 EndX=-167.759 EndY=-46.4761 EndZ=0
    g1: LineSegment [constr] StartX=-167.759 StartY=-46.4761 StartZ=0 EndX=-168.006 EndY=-47.2369 EndZ=0
    g2: LineSegment [constr] StartX=-168.006 StartY=-47.2369 StartZ=0 EndX=-169.675 EndY=-52.3726 EndZ=0
    g3: LineSegment StartX=-169.675 StartY=-52.3726 StartZ=0 EndX=-171.767 EndY=-51.6928 EndZ=0
    g4: LineSegment StartX=-172.795 StartY=-49.6767 StartZ=0 EndX=-172.115 EndY=-47.5843 EndZ=0
    g5: LineSegment StartX=-170.099 StartY=-46.5571 StartZ=0 EndX=-166.485 EndY=-47.7313 EndZ=0
    g6: LineSegment StartX=-166.485 StartY=-47.7313 StartZ=0 EndX=-168.153 EndY=-52.867 EndZ=0
    g7: LineSegment StartX=-169.675 StartY=-52.3726 StartZ=0 EndX=-168.153 EndY=-52.867 EndZ=0
    g8: LineSegment StartX=-170.593 StartY=-48.0788 StartZ=0 EndX=-171.273 EndY=-50.1711 EndZ=0
    g9: LineSegment StartX=-171.273 StartY=-50.1711 StartZ=0 EndX=-169.181 EndY=-50.8509 EndZ=0
    g10: LineSegment StartX=-169.181 StartY=-50.8509 StartZ=0 EndX=-168.501 EndY=-48.7586 EndZ=0
    g11: LineSegment StartX=-168.501 StartY=-48.7586 StartZ=0 EndX=-170.593 EndY=-48.0788 EndZ=0
    g12: ArcOfCircle CenterX=-170.593 CenterY=-48.0788 CenterZ=0 NormalX=0 NormalY=0 NormalZ=1 AngleXU=0 Radius=1.6 StartAngle=1.25664 EndAngle=2.82743
    g13: GeomPoint [constr] X=-171.62 Y=-46.0626 Z=0
    g14: ArcOfCircle CenterX=-171.273 CenterY=-50.1711 CenterZ=0 NormalX=0 NormalY=0 NormalZ=1 AngleXU=0 Radius=1.6 StartAngle=2.82743 EndAngle=4.39823
    g15: GeomPoint [constr] X=-173.289 Y=-51.1984 Z=0
  constraints (41):
    c: Coincident(g0,g-4)
    c: PointOnObject(g0,g-3)
    c: Parallel(g0,g-4)
    c: Coincident(g1,g0)
    c: Parallel(g1,g-3)
    c: Distance(g1) = 0.8
    c: Coincident(g2,g1)
    c: Distance(g2) = 5.4
    c: Coincident(g3,g2)
    c: Parallel(g2,g-3)
    c: Distance(g15,g13) = 5.4
    c: Perpendicular(g3,g2)
    c: Parallel(g4,g2)
    c: Distance(g5,g13) = 5.4
    c: Distance(g3,g15) = 3.8
    c: Perpendicular(g4,g5)
    c: Coincident(g6,g5)
    c: Distance(g6) = 5.4
    c: Parallel(g6,g4)
    c: Coincident(g7,g2)
    c: Coincident(g7,g6)
    c: Coincident(g8,g9)
    c: Coincident(g9,g10)
    c: Coincident(g10,g11)
    c: Coincident(g11,g8)
    c: Distance(g8,g10) = 2.2
    c: Distance(g9,g11) = 2.2
    c: Perpendicular(g11,g8)
    c: Equal(g8,g10)
    c: Equal(g11,g9)
    c: Tangent(g10,g2)
    c: Distance(g10,g1) = 1.6
    c: PointOnObject(g13,g4)
    c: PointOnObject(g13,g5)
    c: Tangent(g4,g12) = 1.5708
    c: Tangent(g5,g12) = 1.5708
    c: PointOnObject(g15,g4)
    c: Tangent(g4,g14) = 1.5708
    c: Tangent(g3,g14) = 1.5708
    c: Equal(g14,g12)
    c: Coincident(g12,g8)
FEATURE [Part::Extrusion] Extrude081  label="Extrude081 - fermi_nuovo_driver"
  Base = -> Sketch141
  Dir = (0,-1,2e-16)
  DirMode = 2
  FaceMakerClass = Part::FaceMakerBullseye
  FaceMakerMode = 3
  LengthFwd = 25.2
  LengthRev = 0
  Solid = true
  Symmetric = true
FEATURE [Part::MultiFuse] Fusion002
  Refine = true
  Shapes = -> [Cut045,Extrude081]
FEATURE [Part::Cut] Cut046
  Base = -> Fusion002
  Refine = true
  Tool = -> Extrude077
FEATURE [Sketcher::SketchObject] Sketch142  label="fermi_rele"
  ArcFitTolerance = 1e-06
  AttachmentSupport = -> [XZ_Plane]
  ExternalGeometry = -> [Sketch,Sketch136]
  FullyConstrained = true
  MakeInternals = false
  MapMode = 5
  Placement = pos=(0,0,0) rot=(1,0,0;1.5708rad)
  sketch-geometry (15):
    g0: LineSegment StartX=-177.245 StartY=-63.3719 StartZ=0 EndX=-177.924 EndY=-65.4642 EndZ=0
    g1: LineSegment StartX=-175.228 StartY=-62.3446 StartZ=0 EndX=-171.614 EndY=-63.5189 EndZ=0
    g2: LineSegment StartX=-171.614 StartY=-63.5189 StartZ=0 EndX=-173.283 EndY=-68.6546 EndZ=0
    g3: LineSegment StartX=-176.897 StartY=-67.4803 StartZ=0 EndX=-173.283 EndY=-68.6546 EndZ=0
    g4: LineSegment StartX=-175.723 StartY=-63.8663 StartZ=0 EndX=-173.631 EndY=-64.5461 EndZ=0
    g5: LineSegment StartX=-175.723 StartY=-63.8663 StartZ=0 EndX=-176.403 EndY=-65.9586 EndZ=0
    g6: LineSegment StartX=-173.631 StartY=-64.5461 StartZ=0 EndX=-174.31 EndY=-66.6385 EndZ=0
    g7: LineSegment StartX=-176.403 StartY=-65.9586 StartZ=0 EndX=-174.31 EndY=-66.6385 EndZ=0
    g8: LineSegment [constr] StartX=-173.631 StartY=-64.5461 StartZ=0 EndX=-173.136 EndY=-63.0245 EndZ=0
    g9: LineSegment [constr] StartX=-173.631 StartY=-64.5461 StartZ=0 EndX=-172.109 EndY=-65.0406 EndZ=0
    g10: LineSegment [constr] StartX=-170.35 StartY=-63.5093 StartZ=0 EndX=-173.013 EndY=-62.644 EndZ=0
    g11: ArcOfCircle CenterX=-175.723 CenterY=-63.8663 CenterZ=0 NormalX=0 NormalY=0 NormalZ=1 AngleXU=0 Radius=1.6 StartAngle=1.25664 EndAngle=2.82743
    g12: GeomPoint [constr] X=-176.75 Y=-61.8502 Z=0
    g13: ArcOfCircle CenterX=-176.403 CenterY=-65.9586 CenterZ=0 NormalX=0 NormalY=0 NormalZ=1 AngleXU=0 Radius=1.6 StartAngle=2.82743 EndAngle=4.39823
    g14: GeomPoint [constr] X=-178.419 Y=-66.9859 Z=0
  constraints (39):
    c: Distance(g14,g12) = 5.4
    c: Distance(g1,g12) = 5.4
    c: Perpendicular(g1,g0)
    c: Coincident(g2,g1)
    c: Parallel(g2,g0)
    c: Coincident(g3,g2)
    c: Parallel(g2,g-3)
    c: Coincident(g5,g4)
    c: Distance(g5) = 2.2
    c: Distance(g4) = 2.2
    c: Perpendicular(g4,g5)
    c: Coincident(g6,g4)
    c: Equal(g6,g5)
    c: Parallel(g6,g5)
    c: Coincident(g7,g5)
    c: Coincident(g7,g6)
    c: Coincident(g8,g4)
    c: Coincident(g9,g4)
    c: Distance(g8) = 1.6
    c: Distance(g9) = 1.6
    c: Parallel(g8,g6)
    c: Parallel(g9,g4)
    c: PointOnObject(g8,g1)
    c: PointOnObject(g9,g2)
    c: Coincident(g10,g-4)
    c: Parallel(g10,g-4)
    c: PointOnObject(g10,g-3)
    c: Tangent(g6,g-3) = 1.5708
    c: Distance(g4,g10) = 2
    c: PointOnObject(g12,g1)
    c: Tangent(g1,g11) = 1.5708
    c: Tangent(g0,g11) = -1.5708
    c: PointOnObject(g14,g3)
    c: PointOnObject(g14,g0)
    c: Tangent(g3,g13) = -1.5708
    c: Tangent(g0,g13) = -1.5708
    c: Equal(g11,g13)
    c: Coincident(g11,g4)
    c: Parallel(g3,g1)
FEATURE [Part::Extrusion] Extrude082  label="Extrude082 - fermi_rele"
  Base = -> Sketch142
  Dir = (0,-1,2e-16)
  DirMode = 2
  FaceMakerClass = Part::FaceMakerBullseye
  FaceMakerMode = 3
  LengthFwd = 25.2
  LengthRev = 0
  Solid = true
  Symmetric = true
FEATURE [Part::MultiFuse] Fusion003
  Refine = true
  Shapes = -> [Cut046,Extrude082]
FEATURE [Part::Cut] Cut047
  Base = -> Fusion003
  Refine = true
  Tool = -> Extrude076
FEATURE [Sketcher::SketchObject] Sketch143  label="foro_passaggio_cavi_led_batteria"
  ArcFitTolerance = 1e-06
  AttachmentSupport = -> [XZ_Plane]
  ExternalGeometry = -> [Sketch,Sketch042,Sketch036]
  FullyConstrained = true
  MakeInternals = false
  MapMode = 5
  Placement = pos=(0,0,0) rot=(1,0,0;1.5708rad)
  sketch-geometry (4):
    g0: LineSegment StartX=-207.775 StartY=-41.3701 StartZ=0 EndX=-213.607 EndY=-53.8767 EndZ=0
    g1: LineSegment StartX=-213.607 StartY=-53.8767 StartZ=0 EndX=-211.843 EndY=-59.5559 EndZ=0
    g2: LineSegment StartX=-207.775 StartY=-41.3701 StartZ=0 EndX=-207.775 EndY=-50.8316 EndZ=0
    g3: LineSegment StartX=-207.775 StartY=-50.8316 StartZ=0 EndX=-211.843 EndY=-59.5559 EndZ=0
  constraints (9):
    c: Coincident(g0,g-3)
    c: PointOnObject(g1,g-6)
    c: Coincident(g1,g0)
    c: Coincident(g2,g0)
    c: Coincident(g2,g-7)
    c: Coincident(g3,g2)
    c: Parallel(g3,g0)
    c: Coincident(g3,g1)
    c: Coincident(g0,g-5)
FEATURE [Part::Extrusion] Extrude083  label="Extrude083 - foro_passaggio_cavi_led_batteria"
  Base = -> Sketch143
  Dir = (0,-1,2e-16)
  DirMode = 2
  FaceMakerClass = Part::FaceMakerBullseye
  FaceMakerMode = 3
  LengthFwd = 6
  LengthRev = 0
  Solid = true
  Symmetric = true
FEATURE [Part::Cut] Cut048
  Base = -> Cut047
  Refine = true
  Tool = -> Extrude083
FEATURE [Sketcher::SketchObject] Sketch144  label="foro_areazione_alimentatore"
  ArcFitTolerance = 1e-06
  AttachmentSupport = -> [XZ_Plane]
  ExternalGeometry = -> [Sketch036]
  FullyConstrained = true
  MakeInternals = false
  MapMode = 5
  Placement = pos=(0,0,0) rot=(1,0,0;1.5708rad)
  sketch-geometry (4):
    g0: LineSegment StartX=-211.843 StartY=-60.3701 StartZ=0 EndX=-207.775 EndY=-60.3701 EndZ=0
    g1: LineSegment StartX=-207.775 StartY=-60.3701 StartZ=0 EndX=-207.775 EndY=-70.3701 EndZ=0
    g2: LineSegment StartX=-211.843 StartY=-60.3701 StartZ=0 EndX=-211.843 EndY=-70.3701 EndZ=0
    g3: LineSegment StartX=-207.775 StartY=-70.3701 StartZ=0 EndX=-211.843 EndY=-70.3701 EndZ=0
  constraints (11):
    c: Horizontal(g0)
    c: Distance(g1) = 10
    c: Coincident(g1,g0)
    c: Tangent(g1,g-3)
    c: PointOnObject(g0,g-4)
    c: Coincident(g2,g0)
    c: PointOnObject(g2,g-4)
    c: Coincident(g3,g1)
    c: Horizontal(g3)
    c: Coincident(g3,g2)
    c: DistanceY(g0,g-3) = 19
FEATURE [Part::Extrusion] Extrude084  label="Extrude084 - foro_areazione_alimentatore"
  Base = -> Sketch144
  Dir = (0,-1,2e-16)
  DirMode = 2
  FaceMakerClass = Part::FaceMakerBullseye
  FaceMakerMode = 3
  LengthFwd = 10
  LengthRev = 0
  Solid = true
  Symmetric = true
FEATURE [Part::Cut] Cut049
  Base = -> Cut048
  Refine = true
  Tool = -> Extrude084
FEATURE [Sketcher::SketchObject] Sketch145  label="foro_per_condesatore"
  ArcFitTolerance = 1e-06
  AttachmentSupport = -> [XZ_Plane]
  ExternalGeometry = -> [Sketch,Sketch139]
  FullyConstrained = true
  MakeInternals = false
  MapMode = 5
  Placement = pos=(0,0,0) rot=(1,0,0;1.5708rad)
  sketch-geometry (1):
    g0: Circle CenterX=-182.345 CenterY=7.02342 CenterZ=0 NormalX=0 NormalY=0 NormalZ=1 AngleXU=0 Radius=5.2
  constraints (3):
    c: Diameter(g0) = 10.4
    c: Tangent(g0,g-3)
    c: Tangent(g0,g-4)
FEATURE [Part::Extrusion] Extrude085  label="Extrude085 - foro_per_condesatore"
  Base = -> Sketch145
  Dir = (0,-1,2e-16)
  DirMode = 2
  FaceMakerClass = Part::FaceMakerBullseye
  FaceMakerMode = 3
  LengthFwd = 25.2
  LengthRev = 0
  Solid = true
  Symmetric = true
FEATURE [Part::Cut] Cut050
  Base = -> Cut049
  Refine = true
  Tool = -> Extrude085
FEATURE [Sketcher::SketchObject] Sketch146  label="scavo_pulsante_6x6_per_led_batteria"
  ArcFitTolerance = 1e-06
  AttachmentSupport = -> [XZ_Plane]
  ExternalGeometry = -> [Sketch016]
  FullyConstrained = true
  MakeInternals = false
  MapMode = 5
  Placement = pos=(0,0,0) rot=(1,0,0;1.5708rad)
  sketch-geometry (5):
    g0: LineSegment StartX=-216.643 StartY=-65.8316 StartZ=0 EndX=-216.643 EndY=-72.8316 EndZ=0
    g1: LineSegment StartX=-216.643 StartY=-72.8316 StartZ=0 EndX=-210.243 EndY=-72.8316 EndZ=0
    g2: LineSegment StartX=-210.243 StartY=-72.8316 StartZ=0 EndX=-210.243 EndY=-65.8316 EndZ=0
    g3: LineSegment StartX=-210.243 StartY=-65.8316 StartZ=0 EndX=-216.643 EndY=-65.8316 EndZ=0
    g4: GeomPoint [constr] X=-213.443 Y=-69.3316 Z=0
  constraints (13):
    c: Coincident(g0,g1)
    c: Coincident(g1,g2)
    c: Coincident(g2,g3)
    c: Coincident(g3,g0)
    c: Vertical(g0)
    c: Vertical(g2)
    c: Horizontal(g1)
    c: Horizontal(g3)
    c: Distance(g0,g2) = 6.4
    c: Distance(g1,g3) = 7
    c: Tangent(g1,g-3)
    c: Symmetric(g0,g2,g4)
    c: Vertical(g-3,g4)
FEATURE [Part::Extrusion] Extrude086  label="Extrude086 - scavo_pulsante_6x6_per_led_batteria"
  Base = -> Sketch146
  Dir = (0,-1,2e-16)
  DirMode = 2
  FaceMakerClass = Part::FaceMakerBullseye
  FaceMakerMode = 3
  LengthFwd = 4
  LengthRev = 0
  Placement = pos=(0,12.6,0) rot=(0,0,1;0rad)
  Solid = true
  Symmetric = false
FEATURE [Sketcher::SketchObject] Sketch147  label="scavo_led_stato_batteria"
  ArcFitTolerance = 1e-06
  AttachmentSupport = -> [XZ_Plane]
  ExternalGeometry = -> [Sketch016]
  FullyConstrained = true
  MakeInternals = false
  MapMode = 5
  Placement = pos=(0,0,0) rot=(1,0,0;1.5708rad)
  sketch-geometry (5):
    g0: LineSegment StartX=-215.843 StartY=-56.2316 StartZ=0 EndX=-215.843 EndY=-65.4316 EndZ=0
    g1: LineSegment StartX=-215.843 StartY=-65.4316 StartZ=0 EndX=-211.043 EndY=-65.4316 EndZ=0
    g2: LineSegment StartX=-211.043 StartY=-65.4316 StartZ=0 EndX=-211.043 EndY=-56.2316 EndZ=0
    g3: LineSegment StartX=-211.043 StartY=-56.2316 StartZ=0 EndX=-215.843 EndY=-56.2316 EndZ=0
    g4: GeomPoint [constr] X=-213.443 Y=-60.8316 Z=0
  constraints (13):
    c: Coincident(g0,g1)
    c: Coincident(g1,g2)
    c: Coincident(g2,g3)
    c: Coincident(g3,g0)
    c: Distance(g0,g2) = 4.8
    c: Distance(g1,g3) = 9.2
    c: Equal(g0,g2)
    c: Equal(g1,g3)
    c: Perpendicular(g3,g0)
    c: DistanceY(g-3,g0) = 11.4
    c: Vertical(g2)
    c: Symmetric(g0,g2,g4)
    c: Vertical(g4,g-3)
FEATURE [Part::Extrusion] Extrude087  label="Extrude087 - scavo_led_stato_batteria"
  Base = -> Sketch147
  Dir = (0,-1,2e-16)
  DirMode = 2
  FaceMakerClass = Part::FaceMakerBullseye
  FaceMakerMode = 3
  LengthFwd = 2.2
  LengthRev = 0
  Placement = pos=(0,12.6,0) rot=(0,0,1;0rad)
  Solid = true
  Symmetric = false
FEATURE [Sketcher::SketchObject] Sketch148
  ArcFitTolerance = 1e-06
  AttachmentSupport = -> [Pad016]
  ExternalGeometry = -> [Pad016]
  FullyConstrained = true
  MakeInternals = false
  MapMode = 5
  Placement = pos=(0,0,-80.4316) rot=(1,0,0;3.14159rad)
  sketch-geometry (8):
    g0: LineSegment StartX=-176.685 StartY=3.6 StartZ=0 EndX=-186.685 EndY=3.6 EndZ=0
    g1: LineSegment StartX=-176.685 StartY=3.6 StartZ=0 EndX=-176.685 EndY=-9e-16 EndZ=0
    g2: LineSegment [constr] StartX=-186.685 StartY=3.6 StartZ=0 EndX=-186.685 EndY=-9e-16 EndZ=0
    g3: ArcOfEllipse CenterX=-186.685 CenterY=-9e-16 CenterZ=0 NormalX=0 NormalY=0 NormalZ=1 MajorRadius=10 MinorRadius=3.6 AngleXU=0 StartAngle=0 EndAngle=1.5708
    g4: LineSegment [constr] StartX=-176.685 StartY=-1e-15 StartZ=0 EndX=-196.685 EndY=-1e-15 EndZ=0
    g5: LineSegment [constr] StartX=-186.685 StartY=3.6 StartZ=0 EndX=-186.685 EndY=-3.6 EndZ=0
    g6: GeomPoint [constr] X=-177.356 Y=-1e-15 Z=0
    g7: GeomPoint [constr] X=-196.015 Y=-1e-15 Z=0
  constraints (13):
    c: Distance(g0) = 10
    c: Coincident(g0,g-5)
    c: PointOnObject(g0,g-3)
    c: Coincident(g1,g0)
    c: Coincident(g1,g-5)
    c: Coincident(g2,g0)
    c: Vertical(g2)
    c: PointOnObject(g2,g-4)
    c: InternalAlignment(g4-g7 -> g3) x4
    c: Coincident(g3,g2)
    c: Coincident(g3,g0)
    c: Coincident(g3,g1)
    c: Horizontal(g4)
FEATURE [PartDesign::SubtractivePipe] SubtractivePipe004
  AuxilleryCurvelinear = true
  AuxillerySpineTangent = false
  BaseFeature = -> Pad016
  Binormal = (0,0,0)
  Mode = 0
  Profile = -> Sketch148
  Refine = true
  Spine = -> Pad016 [Edge253]
  SpineTangent = false
  Suppressed = false
  Transformation = 0
  Transition = 0
FEATURE [Sketcher::SketchObject] Sketch149
  ArcFitTolerance = 1e-06
  AttachmentSupport = -> [Pad016]
  ExternalGeometry = -> [Pad016]
  FullyConstrained = true
  MakeInternals = false
  MapMode = 5
  Placement = pos=(0,0,-80.4316) rot=(1,0,0;3.14159rad)
  sketch-geometry (8):
    g0: LineSegment StartX=-215.932 StartY=3.6 StartZ=0 EndX=-205.932 EndY=3.6 EndZ=0
    g1: LineSegment StartX=-215.932 StartY=3.6 StartZ=0 EndX=-215.932 EndY=-4e-16 EndZ=0
    g2: LineSegment [constr] StartX=-205.932 StartY=3.6 StartZ=0 EndX=-205.932 EndY=-9e-16 EndZ=0
    g3: ArcOfEllipse CenterX=-205.932 CenterY=-1e-15 CenterZ=0 NormalX=0 NormalY=0 NormalZ=1 MajorRadius=10 MinorRadius=3.6 AngleXU=-3.14159 StartAngle=4.71239 EndAngle=6.28319
    g4: LineSegment [constr] StartX=-215.932 StartY=-1e-15 StartZ=0 EndX=-195.932 EndY=-1e-15 EndZ=0
    g5: LineSegment [constr] StartX=-205.932 StartY=-3.6 StartZ=0 EndX=-205.932 EndY=3.6 EndZ=0
    g6: GeomPoint [constr] X=-215.262 Y=-2.1e-15 Z=0
    g7: GeomPoint [constr] X=-196.602 Y=-9e-16 Z=0
  constraints (13):
    c: Distance(g0) = 10
    c: Coincident(g0,g-5)
    c: PointOnObject(g0,g-5)
    c: Coincident(g1,g0)
    c: Coincident(g1,g-4)
    c: Coincident(g2,g0)
    c: Vertical(g2)
    c: PointOnObject(g2,g-3)
    c: InternalAlignment(g4-g7 -> g3) x4
    c: Coincident(g3,g2)
    c: Coincident(g3,g0)
    c: Coincident(g3,g1)
    c: Horizontal(g4)
FEATURE [PartDesign::SubtractivePipe] SubtractivePipe005
  AuxilleryCurvelinear = true
  AuxillerySpineTangent = false
  BaseFeature = -> SubtractivePipe004
  Binormal = (0,0,0)
  Mode = 0
  Profile = -> Sketch149
  Refine = true
  Spine = -> Pad016 [Edge251,Edge256,Edge255]
  SpineTangent = false
  Suppressed = false
  Transformation = 0
  Transition = 0
FEATURE [PartDesign::SubtractiveLoft] SubtractiveLoft002
  BaseFeature = -> SubtractivePipe005
  Closed = false
  Profile = -> Sketch129
  Refine = true
  Ruled = false
  Sections = -> [Sketch130]
  Suppressed = false
FEATURE [PartDesign::SubtractiveLoft] SubtractiveLoft003
  BaseFeature = -> SubtractiveLoft002
  Closed = false
  Profile = -> Clone2D001
  Refine = true
  Ruled = false
  Sections = -> [Sketch131]
  Suppressed = false
FEATURE [PartDesign::Chamfer] Chamfer010
  Angle = 45
  Base = -> SubtractiveLoft003 [Edge203,Edge204,Edge202,Edge201,Edge195]
  BaseFeature = -> SubtractiveLoft003
  ChamferType = 0
  FlipDirection = false
  Refine = true
  Size = 1.5
  Size2 = 1
  SupportTransform = false
  Suppressed = false
  UseAllEdges = false
FEATURE [PartDesign::Chamfer] Chamfer011
  Angle = 45
  Base = -> Chamfer010 [Edge15]
  BaseFeature = -> Chamfer010
  ChamferType = 0
  FlipDirection = false
  Refine = true
  Size = 1.6
  Size2 = 1
  SupportTransform = false
  Suppressed = false
  UseAllEdges = false
FEATURE [PartDesign::Chamfer] Chamfer012
  Angle = 45
  Base = -> Chamfer011 [Edge10]
  BaseFeature = -> Chamfer011
  ChamferType = 0
  FlipDirection = false
  Refine = true
  Size = 3.5
  Size2 = 1
  SupportTransform = false
  Suppressed = false
  UseAllEdges = false
FEATURE [PartDesign::Chamfer] Chamfer013
  Angle = 45
  Base = -> Chamfer012 [Edge94]
  BaseFeature = -> Chamfer012
  ChamferType = 0
  FlipDirection = false
  Refine = true
  Size = 1.9
  Size2 = 1
  SupportTransform = false
  Suppressed = false
  UseAllEdges = false
FEATURE [PartDesign::Fillet] Fillet007
  Base = -> Chamfer013 [Edge83]
  BaseFeature = -> Chamfer013
  Radius = 1.1
  Refine = true
  SupportTransform = false
  Suppressed = false
  UseAllEdges = false
FEATURE [PartDesign::Fillet] Fillet008
  Base = -> Fillet007 [Edge75]
  BaseFeature = -> Fillet007
  Radius = 1.9
  Refine = true
  SupportTransform = false
  Suppressed = false
  UseAllEdges = false
FEATURE [PartDesign::Pocket] Pocket011
  BaseFeature = -> Fillet008
  Direction = (0,1,-2e-16)
  Length = 0.8
  Length2 = 5
  Profile = -> Sketch132
  ReferenceAxis = -> Sketch132 [N_Axis]
  Refine = true
  Suppressed = false
  Type = 0
FEATURE [PartDesign::Pocket] Pocket012
  BaseFeature = -> Pocket011
  Direction = (0,1,0)
  Length = 1
  Length2 = 5
  Profile = -> ShapeString
  ReferenceAxis = -> ShapeString [N_Axis]
  Refine = true
  Suppressed = false
  Type = 0
FEATURE [Sketcher::SketchObject] Sketch150
  ArcFitTolerance = 1e-06
  AttachmentSupport = -> [Pad008]
  ExternalGeometry = -> [Pad008]
  FullyConstrained = true
  MakeInternals = false
  MapMode = 5
  Placement = pos=(0,3.6,0) rot=(0,0.707107,0.707107;3.14159rad)
  sketch-geometry (7):
    g0: LineSegment [constr] StartX=210.343 StartY=-66.0316 StartZ=0 EndX=210.343 EndY=-72.8316 EndZ=0
    g1: LineSegment [constr] StartX=210.343 StartY=-72.8316 StartZ=0 EndX=216.543 EndY=-72.8316 EndZ=0
    g2: LineSegment [constr] StartX=216.543 StartY=-72.8316 StartZ=0 EndX=216.543 EndY=-66.0316 EndZ=0
    g3: LineSegment [constr] StartX=216.543 StartY=-66.0316 StartZ=0 EndX=210.343 EndY=-66.0316 EndZ=0
    g4: LineSegment [constr] StartX=210.343 StartY=-72.8316 StartZ=0 EndX=216.543 EndY=-66.0316 EndZ=0
    g5: LineSegment [constr] StartX=210.343 StartY=-66.0316 StartZ=0 EndX=213.443 EndY=-69.4316 EndZ=0
    g6: Circle CenterX=213.443 CenterY=-69.4316 CenterZ=0 NormalX=0 NormalY=0 NormalZ=1 AngleXU=0 Radius=2
  constraints (18):
    c: Coincident(g0,g1)
    c: Coincident(g1,g2)
    c: Coincident(g2,g3)
    c: Coincident(g3,g0)
    c: Vertical(g0)
    c: Vertical(g2)
    c: Horizontal(g1)
    c: Horizontal(g3)
    c: Distance(g0,g2) = 6.2
    c: Distance(g1,g3) = 6.8
    c: DistanceY(g-3,g1) = 4
    c: Coincident(g4,g0)
    c: Coincident(g4,g2)
    c: Coincident(g5,g0)
    c: Symmetric(g0,g2,g5)
    c: Diameter(g6) = 4
    c: Coincident(g6,g5)
    c: Vertical(g5,g-3)
FEATURE [Sketcher::SketchObject] Sketch151
  ArcFitTolerance = 1e-06
  AttachmentSupport = -> [Pad008]
  ExternalGeometry = -> [Pad008]
  FullyConstrained = true
  MakeInternals = false
  MapMode = 5
  Placement = pos=(0,3.6,0) rot=(0,0.707107,0.707107;3.14159rad)
  sketch-geometry (10):
    g0: LineSegment [constr] StartX=211.143 StartY=-56.2316 StartZ=0 EndX=211.143 EndY=-65.4316 EndZ=0
    g1: LineSegment [constr] StartX=211.143 StartY=-65.4316 StartZ=0 EndX=215.743 EndY=-65.4316 EndZ=0
    g2: LineSegment [constr] StartX=215.743 StartY=-65.4316 StartZ=0 EndX=215.743 EndY=-56.2316 EndZ=0
    g3: LineSegment [constr] StartX=215.743 StartY=-56.2316 StartZ=0 EndX=211.143 EndY=-56.2316 EndZ=0
    g4: LineSegment StartX=212.243 StartY=-63.8316 StartZ=0 EndX=214.643 EndY=-63.8316 EndZ=0
    g5: LineSegment StartX=214.643 StartY=-63.8316 StartZ=0 EndX=214.643 EndY=-57.0316 EndZ=0
    g6: LineSegment StartX=214.643 StartY=-57.0316 StartZ=0 EndX=212.243 EndY=-57.0316 EndZ=0
    g7: LineSegment StartX=212.243 StartY=-57.0316 StartZ=0 EndX=212.243 EndY=-63.8316 EndZ=0
    g8: GeomPoint [constr] X=213.443 Y=-60.4316 Z=0
    g9: GeomPoint [constr] X=213.443 Y=-60.8316 Z=0
  constraints (26):
    c: Coincident(g0,g1)
    c: Coincident(g1,g2)
    c: Coincident(g2,g3)
    c: Coincident(g3,g0)
    c: Vertical(g0)
    c: Vertical(g2)
    c: Horizontal(g1)
    c: Horizontal(g3)
    c: Distance(g0,g2) = 4.6
    c: Distance(g1,g3) = 9.2
    c: DistanceY(g-3,g1) = 11.4
    c: Coincident(g4,g5)
    c: Coincident(g5,g6)
    c: Coincident(g6,g7)
    c: Coincident(g7,g4)
    c: Horizontal(g4)
    c: Horizontal(g6)
    c: Vertical(g5)
    c: Vertical(g7)
    c: Symmetric(g6,g4,g8)
    c: Distance(g5,g7) = 2.4
    c: Distance(g4,g6) = 6.8
    c: Symmetric(g2,g0,g9)
    c: Vertical(g8,g9)
    c: DistanceY(g1,g4) = 1.6
    c: Vertical(g9,g-3)
FEATURE [PartDesign::Pocket] Pocket019
  BaseFeature = -> Pocket013
  Direction = (0,-1,2e-16)
  Length = 3.6
  Length2 = 5
  Profile = -> Sketch151
  ReferenceAxis = -> Sketch151 [N_Axis]
  Refine = true
  Suppressed = false
  Type = 0
FEATURE [PartDesign::Pocket] Pocket018
  BaseFeature = -> Pocket019
  Direction = (0,-1,2e-16)
  Length = 3.6
  Length2 = 5
  Profile = -> Sketch150
  ReferenceAxis = -> Sketch150 [N_Axis]
  Refine = true
  Suppressed = false
  Type = 0
FEATURE [PartDesign::Point] DatumPoint
  AttacherType = Attacher::AttachEnginePoint
  AttachmentSupport = -> [Sketch150]
  MapMode = 36
  Placement = pos=(-213.443,3.6,-69.4316) rot=(0,1,0;3.14159rad)
FEATURE [PartDesign::Plane] DatumPlane002
  AttachmentSupport = -> [DatumPoint]
  Length = 265.655
  MapMode = 1
  Placement = pos=(-213.443,3.6,-69.4316) rot=(0,0,1;0rad)
  ResizeMode = 0
  Width = 72.0719
FEATURE [Sketcher::SketchObject] Sketch152
  ArcFitTolerance = 1e-06
  AttachmentSupport = -> [DatumPlane002]
  ExternalGeometry = -> [Sketch150]
  FullyConstrained = true
  MakeInternals = false
  MapMode = 5
  Placement = pos=(-213.443,3.6,-69.4316) rot=(0,0,1;0rad)
  sketch-geometry (7):
    g0: LineSegment StartX=0 StartY=0 StartZ=0 EndX=-4 EndY=3.8e-15 EndZ=0
    g1: ArcOfEllipse CenterX=0 CenterY=0 CenterZ=0 NormalX=0 NormalY=0 NormalZ=1 MajorRadius=4 MinorRadius=3.6 AngleXU=3.14159 StartAngle=2e-16 EndAngle=1.5708
    g2: LineSegment [constr] StartX=-4 StartY=9e-16 StartZ=0 EndX=4 EndY=-9e-16 EndZ=0
    g3: LineSegment [constr] StartX=0 StartY=-3.6 StartZ=0 EndX=0 EndY=3.6 EndZ=0
    g4: GeomPoint [constr] X=-1.74356 Y=2e-15 Z=0
    g5: GeomPoint [constr] X=1.74356 Y=-2e-15 Z=0
    g6: LineSegment StartX=0 StartY=0 StartZ=0 EndX=-4.4e-15 EndY=-3.6 EndZ=0
  constraints (11):
    c: PointOnObject(g1,g-2)
    c: Distance(g0) = 4
    c: PointOnObject(g0,g-1)
    c: InternalAlignment(g2-g5 -> g1) x4
    c: Coincident(g1,g0)
    c: Vertical(g3)
    c: Coincident(g1,g-1)
    c: Distance(g6) = 3.6
    c: Coincident(g6,g1)
    c: Coincident(g1,g6)
    c: Coincident(g0,g1)
FEATURE [PartDesign::Groove] Groove
  Angle = 360
  Angle2 = 60
  Axis = (0,1,0)
  Base = (-213.443,3.6,-69.4316)
  BaseFeature = -> Pocket018
  Profile = -> Sketch152
  ReferenceAxis = -> Sketch152 [V_Axis]
  Refine = true
  Reversed = true
  Suppressed = false
  Type = 0
FEATURE [PartDesign::Body] Body006  label="lato SX"
  AllowCompound = false
  Group = -> [Binder,Pad019,Chamfer015,Pocket002,Sketch133,Sketch091,Pad005,Sketch092,Pocket001,Sketch093,Sketch094,Pad006,Sketch095,Pad007,Sketch096,Pad008,Sketch097,Pad009,Chamfer005,Pocket004,Sketch098,Pad010,Chamfer006,Pocket003,SubtractivePipe,SubtractivePipe001,Sketch099,Sketch106,Sketch107,Sketch108,Clone2D,Sketch109,SubtractiveLoft,SubtractiveLoft001,Sketch110,Sketch111,Sketch112,Chamfer016,Chamfer017,+15 more]
  Origin = -> Origin006
  Tip = -> Groove
FEATURE [Sketcher::SketchObject] Sketch153  label="ripieno_per_sostegno_led_batteria"
  ArcFitTolerance = 1e-06
  AttachmentSupport = -> [XZ_Plane]
  ExternalGeometry = -> [Sketch036]
  FullyConstrained = true
  MakeInternals = false
  MapMode = 5
  Placement = pos=(0,0,0) rot=(1,0,0;1.5708rad)
  sketch-geometry (4):
    g0: LineSegment StartX=-217.343 StartY=-54.5944 StartZ=0 EndX=-217.343 EndY=-63.1944 EndZ=0
    g1: LineSegment StartX=-217.343 StartY=-63.1944 StartZ=0 EndX=-211.843 EndY=-63.1944 EndZ=0
    g2: LineSegment StartX=-211.843 StartY=-63.1944 StartZ=0 EndX=-211.843 EndY=-54.5944 EndZ=0
    g3: LineSegment StartX=-211.843 StartY=-54.5944 StartZ=0 EndX=-217.343 EndY=-54.5944 EndZ=0
  constraints (11):
    c: Coincident(g0,g1)
    c: Coincident(g1,g2)
    c: Coincident(g2,g3)
    c: Coincident(g3,g0)
    c: Vertical(g0)
    c: Horizontal(g1)
    c: Horizontal(g3)
    c: Tangent(g2,g-3)
    c: DistanceY(g2,g-3) = 4.5
    c: DistanceX(g3,g3) = 5.5
    c: DistanceY(g0,g0) = 8.6
FEATURE [PartDesign::Body] Body  label="Struttura pistola"
  AllowCompound = false
  Group = -> [Sketch,Sketch002,Sketch004,DatumPlane,Sketch005,DatumPlane001,CopyCut,Sketch008,Sketch009,Sketch010,Sketch011,Sketch012,Sketch013,Sketch014,Sketch015,Sketch016,Sketch017,Sketch018,Sketch019,Sketch020,Sketch022,Sketch023,Sketch024,Sketch025,Sketch026,Sketch027,Sketch029,Sketch030,Sketch031,Sketch032,Sketch033,Sketch034,Sketch035,Sketch036,Sketch037,Sketch038,Sketch039,Sketch040,Sketch041,Sketch042,+28 more]
  Origin = -> Origin
FEATURE [Part::Extrusion] Extrude088  label="Extrude088 - ripieno_per_sostegno_led_batteria"
  Base = -> Sketch153
  Dir = (0,-1,2e-16)
  DirMode = 2
  FaceMakerClass = Part::FaceMakerBullseye
  FaceMakerMode = 3
  LengthFwd = 4
  LengthRev = 0
  Placement = pos=(0,12.6,0) rot=(0,0,1;0rad)
  Solid = true
  Symmetric = false
FEATURE [Part::MultiFuse] Fusion004
  Refine = true
  Shapes = -> [Cut050,Extrude088]
FEATURE [Part::Cut] Cut051
  Base = -> Fusion004
  Refine = true
  Tool = -> Extrude087
FEATURE [Part::Cut] Cut052
  Base = -> Cut051
  Refine = true
  Tool = -> Extrude086
FEATURE [Sketcher::SketchObject] Sketch154
  ArcFitTolerance = 1e-06
  AttachmentSupport = -> [Pad016]
  ExternalGeometry = -> [Binder001]
  FullyConstrained = true
  MakeInternals = false
  MapMode = 5
  Placement = pos=(0,-3.6,0) rot=(1,0,0;1.5708rad)
  sketch-geometry (25):
    g0: LineSegment StartX=-214.643 StartY=-72.4316 StartZ=0 EndX=-212.243 EndY=-72.4316 EndZ=0
    g1: LineSegment StartX=-212.243 StartY=-72.4316 StartZ=0 EndX=-212.243 EndY=-71.2316 EndZ=0
    g2: LineSegment StartX=-212.243 StartY=-71.2316 StartZ=0 EndX=-214.643 EndY=-71.2316 EndZ=0
    g3: LineSegment StartX=-214.643 StartY=-71.2316 StartZ=0 EndX=-214.643 EndY=-72.4316 EndZ=0
    g4: GeomPoint [constr] X=-213.443 Y=-71.8316 Z=0
    g5: LineSegment StartX=-214.643 StartY=-69.6316 StartZ=0 EndX=-212.243 EndY=-69.6316 EndZ=0
    g6: LineSegment StartX=-212.243 StartY=-69.6316 StartZ=0 EndX=-212.243 EndY=-68.4316 EndZ=0
    g7: LineSegment StartX=-212.243 StartY=-68.4316 StartZ=0 EndX=-214.643 EndY=-68.4316 EndZ=0
    g8: LineSegment StartX=-214.643 StartY=-68.4316 StartZ=0 EndX=-214.643 EndY=-69.6316 EndZ=0
    g9: GeomPoint [constr] X=-213.443 Y=-69.0316 Z=0
    g10: LineSegment StartX=-214.643 StartY=-66.8316 StartZ=0 EndX=-212.243 EndY=-66.8316 EndZ=0
    g11: LineSegment StartX=-212.243 StartY=-66.8316 StartZ=0 EndX=-212.243 EndY=-65.6316 EndZ=0
    g12: LineSegment StartX=-212.243 StartY=-65.6316 StartZ=0 EndX=-214.643 EndY=-65.6316 EndZ=0
    g13: LineSegment StartX=-214.643 StartY=-65.6316 StartZ=0 EndX=-214.643 EndY=-66.8316 EndZ=0
    g14: GeomPoint [constr] X=-213.443 Y=-66.2316 Z=0
    g15: LineSegment StartX=-214.643 StartY=-64.0316 StartZ=0 EndX=-212.243 EndY=-64.0316 EndZ=0
    g16: LineSegment StartX=-212.243 StartY=-64.0316 StartZ=0 EndX=-212.243 EndY=-62.8316 EndZ=0
    g17: LineSegment StartX=-212.243 StartY=-62.8316 StartZ=0 EndX=-214.643 EndY=-62.8316 EndZ=0
    g18: LineSegment StartX=-214.643 StartY=-62.8316 StartZ=0 EndX=-214.643 EndY=-64.0316 EndZ=0
    g19: GeomPoint [constr] X=-213.443 Y=-63.4316 Z=0
    g20: LineSegment StartX=-214.643 StartY=-61.2316 StartZ=0 EndX=-212.243 EndY=-61.2316 EndZ=0
    g21: LineSegment StartX=-212.243 StartY=-61.2316 StartZ=0 EndX=-212.243 EndY=-60.0316 EndZ=0
    g22: LineSegment StartX=-212.243 StartY=-60.0316 StartZ=0 EndX=-214.643 EndY=-60.0316 EndZ=0
    g23: LineSegment StartX=-214.643 StartY=-60.0316 StartZ=0 EndX=-214.643 EndY=-61.2316 EndZ=0
    g24: GeomPoint [constr] X=-213.443 Y=-60.6316 Z=0
  constraints (65):
    c: Coincident(g0,g1)
    c: Coincident(g1,g2)
    c: Coincident(g2,g3)
    c: Coincident(g3,g0)
    c: Horizontal(g0)
    c: Horizontal(g2)
    c: Vertical(g1)
    c: Vertical(g3)
    c: Symmetric(g2,g0,g4)
    c: Distance(g1,g3) = 2.4
    c: Distance(g0,g2) = 1.2
    c: Coincident(g5,g6)
    c: Coincident(g6,g7)
    c: Coincident(g7,g8)
    c: Coincident(g8,g5)
    c: Horizontal(g5)
    c: Horizontal(g7)
    c: Vertical(g6)
    c: Vertical(g8)
    c: Symmetric(g7,g5,g9)
    c: Distance(g6,g8) = 2.4
    c: Distance(g5,g7) = 1.2
    c: Coincident(g10,g11)
    c: Coincident(g11,g12)
    c: Coincident(g12,g13)
    c: Coincident(g13,g10)
    c: Horizontal(g10)
    c: Horizontal(g12)
    c: Vertical(g11)
    c: Vertical(g13)
    c: Symmetric(g12,g10,g14)
    c: Distance(g11,g13) = 2.4
    c: Distance(g10,g12) = 1.2
    c: Coincident(g15,g16)
    c: Coincident(g16,g17)
    c: Coincident(g17,g18)
    c: Coincident(g18,g15)
    c: Horizontal(g15)
    c: Horizontal(g17)
    c: Vertical(g16)
    c: Vertical(g18)
    c: Symmetric(g17,g15,g19)
    c: Distance(g16,g18) = 2.4
    c: Distance(g15,g17) = 1.2
    c: Vertical(g4,g-3)
    c: Vertical(g9,g-3)
    c: Vertical(g14,g-3)
    c: Vertical(g19,g-3)
    c: DistanceY(g-3,g4) = 5
    c: DistanceY(g4,g9) = 2.8
    c: DistanceY(g9,g14) = 2.8
    c: DistanceY(g14,g19) = 2.8
    c: Coincident(g20,g21)
    c: Coincident(g21,g22)
    c: Coincident(g22,g23)
    c: Coincident(g23,g20)
    c: Horizontal(g20)
    c: Horizontal(g22)
    c: Vertical(g21)
    c: Vertical(g23)
    c: Symmetric(g22,g20,g24)
    c: Distance(g21,g23) = 2.4
    c: Distance(g20,g22) = 1.2
    c: DistanceY(g19,g24) = 2.8
    c: Vertical(g-3,g24)
FEATURE [PartDesign::Pocket] Pocket020
  BaseFeature = -> Pocket012
  Direction = (0,1,-2e-16)
  Length = 3.6
  Length2 = 5
  Profile = -> Sketch154
  ReferenceAxis = -> Sketch154 [N_Axis]
  Refine = true
  Suppressed = false
  Type = 0
FEATURE [PartDesign::Body] Body007  label="lato DX"
  AllowCompound = false
  Group = -> [Binder001,Sketch114,Pad011,Chamfer014,Sketch115,Pocket006,Sketch116,Pad012,Sketch117,Pocket007,Sketch118,Pad013,Sketch119,Pocket008,Pad017,Chamfer009,Pocket009,Sketch123,Sketch120,Pad014,Pad018,Chamfer008,Pocket010,Sketch121,Pad015,Sketch122,Pad016,SubtractivePipe004,SubtractivePipe005,Sketch149,Sketch148,Sketch124,Sketch125,Sketch126,Sketch129,Sketch130,Clone2D001,Sketch131,SubtractiveLoft002,+13 more]
  Origin = -> Origin007
  Tip = -> Pocket020
note: 2 file-system paths scrubbed to <path> (originals preserved in the JSON sidecar)
